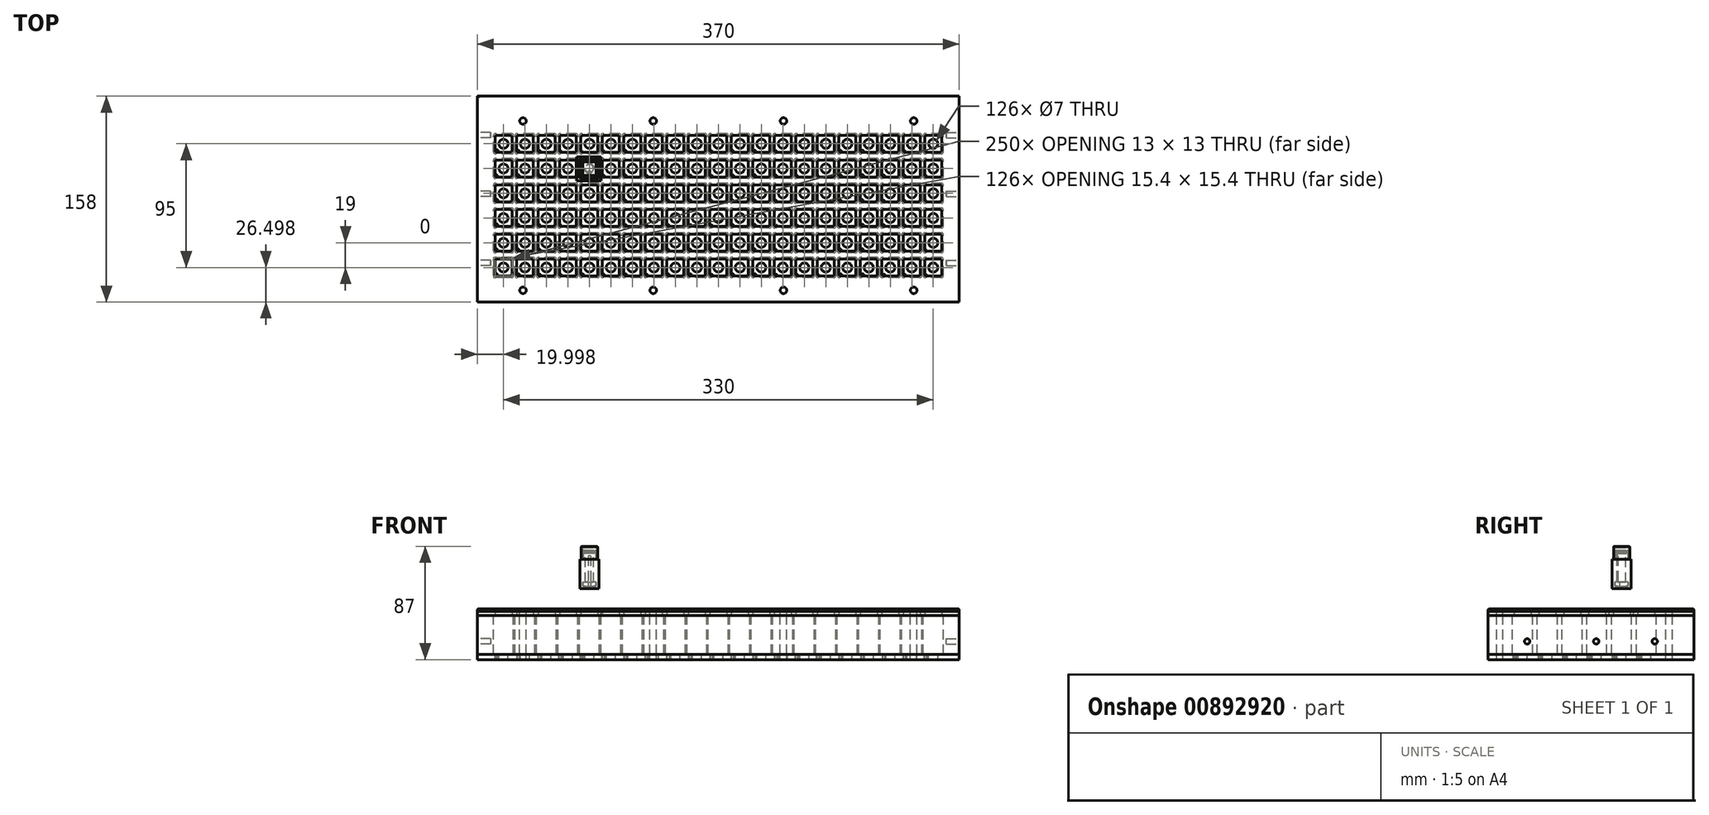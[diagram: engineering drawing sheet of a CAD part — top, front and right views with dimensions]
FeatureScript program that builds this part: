
annotation { "Feature Type Name" : "Feature", "Feature Type Description" : "" }
export const myFeature = defineFeature(function(context is Context, id is Id, definition is map)
    precondition{}
    {
        {
            var Q0;
            Q0=qCreatedBy(makeId("Top.planeOp"),FACE);
            var sketch = newSketch(context, id + "F0", { "sketchPlane" : qUnion([Q0])});
            skLineSegment(sketch, "E0.bottom", {"start": v(-181.07, -94.06) * mm, "end": v(188.93, -94.06) * mm});
            skLineSegment(sketch, "E0.top", {"start": v(-181.07, -252.06) * mm, "end": v(188.93, -252.06) * mm});
            skLineSegment(sketch, "E0.left", {"start": v(-181.07, -94.06) * mm, "end": v(-181.07, -252.06) * mm});
            skLineSegment(sketch, "E0.right", {"start": v(188.93, -94.06) * mm, "end": v(188.93, -252.06) * mm});
            skLineSegment(sketch, "E1.bottom", {"start": v(-167.57, -124.06) * mm, "end": v(175.43, -124.06) * mm, "construction": true});
            skLineSegment(sketch, "E1.top", {"start": v(-167.57, -232.06) * mm, "end": v(175.43, -232.06) * mm, "construction": true});
            skLineSegment(sketch, "E1.left", {"start": v(-167.57, -124.06) * mm, "end": v(-167.57, -232.06) * mm, "construction": true});
            skLineSegment(sketch, "E1.right", {"start": v(175.43, -124.06) * mm, "end": v(175.43, -232.06) * mm, "construction": true});
            skSolve(sketch);
        }
        {
            var Q0;
            Q0=makeQuery(id+"F0.imprint","IMPRINT",FACE,{"disambiguationData":[TD([[makeQuery(id+"F0.imprint","IMPRINT",EDGE,{"derivedFrom":sQuery(id+"F0.wireOp",EDGE,"E0.bottom")}),-1.0]])]});
            var sketch = newSketch(context, id + "F1", { "sketchPlane" : qUnion([Q0])});
            skLineSegment(sketch, "E2.bottom", {"start": v(-166.07, -124.06) * mm, "end": v(-156.07, -124.06) * mm});
            skLineSegment(sketch, "E2.top", {"start": v(-166.07, -137.06) * mm, "end": v(-156.07, -137.06) * mm});
            skLineSegment(sketch, "E2.left", {"start": v(-167.57, -125.56) * mm, "end": v(-167.57, -135.56) * mm});
            skLineSegment(sketch, "E2.right", {"start": v(-154.57, -125.56) * mm, "end": v(-154.57, -135.56) * mm});
            skLineSegment(sketch, "E3.bottom", {"start": v(-166.07, -219.06) * mm, "end": v(-156.07, -219.06) * mm});
            skLineSegment(sketch, "E3.top", {"start": v(-166.07, -232.06) * mm, "end": v(-156.07, -232.06) * mm});
            skLineSegment(sketch, "E3.left", {"start": v(-167.57, -220.56) * mm, "end": v(-167.57, -230.56) * mm});
            skLineSegment(sketch, "E3.right", {"start": v(-154.57, -220.56) * mm, "end": v(-154.57, -230.56) * mm});
            skLineSegment(sketch, "E4.bottom", {"start": v(-166.07, -200.06) * mm, "end": v(-156.07, -200.06) * mm});
            skLineSegment(sketch, "E4.top", {"start": v(-166.07, -213.06) * mm, "end": v(-156.07, -213.06) * mm});
            skLineSegment(sketch, "E4.left", {"start": v(-167.57, -201.56) * mm, "end": v(-167.57, -211.56) * mm});
            skLineSegment(sketch, "E4.right", {"start": v(-154.57, -201.56) * mm, "end": v(-154.57, -211.56) * mm});
            skLineSegment(sketch, "E5.bottom", {"start": v(-166.07, -181.06) * mm, "end": v(-156.07, -181.06) * mm});
            skLineSegment(sketch, "E5.top", {"start": v(-166.07, -194.06) * mm, "end": v(-156.07, -194.06) * mm});
            skLineSegment(sketch, "E5.left", {"start": v(-167.57, -182.56) * mm, "end": v(-167.57, -192.56) * mm});
            skLineSegment(sketch, "E5.right", {"start": v(-154.57, -182.56) * mm, "end": v(-154.57, -192.56) * mm});
            skLineSegment(sketch, "E6.bottom", {"start": v(-166.07, -162.06) * mm, "end": v(-156.07, -162.06) * mm});
            skLineSegment(sketch, "E6.top", {"start": v(-166.07, -175.06) * mm, "end": v(-156.07, -175.06) * mm});
            skLineSegment(sketch, "E6.left", {"start": v(-167.57, -163.56) * mm, "end": v(-167.57, -173.56) * mm});
            skLineSegment(sketch, "E6.right", {"start": v(-154.57, -163.56) * mm, "end": v(-154.57, -173.56) * mm});
            skLineSegment(sketch, "E7.bottom", {"start": v(-166.07, -143.06) * mm, "end": v(-156.07, -143.06) * mm});
            skLineSegment(sketch, "E7.top", {"start": v(-166.07, -156.06) * mm, "end": v(-156.07, -156.06) * mm});
            skLineSegment(sketch, "E7.left", {"start": v(-167.57, -144.56) * mm, "end": v(-167.57, -154.56) * mm});
            skLineSegment(sketch, "E7.right", {"start": v(-154.57, -144.56) * mm, "end": v(-154.57, -154.56) * mm});
            skLineSegment(sketch, "E8.bottom", {"start": v(-149.57, -124.06) * mm, "end": v(-139.57, -124.06) * mm});
            skLineSegment(sketch, "E8.top", {"start": v(-149.57, -137.06) * mm, "end": v(-139.57, -137.06) * mm});
            skLineSegment(sketch, "E8.left", {"start": v(-151.07, -125.56) * mm, "end": v(-151.07, -135.56) * mm});
            skLineSegment(sketch, "E8.right", {"start": v(-138.07, -125.56) * mm, "end": v(-138.07, -135.56) * mm});
            skLineSegment(sketch, "E9.bottom", {"start": v(-149.57, -219.06) * mm, "end": v(-139.57, -219.06) * mm});
            skLineSegment(sketch, "E9.top", {"start": v(-149.57, -232.06) * mm, "end": v(-139.57, -232.06) * mm});
            skLineSegment(sketch, "E9.left", {"start": v(-151.07, -220.56) * mm, "end": v(-151.07, -230.56) * mm});
            skLineSegment(sketch, "E9.right", {"start": v(-138.07, -220.56) * mm, "end": v(-138.07, -230.56) * mm});
            skLineSegment(sketch, "E10.bottom", {"start": v(-149.57, -200.06) * mm, "end": v(-139.57, -200.06) * mm});
            skLineSegment(sketch, "E10.top", {"start": v(-149.57, -213.06) * mm, "end": v(-139.57, -213.06) * mm});
            skLineSegment(sketch, "E10.left", {"start": v(-151.07, -201.56) * mm, "end": v(-151.07, -211.56) * mm});
            skLineSegment(sketch, "E10.right", {"start": v(-138.07, -201.56) * mm, "end": v(-138.07, -211.56) * mm});
            skLineSegment(sketch, "E11.bottom", {"start": v(-149.57, -181.06) * mm, "end": v(-139.57, -181.06) * mm});
            skLineSegment(sketch, "E11.top", {"start": v(-149.57, -194.06) * mm, "end": v(-139.57, -194.06) * mm});
            skLineSegment(sketch, "E11.left", {"start": v(-151.07, -182.56) * mm, "end": v(-151.07, -192.56) * mm});
            skLineSegment(sketch, "E11.right", {"start": v(-138.07, -182.56) * mm, "end": v(-138.07, -192.56) * mm});
            skLineSegment(sketch, "E12.bottom", {"start": v(-149.57, -162.06) * mm, "end": v(-139.57, -162.06) * mm});
            skLineSegment(sketch, "E12.top", {"start": v(-149.57, -175.06) * mm, "end": v(-139.57, -175.06) * mm});
            skLineSegment(sketch, "E12.left", {"start": v(-151.07, -163.56) * mm, "end": v(-151.07, -173.56) * mm});
            skLineSegment(sketch, "E12.right", {"start": v(-138.07, -163.56) * mm, "end": v(-138.07, -173.56) * mm});
            skLineSegment(sketch, "E13.bottom", {"start": v(-149.57, -143.06) * mm, "end": v(-139.57, -143.06) * mm});
            skLineSegment(sketch, "E13.top", {"start": v(-149.57, -156.06) * mm, "end": v(-139.57, -156.06) * mm});
            skLineSegment(sketch, "E13.left", {"start": v(-151.07, -144.56) * mm, "end": v(-151.07, -154.56) * mm});
            skLineSegment(sketch, "E13.right", {"start": v(-138.07, -144.56) * mm, "end": v(-138.07, -154.56) * mm});
            skLineSegment(sketch, "E14.bottom", {"start": v(-133.07, -124.06) * mm, "end": v(-123.07, -124.06) * mm});
            skLineSegment(sketch, "E14.top", {"start": v(-133.07, -137.06) * mm, "end": v(-123.07, -137.06) * mm});
            skLineSegment(sketch, "E14.left", {"start": v(-134.57, -125.56) * mm, "end": v(-134.57, -135.56) * mm});
            skLineSegment(sketch, "E14.right", {"start": v(-121.57, -125.56) * mm, "end": v(-121.57, -135.56) * mm});
            skLineSegment(sketch, "E15.bottom", {"start": v(-133.07, -219.06) * mm, "end": v(-123.07, -219.06) * mm});
            skLineSegment(sketch, "E15.top", {"start": v(-133.07, -232.06) * mm, "end": v(-123.07, -232.06) * mm});
            skLineSegment(sketch, "E15.left", {"start": v(-134.57, -220.56) * mm, "end": v(-134.57, -230.56) * mm});
            skLineSegment(sketch, "E15.right", {"start": v(-121.57, -220.56) * mm, "end": v(-121.57, -230.56) * mm});
            skLineSegment(sketch, "E16.bottom", {"start": v(-133.07, -200.06) * mm, "end": v(-123.07, -200.06) * mm});
            skLineSegment(sketch, "E16.top", {"start": v(-133.07, -213.06) * mm, "end": v(-123.07, -213.06) * mm});
            skLineSegment(sketch, "E16.left", {"start": v(-134.57, -201.56) * mm, "end": v(-134.57, -211.56) * mm});
            skLineSegment(sketch, "E16.right", {"start": v(-121.57, -201.56) * mm, "end": v(-121.57, -211.56) * mm});
            skLineSegment(sketch, "E17.bottom", {"start": v(-133.07, -181.06) * mm, "end": v(-123.07, -181.06) * mm});
            skLineSegment(sketch, "E17.top", {"start": v(-133.07, -194.06) * mm, "end": v(-123.07, -194.06) * mm});
            skLineSegment(sketch, "E17.left", {"start": v(-134.57, -182.56) * mm, "end": v(-134.57, -192.56) * mm});
            skLineSegment(sketch, "E17.right", {"start": v(-121.57, -182.56) * mm, "end": v(-121.57, -192.56) * mm});
            skLineSegment(sketch, "E18.bottom", {"start": v(-133.07, -162.06) * mm, "end": v(-123.07, -162.06) * mm});
            skLineSegment(sketch, "E18.top", {"start": v(-133.07, -175.06) * mm, "end": v(-123.07, -175.06) * mm});
            skLineSegment(sketch, "E18.left", {"start": v(-134.57, -163.56) * mm, "end": v(-134.57, -173.56) * mm});
            skLineSegment(sketch, "E18.right", {"start": v(-121.57, -163.56) * mm, "end": v(-121.57, -173.56) * mm});
            skLineSegment(sketch, "E19.bottom", {"start": v(-133.07, -143.06) * mm, "end": v(-123.07, -143.06) * mm});
            skLineSegment(sketch, "E19.top", {"start": v(-133.07, -156.06) * mm, "end": v(-123.07, -156.06) * mm});
            skLineSegment(sketch, "E19.left", {"start": v(-134.57, -144.56) * mm, "end": v(-134.57, -154.56) * mm});
            skLineSegment(sketch, "E19.right", {"start": v(-121.57, -144.56) * mm, "end": v(-121.57, -154.56) * mm});
            skLineSegment(sketch, "E20.bottom", {"start": v(-116.57, -124.06) * mm, "end": v(-106.57, -124.06) * mm});
            skLineSegment(sketch, "E20.top", {"start": v(-116.57, -137.06) * mm, "end": v(-106.57, -137.06) * mm});
            skLineSegment(sketch, "E20.left", {"start": v(-118.07, -125.56) * mm, "end": v(-118.07, -135.56) * mm});
            skLineSegment(sketch, "E20.right", {"start": v(-105.07, -125.56) * mm, "end": v(-105.07, -135.56) * mm});
            skLineSegment(sketch, "E21.bottom", {"start": v(-116.57, -219.06) * mm, "end": v(-106.57, -219.06) * mm});
            skLineSegment(sketch, "E21.top", {"start": v(-116.57, -232.06) * mm, "end": v(-106.57, -232.06) * mm});
            skLineSegment(sketch, "E21.left", {"start": v(-118.07, -220.56) * mm, "end": v(-118.07, -230.56) * mm});
            skLineSegment(sketch, "E21.right", {"start": v(-105.07, -220.56) * mm, "end": v(-105.07, -230.56) * mm});
            skLineSegment(sketch, "E22.bottom", {"start": v(-116.57, -200.06) * mm, "end": v(-106.57, -200.06) * mm});
            skLineSegment(sketch, "E22.top", {"start": v(-116.57, -213.06) * mm, "end": v(-106.57, -213.06) * mm});
            skLineSegment(sketch, "E22.left", {"start": v(-118.07, -201.56) * mm, "end": v(-118.07, -211.56) * mm});
            skLineSegment(sketch, "E22.right", {"start": v(-105.07, -201.56) * mm, "end": v(-105.07, -211.56) * mm});
            skLineSegment(sketch, "E23.bottom", {"start": v(-116.57, -181.06) * mm, "end": v(-106.57, -181.06) * mm});
            skLineSegment(sketch, "E23.top", {"start": v(-116.57, -194.06) * mm, "end": v(-106.57, -194.06) * mm});
            skLineSegment(sketch, "E23.left", {"start": v(-118.07, -182.56) * mm, "end": v(-118.07, -192.56) * mm});
            skLineSegment(sketch, "E23.right", {"start": v(-105.07, -182.56) * mm, "end": v(-105.07, -192.56) * mm});
            skLineSegment(sketch, "E24.bottom", {"start": v(-116.57, -162.06) * mm, "end": v(-106.57, -162.06) * mm});
            skLineSegment(sketch, "E24.top", {"start": v(-116.57, -175.06) * mm, "end": v(-106.57, -175.06) * mm});
            skLineSegment(sketch, "E24.left", {"start": v(-118.07, -163.56) * mm, "end": v(-118.07, -173.56) * mm});
            skLineSegment(sketch, "E24.right", {"start": v(-105.07, -163.56) * mm, "end": v(-105.07, -173.56) * mm});
            skLineSegment(sketch, "E25.bottom", {"start": v(-116.57, -143.06) * mm, "end": v(-106.57, -143.06) * mm});
            skLineSegment(sketch, "E25.top", {"start": v(-116.57, -156.06) * mm, "end": v(-106.57, -156.06) * mm});
            skLineSegment(sketch, "E25.left", {"start": v(-118.07, -144.56) * mm, "end": v(-118.07, -154.56) * mm});
            skLineSegment(sketch, "E25.right", {"start": v(-105.07, -144.56) * mm, "end": v(-105.07, -154.56) * mm});
            skLineSegment(sketch, "E26.bottom", {"start": v(-100.07, -124.06) * mm, "end": v(-90.07, -124.06) * mm});
            skLineSegment(sketch, "E26.top", {"start": v(-100.07, -137.06) * mm, "end": v(-90.07, -137.06) * mm});
            skLineSegment(sketch, "E26.left", {"start": v(-101.57, -125.56) * mm, "end": v(-101.57, -135.56) * mm});
            skLineSegment(sketch, "E26.right", {"start": v(-88.57, -125.56) * mm, "end": v(-88.57, -135.56) * mm});
            skLineSegment(sketch, "E27.bottom", {"start": v(-100.07, -219.06) * mm, "end": v(-90.07, -219.06) * mm});
            skLineSegment(sketch, "E27.top", {"start": v(-100.07, -232.06) * mm, "end": v(-90.07, -232.06) * mm});
            skLineSegment(sketch, "E27.left", {"start": v(-101.57, -220.56) * mm, "end": v(-101.57, -230.56) * mm});
            skLineSegment(sketch, "E27.right", {"start": v(-88.57, -220.56) * mm, "end": v(-88.57, -230.56) * mm});
            skLineSegment(sketch, "E28.bottom", {"start": v(-100.07, -200.06) * mm, "end": v(-90.07, -200.06) * mm});
            skLineSegment(sketch, "E28.top", {"start": v(-100.07, -213.06) * mm, "end": v(-90.07, -213.06) * mm});
            skLineSegment(sketch, "E28.left", {"start": v(-101.57, -201.56) * mm, "end": v(-101.57, -211.56) * mm});
            skLineSegment(sketch, "E28.right", {"start": v(-88.57, -201.56) * mm, "end": v(-88.57, -211.56) * mm});
            skLineSegment(sketch, "E29.bottom", {"start": v(-100.07, -181.06) * mm, "end": v(-90.07, -181.06) * mm});
            skLineSegment(sketch, "E29.top", {"start": v(-100.07, -194.06) * mm, "end": v(-90.07, -194.06) * mm});
            skLineSegment(sketch, "E29.left", {"start": v(-101.57, -182.56) * mm, "end": v(-101.57, -192.56) * mm});
            skLineSegment(sketch, "E29.right", {"start": v(-88.57, -182.56) * mm, "end": v(-88.57, -192.56) * mm});
            skLineSegment(sketch, "E30.bottom", {"start": v(-100.07, -162.06) * mm, "end": v(-90.07, -162.06) * mm});
            skLineSegment(sketch, "E30.top", {"start": v(-100.07, -175.06) * mm, "end": v(-90.07, -175.06) * mm});
            skLineSegment(sketch, "E30.left", {"start": v(-101.57, -163.56) * mm, "end": v(-101.57, -173.56) * mm});
            skLineSegment(sketch, "E30.right", {"start": v(-88.57, -163.56) * mm, "end": v(-88.57, -173.56) * mm});
            skLineSegment(sketch, "E31.bottom", {"start": v(-100.07, -143.06) * mm, "end": v(-90.07, -143.06) * mm});
            skLineSegment(sketch, "E31.top", {"start": v(-100.07, -156.06) * mm, "end": v(-90.07, -156.06) * mm});
            skLineSegment(sketch, "E31.left", {"start": v(-101.57, -144.56) * mm, "end": v(-101.57, -154.56) * mm});
            skLineSegment(sketch, "E31.right", {"start": v(-88.57, -144.56) * mm, "end": v(-88.57, -154.56) * mm});
            skLineSegment(sketch, "E32.bottom", {"start": v(-83.57, -124.06) * mm, "end": v(-73.57, -124.06) * mm});
            skLineSegment(sketch, "E32.top", {"start": v(-83.57, -137.06) * mm, "end": v(-73.57, -137.06) * mm});
            skLineSegment(sketch, "E32.left", {"start": v(-85.07, -125.56) * mm, "end": v(-85.07, -135.56) * mm});
            skLineSegment(sketch, "E32.right", {"start": v(-72.07, -125.56) * mm, "end": v(-72.07, -135.56) * mm});
            skLineSegment(sketch, "E33.bottom", {"start": v(-83.57, -219.06) * mm, "end": v(-73.57, -219.06) * mm});
            skLineSegment(sketch, "E33.top", {"start": v(-83.57, -232.06) * mm, "end": v(-73.57, -232.06) * mm});
            skLineSegment(sketch, "E33.left", {"start": v(-85.07, -220.56) * mm, "end": v(-85.07, -230.56) * mm});
            skLineSegment(sketch, "E33.right", {"start": v(-72.07, -220.56) * mm, "end": v(-72.07, -230.56) * mm});
            skLineSegment(sketch, "E34.bottom", {"start": v(-83.57, -200.06) * mm, "end": v(-73.57, -200.06) * mm});
            skLineSegment(sketch, "E34.top", {"start": v(-83.57, -213.06) * mm, "end": v(-73.57, -213.06) * mm});
            skLineSegment(sketch, "E34.left", {"start": v(-85.07, -201.56) * mm, "end": v(-85.07, -211.56) * mm});
            skLineSegment(sketch, "E34.right", {"start": v(-72.07, -201.56) * mm, "end": v(-72.07, -211.56) * mm});
            skLineSegment(sketch, "E35.bottom", {"start": v(-83.57, -181.06) * mm, "end": v(-73.57, -181.06) * mm});
            skLineSegment(sketch, "E35.top", {"start": v(-83.57, -194.06) * mm, "end": v(-73.57, -194.06) * mm});
            skLineSegment(sketch, "E35.left", {"start": v(-85.07, -182.56) * mm, "end": v(-85.07, -192.56) * mm});
            skLineSegment(sketch, "E35.right", {"start": v(-72.07, -182.56) * mm, "end": v(-72.07, -192.56) * mm});
            skLineSegment(sketch, "E36.bottom", {"start": v(-83.57, -162.06) * mm, "end": v(-73.57, -162.06) * mm});
            skLineSegment(sketch, "E36.top", {"start": v(-83.57, -175.06) * mm, "end": v(-73.57, -175.06) * mm});
            skLineSegment(sketch, "E36.left", {"start": v(-85.07, -163.56) * mm, "end": v(-85.07, -173.56) * mm});
            skLineSegment(sketch, "E36.right", {"start": v(-72.07, -163.56) * mm, "end": v(-72.07, -173.56) * mm});
            skLineSegment(sketch, "E37.bottom", {"start": v(-83.57, -143.06) * mm, "end": v(-73.57, -143.06) * mm});
            skLineSegment(sketch, "E37.top", {"start": v(-83.57, -156.06) * mm, "end": v(-73.57, -156.06) * mm});
            skLineSegment(sketch, "E37.left", {"start": v(-85.07, -144.56) * mm, "end": v(-85.07, -154.56) * mm});
            skLineSegment(sketch, "E37.right", {"start": v(-72.07, -144.56) * mm, "end": v(-72.07, -154.56) * mm});
            skLineSegment(sketch, "E38.bottom", {"start": v(-67.07, -124.06) * mm, "end": v(-57.07, -124.06) * mm});
            skLineSegment(sketch, "E38.top", {"start": v(-67.07, -137.06) * mm, "end": v(-57.07, -137.06) * mm});
            skLineSegment(sketch, "E38.left", {"start": v(-68.57, -125.56) * mm, "end": v(-68.57, -135.56) * mm});
            skLineSegment(sketch, "E38.right", {"start": v(-55.57, -125.56) * mm, "end": v(-55.57, -135.56) * mm});
            skLineSegment(sketch, "E39.bottom", {"start": v(-67.07, -219.06) * mm, "end": v(-57.07, -219.06) * mm});
            skLineSegment(sketch, "E39.top", {"start": v(-67.07, -232.06) * mm, "end": v(-57.07, -232.06) * mm});
            skLineSegment(sketch, "E39.left", {"start": v(-68.57, -220.56) * mm, "end": v(-68.57, -230.56) * mm});
            skLineSegment(sketch, "E39.right", {"start": v(-55.57, -220.56) * mm, "end": v(-55.57, -230.56) * mm});
            skLineSegment(sketch, "E40.bottom", {"start": v(-67.07, -200.06) * mm, "end": v(-57.07, -200.06) * mm});
            skLineSegment(sketch, "E40.top", {"start": v(-67.07, -213.06) * mm, "end": v(-57.07, -213.06) * mm});
            skLineSegment(sketch, "E40.left", {"start": v(-68.57, -201.56) * mm, "end": v(-68.57, -211.56) * mm});
            skLineSegment(sketch, "E40.right", {"start": v(-55.57, -201.56) * mm, "end": v(-55.57, -211.56) * mm});
            skLineSegment(sketch, "E41.bottom", {"start": v(-67.07, -181.06) * mm, "end": v(-57.07, -181.06) * mm});
            skLineSegment(sketch, "E41.top", {"start": v(-67.07, -194.06) * mm, "end": v(-57.07, -194.06) * mm});
            skLineSegment(sketch, "E41.left", {"start": v(-68.57, -182.56) * mm, "end": v(-68.57, -192.56) * mm});
            skLineSegment(sketch, "E41.right", {"start": v(-55.57, -182.56) * mm, "end": v(-55.57, -192.56) * mm});
            skLineSegment(sketch, "E42.bottom", {"start": v(-67.07, -162.06) * mm, "end": v(-57.07, -162.06) * mm});
            skLineSegment(sketch, "E42.top", {"start": v(-67.07, -175.06) * mm, "end": v(-57.07, -175.06) * mm});
            skLineSegment(sketch, "E42.left", {"start": v(-68.57, -163.56) * mm, "end": v(-68.57, -173.56) * mm});
            skLineSegment(sketch, "E42.right", {"start": v(-55.57, -163.56) * mm, "end": v(-55.57, -173.56) * mm});
            skLineSegment(sketch, "E43.bottom", {"start": v(-67.07, -143.06) * mm, "end": v(-57.07, -143.06) * mm});
            skLineSegment(sketch, "E43.top", {"start": v(-67.07, -156.06) * mm, "end": v(-57.07, -156.06) * mm});
            skLineSegment(sketch, "E43.left", {"start": v(-68.57, -144.56) * mm, "end": v(-68.57, -154.56) * mm});
            skLineSegment(sketch, "E43.right", {"start": v(-55.57, -144.56) * mm, "end": v(-55.57, -154.56) * mm});
            skLineSegment(sketch, "E44.bottom", {"start": v(-50.57, -124.06) * mm, "end": v(-40.57, -124.06) * mm});
            skLineSegment(sketch, "E44.top", {"start": v(-50.57, -137.06) * mm, "end": v(-40.57, -137.06) * mm});
            skLineSegment(sketch, "E44.left", {"start": v(-52.07, -125.56) * mm, "end": v(-52.07, -135.56) * mm});
            skLineSegment(sketch, "E44.right", {"start": v(-39.07, -125.56) * mm, "end": v(-39.07, -135.56) * mm});
            skLineSegment(sketch, "E45.bottom", {"start": v(-50.57, -219.06) * mm, "end": v(-40.57, -219.06) * mm});
            skLineSegment(sketch, "E45.top", {"start": v(-50.57, -232.06) * mm, "end": v(-40.57, -232.06) * mm});
            skLineSegment(sketch, "E45.left", {"start": v(-52.07, -220.56) * mm, "end": v(-52.07, -230.56) * mm});
            skLineSegment(sketch, "E45.right", {"start": v(-39.07, -220.56) * mm, "end": v(-39.07, -230.56) * mm});
            skLineSegment(sketch, "E46.bottom", {"start": v(-50.57, -200.06) * mm, "end": v(-40.57, -200.06) * mm});
            skLineSegment(sketch, "E46.top", {"start": v(-50.57, -213.06) * mm, "end": v(-40.57, -213.06) * mm});
            skLineSegment(sketch, "E46.left", {"start": v(-52.07, -201.56) * mm, "end": v(-52.07, -211.56) * mm});
            skLineSegment(sketch, "E46.right", {"start": v(-39.07, -201.56) * mm, "end": v(-39.07, -211.56) * mm});
            skLineSegment(sketch, "E47.bottom", {"start": v(-50.57, -181.06) * mm, "end": v(-40.57, -181.06) * mm});
            skLineSegment(sketch, "E47.top", {"start": v(-50.57, -194.06) * mm, "end": v(-40.57, -194.06) * mm});
            skLineSegment(sketch, "E47.left", {"start": v(-52.07, -182.56) * mm, "end": v(-52.07, -192.56) * mm});
            skLineSegment(sketch, "E47.right", {"start": v(-39.07, -182.56) * mm, "end": v(-39.07, -192.56) * mm});
            skLineSegment(sketch, "E48.bottom", {"start": v(-50.57, -162.06) * mm, "end": v(-40.57, -162.06) * mm});
            skLineSegment(sketch, "E48.top", {"start": v(-50.57, -175.06) * mm, "end": v(-40.57, -175.06) * mm});
            skLineSegment(sketch, "E48.left", {"start": v(-52.07, -163.56) * mm, "end": v(-52.07, -173.56) * mm});
            skLineSegment(sketch, "E48.right", {"start": v(-39.07, -163.56) * mm, "end": v(-39.07, -173.56) * mm});
            skLineSegment(sketch, "E49.bottom", {"start": v(-50.57, -143.06) * mm, "end": v(-40.57, -143.06) * mm});
            skLineSegment(sketch, "E49.top", {"start": v(-50.57, -156.06) * mm, "end": v(-40.57, -156.06) * mm});
            skLineSegment(sketch, "E49.left", {"start": v(-52.07, -144.56) * mm, "end": v(-52.07, -154.56) * mm});
            skLineSegment(sketch, "E49.right", {"start": v(-39.07, -144.56) * mm, "end": v(-39.07, -154.56) * mm});
            skLineSegment(sketch, "E50.bottom", {"start": v(-34.07, -124.06) * mm, "end": v(-24.07, -124.06) * mm});
            skLineSegment(sketch, "E50.top", {"start": v(-34.07, -137.06) * mm, "end": v(-24.07, -137.06) * mm});
            skLineSegment(sketch, "E50.left", {"start": v(-35.57, -125.56) * mm, "end": v(-35.57, -135.56) * mm});
            skLineSegment(sketch, "E50.right", {"start": v(-22.57, -125.56) * mm, "end": v(-22.57, -135.56) * mm});
            skLineSegment(sketch, "E51.bottom", {"start": v(-34.07, -219.06) * mm, "end": v(-24.07, -219.06) * mm});
            skLineSegment(sketch, "E51.top", {"start": v(-34.07, -232.06) * mm, "end": v(-24.07, -232.06) * mm});
            skLineSegment(sketch, "E51.left", {"start": v(-35.57, -220.56) * mm, "end": v(-35.57, -230.56) * mm});
            skLineSegment(sketch, "E51.right", {"start": v(-22.57, -220.56) * mm, "end": v(-22.57, -230.56) * mm});
            skLineSegment(sketch, "E52.bottom", {"start": v(-34.07, -200.06) * mm, "end": v(-24.07, -200.06) * mm});
            skLineSegment(sketch, "E52.top", {"start": v(-34.07, -213.06) * mm, "end": v(-24.07, -213.06) * mm});
            skLineSegment(sketch, "E52.left", {"start": v(-35.57, -201.56) * mm, "end": v(-35.57, -211.56) * mm});
            skLineSegment(sketch, "E52.right", {"start": v(-22.57, -201.56) * mm, "end": v(-22.57, -211.56) * mm});
            skLineSegment(sketch, "E53.bottom", {"start": v(-34.07, -181.06) * mm, "end": v(-24.07, -181.06) * mm});
            skLineSegment(sketch, "E53.top", {"start": v(-34.07, -194.06) * mm, "end": v(-24.07, -194.06) * mm});
            skLineSegment(sketch, "E53.left", {"start": v(-35.57, -182.56) * mm, "end": v(-35.57, -192.56) * mm});
            skLineSegment(sketch, "E53.right", {"start": v(-22.57, -182.56) * mm, "end": v(-22.57, -192.56) * mm});
            skLineSegment(sketch, "E54.bottom", {"start": v(-34.07, -162.06) * mm, "end": v(-24.07, -162.06) * mm});
            skLineSegment(sketch, "E54.top", {"start": v(-34.07, -175.06) * mm, "end": v(-24.07, -175.06) * mm});
            skLineSegment(sketch, "E54.left", {"start": v(-35.57, -163.56) * mm, "end": v(-35.57, -173.56) * mm});
            skLineSegment(sketch, "E54.right", {"start": v(-22.57, -163.56) * mm, "end": v(-22.57, -173.56) * mm});
            skLineSegment(sketch, "E55.bottom", {"start": v(-34.07, -143.06) * mm, "end": v(-24.07, -143.06) * mm});
            skLineSegment(sketch, "E55.top", {"start": v(-34.07, -156.06) * mm, "end": v(-24.07, -156.06) * mm});
            skLineSegment(sketch, "E55.left", {"start": v(-35.57, -144.56) * mm, "end": v(-35.57, -154.56) * mm});
            skLineSegment(sketch, "E55.right", {"start": v(-22.57, -144.56) * mm, "end": v(-22.57, -154.56) * mm});
            skLineSegment(sketch, "E56.bottom", {"start": v(-17.57, -124.06) * mm, "end": v(-7.57, -124.06) * mm});
            skLineSegment(sketch, "E56.top", {"start": v(-17.57, -137.06) * mm, "end": v(-7.57, -137.06) * mm});
            skLineSegment(sketch, "E56.left", {"start": v(-19.07, -125.56) * mm, "end": v(-19.07, -135.56) * mm});
            skLineSegment(sketch, "E56.right", {"start": v(-6.07, -125.56) * mm, "end": v(-6.07, -135.56) * mm});
            skLineSegment(sketch, "E57.bottom", {"start": v(-17.57, -219.06) * mm, "end": v(-7.57, -219.06) * mm});
            skLineSegment(sketch, "E57.top", {"start": v(-17.57, -232.06) * mm, "end": v(-7.57, -232.06) * mm});
            skLineSegment(sketch, "E57.left", {"start": v(-19.07, -220.56) * mm, "end": v(-19.07, -230.56) * mm});
            skLineSegment(sketch, "E57.right", {"start": v(-6.07, -220.56) * mm, "end": v(-6.07, -230.56) * mm});
            skLineSegment(sketch, "E58.bottom", {"start": v(-17.57, -200.06) * mm, "end": v(-7.57, -200.06) * mm});
            skLineSegment(sketch, "E58.top", {"start": v(-17.57, -213.06) * mm, "end": v(-7.57, -213.06) * mm});
            skLineSegment(sketch, "E58.left", {"start": v(-19.07, -201.56) * mm, "end": v(-19.07, -211.56) * mm});
            skLineSegment(sketch, "E58.right", {"start": v(-6.07, -201.56) * mm, "end": v(-6.07, -211.56) * mm});
            skLineSegment(sketch, "E59.bottom", {"start": v(-17.57, -181.06) * mm, "end": v(-7.57, -181.06) * mm});
            skLineSegment(sketch, "E59.top", {"start": v(-17.57, -194.06) * mm, "end": v(-7.57, -194.06) * mm});
            skLineSegment(sketch, "E59.left", {"start": v(-19.07, -182.56) * mm, "end": v(-19.07, -192.56) * mm});
            skLineSegment(sketch, "E59.right", {"start": v(-6.07, -182.56) * mm, "end": v(-6.07, -192.56) * mm});
            skLineSegment(sketch, "E60.bottom", {"start": v(-17.57, -162.06) * mm, "end": v(-7.57, -162.06) * mm});
            skLineSegment(sketch, "E60.top", {"start": v(-17.57, -175.06) * mm, "end": v(-7.57, -175.06) * mm});
            skLineSegment(sketch, "E60.left", {"start": v(-19.07, -163.56) * mm, "end": v(-19.07, -173.56) * mm});
            skLineSegment(sketch, "E60.right", {"start": v(-6.07, -163.56) * mm, "end": v(-6.07, -173.56) * mm});
            skLineSegment(sketch, "E61.bottom", {"start": v(-17.57, -143.06) * mm, "end": v(-7.57, -143.06) * mm});
            skLineSegment(sketch, "E61.top", {"start": v(-17.57, -156.06) * mm, "end": v(-7.57, -156.06) * mm});
            skLineSegment(sketch, "E61.left", {"start": v(-19.07, -144.56) * mm, "end": v(-19.07, -154.56) * mm});
            skLineSegment(sketch, "E61.right", {"start": v(-6.07, -144.56) * mm, "end": v(-6.07, -154.56) * mm});
            skLineSegment(sketch, "E62.bottom", {"start": v(-1.07, -124.06) * mm, "end": v(8.93, -124.06) * mm});
            skLineSegment(sketch, "E62.top", {"start": v(-1.07, -137.06) * mm, "end": v(8.93, -137.06) * mm});
            skLineSegment(sketch, "E62.left", {"start": v(-2.57, -125.56) * mm, "end": v(-2.57, -135.56) * mm});
            skLineSegment(sketch, "E62.right", {"start": v(10.43, -125.56) * mm, "end": v(10.43, -135.56) * mm});
            skLineSegment(sketch, "E63.bottom", {"start": v(-1.07, -219.06) * mm, "end": v(8.93, -219.06) * mm});
            skLineSegment(sketch, "E63.top", {"start": v(-1.07, -232.06) * mm, "end": v(8.93, -232.06) * mm});
            skLineSegment(sketch, "E63.left", {"start": v(-2.57, -220.56) * mm, "end": v(-2.57, -230.56) * mm});
            skLineSegment(sketch, "E63.right", {"start": v(10.43, -220.56) * mm, "end": v(10.43, -230.56) * mm});
            skLineSegment(sketch, "E64.bottom", {"start": v(-1.07, -200.06) * mm, "end": v(8.93, -200.06) * mm});
            skLineSegment(sketch, "E64.top", {"start": v(-1.07, -213.06) * mm, "end": v(8.93, -213.06) * mm});
            skLineSegment(sketch, "E64.left", {"start": v(-2.57, -201.56) * mm, "end": v(-2.57, -211.56) * mm});
            skLineSegment(sketch, "E64.right", {"start": v(10.43, -201.56) * mm, "end": v(10.43, -211.56) * mm});
            skLineSegment(sketch, "E65.bottom", {"start": v(-1.07, -181.06) * mm, "end": v(8.93, -181.06) * mm});
            skLineSegment(sketch, "E65.top", {"start": v(-1.07, -194.06) * mm, "end": v(8.93, -194.06) * mm});
            skLineSegment(sketch, "E65.left", {"start": v(-2.57, -182.56) * mm, "end": v(-2.57, -192.56) * mm});
            skLineSegment(sketch, "E65.right", {"start": v(10.43, -182.56) * mm, "end": v(10.43, -192.56) * mm});
            skLineSegment(sketch, "E66.bottom", {"start": v(-1.07, -162.06) * mm, "end": v(8.93, -162.06) * mm});
            skLineSegment(sketch, "E66.top", {"start": v(-1.07, -175.06) * mm, "end": v(8.93, -175.06) * mm});
            skLineSegment(sketch, "E66.left", {"start": v(-2.57, -163.56) * mm, "end": v(-2.57, -173.56) * mm});
            skLineSegment(sketch, "E66.right", {"start": v(10.43, -163.56) * mm, "end": v(10.43, -173.56) * mm});
            skLineSegment(sketch, "E67.bottom", {"start": v(-1.07, -143.06) * mm, "end": v(8.93, -143.06) * mm});
            skLineSegment(sketch, "E67.top", {"start": v(-1.07, -156.06) * mm, "end": v(8.93, -156.06) * mm});
            skLineSegment(sketch, "E67.left", {"start": v(-2.57, -144.56) * mm, "end": v(-2.57, -154.56) * mm});
            skLineSegment(sketch, "E67.right", {"start": v(10.43, -144.56) * mm, "end": v(10.43, -154.56) * mm});
            skLineSegment(sketch, "E68.bottom", {"start": v(15.43, -124.06) * mm, "end": v(25.43, -124.06) * mm});
            skLineSegment(sketch, "E68.top", {"start": v(15.43, -137.06) * mm, "end": v(25.43, -137.06) * mm});
            skLineSegment(sketch, "E68.left", {"start": v(13.93, -125.56) * mm, "end": v(13.93, -135.56) * mm});
            skLineSegment(sketch, "E68.right", {"start": v(26.93, -125.56) * mm, "end": v(26.93, -135.56) * mm});
            skLineSegment(sketch, "E69.bottom", {"start": v(15.43, -219.06) * mm, "end": v(25.43, -219.06) * mm});
            skLineSegment(sketch, "E69.top", {"start": v(15.43, -232.06) * mm, "end": v(25.43, -232.06) * mm});
            skLineSegment(sketch, "E69.left", {"start": v(13.93, -220.56) * mm, "end": v(13.93, -230.56) * mm});
            skLineSegment(sketch, "E69.right", {"start": v(26.93, -220.56) * mm, "end": v(26.93, -230.56) * mm});
            skLineSegment(sketch, "E70.bottom", {"start": v(15.43, -200.06) * mm, "end": v(25.43, -200.06) * mm});
            skLineSegment(sketch, "E70.top", {"start": v(15.43, -213.06) * mm, "end": v(25.43, -213.06) * mm});
            skLineSegment(sketch, "E70.left", {"start": v(13.93, -201.56) * mm, "end": v(13.93, -211.56) * mm});
            skLineSegment(sketch, "E70.right", {"start": v(26.93, -201.56) * mm, "end": v(26.93, -211.56) * mm});
            skLineSegment(sketch, "E71.bottom", {"start": v(15.43, -181.06) * mm, "end": v(25.43, -181.06) * mm});
            skLineSegment(sketch, "E71.top", {"start": v(15.43, -194.06) * mm, "end": v(25.43, -194.06) * mm});
            skLineSegment(sketch, "E71.left", {"start": v(13.93, -182.56) * mm, "end": v(13.93, -192.56) * mm});
            skLineSegment(sketch, "E71.right", {"start": v(26.93, -182.56) * mm, "end": v(26.93, -192.56) * mm});
            skLineSegment(sketch, "E72.bottom", {"start": v(15.43, -162.06) * mm, "end": v(25.43, -162.06) * mm});
            skLineSegment(sketch, "E72.top", {"start": v(15.43, -175.06) * mm, "end": v(25.43, -175.06) * mm});
            skLineSegment(sketch, "E72.left", {"start": v(13.93, -163.56) * mm, "end": v(13.93, -173.56) * mm});
            skLineSegment(sketch, "E72.right", {"start": v(26.93, -163.56) * mm, "end": v(26.93, -173.56) * mm});
            skLineSegment(sketch, "E73.bottom", {"start": v(15.43, -143.06) * mm, "end": v(25.43, -143.06) * mm});
            skLineSegment(sketch, "E73.top", {"start": v(15.43, -156.06) * mm, "end": v(25.43, -156.06) * mm});
            skLineSegment(sketch, "E73.left", {"start": v(13.93, -144.56) * mm, "end": v(13.93, -154.56) * mm});
            skLineSegment(sketch, "E73.right", {"start": v(26.93, -144.56) * mm, "end": v(26.93, -154.56) * mm});
            skLineSegment(sketch, "E74.bottom", {"start": v(31.93, -124.06) * mm, "end": v(41.93, -124.06) * mm});
            skLineSegment(sketch, "E74.top", {"start": v(31.93, -137.06) * mm, "end": v(41.93, -137.06) * mm});
            skLineSegment(sketch, "E74.left", {"start": v(30.43, -125.56) * mm, "end": v(30.43, -135.56) * mm});
            skLineSegment(sketch, "E74.right", {"start": v(43.43, -125.56) * mm, "end": v(43.43, -135.56) * mm});
            skLineSegment(sketch, "E75.bottom", {"start": v(31.93, -219.06) * mm, "end": v(41.93, -219.06) * mm});
            skLineSegment(sketch, "E75.top", {"start": v(31.93, -232.06) * mm, "end": v(41.93, -232.06) * mm});
            skLineSegment(sketch, "E75.left", {"start": v(30.43, -220.56) * mm, "end": v(30.43, -230.56) * mm});
            skLineSegment(sketch, "E75.right", {"start": v(43.43, -220.56) * mm, "end": v(43.43, -230.56) * mm});
            skLineSegment(sketch, "E76.bottom", {"start": v(31.93, -200.06) * mm, "end": v(41.93, -200.06) * mm});
            skLineSegment(sketch, "E76.top", {"start": v(31.93, -213.06) * mm, "end": v(41.93, -213.06) * mm});
            skLineSegment(sketch, "E76.left", {"start": v(30.43, -201.56) * mm, "end": v(30.43, -211.56) * mm});
            skLineSegment(sketch, "E76.right", {"start": v(43.43, -201.56) * mm, "end": v(43.43, -211.56) * mm});
            skLineSegment(sketch, "E77.bottom", {"start": v(31.93, -181.06) * mm, "end": v(41.93, -181.06) * mm});
            skLineSegment(sketch, "E77.top", {"start": v(31.93, -194.06) * mm, "end": v(41.93, -194.06) * mm});
            skLineSegment(sketch, "E77.left", {"start": v(30.43, -182.56) * mm, "end": v(30.43, -192.56) * mm});
            skLineSegment(sketch, "E77.right", {"start": v(43.43, -182.56) * mm, "end": v(43.43, -192.56) * mm});
            skLineSegment(sketch, "E78.bottom", {"start": v(31.93, -162.06) * mm, "end": v(41.93, -162.06) * mm});
            skLineSegment(sketch, "E78.top", {"start": v(31.93, -175.06) * mm, "end": v(41.93, -175.06) * mm});
            skLineSegment(sketch, "E78.left", {"start": v(30.43, -163.56) * mm, "end": v(30.43, -173.56) * mm});
            skLineSegment(sketch, "E78.right", {"start": v(43.43, -163.56) * mm, "end": v(43.43, -173.56) * mm});
            skLineSegment(sketch, "E79.bottom", {"start": v(31.93, -143.06) * mm, "end": v(41.93, -143.06) * mm});
            skLineSegment(sketch, "E79.top", {"start": v(31.93, -156.06) * mm, "end": v(41.93, -156.06) * mm});
            skLineSegment(sketch, "E79.left", {"start": v(30.43, -144.56) * mm, "end": v(30.43, -154.56) * mm});
            skLineSegment(sketch, "E79.right", {"start": v(43.43, -144.56) * mm, "end": v(43.43, -154.56) * mm});
            skLineSegment(sketch, "E80.bottom", {"start": v(48.43, -124.06) * mm, "end": v(58.43, -124.06) * mm});
            skLineSegment(sketch, "E80.top", {"start": v(48.43, -137.06) * mm, "end": v(58.43, -137.06) * mm});
            skLineSegment(sketch, "E80.left", {"start": v(46.93, -125.56) * mm, "end": v(46.93, -135.56) * mm});
            skLineSegment(sketch, "E80.right", {"start": v(59.93, -125.56) * mm, "end": v(59.93, -135.56) * mm});
            skLineSegment(sketch, "E81.bottom", {"start": v(48.43, -219.06) * mm, "end": v(58.43, -219.06) * mm});
            skLineSegment(sketch, "E81.top", {"start": v(48.43, -232.06) * mm, "end": v(58.43, -232.06) * mm});
            skLineSegment(sketch, "E81.left", {"start": v(46.93, -220.56) * mm, "end": v(46.93, -230.56) * mm});
            skLineSegment(sketch, "E81.right", {"start": v(59.93, -220.56) * mm, "end": v(59.93, -230.56) * mm});
            skLineSegment(sketch, "E82.bottom", {"start": v(48.43, -200.06) * mm, "end": v(58.43, -200.06) * mm});
            skLineSegment(sketch, "E82.top", {"start": v(48.43, -213.06) * mm, "end": v(58.43, -213.06) * mm});
            skLineSegment(sketch, "E82.left", {"start": v(46.93, -201.56) * mm, "end": v(46.93, -211.56) * mm});
            skLineSegment(sketch, "E82.right", {"start": v(59.93, -201.56) * mm, "end": v(59.93, -211.56) * mm});
            skLineSegment(sketch, "E83.bottom", {"start": v(48.43, -181.06) * mm, "end": v(58.43, -181.06) * mm});
            skLineSegment(sketch, "E83.top", {"start": v(48.43, -194.06) * mm, "end": v(58.43, -194.06) * mm});
            skLineSegment(sketch, "E83.left", {"start": v(46.93, -182.56) * mm, "end": v(46.93, -192.56) * mm});
            skLineSegment(sketch, "E83.right", {"start": v(59.93, -182.56) * mm, "end": v(59.93, -192.56) * mm});
            skLineSegment(sketch, "E84.bottom", {"start": v(48.43, -162.06) * mm, "end": v(58.43, -162.06) * mm});
            skLineSegment(sketch, "E84.top", {"start": v(48.43, -175.06) * mm, "end": v(58.43, -175.06) * mm});
            skLineSegment(sketch, "E84.left", {"start": v(46.93, -163.56) * mm, "end": v(46.93, -173.56) * mm});
            skLineSegment(sketch, "E84.right", {"start": v(59.93, -163.56) * mm, "end": v(59.93, -173.56) * mm});
            skLineSegment(sketch, "E85.bottom", {"start": v(48.43, -143.06) * mm, "end": v(58.43, -143.06) * mm});
            skLineSegment(sketch, "E85.top", {"start": v(48.43, -156.06) * mm, "end": v(58.43, -156.06) * mm});
            skLineSegment(sketch, "E85.left", {"start": v(46.93, -144.56) * mm, "end": v(46.93, -154.56) * mm});
            skLineSegment(sketch, "E85.right", {"start": v(59.93, -144.56) * mm, "end": v(59.93, -154.56) * mm});
            skLineSegment(sketch, "E86.bottom", {"start": v(64.93, -124.06) * mm, "end": v(74.93, -124.06) * mm});
            skLineSegment(sketch, "E86.top", {"start": v(64.93, -137.06) * mm, "end": v(74.93, -137.06) * mm});
            skLineSegment(sketch, "E86.left", {"start": v(63.43, -125.56) * mm, "end": v(63.43, -135.56) * mm});
            skLineSegment(sketch, "E86.right", {"start": v(76.43, -125.56) * mm, "end": v(76.43, -135.56) * mm});
            skLineSegment(sketch, "E87.bottom", {"start": v(64.93, -219.06) * mm, "end": v(74.93, -219.06) * mm});
            skLineSegment(sketch, "E87.top", {"start": v(64.93, -232.06) * mm, "end": v(74.93, -232.06) * mm});
            skLineSegment(sketch, "E87.left", {"start": v(63.43, -220.56) * mm, "end": v(63.43, -230.56) * mm});
            skLineSegment(sketch, "E87.right", {"start": v(76.43, -220.56) * mm, "end": v(76.43, -230.56) * mm});
            skLineSegment(sketch, "E88.bottom", {"start": v(64.93, -200.06) * mm, "end": v(74.93, -200.06) * mm});
            skLineSegment(sketch, "E88.top", {"start": v(64.93, -213.06) * mm, "end": v(74.93, -213.06) * mm});
            skLineSegment(sketch, "E88.left", {"start": v(63.43, -201.56) * mm, "end": v(63.43, -211.56) * mm});
            skLineSegment(sketch, "E88.right", {"start": v(76.43, -201.56) * mm, "end": v(76.43, -211.56) * mm});
            skLineSegment(sketch, "E89.bottom", {"start": v(64.93, -181.06) * mm, "end": v(74.93, -181.06) * mm});
            skLineSegment(sketch, "E89.top", {"start": v(64.93, -194.06) * mm, "end": v(74.93, -194.06) * mm});
            skLineSegment(sketch, "E89.left", {"start": v(63.43, -182.56) * mm, "end": v(63.43, -192.56) * mm});
            skLineSegment(sketch, "E89.right", {"start": v(76.43, -182.56) * mm, "end": v(76.43, -192.56) * mm});
            skLineSegment(sketch, "E90.bottom", {"start": v(64.93, -162.06) * mm, "end": v(74.93, -162.06) * mm});
            skLineSegment(sketch, "E90.top", {"start": v(64.93, -175.06) * mm, "end": v(74.93, -175.06) * mm});
            skLineSegment(sketch, "E90.left", {"start": v(63.43, -163.56) * mm, "end": v(63.43, -173.56) * mm});
            skLineSegment(sketch, "E90.right", {"start": v(76.43, -163.56) * mm, "end": v(76.43, -173.56) * mm});
            skLineSegment(sketch, "E91.bottom", {"start": v(64.93, -143.06) * mm, "end": v(74.93, -143.06) * mm});
            skLineSegment(sketch, "E91.top", {"start": v(64.93, -156.06) * mm, "end": v(74.93, -156.06) * mm});
            skLineSegment(sketch, "E91.left", {"start": v(63.43, -144.56) * mm, "end": v(63.43, -154.56) * mm});
            skLineSegment(sketch, "E91.right", {"start": v(76.43, -144.56) * mm, "end": v(76.43, -154.56) * mm});
            skLineSegment(sketch, "E92.bottom", {"start": v(81.43, -124.06) * mm, "end": v(91.43, -124.06) * mm});
            skLineSegment(sketch, "E92.top", {"start": v(81.43, -137.06) * mm, "end": v(91.43, -137.06) * mm});
            skLineSegment(sketch, "E92.left", {"start": v(79.93, -125.56) * mm, "end": v(79.93, -135.56) * mm});
            skLineSegment(sketch, "E92.right", {"start": v(92.93, -125.56) * mm, "end": v(92.93, -135.56) * mm});
            skLineSegment(sketch, "E93.bottom", {"start": v(81.43, -219.06) * mm, "end": v(91.43, -219.06) * mm});
            skLineSegment(sketch, "E93.top", {"start": v(81.43, -232.06) * mm, "end": v(91.43, -232.06) * mm});
            skLineSegment(sketch, "E93.left", {"start": v(79.93, -220.56) * mm, "end": v(79.93, -230.56) * mm});
            skLineSegment(sketch, "E93.right", {"start": v(92.93, -220.56) * mm, "end": v(92.93, -230.56) * mm});
            skLineSegment(sketch, "E94.bottom", {"start": v(81.43, -200.06) * mm, "end": v(91.43, -200.06) * mm});
            skLineSegment(sketch, "E94.top", {"start": v(81.43, -213.06) * mm, "end": v(91.43, -213.06) * mm});
            skLineSegment(sketch, "E94.left", {"start": v(79.93, -201.56) * mm, "end": v(79.93, -211.56) * mm});
            skLineSegment(sketch, "E94.right", {"start": v(92.93, -201.56) * mm, "end": v(92.93, -211.56) * mm});
            skLineSegment(sketch, "E95.bottom", {"start": v(81.43, -181.06) * mm, "end": v(91.43, -181.06) * mm});
            skLineSegment(sketch, "E95.top", {"start": v(81.43, -194.06) * mm, "end": v(91.43, -194.06) * mm});
            skLineSegment(sketch, "E95.left", {"start": v(79.93, -182.56) * mm, "end": v(79.93, -192.56) * mm});
            skLineSegment(sketch, "E95.right", {"start": v(92.93, -182.56) * mm, "end": v(92.93, -192.56) * mm});
            skLineSegment(sketch, "E96.bottom", {"start": v(81.43, -162.06) * mm, "end": v(91.43, -162.06) * mm});
            skLineSegment(sketch, "E96.top", {"start": v(81.43, -175.06) * mm, "end": v(91.43, -175.06) * mm});
            skLineSegment(sketch, "E96.left", {"start": v(79.93, -163.56) * mm, "end": v(79.93, -173.56) * mm});
            skLineSegment(sketch, "E96.right", {"start": v(92.93, -163.56) * mm, "end": v(92.93, -173.56) * mm});
            skLineSegment(sketch, "E97.bottom", {"start": v(81.43, -143.06) * mm, "end": v(91.43, -143.06) * mm});
            skLineSegment(sketch, "E97.top", {"start": v(81.43, -156.06) * mm, "end": v(91.43, -156.06) * mm});
            skLineSegment(sketch, "E97.left", {"start": v(79.93, -144.56) * mm, "end": v(79.93, -154.56) * mm});
            skLineSegment(sketch, "E97.right", {"start": v(92.93, -144.56) * mm, "end": v(92.93, -154.56) * mm});
            skLineSegment(sketch, "E98.bottom", {"start": v(97.93, -124.06) * mm, "end": v(107.93, -124.06) * mm});
            skLineSegment(sketch, "E98.top", {"start": v(97.93, -137.06) * mm, "end": v(107.93, -137.06) * mm});
            skLineSegment(sketch, "E98.left", {"start": v(96.43, -125.56) * mm, "end": v(96.43, -135.56) * mm});
            skLineSegment(sketch, "E98.right", {"start": v(109.43, -125.56) * mm, "end": v(109.43, -135.56) * mm});
            skLineSegment(sketch, "E99.bottom", {"start": v(97.93, -219.06) * mm, "end": v(107.93, -219.06) * mm});
            skLineSegment(sketch, "E99.top", {"start": v(97.93, -232.06) * mm, "end": v(107.93, -232.06) * mm});
            skLineSegment(sketch, "E99.left", {"start": v(96.43, -220.56) * mm, "end": v(96.43, -230.56) * mm});
            skLineSegment(sketch, "E99.right", {"start": v(109.43, -220.56) * mm, "end": v(109.43, -230.56) * mm});
            skLineSegment(sketch, "E100.bottom", {"start": v(97.93, -200.06) * mm, "end": v(107.93, -200.06) * mm});
            skLineSegment(sketch, "E100.top", {"start": v(97.93, -213.06) * mm, "end": v(107.93, -213.06) * mm});
            skLineSegment(sketch, "E100.left", {"start": v(96.43, -201.56) * mm, "end": v(96.43, -211.56) * mm});
            skLineSegment(sketch, "E100.right", {"start": v(109.43, -201.56) * mm, "end": v(109.43, -211.56) * mm});
            skLineSegment(sketch, "E101.bottom", {"start": v(97.93, -181.06) * mm, "end": v(107.93, -181.06) * mm});
            skLineSegment(sketch, "E101.top", {"start": v(97.93, -194.06) * mm, "end": v(107.93, -194.06) * mm});
            skLineSegment(sketch, "E101.left", {"start": v(96.43, -182.56) * mm, "end": v(96.43, -192.56) * mm});
            skLineSegment(sketch, "E101.right", {"start": v(109.43, -182.56) * mm, "end": v(109.43, -192.56) * mm});
            skLineSegment(sketch, "E102.bottom", {"start": v(97.93, -162.06) * mm, "end": v(107.93, -162.06) * mm});
            skLineSegment(sketch, "E102.top", {"start": v(97.93, -175.06) * mm, "end": v(107.93, -175.06) * mm});
            skLineSegment(sketch, "E102.left", {"start": v(96.43, -163.56) * mm, "end": v(96.43, -173.56) * mm});
            skLineSegment(sketch, "E102.right", {"start": v(109.43, -163.56) * mm, "end": v(109.43, -173.56) * mm});
            skLineSegment(sketch, "E103.bottom", {"start": v(97.93, -143.06) * mm, "end": v(107.93, -143.06) * mm});
            skLineSegment(sketch, "E103.top", {"start": v(97.93, -156.06) * mm, "end": v(107.93, -156.06) * mm});
            skLineSegment(sketch, "E103.left", {"start": v(96.43, -144.56) * mm, "end": v(96.43, -154.56) * mm});
            skLineSegment(sketch, "E103.right", {"start": v(109.43, -144.56) * mm, "end": v(109.43, -154.56) * mm});
            skLineSegment(sketch, "E104.bottom", {"start": v(114.43, -124.06) * mm, "end": v(124.43, -124.06) * mm});
            skLineSegment(sketch, "E104.top", {"start": v(114.43, -137.06) * mm, "end": v(124.43, -137.06) * mm});
            skLineSegment(sketch, "E104.left", {"start": v(112.93, -125.56) * mm, "end": v(112.93, -135.56) * mm});
            skLineSegment(sketch, "E104.right", {"start": v(125.93, -125.56) * mm, "end": v(125.93, -135.56) * mm});
            skLineSegment(sketch, "E105.bottom", {"start": v(114.43, -219.06) * mm, "end": v(124.43, -219.06) * mm});
            skLineSegment(sketch, "E105.top", {"start": v(114.43, -232.06) * mm, "end": v(124.43, -232.06) * mm});
            skLineSegment(sketch, "E105.left", {"start": v(112.93, -220.56) * mm, "end": v(112.93, -230.56) * mm});
            skLineSegment(sketch, "E105.right", {"start": v(125.93, -220.56) * mm, "end": v(125.93, -230.56) * mm});
            skLineSegment(sketch, "E106.bottom", {"start": v(114.43, -200.06) * mm, "end": v(124.43, -200.06) * mm});
            skLineSegment(sketch, "E106.top", {"start": v(114.43, -213.06) * mm, "end": v(124.43, -213.06) * mm});
            skLineSegment(sketch, "E106.left", {"start": v(112.93, -201.56) * mm, "end": v(112.93, -211.56) * mm});
            skLineSegment(sketch, "E106.right", {"start": v(125.93, -201.56) * mm, "end": v(125.93, -211.56) * mm});
            skLineSegment(sketch, "E107.bottom", {"start": v(114.43, -181.06) * mm, "end": v(124.43, -181.06) * mm});
            skLineSegment(sketch, "E107.top", {"start": v(114.43, -194.06) * mm, "end": v(124.43, -194.06) * mm});
            skLineSegment(sketch, "E107.left", {"start": v(112.93, -182.56) * mm, "end": v(112.93, -192.56) * mm});
            skLineSegment(sketch, "E107.right", {"start": v(125.93, -182.56) * mm, "end": v(125.93, -192.56) * mm});
            skLineSegment(sketch, "E108.bottom", {"start": v(114.43, -162.06) * mm, "end": v(124.43, -162.06) * mm});
            skLineSegment(sketch, "E108.top", {"start": v(114.43, -175.06) * mm, "end": v(124.43, -175.06) * mm});
            skLineSegment(sketch, "E108.left", {"start": v(112.93, -163.56) * mm, "end": v(112.93, -173.56) * mm});
            skLineSegment(sketch, "E108.right", {"start": v(125.93, -163.56) * mm, "end": v(125.93, -173.56) * mm});
            skLineSegment(sketch, "E109.bottom", {"start": v(114.43, -143.06) * mm, "end": v(124.43, -143.06) * mm});
            skLineSegment(sketch, "E109.top", {"start": v(114.43, -156.06) * mm, "end": v(124.43, -156.06) * mm});
            skLineSegment(sketch, "E109.left", {"start": v(112.93, -144.56) * mm, "end": v(112.93, -154.56) * mm});
            skLineSegment(sketch, "E109.right", {"start": v(125.93, -144.56) * mm, "end": v(125.93, -154.56) * mm});
            skLineSegment(sketch, "E110.bottom", {"start": v(130.93, -124.06) * mm, "end": v(140.93, -124.06) * mm});
            skLineSegment(sketch, "E110.top", {"start": v(130.93, -137.06) * mm, "end": v(140.93, -137.06) * mm});
            skLineSegment(sketch, "E110.left", {"start": v(129.43, -125.56) * mm, "end": v(129.43, -135.56) * mm});
            skLineSegment(sketch, "E110.right", {"start": v(142.43, -125.56) * mm, "end": v(142.43, -135.56) * mm});
            skLineSegment(sketch, "E111.bottom", {"start": v(130.93, -219.06) * mm, "end": v(140.93, -219.06) * mm});
            skLineSegment(sketch, "E111.top", {"start": v(130.93, -232.06) * mm, "end": v(140.93, -232.06) * mm});
            skLineSegment(sketch, "E111.left", {"start": v(129.43, -220.56) * mm, "end": v(129.43, -230.56) * mm});
            skLineSegment(sketch, "E111.right", {"start": v(142.43, -220.56) * mm, "end": v(142.43, -230.56) * mm});
            skLineSegment(sketch, "E112.bottom", {"start": v(130.93, -200.06) * mm, "end": v(140.93, -200.06) * mm});
            skLineSegment(sketch, "E112.top", {"start": v(130.93, -213.06) * mm, "end": v(140.93, -213.06) * mm});
            skLineSegment(sketch, "E112.left", {"start": v(129.43, -201.56) * mm, "end": v(129.43, -211.56) * mm});
            skLineSegment(sketch, "E112.right", {"start": v(142.43, -201.56) * mm, "end": v(142.43, -211.56) * mm});
            skLineSegment(sketch, "E113.bottom", {"start": v(130.93, -181.06) * mm, "end": v(140.93, -181.06) * mm});
            skLineSegment(sketch, "E113.top", {"start": v(130.93, -194.06) * mm, "end": v(140.93, -194.06) * mm});
            skLineSegment(sketch, "E113.left", {"start": v(129.43, -182.56) * mm, "end": v(129.43, -192.56) * mm});
            skLineSegment(sketch, "E113.right", {"start": v(142.43, -182.56) * mm, "end": v(142.43, -192.56) * mm});
            skLineSegment(sketch, "E114.bottom", {"start": v(130.93, -162.06) * mm, "end": v(140.93, -162.06) * mm});
            skLineSegment(sketch, "E114.top", {"start": v(130.93, -175.06) * mm, "end": v(140.93, -175.06) * mm});
            skLineSegment(sketch, "E114.left", {"start": v(129.43, -163.56) * mm, "end": v(129.43, -173.56) * mm});
            skLineSegment(sketch, "E114.right", {"start": v(142.43, -163.56) * mm, "end": v(142.43, -173.56) * mm});
            skLineSegment(sketch, "E115.bottom", {"start": v(130.93, -143.06) * mm, "end": v(140.93, -143.06) * mm});
            skLineSegment(sketch, "E115.top", {"start": v(130.93, -156.06) * mm, "end": v(140.93, -156.06) * mm});
            skLineSegment(sketch, "E115.left", {"start": v(129.43, -144.56) * mm, "end": v(129.43, -154.56) * mm});
            skLineSegment(sketch, "E115.right", {"start": v(142.43, -144.56) * mm, "end": v(142.43, -154.56) * mm});
            skLineSegment(sketch, "E116.bottom", {"start": v(147.43, -124.06) * mm, "end": v(157.43, -124.06) * mm});
            skLineSegment(sketch, "E116.top", {"start": v(147.43, -137.06) * mm, "end": v(157.43, -137.06) * mm});
            skLineSegment(sketch, "E116.left", {"start": v(145.93, -125.56) * mm, "end": v(145.93, -135.56) * mm});
            skLineSegment(sketch, "E116.right", {"start": v(158.93, -125.56) * mm, "end": v(158.93, -135.56) * mm});
            skLineSegment(sketch, "E117.bottom", {"start": v(147.43, -219.06) * mm, "end": v(157.43, -219.06) * mm});
            skLineSegment(sketch, "E117.top", {"start": v(147.43, -232.06) * mm, "end": v(157.43, -232.06) * mm});
            skLineSegment(sketch, "E117.left", {"start": v(145.93, -220.56) * mm, "end": v(145.93, -230.56) * mm});
            skLineSegment(sketch, "E117.right", {"start": v(158.93, -220.56) * mm, "end": v(158.93, -230.56) * mm});
            skLineSegment(sketch, "E118.bottom", {"start": v(147.43, -200.06) * mm, "end": v(157.43, -200.06) * mm});
            skLineSegment(sketch, "E118.top", {"start": v(147.43, -213.06) * mm, "end": v(157.43, -213.06) * mm});
            skLineSegment(sketch, "E118.left", {"start": v(145.93, -201.56) * mm, "end": v(145.93, -211.56) * mm});
            skLineSegment(sketch, "E118.right", {"start": v(158.93, -201.56) * mm, "end": v(158.93, -211.56) * mm});
            skLineSegment(sketch, "E119.bottom", {"start": v(147.43, -181.06) * mm, "end": v(157.43, -181.06) * mm});
            skLineSegment(sketch, "E119.top", {"start": v(147.43, -194.06) * mm, "end": v(157.43, -194.06) * mm});
            skLineSegment(sketch, "E119.left", {"start": v(145.93, -182.56) * mm, "end": v(145.93, -192.56) * mm});
            skLineSegment(sketch, "E119.right", {"start": v(158.93, -182.56) * mm, "end": v(158.93, -192.56) * mm});
            skLineSegment(sketch, "E120.bottom", {"start": v(147.43, -162.06) * mm, "end": v(157.43, -162.06) * mm});
            skLineSegment(sketch, "E120.top", {"start": v(147.43, -175.06) * mm, "end": v(157.43, -175.06) * mm});
            skLineSegment(sketch, "E120.left", {"start": v(145.93, -163.56) * mm, "end": v(145.93, -173.56) * mm});
            skLineSegment(sketch, "E120.right", {"start": v(158.93, -163.56) * mm, "end": v(158.93, -173.56) * mm});
            skLineSegment(sketch, "E121.bottom", {"start": v(147.43, -143.06) * mm, "end": v(157.43, -143.06) * mm});
            skLineSegment(sketch, "E121.top", {"start": v(147.43, -156.06) * mm, "end": v(157.43, -156.06) * mm});
            skLineSegment(sketch, "E121.left", {"start": v(145.93, -144.56) * mm, "end": v(145.93, -154.56) * mm});
            skLineSegment(sketch, "E121.right", {"start": v(158.93, -144.56) * mm, "end": v(158.93, -154.56) * mm});
            skLineSegment(sketch, "E122.bottom", {"start": v(163.93, -124.06) * mm, "end": v(173.93, -124.06) * mm});
            skLineSegment(sketch, "E122.top", {"start": v(163.93, -137.06) * mm, "end": v(173.93, -137.06) * mm});
            skLineSegment(sketch, "E122.left", {"start": v(162.43, -125.56) * mm, "end": v(162.43, -135.56) * mm});
            skLineSegment(sketch, "E122.right", {"start": v(175.43, -125.56) * mm, "end": v(175.43, -135.56) * mm});
            skLineSegment(sketch, "E123.bottom", {"start": v(163.93, -219.06) * mm, "end": v(173.93, -219.06) * mm});
            skLineSegment(sketch, "E123.top", {"start": v(163.93, -232.06) * mm, "end": v(173.93, -232.06) * mm});
            skLineSegment(sketch, "E123.left", {"start": v(162.43, -220.56) * mm, "end": v(162.43, -230.56) * mm});
            skLineSegment(sketch, "E123.right", {"start": v(175.43, -220.56) * mm, "end": v(175.43, -230.56) * mm});
            skLineSegment(sketch, "E124.bottom", {"start": v(163.93, -200.06) * mm, "end": v(173.93, -200.06) * mm});
            skLineSegment(sketch, "E124.top", {"start": v(163.93, -213.06) * mm, "end": v(173.93, -213.06) * mm});
            skLineSegment(sketch, "E124.left", {"start": v(162.43, -201.56) * mm, "end": v(162.43, -211.56) * mm});
            skLineSegment(sketch, "E124.right", {"start": v(175.43, -201.56) * mm, "end": v(175.43, -211.56) * mm});
            skLineSegment(sketch, "E125.bottom", {"start": v(163.93, -181.06) * mm, "end": v(173.93, -181.06) * mm});
            skLineSegment(sketch, "E125.top", {"start": v(163.93, -194.06) * mm, "end": v(173.93, -194.06) * mm});
            skLineSegment(sketch, "E125.left", {"start": v(162.43, -182.56) * mm, "end": v(162.43, -192.56) * mm});
            skLineSegment(sketch, "E125.right", {"start": v(175.43, -182.56) * mm, "end": v(175.43, -192.56) * mm});
            skLineSegment(sketch, "E126.bottom", {"start": v(163.93, -162.06) * mm, "end": v(173.93, -162.06) * mm});
            skLineSegment(sketch, "E126.top", {"start": v(163.93, -175.06) * mm, "end": v(173.93, -175.06) * mm});
            skLineSegment(sketch, "E126.left", {"start": v(162.43, -163.56) * mm, "end": v(162.43, -173.56) * mm});
            skLineSegment(sketch, "E126.right", {"start": v(175.43, -163.56) * mm, "end": v(175.43, -173.56) * mm});
            skLineSegment(sketch, "E127.bottom", {"start": v(163.93, -143.06) * mm, "end": v(173.93, -143.06) * mm});
            skLineSegment(sketch, "E127.top", {"start": v(163.93, -156.06) * mm, "end": v(173.93, -156.06) * mm});
            skLineSegment(sketch, "E127.left", {"start": v(162.43, -144.56) * mm, "end": v(162.43, -154.56) * mm});
            skLineSegment(sketch, "E127.right", {"start": v(175.43, -144.56) * mm, "end": v(175.43, -154.56) * mm});
            skPoint(sketch, "E128.visualSharp", {"position": v(-167.57, -124.06) * mm});
            skArc(sketch, "E128.filletArc", {"start": v(-166.07, -124.06) * mm, "mid": v(-167.13, -124.5) * mm, "end": v(-167.57, -125.56) * mm});
            skPoint(sketch, "E129.visualSharp", {"position": v(-154.57, -124.06) * mm});
            skArc(sketch, "E129.filletArc", {"start": v(-154.57, -125.56) * mm, "mid": v(-155.01, -124.5) * mm, "end": v(-156.07, -124.06) * mm});
            skPoint(sketch, "E130.visualSharp", {"position": v(-154.57, -137.06) * mm});
            skArc(sketch, "E130.filletArc", {"start": v(-156.07, -137.06) * mm, "mid": v(-155.01, -136.62) * mm, "end": v(-154.57, -135.56) * mm});
            skPoint(sketch, "E131.visualSharp", {"position": v(-167.57, -137.06) * mm});
            skArc(sketch, "E131.filletArc", {"start": v(-167.57, -135.56) * mm, "mid": v(-167.13, -136.62) * mm, "end": v(-166.07, -137.06) * mm});
            skPoint(sketch, "E132.visualSharp", {"position": v(-167.57, -143.06) * mm});
            skArc(sketch, "E132.filletArc", {"start": v(-166.07, -143.06) * mm, "mid": v(-167.13, -143.5) * mm, "end": v(-167.57, -144.56) * mm});
            skPoint(sketch, "E133.visualSharp", {"position": v(-154.57, -143.06) * mm});
            skArc(sketch, "E133.filletArc", {"start": v(-154.57, -144.56) * mm, "mid": v(-155.01, -143.5) * mm, "end": v(-156.07, -143.06) * mm});
            skPoint(sketch, "E134.visualSharp", {"position": v(-167.57, -156.06) * mm});
            skArc(sketch, "E134.filletArc", {"start": v(-167.57, -154.56) * mm, "mid": v(-167.13, -155.62) * mm, "end": v(-166.07, -156.06) * mm});
            skPoint(sketch, "E135.visualSharp", {"position": v(-154.57, -156.06) * mm});
            skArc(sketch, "E135.filletArc", {"start": v(-156.07, -156.06) * mm, "mid": v(-155.01, -155.62) * mm, "end": v(-154.57, -154.56) * mm});
            skPoint(sketch, "E136.visualSharp", {"position": v(-167.57, -162.06) * mm});
            skArc(sketch, "E136.filletArc", {"start": v(-166.07, -162.06) * mm, "mid": v(-167.13, -162.5) * mm, "end": v(-167.57, -163.56) * mm});
            skPoint(sketch, "E137.visualSharp", {"position": v(-154.57, -162.06) * mm});
            skArc(sketch, "E137.filletArc", {"start": v(-154.57, -163.56) * mm, "mid": v(-155.01, -162.5) * mm, "end": v(-156.07, -162.06) * mm});
            skPoint(sketch, "E138.visualSharp", {"position": v(-154.57, -175.06) * mm});
            skArc(sketch, "E138.filletArc", {"start": v(-156.07, -175.06) * mm, "mid": v(-155.01, -174.62) * mm, "end": v(-154.57, -173.56) * mm});
            skPoint(sketch, "E139.visualSharp", {"position": v(-167.57, -175.06) * mm});
            skArc(sketch, "E139.filletArc", {"start": v(-167.57, -173.56) * mm, "mid": v(-167.13, -174.62) * mm, "end": v(-166.07, -175.06) * mm});
            skPoint(sketch, "E140.visualSharp", {"position": v(-167.57, -181.06) * mm});
            skArc(sketch, "E140.filletArc", {"start": v(-166.07, -181.06) * mm, "mid": v(-167.13, -181.5) * mm, "end": v(-167.57, -182.56) * mm});
            skPoint(sketch, "E141.visualSharp", {"position": v(-154.57, -181.06) * mm});
            skArc(sketch, "E141.filletArc", {"start": v(-154.57, -182.56) * mm, "mid": v(-155.01, -181.5) * mm, "end": v(-156.07, -181.06) * mm});
            skPoint(sketch, "E142.visualSharp", {"position": v(-167.57, -194.06) * mm});
            skArc(sketch, "E142.filletArc", {"start": v(-167.57, -192.56) * mm, "mid": v(-167.13, -193.62) * mm, "end": v(-166.07, -194.06) * mm});
            skPoint(sketch, "E143.visualSharp", {"position": v(-154.57, -194.06) * mm});
            skArc(sketch, "E143.filletArc", {"start": v(-156.07, -194.06) * mm, "mid": v(-155.01, -193.62) * mm, "end": v(-154.57, -192.56) * mm});
            skPoint(sketch, "E144.visualSharp", {"position": v(-167.57, -200.06) * mm});
            skArc(sketch, "E144.filletArc", {"start": v(-166.07, -200.06) * mm, "mid": v(-167.13, -200.5) * mm, "end": v(-167.57, -201.56) * mm});
            skPoint(sketch, "E145.visualSharp", {"position": v(-167.57, -213.06) * mm});
            skArc(sketch, "E145.filletArc", {"start": v(-167.57, -211.56) * mm, "mid": v(-167.13, -212.62) * mm, "end": v(-166.07, -213.06) * mm});
            skPoint(sketch, "E146.visualSharp", {"position": v(-154.57, -200.06) * mm});
            skArc(sketch, "E146.filletArc", {"start": v(-154.57, -201.56) * mm, "mid": v(-155.01, -200.5) * mm, "end": v(-156.07, -200.06) * mm});
            skPoint(sketch, "E147.visualSharp", {"position": v(-154.57, -213.06) * mm});
            skArc(sketch, "E147.filletArc", {"start": v(-156.07, -213.06) * mm, "mid": v(-155.01, -212.62) * mm, "end": v(-154.57, -211.56) * mm});
            skPoint(sketch, "E148.visualSharp", {"position": v(-167.57, -219.06) * mm});
            skArc(sketch, "E148.filletArc", {"start": v(-166.07, -219.06) * mm, "mid": v(-167.13, -219.5) * mm, "end": v(-167.57, -220.56) * mm});
            skPoint(sketch, "E149.visualSharp", {"position": v(-154.57, -219.06) * mm});
            skArc(sketch, "E149.filletArc", {"start": v(-154.57, -220.56) * mm, "mid": v(-155.01, -219.5) * mm, "end": v(-156.07, -219.06) * mm});
            skPoint(sketch, "E150.visualSharp", {"position": v(-167.57, -232.06) * mm});
            skArc(sketch, "E150.filletArc", {"start": v(-167.57, -230.56) * mm, "mid": v(-167.13, -231.62) * mm, "end": v(-166.07, -232.06) * mm});
            skPoint(sketch, "E151.visualSharp", {"position": v(-154.57, -232.06) * mm});
            skArc(sketch, "E151.filletArc", {"start": v(-156.07, -232.06) * mm, "mid": v(-155.01, -231.62) * mm, "end": v(-154.57, -230.56) * mm});
            skPoint(sketch, "E152.visualSharp", {"position": v(-151.07, -124.06) * mm});
            skArc(sketch, "E152.filletArc", {"start": v(-149.57, -124.06) * mm, "mid": v(-150.63, -124.5) * mm, "end": v(-151.07, -125.56) * mm});
            skPoint(sketch, "E153.visualSharp", {"position": v(-151.07, -137.06) * mm});
            skArc(sketch, "E153.filletArc", {"start": v(-151.07, -135.56) * mm, "mid": v(-150.63, -136.62) * mm, "end": v(-149.57, -137.06) * mm});
            skPoint(sketch, "E154.visualSharp", {"position": v(-138.07, -124.06) * mm});
            skArc(sketch, "E154.filletArc", {"start": v(-138.07, -125.56) * mm, "mid": v(-138.51, -124.5) * mm, "end": v(-139.57, -124.06) * mm});
            skPoint(sketch, "E155.visualSharp", {"position": v(-138.07, -137.06) * mm});
            skArc(sketch, "E155.filletArc", {"start": v(-139.57, -137.06) * mm, "mid": v(-138.51, -136.62) * mm, "end": v(-138.07, -135.56) * mm});
            skPoint(sketch, "E156.visualSharp", {"position": v(-151.07, -143.06) * mm});
            skArc(sketch, "E156.filletArc", {"start": v(-149.57, -143.06) * mm, "mid": v(-150.63, -143.5) * mm, "end": v(-151.07, -144.56) * mm});
            skPoint(sketch, "E157.visualSharp", {"position": v(-138.07, -143.06) * mm});
            skArc(sketch, "E157.filletArc", {"start": v(-138.07, -144.56) * mm, "mid": v(-138.51, -143.5) * mm, "end": v(-139.57, -143.06) * mm});
            skPoint(sketch, "E158.visualSharp", {"position": v(-151.07, -156.06) * mm});
            skArc(sketch, "E158.filletArc", {"start": v(-151.07, -154.56) * mm, "mid": v(-150.63, -155.62) * mm, "end": v(-149.57, -156.06) * mm});
            skPoint(sketch, "E159.visualSharp", {"position": v(-138.07, -156.06) * mm});
            skArc(sketch, "E159.filletArc", {"start": v(-139.57, -156.06) * mm, "mid": v(-138.51, -155.62) * mm, "end": v(-138.07, -154.56) * mm});
            skPoint(sketch, "E160.visualSharp", {"position": v(-138.07, -162.06) * mm});
            skArc(sketch, "E160.filletArc", {"start": v(-138.07, -163.56) * mm, "mid": v(-138.51, -162.5) * mm, "end": v(-139.57, -162.06) * mm});
            skPoint(sketch, "E161.visualSharp", {"position": v(-138.07, -175.06) * mm});
            skArc(sketch, "E161.filletArc", {"start": v(-139.57, -175.06) * mm, "mid": v(-138.51, -174.62) * mm, "end": v(-138.07, -173.56) * mm});
            skPoint(sketch, "E162.visualSharp", {"position": v(-151.07, -175.06) * mm});
            skArc(sketch, "E162.filletArc", {"start": v(-151.07, -173.56) * mm, "mid": v(-150.63, -174.62) * mm, "end": v(-149.57, -175.06) * mm});
            skPoint(sketch, "E163.visualSharp", {"position": v(-151.07, -162.06) * mm});
            skArc(sketch, "E163.filletArc", {"start": v(-149.57, -162.06) * mm, "mid": v(-150.63, -162.5) * mm, "end": v(-151.07, -163.56) * mm});
            skPoint(sketch, "E164.visualSharp", {"position": v(-151.07, -181.06) * mm});
            skArc(sketch, "E164.filletArc", {"start": v(-149.57, -181.06) * mm, "mid": v(-150.63, -181.5) * mm, "end": v(-151.07, -182.56) * mm});
            skPoint(sketch, "E165.visualSharp", {"position": v(-138.07, -181.06) * mm});
            skArc(sketch, "E165.filletArc", {"start": v(-138.07, -182.56) * mm, "mid": v(-138.51, -181.5) * mm, "end": v(-139.57, -181.06) * mm});
            skPoint(sketch, "E166.visualSharp", {"position": v(-151.07, -194.06) * mm});
            skArc(sketch, "E166.filletArc", {"start": v(-151.07, -192.56) * mm, "mid": v(-150.63, -193.62) * mm, "end": v(-149.57, -194.06) * mm});
            skPoint(sketch, "E167.visualSharp", {"position": v(-138.07, -194.06) * mm});
            skArc(sketch, "E167.filletArc", {"start": v(-139.57, -194.06) * mm, "mid": v(-138.51, -193.62) * mm, "end": v(-138.07, -192.56) * mm});
            skPoint(sketch, "E168.visualSharp", {"position": v(-151.07, -200.06) * mm});
            skArc(sketch, "E168.filletArc", {"start": v(-149.57, -200.06) * mm, "mid": v(-150.63, -200.5) * mm, "end": v(-151.07, -201.56) * mm});
            skPoint(sketch, "E169.visualSharp", {"position": v(-138.07, -200.06) * mm});
            skArc(sketch, "E169.filletArc", {"start": v(-138.07, -201.56) * mm, "mid": v(-138.51, -200.5) * mm, "end": v(-139.57, -200.06) * mm});
            skPoint(sketch, "E170.visualSharp", {"position": v(-138.07, -213.06) * mm});
            skArc(sketch, "E170.filletArc", {"start": v(-139.57, -213.06) * mm, "mid": v(-138.51, -212.62) * mm, "end": v(-138.07, -211.56) * mm});
            skPoint(sketch, "E171.visualSharp", {"position": v(-151.07, -213.06) * mm});
            skArc(sketch, "E171.filletArc", {"start": v(-151.07, -211.56) * mm, "mid": v(-150.63, -212.62) * mm, "end": v(-149.57, -213.06) * mm});
            skPoint(sketch, "E172.visualSharp", {"position": v(-151.07, -219.06) * mm});
            skArc(sketch, "E172.filletArc", {"start": v(-149.57, -219.06) * mm, "mid": v(-150.63, -219.5) * mm, "end": v(-151.07, -220.56) * mm});
            skPoint(sketch, "E173.visualSharp", {"position": v(-138.07, -219.06) * mm});
            skArc(sketch, "E173.filletArc", {"start": v(-138.07, -220.56) * mm, "mid": v(-138.51, -219.5) * mm, "end": v(-139.57, -219.06) * mm});
            skPoint(sketch, "E174.visualSharp", {"position": v(-151.07, -232.06) * mm});
            skArc(sketch, "E174.filletArc", {"start": v(-151.07, -230.56) * mm, "mid": v(-150.63, -231.62) * mm, "end": v(-149.57, -232.06) * mm});
            skPoint(sketch, "E175.visualSharp", {"position": v(-138.07, -232.06) * mm});
            skArc(sketch, "E175.filletArc", {"start": v(-139.57, -232.06) * mm, "mid": v(-138.51, -231.62) * mm, "end": v(-138.07, -230.56) * mm});
            skPoint(sketch, "E176.visualSharp", {"position": v(-134.57, -124.06) * mm});
            skArc(sketch, "E176.filletArc", {"start": v(-133.07, -124.06) * mm, "mid": v(-134.13, -124.5) * mm, "end": v(-134.57, -125.56) * mm});
            skPoint(sketch, "E177.visualSharp", {"position": v(-121.57, -124.06) * mm});
            skArc(sketch, "E177.filletArc", {"start": v(-121.57, -125.56) * mm, "mid": v(-122.01, -124.5) * mm, "end": v(-123.07, -124.06) * mm});
            skPoint(sketch, "E178.visualSharp", {"position": v(-134.57, -137.06) * mm});
            skArc(sketch, "E178.filletArc", {"start": v(-134.57, -135.56) * mm, "mid": v(-134.13, -136.62) * mm, "end": v(-133.07, -137.06) * mm});
            skPoint(sketch, "E179.visualSharp", {"position": v(-121.57, -137.06) * mm});
            skArc(sketch, "E179.filletArc", {"start": v(-123.07, -137.06) * mm, "mid": v(-122.01, -136.62) * mm, "end": v(-121.57, -135.56) * mm});
            skPoint(sketch, "E180.visualSharp", {"position": v(-134.57, -143.06) * mm});
            skArc(sketch, "E180.filletArc", {"start": v(-133.07, -143.06) * mm, "mid": v(-134.13, -143.5) * mm, "end": v(-134.57, -144.56) * mm});
            skPoint(sketch, "E181.visualSharp", {"position": v(-121.57, -143.06) * mm});
            skArc(sketch, "E181.filletArc", {"start": v(-121.57, -144.56) * mm, "mid": v(-122.01, -143.5) * mm, "end": v(-123.07, -143.06) * mm});
            skPoint(sketch, "E182.visualSharp", {"position": v(-134.57, -156.06) * mm});
            skArc(sketch, "E182.filletArc", {"start": v(-134.57, -154.56) * mm, "mid": v(-134.13, -155.62) * mm, "end": v(-133.07, -156.06) * mm});
            skPoint(sketch, "E183.visualSharp", {"position": v(-121.57, -156.06) * mm});
            skArc(sketch, "E183.filletArc", {"start": v(-123.07, -156.06) * mm, "mid": v(-122.01, -155.62) * mm, "end": v(-121.57, -154.56) * mm});
            skPoint(sketch, "E184.visualSharp", {"position": v(-134.57, -162.06) * mm});
            skArc(sketch, "E184.filletArc", {"start": v(-133.07, -162.06) * mm, "mid": v(-134.13, -162.5) * mm, "end": v(-134.57, -163.56) * mm});
            skPoint(sketch, "E185.visualSharp", {"position": v(-121.57, -162.06) * mm});
            skArc(sketch, "E185.filletArc", {"start": v(-121.57, -163.56) * mm, "mid": v(-122.01, -162.5) * mm, "end": v(-123.07, -162.06) * mm});
            skPoint(sketch, "E186.visualSharp", {"position": v(-134.57, -175.06) * mm});
            skArc(sketch, "E186.filletArc", {"start": v(-134.57, -173.56) * mm, "mid": v(-134.13, -174.62) * mm, "end": v(-133.07, -175.06) * mm});
            skPoint(sketch, "E187.visualSharp", {"position": v(-121.57, -175.06) * mm});
            skArc(sketch, "E187.filletArc", {"start": v(-123.07, -175.06) * mm, "mid": v(-122.01, -174.62) * mm, "end": v(-121.57, -173.56) * mm});
            skPoint(sketch, "E188.visualSharp", {"position": v(-134.57, -181.06) * mm});
            skArc(sketch, "E188.filletArc", {"start": v(-133.07, -181.06) * mm, "mid": v(-134.13, -181.5) * mm, "end": v(-134.57, -182.56) * mm});
            skPoint(sketch, "E189.visualSharp", {"position": v(-121.57, -181.06) * mm});
            skArc(sketch, "E189.filletArc", {"start": v(-121.57, -182.56) * mm, "mid": v(-122.01, -181.5) * mm, "end": v(-123.07, -181.06) * mm});
            skPoint(sketch, "E190.visualSharp", {"position": v(-134.57, -194.06) * mm});
            skArc(sketch, "E190.filletArc", {"start": v(-134.57, -192.56) * mm, "mid": v(-134.13, -193.62) * mm, "end": v(-133.07, -194.06) * mm});
            skPoint(sketch, "E191.visualSharp", {"position": v(-121.57, -194.06) * mm});
            skArc(sketch, "E191.filletArc", {"start": v(-123.07, -194.06) * mm, "mid": v(-122.01, -193.62) * mm, "end": v(-121.57, -192.56) * mm});
            skPoint(sketch, "E192.visualSharp", {"position": v(-134.57, -200.06) * mm});
            skArc(sketch, "E192.filletArc", {"start": v(-133.07, -200.06) * mm, "mid": v(-134.13, -200.5) * mm, "end": v(-134.57, -201.56) * mm});
            skPoint(sketch, "E193.visualSharp", {"position": v(-121.57, -200.06) * mm});
            skArc(sketch, "E193.filletArc", {"start": v(-121.57, -201.56) * mm, "mid": v(-122.01, -200.5) * mm, "end": v(-123.07, -200.06) * mm});
            skPoint(sketch, "E194.visualSharp", {"position": v(-134.57, -213.06) * mm});
            skArc(sketch, "E194.filletArc", {"start": v(-134.57, -211.56) * mm, "mid": v(-134.13, -212.62) * mm, "end": v(-133.07, -213.06) * mm});
            skPoint(sketch, "E195.visualSharp", {"position": v(-121.57, -213.06) * mm});
            skArc(sketch, "E195.filletArc", {"start": v(-123.07, -213.06) * mm, "mid": v(-122.01, -212.62) * mm, "end": v(-121.57, -211.56) * mm});
            skPoint(sketch, "E196.visualSharp", {"position": v(-134.57, -219.06) * mm});
            skArc(sketch, "E196.filletArc", {"start": v(-133.07, -219.06) * mm, "mid": v(-134.13, -219.5) * mm, "end": v(-134.57, -220.56) * mm});
            skPoint(sketch, "E197.visualSharp", {"position": v(-121.57, -219.06) * mm});
            skArc(sketch, "E197.filletArc", {"start": v(-121.57, -220.56) * mm, "mid": v(-122.01, -219.5) * mm, "end": v(-123.07, -219.06) * mm});
            skPoint(sketch, "E198.visualSharp", {"position": v(-134.57, -232.06) * mm});
            skArc(sketch, "E198.filletArc", {"start": v(-134.57, -230.56) * mm, "mid": v(-134.13, -231.62) * mm, "end": v(-133.07, -232.06) * mm});
            skPoint(sketch, "E199.visualSharp", {"position": v(-121.57, -232.06) * mm});
            skArc(sketch, "E199.filletArc", {"start": v(-123.07, -232.06) * mm, "mid": v(-122.01, -231.62) * mm, "end": v(-121.57, -230.56) * mm});
            skPoint(sketch, "E200.visualSharp", {"position": v(-118.07, -124.06) * mm});
            skArc(sketch, "E200.filletArc", {"start": v(-116.57, -124.06) * mm, "mid": v(-117.63, -124.5) * mm, "end": v(-118.07, -125.56) * mm});
            skPoint(sketch, "E201.visualSharp", {"position": v(-105.07, -124.06) * mm});
            skArc(sketch, "E201.filletArc", {"start": v(-105.07, -125.56) * mm, "mid": v(-105.51, -124.5) * mm, "end": v(-106.57, -124.06) * mm});
            skPoint(sketch, "E202.visualSharp", {"position": v(-118.07, -137.06) * mm});
            skArc(sketch, "E202.filletArc", {"start": v(-118.07, -135.56) * mm, "mid": v(-117.63, -136.62) * mm, "end": v(-116.57, -137.06) * mm});
            skPoint(sketch, "E203.visualSharp", {"position": v(-105.07, -137.06) * mm});
            skArc(sketch, "E203.filletArc", {"start": v(-106.57, -137.06) * mm, "mid": v(-105.51, -136.62) * mm, "end": v(-105.07, -135.56) * mm});
            skPoint(sketch, "E204.visualSharp", {"position": v(-118.07, -143.06) * mm});
            skArc(sketch, "E204.filletArc", {"start": v(-116.57, -143.06) * mm, "mid": v(-117.63, -143.5) * mm, "end": v(-118.07, -144.56) * mm});
            skPoint(sketch, "E205.visualSharp", {"position": v(-105.07, -143.06) * mm});
            skArc(sketch, "E205.filletArc", {"start": v(-105.07, -144.56) * mm, "mid": v(-105.51, -143.5) * mm, "end": v(-106.57, -143.06) * mm});
            skPoint(sketch, "E206.visualSharp", {"position": v(-118.07, -156.06) * mm});
            skArc(sketch, "E206.filletArc", {"start": v(-118.07, -154.56) * mm, "mid": v(-117.63, -155.62) * mm, "end": v(-116.57, -156.06) * mm});
            skPoint(sketch, "E207.visualSharp", {"position": v(-105.07, -156.06) * mm});
            skArc(sketch, "E207.filletArc", {"start": v(-106.57, -156.06) * mm, "mid": v(-105.51, -155.62) * mm, "end": v(-105.07, -154.56) * mm});
            skPoint(sketch, "E208.visualSharp", {"position": v(-118.07, -162.06) * mm});
            skArc(sketch, "E208.filletArc", {"start": v(-116.57, -162.06) * mm, "mid": v(-117.63, -162.5) * mm, "end": v(-118.07, -163.56) * mm});
            skPoint(sketch, "E209.visualSharp", {"position": v(-105.07, -162.06) * mm});
            skArc(sketch, "E209.filletArc", {"start": v(-105.07, -163.56) * mm, "mid": v(-105.51, -162.5) * mm, "end": v(-106.57, -162.06) * mm});
            skPoint(sketch, "E210.visualSharp", {"position": v(-118.07, -175.06) * mm});
            skArc(sketch, "E210.filletArc", {"start": v(-118.07, -173.56) * mm, "mid": v(-117.63, -174.62) * mm, "end": v(-116.57, -175.06) * mm});
            skPoint(sketch, "E211.visualSharp", {"position": v(-105.07, -175.06) * mm});
            skArc(sketch, "E211.filletArc", {"start": v(-106.57, -175.06) * mm, "mid": v(-105.51, -174.62) * mm, "end": v(-105.07, -173.56) * mm});
            skPoint(sketch, "E212.visualSharp", {"position": v(-118.07, -181.06) * mm});
            skArc(sketch, "E212.filletArc", {"start": v(-116.57, -181.06) * mm, "mid": v(-117.63, -181.5) * mm, "end": v(-118.07, -182.56) * mm});
            skPoint(sketch, "E213.visualSharp", {"position": v(-105.07, -181.06) * mm});
            skArc(sketch, "E213.filletArc", {"start": v(-105.07, -182.56) * mm, "mid": v(-105.51, -181.5) * mm, "end": v(-106.57, -181.06) * mm});
            skPoint(sketch, "E214.visualSharp", {"position": v(-118.07, -194.06) * mm});
            skArc(sketch, "E214.filletArc", {"start": v(-118.07, -192.56) * mm, "mid": v(-117.63, -193.62) * mm, "end": v(-116.57, -194.06) * mm});
            skPoint(sketch, "E215.visualSharp", {"position": v(-105.07, -194.06) * mm});
            skArc(sketch, "E215.filletArc", {"start": v(-106.57, -194.06) * mm, "mid": v(-105.51, -193.62) * mm, "end": v(-105.07, -192.56) * mm});
            skPoint(sketch, "E216.visualSharp", {"position": v(-118.07, -200.06) * mm});
            skArc(sketch, "E216.filletArc", {"start": v(-116.57, -200.06) * mm, "mid": v(-117.63, -200.5) * mm, "end": v(-118.07, -201.56) * mm});
            skPoint(sketch, "E217.visualSharp", {"position": v(-105.07, -200.06) * mm});
            skArc(sketch, "E217.filletArc", {"start": v(-105.07, -201.56) * mm, "mid": v(-105.51, -200.5) * mm, "end": v(-106.57, -200.06) * mm});
            skPoint(sketch, "E218.visualSharp", {"position": v(-118.07, -213.06) * mm});
            skArc(sketch, "E218.filletArc", {"start": v(-118.07, -211.56) * mm, "mid": v(-117.63, -212.62) * mm, "end": v(-116.57, -213.06) * mm});
            skPoint(sketch, "E219.visualSharp", {"position": v(-105.07, -213.06) * mm});
            skArc(sketch, "E219.filletArc", {"start": v(-106.57, -213.06) * mm, "mid": v(-105.51, -212.62) * mm, "end": v(-105.07, -211.56) * mm});
            skPoint(sketch, "E220.visualSharp", {"position": v(-118.07, -219.06) * mm});
            skArc(sketch, "E220.filletArc", {"start": v(-116.57, -219.06) * mm, "mid": v(-117.63, -219.5) * mm, "end": v(-118.07, -220.56) * mm});
            skPoint(sketch, "E221.visualSharp", {"position": v(-105.07, -219.06) * mm});
            skArc(sketch, "E221.filletArc", {"start": v(-105.07, -220.56) * mm, "mid": v(-105.51, -219.5) * mm, "end": v(-106.57, -219.06) * mm});
            skPoint(sketch, "E222.visualSharp", {"position": v(-118.07, -232.06) * mm});
            skArc(sketch, "E222.filletArc", {"start": v(-118.07, -230.56) * mm, "mid": v(-117.63, -231.62) * mm, "end": v(-116.57, -232.06) * mm});
            skPoint(sketch, "E223.visualSharp", {"position": v(-105.07, -232.06) * mm});
            skArc(sketch, "E223.filletArc", {"start": v(-106.57, -232.06) * mm, "mid": v(-105.51, -231.62) * mm, "end": v(-105.07, -230.56) * mm});
            skPoint(sketch, "E224.visualSharp", {"position": v(-101.57, -124.06) * mm});
            skArc(sketch, "E224.filletArc", {"start": v(-100.07, -124.06) * mm, "mid": v(-101.13, -124.5) * mm, "end": v(-101.57, -125.56) * mm});
            skPoint(sketch, "E225.visualSharp", {"position": v(-88.57, -124.06) * mm});
            skArc(sketch, "E225.filletArc", {"start": v(-88.57, -125.56) * mm, "mid": v(-89.01, -124.5) * mm, "end": v(-90.07, -124.06) * mm});
            skPoint(sketch, "E226.visualSharp", {"position": v(-101.57, -137.06) * mm});
            skArc(sketch, "E226.filletArc", {"start": v(-101.57, -135.56) * mm, "mid": v(-101.13, -136.62) * mm, "end": v(-100.07, -137.06) * mm});
            skPoint(sketch, "E227.visualSharp", {"position": v(-88.57, -137.06) * mm});
            skArc(sketch, "E227.filletArc", {"start": v(-90.07, -137.06) * mm, "mid": v(-89.01, -136.62) * mm, "end": v(-88.57, -135.56) * mm});
            skPoint(sketch, "E228.visualSharp", {"position": v(-101.57, -143.06) * mm});
            skArc(sketch, "E228.filletArc", {"start": v(-100.07, -143.06) * mm, "mid": v(-101.13, -143.5) * mm, "end": v(-101.57, -144.56) * mm});
            skPoint(sketch, "E229.visualSharp", {"position": v(-88.57, -143.06) * mm});
            skArc(sketch, "E229.filletArc", {"start": v(-88.57, -144.56) * mm, "mid": v(-89.01, -143.5) * mm, "end": v(-90.07, -143.06) * mm});
            skPoint(sketch, "E230.visualSharp", {"position": v(-101.57, -156.06) * mm});
            skArc(sketch, "E230.filletArc", {"start": v(-101.57, -154.56) * mm, "mid": v(-101.13, -155.62) * mm, "end": v(-100.07, -156.06) * mm});
            skPoint(sketch, "E231.visualSharp", {"position": v(-88.57, -156.06) * mm});
            skArc(sketch, "E231.filletArc", {"start": v(-90.07, -156.06) * mm, "mid": v(-89.01, -155.62) * mm, "end": v(-88.57, -154.56) * mm});
            skPoint(sketch, "E232.visualSharp", {"position": v(-88.57, -162.06) * mm});
            skArc(sketch, "E232.filletArc", {"start": v(-88.57, -163.56) * mm, "mid": v(-89.01, -162.5) * mm, "end": v(-90.07, -162.06) * mm});
            skPoint(sketch, "E233.visualSharp", {"position": v(-88.57, -175.06) * mm});
            skArc(sketch, "E233.filletArc", {"start": v(-90.07, -175.06) * mm, "mid": v(-89.01, -174.62) * mm, "end": v(-88.57, -173.56) * mm});
            skPoint(sketch, "E234.visualSharp", {"position": v(-101.57, -175.06) * mm});
            skArc(sketch, "E234.filletArc", {"start": v(-101.57, -173.56) * mm, "mid": v(-101.13, -174.62) * mm, "end": v(-100.07, -175.06) * mm});
            skPoint(sketch, "E235.visualSharp", {"position": v(-101.57, -162.06) * mm});
            skArc(sketch, "E235.filletArc", {"start": v(-100.07, -162.06) * mm, "mid": v(-101.13, -162.5) * mm, "end": v(-101.57, -163.56) * mm});
            skPoint(sketch, "E236.visualSharp", {"position": v(-101.57, -181.06) * mm});
            skArc(sketch, "E236.filletArc", {"start": v(-100.07, -181.06) * mm, "mid": v(-101.13, -181.5) * mm, "end": v(-101.57, -182.56) * mm});
            skPoint(sketch, "E237.visualSharp", {"position": v(-88.57, -181.06) * mm});
            skArc(sketch, "E237.filletArc", {"start": v(-88.57, -182.56) * mm, "mid": v(-89.01, -181.5) * mm, "end": v(-90.07, -181.06) * mm});
            skPoint(sketch, "E238.visualSharp", {"position": v(-101.57, -194.06) * mm});
            skArc(sketch, "E238.filletArc", {"start": v(-101.57, -192.56) * mm, "mid": v(-101.13, -193.62) * mm, "end": v(-100.07, -194.06) * mm});
            skPoint(sketch, "E239.visualSharp", {"position": v(-88.57, -194.06) * mm});
            skArc(sketch, "E239.filletArc", {"start": v(-90.07, -194.06) * mm, "mid": v(-89.01, -193.62) * mm, "end": v(-88.57, -192.56) * mm});
            skPoint(sketch, "E240.visualSharp", {"position": v(-101.57, -200.06) * mm});
            skArc(sketch, "E240.filletArc", {"start": v(-100.07, -200.06) * mm, "mid": v(-101.13, -200.5) * mm, "end": v(-101.57, -201.56) * mm});
            skPoint(sketch, "E241.visualSharp", {"position": v(-88.57, -200.06) * mm});
            skArc(sketch, "E241.filletArc", {"start": v(-88.57, -201.56) * mm, "mid": v(-89.01, -200.5) * mm, "end": v(-90.07, -200.06) * mm});
            skPoint(sketch, "E242.visualSharp", {"position": v(-101.57, -213.06) * mm});
            skArc(sketch, "E242.filletArc", {"start": v(-101.57, -211.56) * mm, "mid": v(-101.13, -212.62) * mm, "end": v(-100.07, -213.06) * mm});
            skPoint(sketch, "E243.visualSharp", {"position": v(-88.57, -213.06) * mm});
            skArc(sketch, "E243.filletArc", {"start": v(-90.07, -213.06) * mm, "mid": v(-89.01, -212.62) * mm, "end": v(-88.57, -211.56) * mm});
            skPoint(sketch, "E244.visualSharp", {"position": v(-101.57, -219.06) * mm});
            skArc(sketch, "E244.filletArc", {"start": v(-100.07, -219.06) * mm, "mid": v(-101.13, -219.5) * mm, "end": v(-101.57, -220.56) * mm});
            skPoint(sketch, "E245.visualSharp", {"position": v(-88.57, -219.06) * mm});
            skArc(sketch, "E245.filletArc", {"start": v(-88.57, -220.56) * mm, "mid": v(-89.01, -219.5) * mm, "end": v(-90.07, -219.06) * mm});
            skPoint(sketch, "E246.visualSharp", {"position": v(-101.57, -232.06) * mm});
            skArc(sketch, "E246.filletArc", {"start": v(-101.57, -230.56) * mm, "mid": v(-101.13, -231.62) * mm, "end": v(-100.07, -232.06) * mm});
            skPoint(sketch, "E247.visualSharp", {"position": v(-88.57, -232.06) * mm});
            skArc(sketch, "E247.filletArc", {"start": v(-90.07, -232.06) * mm, "mid": v(-89.01, -231.62) * mm, "end": v(-88.57, -230.56) * mm});
            skPoint(sketch, "E248.visualSharp", {"position": v(-85.07, -124.06) * mm});
            skArc(sketch, "E248.filletArc", {"start": v(-83.57, -124.06) * mm, "mid": v(-84.63, -124.5) * mm, "end": v(-85.07, -125.56) * mm});
            skPoint(sketch, "E249.visualSharp", {"position": v(-72.07, -124.06) * mm});
            skArc(sketch, "E249.filletArc", {"start": v(-72.07, -125.56) * mm, "mid": v(-72.51, -124.5) * mm, "end": v(-73.57, -124.06) * mm});
            skPoint(sketch, "E250.visualSharp", {"position": v(-85.07, -137.06) * mm});
            skArc(sketch, "E250.filletArc", {"start": v(-85.07, -135.56) * mm, "mid": v(-84.63, -136.62) * mm, "end": v(-83.57, -137.06) * mm});
            skPoint(sketch, "E251.visualSharp", {"position": v(-72.07, -137.06) * mm});
            skArc(sketch, "E251.filletArc", {"start": v(-73.57, -137.06) * mm, "mid": v(-72.51, -136.62) * mm, "end": v(-72.07, -135.56) * mm});
            skPoint(sketch, "E252.visualSharp", {"position": v(-85.07, -143.06) * mm});
            skArc(sketch, "E252.filletArc", {"start": v(-83.57, -143.06) * mm, "mid": v(-84.63, -143.5) * mm, "end": v(-85.07, -144.56) * mm});
            skPoint(sketch, "E253.visualSharp", {"position": v(-72.07, -143.06) * mm});
            skArc(sketch, "E253.filletArc", {"start": v(-72.07, -144.56) * mm, "mid": v(-72.51, -143.5) * mm, "end": v(-73.57, -143.06) * mm});
            skPoint(sketch, "E254.visualSharp", {"position": v(-85.07, -156.06) * mm});
            skArc(sketch, "E254.filletArc", {"start": v(-85.07, -154.56) * mm, "mid": v(-84.63, -155.62) * mm, "end": v(-83.57, -156.06) * mm});
            skPoint(sketch, "E255.visualSharp", {"position": v(-72.07, -156.06) * mm});
            skArc(sketch, "E255.filletArc", {"start": v(-73.57, -156.06) * mm, "mid": v(-72.51, -155.62) * mm, "end": v(-72.07, -154.56) * mm});
            skPoint(sketch, "E256.visualSharp", {"position": v(-85.07, -162.06) * mm});
            skArc(sketch, "E256.filletArc", {"start": v(-83.57, -162.06) * mm, "mid": v(-84.63, -162.5) * mm, "end": v(-85.07, -163.56) * mm});
            skPoint(sketch, "E257.visualSharp", {"position": v(-72.07, -162.06) * mm});
            skArc(sketch, "E257.filletArc", {"start": v(-72.07, -163.56) * mm, "mid": v(-72.51, -162.5) * mm, "end": v(-73.57, -162.06) * mm});
            skPoint(sketch, "E258.visualSharp", {"position": v(-85.07, -175.06) * mm});
            skArc(sketch, "E258.filletArc", {"start": v(-85.07, -173.56) * mm, "mid": v(-84.63, -174.62) * mm, "end": v(-83.57, -175.06) * mm});
            skPoint(sketch, "E259.visualSharp", {"position": v(-72.07, -175.06) * mm});
            skArc(sketch, "E259.filletArc", {"start": v(-73.57, -175.06) * mm, "mid": v(-72.51, -174.62) * mm, "end": v(-72.07, -173.56) * mm});
            skPoint(sketch, "E260.visualSharp", {"position": v(-85.07, -181.06) * mm});
            skArc(sketch, "E260.filletArc", {"start": v(-83.57, -181.06) * mm, "mid": v(-84.63, -181.5) * mm, "end": v(-85.07, -182.56) * mm});
            skPoint(sketch, "E261.visualSharp", {"position": v(-85.07, -194.06) * mm});
            skArc(sketch, "E261.filletArc", {"start": v(-85.07, -192.56) * mm, "mid": v(-84.63, -193.62) * mm, "end": v(-83.57, -194.06) * mm});
            skPoint(sketch, "E262.visualSharp", {"position": v(-72.07, -181.06) * mm});
            skArc(sketch, "E262.filletArc", {"start": v(-72.07, -182.56) * mm, "mid": v(-72.51, -181.5) * mm, "end": v(-73.57, -181.06) * mm});
            skPoint(sketch, "E263.visualSharp", {"position": v(-72.07, -194.06) * mm});
            skArc(sketch, "E263.filletArc", {"start": v(-73.57, -194.06) * mm, "mid": v(-72.51, -193.62) * mm, "end": v(-72.07, -192.56) * mm});
            skPoint(sketch, "E264.visualSharp", {"position": v(-85.07, -200.06) * mm});
            skArc(sketch, "E264.filletArc", {"start": v(-83.57, -200.06) * mm, "mid": v(-84.63, -200.5) * mm, "end": v(-85.07, -201.56) * mm});
            skPoint(sketch, "E265.visualSharp", {"position": v(-72.07, -200.06) * mm});
            skArc(sketch, "E265.filletArc", {"start": v(-72.07, -201.56) * mm, "mid": v(-72.51, -200.5) * mm, "end": v(-73.57, -200.06) * mm});
            skPoint(sketch, "E266.visualSharp", {"position": v(-85.07, -213.06) * mm});
            skArc(sketch, "E266.filletArc", {"start": v(-85.07, -211.56) * mm, "mid": v(-84.63, -212.62) * mm, "end": v(-83.57, -213.06) * mm});
            skPoint(sketch, "E267.visualSharp", {"position": v(-72.07, -213.06) * mm});
            skArc(sketch, "E267.filletArc", {"start": v(-73.57, -213.06) * mm, "mid": v(-72.51, -212.62) * mm, "end": v(-72.07, -211.56) * mm});
            skPoint(sketch, "E268.visualSharp", {"position": v(-85.07, -219.06) * mm});
            skArc(sketch, "E268.filletArc", {"start": v(-83.57, -219.06) * mm, "mid": v(-84.63, -219.5) * mm, "end": v(-85.07, -220.56) * mm});
            skPoint(sketch, "E269.visualSharp", {"position": v(-72.07, -219.06) * mm});
            skArc(sketch, "E269.filletArc", {"start": v(-72.07, -220.56) * mm, "mid": v(-72.51, -219.5) * mm, "end": v(-73.57, -219.06) * mm});
            skPoint(sketch, "E270.visualSharp", {"position": v(-85.07, -232.06) * mm});
            skArc(sketch, "E270.filletArc", {"start": v(-85.07, -230.56) * mm, "mid": v(-84.63, -231.62) * mm, "end": v(-83.57, -232.06) * mm});
            skPoint(sketch, "E271.visualSharp", {"position": v(-72.07, -232.06) * mm});
            skArc(sketch, "E271.filletArc", {"start": v(-73.57, -232.06) * mm, "mid": v(-72.51, -231.62) * mm, "end": v(-72.07, -230.56) * mm});
            skPoint(sketch, "E272.visualSharp", {"position": v(-68.57, -124.06) * mm});
            skArc(sketch, "E272.filletArc", {"start": v(-67.07, -124.06) * mm, "mid": v(-68.13, -124.5) * mm, "end": v(-68.57, -125.56) * mm});
            skPoint(sketch, "E273.visualSharp", {"position": v(-68.57, -137.06) * mm});
            skArc(sketch, "E273.filletArc", {"start": v(-68.57, -135.56) * mm, "mid": v(-68.13, -136.62) * mm, "end": v(-67.07, -137.06) * mm});
            skPoint(sketch, "E274.visualSharp", {"position": v(-55.57, -137.06) * mm});
            skArc(sketch, "E274.filletArc", {"start": v(-57.07, -137.06) * mm, "mid": v(-56.01, -136.62) * mm, "end": v(-55.57, -135.56) * mm});
            skPoint(sketch, "E275.visualSharp", {"position": v(-55.57, -124.06) * mm});
            skArc(sketch, "E275.filletArc", {"start": v(-55.57, -125.56) * mm, "mid": v(-56.01, -124.5) * mm, "end": v(-57.07, -124.06) * mm});
            skPoint(sketch, "E276.visualSharp", {"position": v(-68.57, -143.06) * mm});
            skArc(sketch, "E276.filletArc", {"start": v(-67.07, -143.06) * mm, "mid": v(-68.13, -143.5) * mm, "end": v(-68.57, -144.56) * mm});
            skPoint(sketch, "E277.visualSharp", {"position": v(-55.57, -143.06) * mm});
            skArc(sketch, "E277.filletArc", {"start": v(-55.57, -144.56) * mm, "mid": v(-56.01, -143.5) * mm, "end": v(-57.07, -143.06) * mm});
            skPoint(sketch, "E278.visualSharp", {"position": v(-68.57, -156.06) * mm});
            skArc(sketch, "E278.filletArc", {"start": v(-68.57, -154.56) * mm, "mid": v(-68.13, -155.62) * mm, "end": v(-67.07, -156.06) * mm});
            skPoint(sketch, "E279.visualSharp", {"position": v(-55.57, -156.06) * mm});
            skArc(sketch, "E279.filletArc", {"start": v(-57.07, -156.06) * mm, "mid": v(-56.01, -155.62) * mm, "end": v(-55.57, -154.56) * mm});
            skPoint(sketch, "E280.visualSharp", {"position": v(-55.57, -162.06) * mm});
            skArc(sketch, "E280.filletArc", {"start": v(-55.57, -163.56) * mm, "mid": v(-56.01, -162.5) * mm, "end": v(-57.07, -162.06) * mm});
            skPoint(sketch, "E281.visualSharp", {"position": v(-68.57, -175.06) * mm});
            skArc(sketch, "E281.filletArc", {"start": v(-68.57, -173.56) * mm, "mid": v(-68.13, -174.62) * mm, "end": v(-67.07, -175.06) * mm});
            skPoint(sketch, "E282.visualSharp", {"position": v(-55.57, -175.06) * mm});
            skArc(sketch, "E282.filletArc", {"start": v(-57.07, -175.06) * mm, "mid": v(-56.01, -174.62) * mm, "end": v(-55.57, -173.56) * mm});
            skPoint(sketch, "E283.visualSharp", {"position": v(-68.57, -162.06) * mm});
            skArc(sketch, "E283.filletArc", {"start": v(-67.07, -162.06) * mm, "mid": v(-68.13, -162.5) * mm, "end": v(-68.57, -163.56) * mm});
            skPoint(sketch, "E284.visualSharp", {"position": v(-68.57, -181.06) * mm});
            skArc(sketch, "E284.filletArc", {"start": v(-67.07, -181.06) * mm, "mid": v(-68.13, -181.5) * mm, "end": v(-68.57, -182.56) * mm});
            skPoint(sketch, "E285.visualSharp", {"position": v(-55.57, -181.06) * mm});
            skArc(sketch, "E285.filletArc", {"start": v(-55.57, -182.56) * mm, "mid": v(-56.01, -181.5) * mm, "end": v(-57.07, -181.06) * mm});
            skPoint(sketch, "E286.visualSharp", {"position": v(-68.57, -194.06) * mm});
            skArc(sketch, "E286.filletArc", {"start": v(-68.57, -192.56) * mm, "mid": v(-68.13, -193.62) * mm, "end": v(-67.07, -194.06) * mm});
            skPoint(sketch, "E287.visualSharp", {"position": v(-55.57, -194.06) * mm});
            skArc(sketch, "E287.filletArc", {"start": v(-57.07, -194.06) * mm, "mid": v(-56.01, -193.62) * mm, "end": v(-55.57, -192.56) * mm});
            skPoint(sketch, "E288.visualSharp", {"position": v(-68.57, -200.06) * mm});
            skArc(sketch, "E288.filletArc", {"start": v(-67.07, -200.06) * mm, "mid": v(-68.13, -200.5) * mm, "end": v(-68.57, -201.56) * mm});
            skPoint(sketch, "E289.visualSharp", {"position": v(-55.57, -200.06) * mm});
            skArc(sketch, "E289.filletArc", {"start": v(-55.57, -201.56) * mm, "mid": v(-56.01, -200.5) * mm, "end": v(-57.07, -200.06) * mm});
            skPoint(sketch, "E290.visualSharp", {"position": v(-68.57, -213.06) * mm});
            skArc(sketch, "E290.filletArc", {"start": v(-68.57, -211.56) * mm, "mid": v(-68.13, -212.62) * mm, "end": v(-67.07, -213.06) * mm});
            skPoint(sketch, "E291.visualSharp", {"position": v(-55.57, -213.06) * mm});
            skArc(sketch, "E291.filletArc", {"start": v(-57.07, -213.06) * mm, "mid": v(-56.01, -212.62) * mm, "end": v(-55.57, -211.56) * mm});
            skPoint(sketch, "E292.visualSharp", {"position": v(-68.57, -219.06) * mm});
            skArc(sketch, "E292.filletArc", {"start": v(-67.07, -219.06) * mm, "mid": v(-68.13, -219.5) * mm, "end": v(-68.57, -220.56) * mm});
            skPoint(sketch, "E293.visualSharp", {"position": v(-55.57, -219.06) * mm});
            skArc(sketch, "E293.filletArc", {"start": v(-55.57, -220.56) * mm, "mid": v(-56.01, -219.5) * mm, "end": v(-57.07, -219.06) * mm});
            skPoint(sketch, "E294.visualSharp", {"position": v(-68.57, -232.06) * mm});
            skArc(sketch, "E294.filletArc", {"start": v(-68.57, -230.56) * mm, "mid": v(-68.13, -231.62) * mm, "end": v(-67.07, -232.06) * mm});
            skPoint(sketch, "E295.visualSharp", {"position": v(-55.57, -232.06) * mm});
            skArc(sketch, "E295.filletArc", {"start": v(-57.07, -232.06) * mm, "mid": v(-56.01, -231.62) * mm, "end": v(-55.57, -230.56) * mm});
            skPoint(sketch, "E296.visualSharp", {"position": v(-52.07, -124.06) * mm});
            skArc(sketch, "E296.filletArc", {"start": v(-50.57, -124.06) * mm, "mid": v(-51.63, -124.5) * mm, "end": v(-52.07, -125.56) * mm});
            skPoint(sketch, "E297.visualSharp", {"position": v(-39.07, -124.06) * mm});
            skArc(sketch, "E297.filletArc", {"start": v(-39.07, -125.56) * mm, "mid": v(-39.51, -124.5) * mm, "end": v(-40.57, -124.06) * mm});
            skPoint(sketch, "E298.visualSharp", {"position": v(-52.07, -137.06) * mm});
            skArc(sketch, "E298.filletArc", {"start": v(-52.07, -135.56) * mm, "mid": v(-51.63, -136.62) * mm, "end": v(-50.57, -137.06) * mm});
            skPoint(sketch, "E299.visualSharp", {"position": v(-39.07, -137.06) * mm});
            skArc(sketch, "E299.filletArc", {"start": v(-40.57, -137.06) * mm, "mid": v(-39.51, -136.62) * mm, "end": v(-39.07, -135.56) * mm});
            skPoint(sketch, "E300.visualSharp", {"position": v(-52.07, -143.06) * mm});
            skArc(sketch, "E300.filletArc", {"start": v(-50.57, -143.06) * mm, "mid": v(-51.63, -143.5) * mm, "end": v(-52.07, -144.56) * mm});
            skPoint(sketch, "E301.visualSharp", {"position": v(-39.07, -143.06) * mm});
            skArc(sketch, "E301.filletArc", {"start": v(-39.07, -144.56) * mm, "mid": v(-39.51, -143.5) * mm, "end": v(-40.57, -143.06) * mm});
            skPoint(sketch, "E302.visualSharp", {"position": v(-52.07, -156.06) * mm});
            skArc(sketch, "E302.filletArc", {"start": v(-52.07, -154.56) * mm, "mid": v(-51.63, -155.62) * mm, "end": v(-50.57, -156.06) * mm});
            skPoint(sketch, "E303.visualSharp", {"position": v(-39.07, -156.06) * mm});
            skArc(sketch, "E303.filletArc", {"start": v(-40.57, -156.06) * mm, "mid": v(-39.51, -155.62) * mm, "end": v(-39.07, -154.56) * mm});
            skPoint(sketch, "E304.visualSharp", {"position": v(-52.07, -162.06) * mm});
            skArc(sketch, "E304.filletArc", {"start": v(-50.57, -162.06) * mm, "mid": v(-51.63, -162.5) * mm, "end": v(-52.07, -163.56) * mm});
            skPoint(sketch, "E305.visualSharp", {"position": v(-39.07, -162.06) * mm});
            skArc(sketch, "E305.filletArc", {"start": v(-39.07, -163.56) * mm, "mid": v(-39.51, -162.5) * mm, "end": v(-40.57, -162.06) * mm});
            skPoint(sketch, "E306.visualSharp", {"position": v(-52.07, -175.06) * mm});
            skArc(sketch, "E306.filletArc", {"start": v(-52.07, -173.56) * mm, "mid": v(-51.63, -174.62) * mm, "end": v(-50.57, -175.06) * mm});
            skPoint(sketch, "E307.visualSharp", {"position": v(-39.07, -175.06) * mm});
            skArc(sketch, "E307.filletArc", {"start": v(-40.57, -175.06) * mm, "mid": v(-39.51, -174.62) * mm, "end": v(-39.07, -173.56) * mm});
            skPoint(sketch, "E308.visualSharp", {"position": v(-52.07, -181.06) * mm});
            skArc(sketch, "E308.filletArc", {"start": v(-50.57, -181.06) * mm, "mid": v(-51.63, -181.5) * mm, "end": v(-52.07, -182.56) * mm});
            skPoint(sketch, "E309.visualSharp", {"position": v(-39.07, -181.06) * mm});
            skArc(sketch, "E309.filletArc", {"start": v(-39.07, -182.56) * mm, "mid": v(-39.51, -181.5) * mm, "end": v(-40.57, -181.06) * mm});
            skPoint(sketch, "E310.visualSharp", {"position": v(-52.07, -194.06) * mm});
            skArc(sketch, "E310.filletArc", {"start": v(-52.07, -192.56) * mm, "mid": v(-51.63, -193.62) * mm, "end": v(-50.57, -194.06) * mm});
            skPoint(sketch, "E311.visualSharp", {"position": v(-39.07, -194.06) * mm});
            skArc(sketch, "E311.filletArc", {"start": v(-40.57, -194.06) * mm, "mid": v(-39.51, -193.62) * mm, "end": v(-39.07, -192.56) * mm});
            skPoint(sketch, "E312.visualSharp", {"position": v(-52.07, -200.06) * mm});
            skArc(sketch, "E312.filletArc", {"start": v(-50.57, -200.06) * mm, "mid": v(-51.63, -200.5) * mm, "end": v(-52.07, -201.56) * mm});
            skPoint(sketch, "E313.visualSharp", {"position": v(-39.07, -200.06) * mm});
            skArc(sketch, "E313.filletArc", {"start": v(-39.07, -201.56) * mm, "mid": v(-39.51, -200.5) * mm, "end": v(-40.57, -200.06) * mm});
            skPoint(sketch, "E314.visualSharp", {"position": v(-52.07, -213.06) * mm});
            skArc(sketch, "E314.filletArc", {"start": v(-52.07, -211.56) * mm, "mid": v(-51.63, -212.62) * mm, "end": v(-50.57, -213.06) * mm});
            skPoint(sketch, "E315.visualSharp", {"position": v(-39.07, -213.06) * mm});
            skArc(sketch, "E315.filletArc", {"start": v(-40.57, -213.06) * mm, "mid": v(-39.51, -212.62) * mm, "end": v(-39.07, -211.56) * mm});
            skPoint(sketch, "E316.visualSharp", {"position": v(-52.07, -219.06) * mm});
            skArc(sketch, "E316.filletArc", {"start": v(-50.57, -219.06) * mm, "mid": v(-51.63, -219.5) * mm, "end": v(-52.07, -220.56) * mm});
            skPoint(sketch, "E317.visualSharp", {"position": v(-39.07, -219.06) * mm});
            skArc(sketch, "E317.filletArc", {"start": v(-39.07, -220.56) * mm, "mid": v(-39.51, -219.5) * mm, "end": v(-40.57, -219.06) * mm});
            skPoint(sketch, "E318.visualSharp", {"position": v(-52.07, -232.06) * mm});
            skArc(sketch, "E318.filletArc", {"start": v(-52.07, -230.56) * mm, "mid": v(-51.63, -231.62) * mm, "end": v(-50.57, -232.06) * mm});
            skPoint(sketch, "E319.visualSharp", {"position": v(-39.07, -232.06) * mm});
            skArc(sketch, "E319.filletArc", {"start": v(-40.57, -232.06) * mm, "mid": v(-39.51, -231.62) * mm, "end": v(-39.07, -230.56) * mm});
            skPoint(sketch, "E320.visualSharp", {"position": v(-35.57, -124.06) * mm});
            skArc(sketch, "E320.filletArc", {"start": v(-34.07, -124.06) * mm, "mid": v(-35.13, -124.5) * mm, "end": v(-35.57, -125.56) * mm});
            skPoint(sketch, "E321.visualSharp", {"position": v(-22.57, -124.06) * mm});
            skArc(sketch, "E321.filletArc", {"start": v(-22.57, -125.56) * mm, "mid": v(-23.01, -124.5) * mm, "end": v(-24.07, -124.06) * mm});
            skPoint(sketch, "E322.visualSharp", {"position": v(-35.57, -137.06) * mm});
            skArc(sketch, "E322.filletArc", {"start": v(-35.57, -135.56) * mm, "mid": v(-35.13, -136.62) * mm, "end": v(-34.07, -137.06) * mm});
            skPoint(sketch, "E323.visualSharp", {"position": v(-22.57, -137.06) * mm});
            skArc(sketch, "E323.filletArc", {"start": v(-24.07, -137.06) * mm, "mid": v(-23.01, -136.62) * mm, "end": v(-22.57, -135.56) * mm});
            skPoint(sketch, "E324.visualSharp", {"position": v(-35.57, -143.06) * mm});
            skArc(sketch, "E324.filletArc", {"start": v(-34.07, -143.06) * mm, "mid": v(-35.13, -143.5) * mm, "end": v(-35.57, -144.56) * mm});
            skPoint(sketch, "E325.visualSharp", {"position": v(-22.57, -143.06) * mm});
            skArc(sketch, "E325.filletArc", {"start": v(-22.57, -144.56) * mm, "mid": v(-23.01, -143.5) * mm, "end": v(-24.07, -143.06) * mm});
            skPoint(sketch, "E326.visualSharp", {"position": v(-35.57, -156.06) * mm});
            skArc(sketch, "E326.filletArc", {"start": v(-35.57, -154.56) * mm, "mid": v(-35.13, -155.62) * mm, "end": v(-34.07, -156.06) * mm});
            skPoint(sketch, "E327.visualSharp", {"position": v(-22.57, -156.06) * mm});
            skArc(sketch, "E327.filletArc", {"start": v(-24.07, -156.06) * mm, "mid": v(-23.01, -155.62) * mm, "end": v(-22.57, -154.56) * mm});
            skPoint(sketch, "E328.visualSharp", {"position": v(-35.57, -162.06) * mm});
            skArc(sketch, "E328.filletArc", {"start": v(-34.07, -162.06) * mm, "mid": v(-35.13, -162.5) * mm, "end": v(-35.57, -163.56) * mm});
            skPoint(sketch, "E329.visualSharp", {"position": v(-22.57, -162.06) * mm});
            skArc(sketch, "E329.filletArc", {"start": v(-22.57, -163.56) * mm, "mid": v(-23.01, -162.5) * mm, "end": v(-24.07, -162.06) * mm});
            skPoint(sketch, "E330.visualSharp", {"position": v(-35.57, -175.06) * mm});
            skArc(sketch, "E330.filletArc", {"start": v(-35.57, -173.56) * mm, "mid": v(-35.13, -174.62) * mm, "end": v(-34.07, -175.06) * mm});
            skPoint(sketch, "E331.visualSharp", {"position": v(-22.57, -175.06) * mm});
            skArc(sketch, "E331.filletArc", {"start": v(-24.07, -175.06) * mm, "mid": v(-23.01, -174.62) * mm, "end": v(-22.57, -173.56) * mm});
            skPoint(sketch, "E332.visualSharp", {"position": v(-35.57, -181.06) * mm});
            skArc(sketch, "E332.filletArc", {"start": v(-34.07, -181.06) * mm, "mid": v(-35.13, -181.5) * mm, "end": v(-35.57, -182.56) * mm});
            skPoint(sketch, "E333.visualSharp", {"position": v(-22.57, -181.06) * mm});
            skArc(sketch, "E333.filletArc", {"start": v(-22.57, -182.56) * mm, "mid": v(-23.01, -181.5) * mm, "end": v(-24.07, -181.06) * mm});
            skPoint(sketch, "E334.visualSharp", {"position": v(-35.57, -194.06) * mm});
            skArc(sketch, "E334.filletArc", {"start": v(-35.57, -192.56) * mm, "mid": v(-35.13, -193.62) * mm, "end": v(-34.07, -194.06) * mm});
            skPoint(sketch, "E335.visualSharp", {"position": v(-22.57, -194.06) * mm});
            skArc(sketch, "E335.filletArc", {"start": v(-24.07, -194.06) * mm, "mid": v(-23.01, -193.62) * mm, "end": v(-22.57, -192.56) * mm});
            skPoint(sketch, "E336.visualSharp", {"position": v(-35.57, -200.06) * mm});
            skArc(sketch, "E336.filletArc", {"start": v(-34.07, -200.06) * mm, "mid": v(-35.13, -200.5) * mm, "end": v(-35.57, -201.56) * mm});
            skPoint(sketch, "E337.visualSharp", {"position": v(-22.57, -200.06) * mm});
            skArc(sketch, "E337.filletArc", {"start": v(-22.57, -201.56) * mm, "mid": v(-23.01, -200.5) * mm, "end": v(-24.07, -200.06) * mm});
            skPoint(sketch, "E338.visualSharp", {"position": v(-35.57, -213.06) * mm});
            skArc(sketch, "E338.filletArc", {"start": v(-35.57, -211.56) * mm, "mid": v(-35.13, -212.62) * mm, "end": v(-34.07, -213.06) * mm});
            skPoint(sketch, "E339.visualSharp", {"position": v(-22.57, -213.06) * mm});
            skArc(sketch, "E339.filletArc", {"start": v(-24.07, -213.06) * mm, "mid": v(-23.01, -212.62) * mm, "end": v(-22.57, -211.56) * mm});
            skPoint(sketch, "E340.visualSharp", {"position": v(-35.57, -219.06) * mm});
            skArc(sketch, "E340.filletArc", {"start": v(-34.07, -219.06) * mm, "mid": v(-35.13, -219.5) * mm, "end": v(-35.57, -220.56) * mm});
            skPoint(sketch, "E341.visualSharp", {"position": v(-22.57, -219.06) * mm});
            skArc(sketch, "E341.filletArc", {"start": v(-22.57, -220.56) * mm, "mid": v(-23.01, -219.5) * mm, "end": v(-24.07, -219.06) * mm});
            skPoint(sketch, "E342.visualSharp", {"position": v(-35.57, -232.06) * mm});
            skArc(sketch, "E342.filletArc", {"start": v(-35.57, -230.56) * mm, "mid": v(-35.13, -231.62) * mm, "end": v(-34.07, -232.06) * mm});
            skPoint(sketch, "E343.visualSharp", {"position": v(-22.57, -232.06) * mm});
            skArc(sketch, "E343.filletArc", {"start": v(-24.07, -232.06) * mm, "mid": v(-23.01, -231.62) * mm, "end": v(-22.57, -230.56) * mm});
            skPoint(sketch, "E344.visualSharp", {"position": v(-19.07, -124.06) * mm});
            skArc(sketch, "E344.filletArc", {"start": v(-17.57, -124.06) * mm, "mid": v(-18.63, -124.5) * mm, "end": v(-19.07, -125.56) * mm});
            skPoint(sketch, "E345.visualSharp", {"position": v(-6.07, -124.06) * mm});
            skArc(sketch, "E345.filletArc", {"start": v(-6.07, -125.56) * mm, "mid": v(-6.51, -124.5) * mm, "end": v(-7.57, -124.06) * mm});
            skPoint(sketch, "E346.visualSharp", {"position": v(-19.07, -137.06) * mm});
            skArc(sketch, "E346.filletArc", {"start": v(-19.07, -135.56) * mm, "mid": v(-18.63, -136.62) * mm, "end": v(-17.57, -137.06) * mm});
            skPoint(sketch, "E347.visualSharp", {"position": v(-6.07, -137.06) * mm});
            skArc(sketch, "E347.filletArc", {"start": v(-7.57, -137.06) * mm, "mid": v(-6.51, -136.62) * mm, "end": v(-6.07, -135.56) * mm});
            skPoint(sketch, "E348.visualSharp", {"position": v(-19.07, -143.06) * mm});
            skArc(sketch, "E348.filletArc", {"start": v(-17.57, -143.06) * mm, "mid": v(-18.63, -143.5) * mm, "end": v(-19.07, -144.56) * mm});
            skPoint(sketch, "E349.visualSharp", {"position": v(-6.07, -143.06) * mm});
            skArc(sketch, "E349.filletArc", {"start": v(-6.07, -144.56) * mm, "mid": v(-6.51, -143.5) * mm, "end": v(-7.57, -143.06) * mm});
            skPoint(sketch, "E350.visualSharp", {"position": v(-19.07, -156.06) * mm});
            skArc(sketch, "E350.filletArc", {"start": v(-19.07, -154.56) * mm, "mid": v(-18.63, -155.62) * mm, "end": v(-17.57, -156.06) * mm});
            skPoint(sketch, "E351.visualSharp", {"position": v(-6.07, -156.06) * mm});
            skArc(sketch, "E351.filletArc", {"start": v(-7.57, -156.06) * mm, "mid": v(-6.51, -155.62) * mm, "end": v(-6.07, -154.56) * mm});
            skPoint(sketch, "E352.visualSharp", {"position": v(-19.07, -162.06) * mm});
            skArc(sketch, "E352.filletArc", {"start": v(-17.57, -162.06) * mm, "mid": v(-18.63, -162.5) * mm, "end": v(-19.07, -163.56) * mm});
            skPoint(sketch, "E353.visualSharp", {"position": v(-6.07, -162.06) * mm});
            skArc(sketch, "E353.filletArc", {"start": v(-6.07, -163.56) * mm, "mid": v(-6.51, -162.5) * mm, "end": v(-7.57, -162.06) * mm});
            skPoint(sketch, "E354.visualSharp", {"position": v(-19.07, -175.06) * mm});
            skArc(sketch, "E354.filletArc", {"start": v(-19.07, -173.56) * mm, "mid": v(-18.63, -174.62) * mm, "end": v(-17.57, -175.06) * mm});
            skPoint(sketch, "E355.visualSharp", {"position": v(-6.07, -175.06) * mm});
            skArc(sketch, "E355.filletArc", {"start": v(-7.57, -175.06) * mm, "mid": v(-6.51, -174.62) * mm, "end": v(-6.07, -173.56) * mm});
            skPoint(sketch, "E356.visualSharp", {"position": v(-19.07, -181.06) * mm});
            skArc(sketch, "E356.filletArc", {"start": v(-17.57, -181.06) * mm, "mid": v(-18.63, -181.5) * mm, "end": v(-19.07, -182.56) * mm});
            skPoint(sketch, "E357.visualSharp", {"position": v(-6.07, -181.06) * mm});
            skArc(sketch, "E357.filletArc", {"start": v(-6.07, -182.56) * mm, "mid": v(-6.51, -181.5) * mm, "end": v(-7.57, -181.06) * mm});
            skPoint(sketch, "E358.visualSharp", {"position": v(-19.07, -194.06) * mm});
            skArc(sketch, "E358.filletArc", {"start": v(-19.07, -192.56) * mm, "mid": v(-18.63, -193.62) * mm, "end": v(-17.57, -194.06) * mm});
            skPoint(sketch, "E359.visualSharp", {"position": v(-6.07, -194.06) * mm});
            skArc(sketch, "E359.filletArc", {"start": v(-7.57, -194.06) * mm, "mid": v(-6.51, -193.62) * mm, "end": v(-6.07, -192.56) * mm});
            skPoint(sketch, "E360.visualSharp", {"position": v(-19.07, -200.06) * mm});
            skArc(sketch, "E360.filletArc", {"start": v(-17.57, -200.06) * mm, "mid": v(-18.63, -200.5) * mm, "end": v(-19.07, -201.56) * mm});
            skPoint(sketch, "E361.visualSharp", {"position": v(-6.07, -200.06) * mm});
            skArc(sketch, "E361.filletArc", {"start": v(-6.07, -201.56) * mm, "mid": v(-6.51, -200.5) * mm, "end": v(-7.57, -200.06) * mm});
            skPoint(sketch, "E362.visualSharp", {"position": v(-19.07, -213.06) * mm});
            skArc(sketch, "E362.filletArc", {"start": v(-19.07, -211.56) * mm, "mid": v(-18.63, -212.62) * mm, "end": v(-17.57, -213.06) * mm});
            skPoint(sketch, "E363.visualSharp", {"position": v(-6.07, -213.06) * mm});
            skArc(sketch, "E363.filletArc", {"start": v(-7.57, -213.06) * mm, "mid": v(-6.51, -212.62) * mm, "end": v(-6.07, -211.56) * mm});
            skPoint(sketch, "E364.visualSharp", {"position": v(-19.07, -219.06) * mm});
            skArc(sketch, "E364.filletArc", {"start": v(-17.57, -219.06) * mm, "mid": v(-18.63, -219.5) * mm, "end": v(-19.07, -220.56) * mm});
            skPoint(sketch, "E365.visualSharp", {"position": v(-6.07, -219.06) * mm});
            skArc(sketch, "E365.filletArc", {"start": v(-6.07, -220.56) * mm, "mid": v(-6.51, -219.5) * mm, "end": v(-7.57, -219.06) * mm});
            skPoint(sketch, "E366.visualSharp", {"position": v(-19.07, -232.06) * mm});
            skArc(sketch, "E366.filletArc", {"start": v(-19.07, -230.56) * mm, "mid": v(-18.63, -231.62) * mm, "end": v(-17.57, -232.06) * mm});
            skPoint(sketch, "E367.visualSharp", {"position": v(-6.07, -232.06) * mm});
            skArc(sketch, "E367.filletArc", {"start": v(-7.57, -232.06) * mm, "mid": v(-6.51, -231.62) * mm, "end": v(-6.07, -230.56) * mm});
            skPoint(sketch, "E368.visualSharp", {"position": v(-2.57, -124.06) * mm});
            skArc(sketch, "E368.filletArc", {"start": v(-1.07, -124.06) * mm, "mid": v(-2.13, -124.5) * mm, "end": v(-2.57, -125.56) * mm});
            skPoint(sketch, "E369.visualSharp", {"position": v(10.43, -124.06) * mm});
            skArc(sketch, "E369.filletArc", {"start": v(10.43, -125.56) * mm, "mid": v(9.99, -124.5) * mm, "end": v(8.93, -124.06) * mm});
            skPoint(sketch, "E370.visualSharp", {"position": v(-2.57, -137.06) * mm});
            skArc(sketch, "E370.filletArc", {"start": v(-2.57, -135.56) * mm, "mid": v(-2.13, -136.62) * mm, "end": v(-1.07, -137.06) * mm});
            skPoint(sketch, "E371.visualSharp", {"position": v(-2.57, -143.06) * mm});
            skArc(sketch, "E371.filletArc", {"start": v(-1.07, -143.06) * mm, "mid": v(-2.13, -143.5) * mm, "end": v(-2.57, -144.56) * mm});
            skPoint(sketch, "E372.visualSharp", {"position": v(10.43, -137.06) * mm});
            skArc(sketch, "E372.filletArc", {"start": v(8.93, -137.06) * mm, "mid": v(9.99, -136.62) * mm, "end": v(10.43, -135.56) * mm});
            skPoint(sketch, "E373.visualSharp", {"position": v(10.43, -143.06) * mm});
            skArc(sketch, "E373.filletArc", {"start": v(10.43, -144.56) * mm, "mid": v(9.99, -143.5) * mm, "end": v(8.93, -143.06) * mm});
            skPoint(sketch, "E374.visualSharp", {"position": v(-2.57, -156.06) * mm});
            skArc(sketch, "E374.filletArc", {"start": v(-2.57, -154.56) * mm, "mid": v(-2.13, -155.62) * mm, "end": v(-1.07, -156.06) * mm});
            skPoint(sketch, "E375.visualSharp", {"position": v(10.43, -156.06) * mm});
            skArc(sketch, "E375.filletArc", {"start": v(8.93, -156.06) * mm, "mid": v(9.99, -155.62) * mm, "end": v(10.43, -154.56) * mm});
            skPoint(sketch, "E376.visualSharp", {"position": v(-2.57, -162.06) * mm});
            skArc(sketch, "E376.filletArc", {"start": v(-1.07, -162.06) * mm, "mid": v(-2.13, -162.5) * mm, "end": v(-2.57, -163.56) * mm});
            skPoint(sketch, "E377.visualSharp", {"position": v(13.93, -162.06) * mm});
            skArc(sketch, "E377.filletArc", {"start": v(15.43, -162.06) * mm, "mid": v(14.37, -162.5) * mm, "end": v(13.93, -163.56) * mm});
            skPoint(sketch, "E378.visualSharp", {"position": v(30.43, -162.06) * mm});
            skArc(sketch, "E378.filletArc", {"start": v(31.93, -162.06) * mm, "mid": v(30.87, -162.5) * mm, "end": v(30.43, -163.56) * mm});
            skPoint(sketch, "E379.visualSharp", {"position": v(46.93, -162.06) * mm});
            skArc(sketch, "E379.filletArc", {"start": v(48.43, -162.06) * mm, "mid": v(47.37, -162.5) * mm, "end": v(46.93, -163.56) * mm});
            skPoint(sketch, "E380.visualSharp", {"position": v(63.43, -162.06) * mm});
            skArc(sketch, "E380.filletArc", {"start": v(64.93, -162.06) * mm, "mid": v(63.87, -162.5) * mm, "end": v(63.43, -163.56) * mm});
            skPoint(sketch, "E381.visualSharp", {"position": v(79.93, -162.06) * mm});
            skArc(sketch, "E381.filletArc", {"start": v(81.43, -162.06) * mm, "mid": v(80.37, -162.5) * mm, "end": v(79.93, -163.56) * mm});
            skPoint(sketch, "E382.visualSharp", {"position": v(96.43, -162.06) * mm});
            skArc(sketch, "E382.filletArc", {"start": v(97.93, -162.06) * mm, "mid": v(96.87, -162.5) * mm, "end": v(96.43, -163.56) * mm});
            skPoint(sketch, "E383.visualSharp", {"position": v(112.93, -162.06) * mm});
            skArc(sketch, "E383.filletArc", {"start": v(114.43, -162.06) * mm, "mid": v(113.37, -162.5) * mm, "end": v(112.93, -163.56) * mm});
            skPoint(sketch, "E384.visualSharp", {"position": v(129.43, -162.06) * mm});
            skArc(sketch, "E384.filletArc", {"start": v(130.93, -162.06) * mm, "mid": v(129.87, -162.5) * mm, "end": v(129.43, -163.56) * mm});
            skPoint(sketch, "E385.visualSharp", {"position": v(145.93, -162.06) * mm});
            skArc(sketch, "E385.filletArc", {"start": v(147.43, -162.06) * mm, "mid": v(146.37, -162.5) * mm, "end": v(145.93, -163.56) * mm});
            skPoint(sketch, "E386.visualSharp", {"position": v(162.43, -162.06) * mm});
            skArc(sketch, "E386.filletArc", {"start": v(163.93, -162.06) * mm, "mid": v(162.87, -162.5) * mm, "end": v(162.43, -163.56) * mm});
            skPoint(sketch, "E387.visualSharp", {"position": v(10.43, -162.06) * mm});
            skArc(sketch, "E387.filletArc", {"start": v(10.43, -163.56) * mm, "mid": v(9.99, -162.5) * mm, "end": v(8.93, -162.06) * mm});
            skPoint(sketch, "E388.visualSharp", {"position": v(-2.57, -175.06) * mm});
            skArc(sketch, "E388.filletArc", {"start": v(-2.57, -173.56) * mm, "mid": v(-2.13, -174.62) * mm, "end": v(-1.07, -175.06) * mm});
            skPoint(sketch, "E389.visualSharp", {"position": v(10.43, -175.06) * mm});
            skArc(sketch, "E389.filletArc", {"start": v(8.93, -175.06) * mm, "mid": v(9.99, -174.62) * mm, "end": v(10.43, -173.56) * mm});
            skPoint(sketch, "E390.visualSharp", {"position": v(-2.57, -181.06) * mm});
            skArc(sketch, "E390.filletArc", {"start": v(-1.07, -181.06) * mm, "mid": v(-2.13, -181.5) * mm, "end": v(-2.57, -182.56) * mm});
            skPoint(sketch, "E391.visualSharp", {"position": v(10.43, -181.06) * mm});
            skArc(sketch, "E391.filletArc", {"start": v(10.43, -182.56) * mm, "mid": v(9.99, -181.5) * mm, "end": v(8.93, -181.06) * mm});
            skPoint(sketch, "E392.visualSharp", {"position": v(-2.57, -194.06) * mm});
            skArc(sketch, "E392.filletArc", {"start": v(-2.57, -192.56) * mm, "mid": v(-2.13, -193.62) * mm, "end": v(-1.07, -194.06) * mm});
            skPoint(sketch, "E393.visualSharp", {"position": v(10.43, -194.06) * mm});
            skArc(sketch, "E393.filletArc", {"start": v(8.93, -194.06) * mm, "mid": v(9.99, -193.62) * mm, "end": v(10.43, -192.56) * mm});
            skPoint(sketch, "E394.visualSharp", {"position": v(-2.57, -200.06) * mm});
            skArc(sketch, "E394.filletArc", {"start": v(-1.07, -200.06) * mm, "mid": v(-2.13, -200.5) * mm, "end": v(-2.57, -201.56) * mm});
            skPoint(sketch, "E395.visualSharp", {"position": v(10.43, -200.06) * mm});
            skArc(sketch, "E395.filletArc", {"start": v(10.43, -201.56) * mm, "mid": v(9.99, -200.5) * mm, "end": v(8.93, -200.06) * mm});
            skPoint(sketch, "E396.visualSharp", {"position": v(-2.57, -213.06) * mm});
            skArc(sketch, "E396.filletArc", {"start": v(-2.57, -211.56) * mm, "mid": v(-2.13, -212.62) * mm, "end": v(-1.07, -213.06) * mm});
            skPoint(sketch, "E397.visualSharp", {"position": v(10.43, -213.06) * mm});
            skArc(sketch, "E397.filletArc", {"start": v(8.93, -213.06) * mm, "mid": v(9.99, -212.62) * mm, "end": v(10.43, -211.56) * mm});
            skPoint(sketch, "E398.visualSharp", {"position": v(-2.57, -219.06) * mm});
            skArc(sketch, "E398.filletArc", {"start": v(-1.07, -219.06) * mm, "mid": v(-2.13, -219.5) * mm, "end": v(-2.57, -220.56) * mm});
            skPoint(sketch, "E399.visualSharp", {"position": v(10.43, -219.06) * mm});
            skArc(sketch, "E399.filletArc", {"start": v(10.43, -220.56) * mm, "mid": v(9.99, -219.5) * mm, "end": v(8.93, -219.06) * mm});
            skPoint(sketch, "E400.visualSharp", {"position": v(-2.57, -232.06) * mm});
            skArc(sketch, "E400.filletArc", {"start": v(-2.57, -230.56) * mm, "mid": v(-2.13, -231.62) * mm, "end": v(-1.07, -232.06) * mm});
            skPoint(sketch, "E401.visualSharp", {"position": v(10.43, -232.06) * mm});
            skArc(sketch, "E401.filletArc", {"start": v(8.93, -232.06) * mm, "mid": v(9.99, -231.62) * mm, "end": v(10.43, -230.56) * mm});
            skPoint(sketch, "E402.visualSharp", {"position": v(13.93, -124.06) * mm});
            skArc(sketch, "E402.filletArc", {"start": v(15.43, -124.06) * mm, "mid": v(14.37, -124.5) * mm, "end": v(13.93, -125.56) * mm});
            skPoint(sketch, "E403.visualSharp", {"position": v(26.93, -124.06) * mm});
            skArc(sketch, "E403.filletArc", {"start": v(26.93, -125.56) * mm, "mid": v(26.49, -124.5) * mm, "end": v(25.43, -124.06) * mm});
            skPoint(sketch, "E404.visualSharp", {"position": v(13.93, -137.06) * mm});
            skArc(sketch, "E404.filletArc", {"start": v(13.93, -135.56) * mm, "mid": v(14.37, -136.62) * mm, "end": v(15.43, -137.06) * mm});
            skPoint(sketch, "E405.visualSharp", {"position": v(26.93, -137.06) * mm});
            skArc(sketch, "E405.filletArc", {"start": v(25.43, -137.06) * mm, "mid": v(26.49, -136.62) * mm, "end": v(26.93, -135.56) * mm});
            skPoint(sketch, "E406.visualSharp", {"position": v(13.93, -143.06) * mm});
            skArc(sketch, "E406.filletArc", {"start": v(15.43, -143.06) * mm, "mid": v(14.37, -143.5) * mm, "end": v(13.93, -144.56) * mm});
            skPoint(sketch, "E407.visualSharp", {"position": v(26.93, -143.06) * mm});
            skArc(sketch, "E407.filletArc", {"start": v(26.93, -144.56) * mm, "mid": v(26.49, -143.5) * mm, "end": v(25.43, -143.06) * mm});
            skPoint(sketch, "E408.visualSharp", {"position": v(13.93, -156.06) * mm});
            skArc(sketch, "E408.filletArc", {"start": v(13.93, -154.56) * mm, "mid": v(14.37, -155.62) * mm, "end": v(15.43, -156.06) * mm});
            skPoint(sketch, "E409.visualSharp", {"position": v(26.93, -156.06) * mm});
            skArc(sketch, "E409.filletArc", {"start": v(25.43, -156.06) * mm, "mid": v(26.49, -155.62) * mm, "end": v(26.93, -154.56) * mm});
            skPoint(sketch, "E410.visualSharp", {"position": v(26.93, -162.06) * mm});
            skArc(sketch, "E410.filletArc", {"start": v(26.93, -163.56) * mm, "mid": v(26.49, -162.5) * mm, "end": v(25.43, -162.06) * mm});
            skPoint(sketch, "E411.visualSharp", {"position": v(13.93, -175.06) * mm});
            skArc(sketch, "E411.filletArc", {"start": v(13.93, -173.56) * mm, "mid": v(14.37, -174.62) * mm, "end": v(15.43, -175.06) * mm});
            skPoint(sketch, "E412.visualSharp", {"position": v(26.93, -175.06) * mm});
            skArc(sketch, "E412.filletArc", {"start": v(25.43, -175.06) * mm, "mid": v(26.49, -174.62) * mm, "end": v(26.93, -173.56) * mm});
            skPoint(sketch, "E413.visualSharp", {"position": v(13.93, -181.06) * mm});
            skArc(sketch, "E413.filletArc", {"start": v(15.43, -181.06) * mm, "mid": v(14.37, -181.5) * mm, "end": v(13.93, -182.56) * mm});
            skPoint(sketch, "E414.visualSharp", {"position": v(26.93, -181.06) * mm});
            skArc(sketch, "E414.filletArc", {"start": v(26.93, -182.56) * mm, "mid": v(26.49, -181.5) * mm, "end": v(25.43, -181.06) * mm});
            skPoint(sketch, "E415.visualSharp", {"position": v(13.93, -194.06) * mm});
            skArc(sketch, "E415.filletArc", {"start": v(13.93, -192.56) * mm, "mid": v(14.37, -193.62) * mm, "end": v(15.43, -194.06) * mm});
            skPoint(sketch, "E416.visualSharp", {"position": v(26.93, -194.06) * mm});
            skArc(sketch, "E416.filletArc", {"start": v(25.43, -194.06) * mm, "mid": v(26.49, -193.62) * mm, "end": v(26.93, -192.56) * mm});
            skPoint(sketch, "E417.visualSharp", {"position": v(13.93, -200.06) * mm});
            skArc(sketch, "E417.filletArc", {"start": v(15.43, -200.06) * mm, "mid": v(14.37, -200.5) * mm, "end": v(13.93, -201.56) * mm});
            skPoint(sketch, "E418.visualSharp", {"position": v(26.93, -200.06) * mm});
            skArc(sketch, "E418.filletArc", {"start": v(26.93, -201.56) * mm, "mid": v(26.49, -200.5) * mm, "end": v(25.43, -200.06) * mm});
            skPoint(sketch, "E419.visualSharp", {"position": v(13.93, -213.06) * mm});
            skArc(sketch, "E419.filletArc", {"start": v(13.93, -211.56) * mm, "mid": v(14.37, -212.62) * mm, "end": v(15.43, -213.06) * mm});
            skPoint(sketch, "E420.visualSharp", {"position": v(26.93, -213.06) * mm});
            skArc(sketch, "E420.filletArc", {"start": v(25.43, -213.06) * mm, "mid": v(26.49, -212.62) * mm, "end": v(26.93, -211.56) * mm});
            skPoint(sketch, "E421.visualSharp", {"position": v(13.93, -219.06) * mm});
            skArc(sketch, "E421.filletArc", {"start": v(15.43, -219.06) * mm, "mid": v(14.37, -219.5) * mm, "end": v(13.93, -220.56) * mm});
            skPoint(sketch, "E422.visualSharp", {"position": v(26.93, -219.06) * mm});
            skArc(sketch, "E422.filletArc", {"start": v(26.93, -220.56) * mm, "mid": v(26.49, -219.5) * mm, "end": v(25.43, -219.06) * mm});
            skPoint(sketch, "E423.visualSharp", {"position": v(13.93, -232.06) * mm});
            skArc(sketch, "E423.filletArc", {"start": v(13.93, -230.56) * mm, "mid": v(14.37, -231.62) * mm, "end": v(15.43, -232.06) * mm});
            skPoint(sketch, "E424.visualSharp", {"position": v(26.93, -232.06) * mm});
            skArc(sketch, "E424.filletArc", {"start": v(25.43, -232.06) * mm, "mid": v(26.49, -231.62) * mm, "end": v(26.93, -230.56) * mm});
            skPoint(sketch, "E425.visualSharp", {"position": v(30.43, -124.06) * mm});
            skArc(sketch, "E425.filletArc", {"start": v(31.93, -124.06) * mm, "mid": v(30.87, -124.5) * mm, "end": v(30.43, -125.56) * mm});
            skPoint(sketch, "E426.visualSharp", {"position": v(43.43, -124.06) * mm});
            skArc(sketch, "E426.filletArc", {"start": v(43.43, -125.56) * mm, "mid": v(42.99, -124.5) * mm, "end": v(41.93, -124.06) * mm});
            skPoint(sketch, "E427.visualSharp", {"position": v(30.43, -137.06) * mm});
            skArc(sketch, "E427.filletArc", {"start": v(30.43, -135.56) * mm, "mid": v(30.87, -136.62) * mm, "end": v(31.93, -137.06) * mm});
            skPoint(sketch, "E428.visualSharp", {"position": v(43.43, -137.06) * mm});
            skArc(sketch, "E428.filletArc", {"start": v(41.93, -137.06) * mm, "mid": v(42.99, -136.62) * mm, "end": v(43.43, -135.56) * mm});
            skPoint(sketch, "E429.visualSharp", {"position": v(30.43, -143.06) * mm});
            skArc(sketch, "E429.filletArc", {"start": v(31.93, -143.06) * mm, "mid": v(30.87, -143.5) * mm, "end": v(30.43, -144.56) * mm});
            skPoint(sketch, "E430.visualSharp", {"position": v(43.43, -143.06) * mm});
            skArc(sketch, "E430.filletArc", {"start": v(43.43, -144.56) * mm, "mid": v(42.99, -143.5) * mm, "end": v(41.93, -143.06) * mm});
            skPoint(sketch, "E431.visualSharp", {"position": v(30.43, -156.06) * mm});
            skArc(sketch, "E431.filletArc", {"start": v(30.43, -154.56) * mm, "mid": v(30.87, -155.62) * mm, "end": v(31.93, -156.06) * mm});
            skPoint(sketch, "E432.visualSharp", {"position": v(43.43, -156.06) * mm});
            skArc(sketch, "E432.filletArc", {"start": v(41.93, -156.06) * mm, "mid": v(42.99, -155.62) * mm, "end": v(43.43, -154.56) * mm});
            skPoint(sketch, "E433.visualSharp", {"position": v(43.43, -162.06) * mm});
            skArc(sketch, "E433.filletArc", {"start": v(43.43, -163.56) * mm, "mid": v(42.99, -162.5) * mm, "end": v(41.93, -162.06) * mm});
            skPoint(sketch, "E434.visualSharp", {"position": v(30.43, -175.06) * mm});
            skArc(sketch, "E434.filletArc", {"start": v(30.43, -173.56) * mm, "mid": v(30.87, -174.62) * mm, "end": v(31.93, -175.06) * mm});
            skPoint(sketch, "E435.visualSharp", {"position": v(43.43, -175.06) * mm});
            skArc(sketch, "E435.filletArc", {"start": v(41.93, -175.06) * mm, "mid": v(42.99, -174.62) * mm, "end": v(43.43, -173.56) * mm});
            skPoint(sketch, "E436.visualSharp", {"position": v(30.43, -181.06) * mm});
            skArc(sketch, "E436.filletArc", {"start": v(31.93, -181.06) * mm, "mid": v(30.87, -181.5) * mm, "end": v(30.43, -182.56) * mm});
            skPoint(sketch, "E437.visualSharp", {"position": v(43.43, -181.06) * mm});
            skArc(sketch, "E437.filletArc", {"start": v(43.43, -182.56) * mm, "mid": v(42.99, -181.5) * mm, "end": v(41.93, -181.06) * mm});
            skPoint(sketch, "E438.visualSharp", {"position": v(30.43, -194.06) * mm});
            skArc(sketch, "E438.filletArc", {"start": v(30.43, -192.56) * mm, "mid": v(30.87, -193.62) * mm, "end": v(31.93, -194.06) * mm});
            skPoint(sketch, "E439.visualSharp", {"position": v(43.43, -194.06) * mm});
            skArc(sketch, "E439.filletArc", {"start": v(41.93, -194.06) * mm, "mid": v(42.99, -193.62) * mm, "end": v(43.43, -192.56) * mm});
            skPoint(sketch, "E440.visualSharp", {"position": v(30.43, -200.06) * mm});
            skArc(sketch, "E440.filletArc", {"start": v(31.93, -200.06) * mm, "mid": v(30.87, -200.5) * mm, "end": v(30.43, -201.56) * mm});
            skPoint(sketch, "E441.visualSharp", {"position": v(43.43, -200.06) * mm});
            skArc(sketch, "E441.filletArc", {"start": v(43.43, -201.56) * mm, "mid": v(42.99, -200.5) * mm, "end": v(41.93, -200.06) * mm});
            skPoint(sketch, "E442.visualSharp", {"position": v(43.43, -213.06) * mm});
            skArc(sketch, "E442.filletArc", {"start": v(41.93, -213.06) * mm, "mid": v(42.99, -212.62) * mm, "end": v(43.43, -211.56) * mm});
            skPoint(sketch, "E443.visualSharp", {"position": v(30.43, -213.06) * mm});
            skArc(sketch, "E443.filletArc", {"start": v(30.43, -211.56) * mm, "mid": v(30.87, -212.62) * mm, "end": v(31.93, -213.06) * mm});
            skPoint(sketch, "E444.visualSharp", {"position": v(30.43, -219.06) * mm});
            skArc(sketch, "E444.filletArc", {"start": v(31.93, -219.06) * mm, "mid": v(30.87, -219.5) * mm, "end": v(30.43, -220.56) * mm});
            skPoint(sketch, "E445.visualSharp", {"position": v(43.43, -219.06) * mm});
            skArc(sketch, "E445.filletArc", {"start": v(43.43, -220.56) * mm, "mid": v(42.99, -219.5) * mm, "end": v(41.93, -219.06) * mm});
            skPoint(sketch, "E446.visualSharp", {"position": v(30.43, -232.06) * mm});
            skArc(sketch, "E446.filletArc", {"start": v(30.43, -230.56) * mm, "mid": v(30.87, -231.62) * mm, "end": v(31.93, -232.06) * mm});
            skPoint(sketch, "E447.visualSharp", {"position": v(43.43, -232.06) * mm});
            skArc(sketch, "E447.filletArc", {"start": v(41.93, -232.06) * mm, "mid": v(42.99, -231.62) * mm, "end": v(43.43, -230.56) * mm});
            skPoint(sketch, "E448.visualSharp", {"position": v(46.93, -124.06) * mm});
            skArc(sketch, "E448.filletArc", {"start": v(48.43, -124.06) * mm, "mid": v(47.37, -124.5) * mm, "end": v(46.93, -125.56) * mm});
            skPoint(sketch, "E449.visualSharp", {"position": v(59.93, -124.06) * mm});
            skArc(sketch, "E449.filletArc", {"start": v(59.93, -125.56) * mm, "mid": v(59.49, -124.5) * mm, "end": v(58.43, -124.06) * mm});
            skPoint(sketch, "E450.visualSharp", {"position": v(46.93, -137.06) * mm});
            skArc(sketch, "E450.filletArc", {"start": v(46.93, -135.56) * mm, "mid": v(47.37, -136.62) * mm, "end": v(48.43, -137.06) * mm});
            skPoint(sketch, "E451.visualSharp", {"position": v(59.93, -137.06) * mm});
            skArc(sketch, "E451.filletArc", {"start": v(58.43, -137.06) * mm, "mid": v(59.49, -136.62) * mm, "end": v(59.93, -135.56) * mm});
            skPoint(sketch, "E452.visualSharp", {"position": v(46.93, -143.06) * mm});
            skArc(sketch, "E452.filletArc", {"start": v(48.43, -143.06) * mm, "mid": v(47.37, -143.5) * mm, "end": v(46.93, -144.56) * mm});
            skPoint(sketch, "E453.visualSharp", {"position": v(46.93, -156.06) * mm});
            skArc(sketch, "E453.filletArc", {"start": v(46.93, -154.56) * mm, "mid": v(47.37, -155.62) * mm, "end": v(48.43, -156.06) * mm});
            skPoint(sketch, "E454.visualSharp", {"position": v(59.93, -143.06) * mm});
            skArc(sketch, "E454.filletArc", {"start": v(59.93, -144.56) * mm, "mid": v(59.49, -143.5) * mm, "end": v(58.43, -143.06) * mm});
            skPoint(sketch, "E455.visualSharp", {"position": v(59.93, -156.06) * mm});
            skArc(sketch, "E455.filletArc", {"start": v(58.43, -156.06) * mm, "mid": v(59.49, -155.62) * mm, "end": v(59.93, -154.56) * mm});
            skPoint(sketch, "E456.visualSharp", {"position": v(59.93, -162.06) * mm});
            skArc(sketch, "E456.filletArc", {"start": v(59.93, -163.56) * mm, "mid": v(59.49, -162.5) * mm, "end": v(58.43, -162.06) * mm});
            skPoint(sketch, "E457.visualSharp", {"position": v(46.93, -175.06) * mm});
            skArc(sketch, "E457.filletArc", {"start": v(46.93, -173.56) * mm, "mid": v(47.37, -174.62) * mm, "end": v(48.43, -175.06) * mm});
            skPoint(sketch, "E458.visualSharp", {"position": v(59.93, -175.06) * mm});
            skArc(sketch, "E458.filletArc", {"start": v(58.43, -175.06) * mm, "mid": v(59.49, -174.62) * mm, "end": v(59.93, -173.56) * mm});
            skPoint(sketch, "E459.visualSharp", {"position": v(46.93, -181.06) * mm});
            skArc(sketch, "E459.filletArc", {"start": v(48.43, -181.06) * mm, "mid": v(47.37, -181.5) * mm, "end": v(46.93, -182.56) * mm});
            skPoint(sketch, "E460.visualSharp", {"position": v(59.93, -181.06) * mm});
            skArc(sketch, "E460.filletArc", {"start": v(59.93, -182.56) * mm, "mid": v(59.49, -181.5) * mm, "end": v(58.43, -181.06) * mm});
            skPoint(sketch, "E461.visualSharp", {"position": v(46.93, -194.06) * mm});
            skArc(sketch, "E461.filletArc", {"start": v(46.93, -192.56) * mm, "mid": v(47.37, -193.62) * mm, "end": v(48.43, -194.06) * mm});
            skPoint(sketch, "E462.visualSharp", {"position": v(59.93, -194.06) * mm});
            skArc(sketch, "E462.filletArc", {"start": v(58.43, -194.06) * mm, "mid": v(59.49, -193.62) * mm, "end": v(59.93, -192.56) * mm});
            skPoint(sketch, "E463.visualSharp", {"position": v(46.93, -200.06) * mm});
            skArc(sketch, "E463.filletArc", {"start": v(48.43, -200.06) * mm, "mid": v(47.37, -200.5) * mm, "end": v(46.93, -201.56) * mm});
            skPoint(sketch, "E464.visualSharp", {"position": v(59.93, -200.06) * mm});
            skArc(sketch, "E464.filletArc", {"start": v(59.93, -201.56) * mm, "mid": v(59.49, -200.5) * mm, "end": v(58.43, -200.06) * mm});
            skPoint(sketch, "E465.visualSharp", {"position": v(46.93, -213.06) * mm});
            skArc(sketch, "E465.filletArc", {"start": v(46.93, -211.56) * mm, "mid": v(47.37, -212.62) * mm, "end": v(48.43, -213.06) * mm});
            skPoint(sketch, "E466.visualSharp", {"position": v(59.93, -213.06) * mm});
            skArc(sketch, "E466.filletArc", {"start": v(58.43, -213.06) * mm, "mid": v(59.49, -212.62) * mm, "end": v(59.93, -211.56) * mm});
            skPoint(sketch, "E467.visualSharp", {"position": v(46.93, -219.06) * mm});
            skArc(sketch, "E467.filletArc", {"start": v(48.43, -219.06) * mm, "mid": v(47.37, -219.5) * mm, "end": v(46.93, -220.56) * mm});
            skPoint(sketch, "E468.visualSharp", {"position": v(59.93, -219.06) * mm});
            skArc(sketch, "E468.filletArc", {"start": v(59.93, -220.56) * mm, "mid": v(59.49, -219.5) * mm, "end": v(58.43, -219.06) * mm});
            skPoint(sketch, "E469.visualSharp", {"position": v(46.93, -232.06) * mm});
            skArc(sketch, "E469.filletArc", {"start": v(46.93, -230.56) * mm, "mid": v(47.37, -231.62) * mm, "end": v(48.43, -232.06) * mm});
            skPoint(sketch, "E470.visualSharp", {"position": v(59.93, -232.06) * mm});
            skArc(sketch, "E470.filletArc", {"start": v(58.43, -232.06) * mm, "mid": v(59.49, -231.62) * mm, "end": v(59.93, -230.56) * mm});
            skPoint(sketch, "E471.visualSharp", {"position": v(63.43, -124.06) * mm});
            skArc(sketch, "E471.filletArc", {"start": v(64.93, -124.06) * mm, "mid": v(63.87, -124.5) * mm, "end": v(63.43, -125.56) * mm});
            skPoint(sketch, "E472.visualSharp", {"position": v(76.43, -124.06) * mm});
            skArc(sketch, "E472.filletArc", {"start": v(76.43, -125.56) * mm, "mid": v(75.99, -124.5) * mm, "end": v(74.93, -124.06) * mm});
            skPoint(sketch, "E473.visualSharp", {"position": v(63.43, -137.06) * mm});
            skArc(sketch, "E473.filletArc", {"start": v(63.43, -135.56) * mm, "mid": v(63.87, -136.62) * mm, "end": v(64.93, -137.06) * mm});
            skPoint(sketch, "E474.visualSharp", {"position": v(76.43, -137.06) * mm});
            skArc(sketch, "E474.filletArc", {"start": v(74.93, -137.06) * mm, "mid": v(75.99, -136.62) * mm, "end": v(76.43, -135.56) * mm});
            skPoint(sketch, "E475.visualSharp", {"position": v(63.43, -143.06) * mm});
            skArc(sketch, "E475.filletArc", {"start": v(64.93, -143.06) * mm, "mid": v(63.87, -143.5) * mm, "end": v(63.43, -144.56) * mm});
            skPoint(sketch, "E476.visualSharp", {"position": v(76.43, -143.06) * mm});
            skArc(sketch, "E476.filletArc", {"start": v(76.43, -144.56) * mm, "mid": v(75.99, -143.5) * mm, "end": v(74.93, -143.06) * mm});
            skPoint(sketch, "E477.visualSharp", {"position": v(63.43, -156.06) * mm});
            skArc(sketch, "E477.filletArc", {"start": v(63.43, -154.56) * mm, "mid": v(63.87, -155.62) * mm, "end": v(64.93, -156.06) * mm});
            skPoint(sketch, "E478.visualSharp", {"position": v(76.43, -156.06) * mm});
            skArc(sketch, "E478.filletArc", {"start": v(74.93, -156.06) * mm, "mid": v(75.99, -155.62) * mm, "end": v(76.43, -154.56) * mm});
            skPoint(sketch, "E479.visualSharp", {"position": v(76.43, -162.06) * mm});
            skArc(sketch, "E479.filletArc", {"start": v(76.43, -163.56) * mm, "mid": v(75.99, -162.5) * mm, "end": v(74.93, -162.06) * mm});
            skPoint(sketch, "E480.visualSharp", {"position": v(63.43, -175.06) * mm});
            skArc(sketch, "E480.filletArc", {"start": v(63.43, -173.56) * mm, "mid": v(63.87, -174.62) * mm, "end": v(64.93, -175.06) * mm});
            skPoint(sketch, "E481.visualSharp", {"position": v(76.43, -175.06) * mm});
            skArc(sketch, "E481.filletArc", {"start": v(74.93, -175.06) * mm, "mid": v(75.99, -174.62) * mm, "end": v(76.43, -173.56) * mm});
            skPoint(sketch, "E482.visualSharp", {"position": v(63.43, -181.06) * mm});
            skArc(sketch, "E482.filletArc", {"start": v(64.93, -181.06) * mm, "mid": v(63.87, -181.5) * mm, "end": v(63.43, -182.56) * mm});
            skPoint(sketch, "E483.visualSharp", {"position": v(76.43, -181.06) * mm});
            skArc(sketch, "E483.filletArc", {"start": v(76.43, -182.56) * mm, "mid": v(75.99, -181.5) * mm, "end": v(74.93, -181.06) * mm});
            skPoint(sketch, "E484.visualSharp", {"position": v(63.43, -194.06) * mm});
            skArc(sketch, "E484.filletArc", {"start": v(63.43, -192.56) * mm, "mid": v(63.87, -193.62) * mm, "end": v(64.93, -194.06) * mm});
            skPoint(sketch, "E485.visualSharp", {"position": v(76.43, -194.06) * mm});
            skArc(sketch, "E485.filletArc", {"start": v(74.93, -194.06) * mm, "mid": v(75.99, -193.62) * mm, "end": v(76.43, -192.56) * mm});
            skPoint(sketch, "E486.visualSharp", {"position": v(63.43, -200.06) * mm});
            skArc(sketch, "E486.filletArc", {"start": v(64.93, -200.06) * mm, "mid": v(63.87, -200.5) * mm, "end": v(63.43, -201.56) * mm});
            skPoint(sketch, "E487.visualSharp", {"position": v(76.43, -200.06) * mm});
            skArc(sketch, "E487.filletArc", {"start": v(76.43, -201.56) * mm, "mid": v(75.99, -200.5) * mm, "end": v(74.93, -200.06) * mm});
            skPoint(sketch, "E488.visualSharp", {"position": v(63.43, -213.06) * mm});
            skArc(sketch, "E488.filletArc", {"start": v(63.43, -211.56) * mm, "mid": v(63.87, -212.62) * mm, "end": v(64.93, -213.06) * mm});
            skPoint(sketch, "E489.visualSharp", {"position": v(76.43, -213.06) * mm});
            skArc(sketch, "E489.filletArc", {"start": v(74.93, -213.06) * mm, "mid": v(75.99, -212.62) * mm, "end": v(76.43, -211.56) * mm});
            skPoint(sketch, "E490.visualSharp", {"position": v(63.43, -219.06) * mm});
            skArc(sketch, "E490.filletArc", {"start": v(64.93, -219.06) * mm, "mid": v(63.87, -219.5) * mm, "end": v(63.43, -220.56) * mm});
            skPoint(sketch, "E491.visualSharp", {"position": v(76.43, -219.06) * mm});
            skArc(sketch, "E491.filletArc", {"start": v(76.43, -220.56) * mm, "mid": v(75.99, -219.5) * mm, "end": v(74.93, -219.06) * mm});
            skPoint(sketch, "E492.visualSharp", {"position": v(63.43, -232.06) * mm});
            skArc(sketch, "E492.filletArc", {"start": v(63.43, -230.56) * mm, "mid": v(63.87, -231.62) * mm, "end": v(64.93, -232.06) * mm});
            skPoint(sketch, "E493.visualSharp", {"position": v(76.43, -232.06) * mm});
            skArc(sketch, "E493.filletArc", {"start": v(74.93, -232.06) * mm, "mid": v(75.99, -231.62) * mm, "end": v(76.43, -230.56) * mm});
            skPoint(sketch, "E494.visualSharp", {"position": v(79.93, -124.06) * mm});
            skArc(sketch, "E494.filletArc", {"start": v(81.43, -124.06) * mm, "mid": v(80.37, -124.5) * mm, "end": v(79.93, -125.56) * mm});
            skPoint(sketch, "E495.visualSharp", {"position": v(92.93, -124.06) * mm});
            skArc(sketch, "E495.filletArc", {"start": v(92.93, -125.56) * mm, "mid": v(92.49, -124.5) * mm, "end": v(91.43, -124.06) * mm});
            skPoint(sketch, "E496.visualSharp", {"position": v(79.93, -137.06) * mm});
            skArc(sketch, "E496.filletArc", {"start": v(79.93, -135.56) * mm, "mid": v(80.37, -136.62) * mm, "end": v(81.43, -137.06) * mm});
            skPoint(sketch, "E497.visualSharp", {"position": v(92.93, -137.06) * mm});
            skArc(sketch, "E497.filletArc", {"start": v(91.43, -137.06) * mm, "mid": v(92.49, -136.62) * mm, "end": v(92.93, -135.56) * mm});
            skPoint(sketch, "E498.visualSharp", {"position": v(96.43, -124.06) * mm});
            skArc(sketch, "E498.filletArc", {"start": v(97.93, -124.06) * mm, "mid": v(96.87, -124.5) * mm, "end": v(96.43, -125.56) * mm});
            skPoint(sketch, "E499.visualSharp", {"position": v(109.43, -124.06) * mm});
            skArc(sketch, "E499.filletArc", {"start": v(109.43, -125.56) * mm, "mid": v(108.99, -124.5) * mm, "end": v(107.93, -124.06) * mm});
            skPoint(sketch, "E500.visualSharp", {"position": v(96.43, -137.06) * mm});
            skArc(sketch, "E500.filletArc", {"start": v(96.43, -135.56) * mm, "mid": v(96.87, -136.62) * mm, "end": v(97.93, -137.06) * mm});
            skPoint(sketch, "E501.visualSharp", {"position": v(109.43, -137.06) * mm});
            skArc(sketch, "E501.filletArc", {"start": v(107.93, -137.06) * mm, "mid": v(108.99, -136.62) * mm, "end": v(109.43, -135.56) * mm});
            skPoint(sketch, "E502.visualSharp", {"position": v(112.93, -124.06) * mm});
            skArc(sketch, "E502.filletArc", {"start": v(114.43, -124.06) * mm, "mid": v(113.37, -124.5) * mm, "end": v(112.93, -125.56) * mm});
            skPoint(sketch, "E503.visualSharp", {"position": v(125.93, -124.06) * mm});
            skArc(sketch, "E503.filletArc", {"start": v(125.93, -125.56) * mm, "mid": v(125.49, -124.5) * mm, "end": v(124.43, -124.06) * mm});
            skPoint(sketch, "E504.visualSharp", {"position": v(112.93, -137.06) * mm});
            skArc(sketch, "E504.filletArc", {"start": v(112.93, -135.56) * mm, "mid": v(113.37, -136.62) * mm, "end": v(114.43, -137.06) * mm});
            skPoint(sketch, "E505.visualSharp", {"position": v(125.93, -137.06) * mm});
            skArc(sketch, "E505.filletArc", {"start": v(124.43, -137.06) * mm, "mid": v(125.49, -136.62) * mm, "end": v(125.93, -135.56) * mm});
            skPoint(sketch, "E506.visualSharp", {"position": v(129.43, -124.06) * mm});
            skArc(sketch, "E506.filletArc", {"start": v(130.93, -124.06) * mm, "mid": v(129.87, -124.5) * mm, "end": v(129.43, -125.56) * mm});
            skPoint(sketch, "E507.visualSharp", {"position": v(142.43, -124.06) * mm});
            skArc(sketch, "E507.filletArc", {"start": v(142.43, -125.56) * mm, "mid": v(141.99, -124.5) * mm, "end": v(140.93, -124.06) * mm});
            skPoint(sketch, "E508.visualSharp", {"position": v(129.43, -137.06) * mm});
            skArc(sketch, "E508.filletArc", {"start": v(129.43, -135.56) * mm, "mid": v(129.87, -136.62) * mm, "end": v(130.93, -137.06) * mm});
            skPoint(sketch, "E509.visualSharp", {"position": v(142.43, -137.06) * mm});
            skArc(sketch, "E509.filletArc", {"start": v(140.93, -137.06) * mm, "mid": v(141.99, -136.62) * mm, "end": v(142.43, -135.56) * mm});
            skPoint(sketch, "E510.visualSharp", {"position": v(145.93, -124.06) * mm});
            skArc(sketch, "E510.filletArc", {"start": v(147.43, -124.06) * mm, "mid": v(146.37, -124.5) * mm, "end": v(145.93, -125.56) * mm});
            skPoint(sketch, "E511.visualSharp", {"position": v(158.93, -124.06) * mm});
            skArc(sketch, "E511.filletArc", {"start": v(158.93, -125.56) * mm, "mid": v(158.49, -124.5) * mm, "end": v(157.43, -124.06) * mm});
            skPoint(sketch, "E512.visualSharp", {"position": v(145.93, -137.06) * mm});
            skArc(sketch, "E512.filletArc", {"start": v(145.93, -135.56) * mm, "mid": v(146.37, -136.62) * mm, "end": v(147.43, -137.06) * mm});
            skPoint(sketch, "E513.visualSharp", {"position": v(158.93, -137.06) * mm});
            skArc(sketch, "E513.filletArc", {"start": v(157.43, -137.06) * mm, "mid": v(158.49, -136.62) * mm, "end": v(158.93, -135.56) * mm});
            skPoint(sketch, "E514.visualSharp", {"position": v(162.43, -124.06) * mm});
            skArc(sketch, "E514.filletArc", {"start": v(163.93, -124.06) * mm, "mid": v(162.87, -124.5) * mm, "end": v(162.43, -125.56) * mm});
            skPoint(sketch, "E515.visualSharp", {"position": v(175.43, -124.06) * mm});
            skArc(sketch, "E515.filletArc", {"start": v(175.43, -125.56) * mm, "mid": v(174.99, -124.5) * mm, "end": v(173.93, -124.06) * mm});
            skPoint(sketch, "E516.visualSharp", {"position": v(162.43, -137.06) * mm});
            skArc(sketch, "E516.filletArc", {"start": v(162.43, -135.56) * mm, "mid": v(162.87, -136.62) * mm, "end": v(163.93, -137.06) * mm});
            skPoint(sketch, "E517.visualSharp", {"position": v(175.43, -137.06) * mm});
            skArc(sketch, "E517.filletArc", {"start": v(173.93, -137.06) * mm, "mid": v(174.99, -136.62) * mm, "end": v(175.43, -135.56) * mm});
            skPoint(sketch, "E518.visualSharp", {"position": v(79.93, -143.06) * mm});
            skArc(sketch, "E518.filletArc", {"start": v(81.43, -143.06) * mm, "mid": v(80.37, -143.5) * mm, "end": v(79.93, -144.56) * mm});
            skPoint(sketch, "E519.visualSharp", {"position": v(92.93, -143.06) * mm});
            skArc(sketch, "E519.filletArc", {"start": v(92.93, -144.56) * mm, "mid": v(92.49, -143.5) * mm, "end": v(91.43, -143.06) * mm});
            skPoint(sketch, "E520.visualSharp", {"position": v(79.93, -156.06) * mm});
            skArc(sketch, "E520.filletArc", {"start": v(79.93, -154.56) * mm, "mid": v(80.37, -155.62) * mm, "end": v(81.43, -156.06) * mm});
            skPoint(sketch, "E521.visualSharp", {"position": v(92.93, -156.06) * mm});
            skArc(sketch, "E521.filletArc", {"start": v(91.43, -156.06) * mm, "mid": v(92.49, -155.62) * mm, "end": v(92.93, -154.56) * mm});
            skPoint(sketch, "E522.visualSharp", {"position": v(96.43, -143.06) * mm});
            skArc(sketch, "E522.filletArc", {"start": v(97.93, -143.06) * mm, "mid": v(96.87, -143.5) * mm, "end": v(96.43, -144.56) * mm});
            skPoint(sketch, "E523.visualSharp", {"position": v(109.43, -143.06) * mm});
            skArc(sketch, "E523.filletArc", {"start": v(109.43, -144.56) * mm, "mid": v(108.99, -143.5) * mm, "end": v(107.93, -143.06) * mm});
            skPoint(sketch, "E524.visualSharp", {"position": v(96.43, -156.06) * mm});
            skArc(sketch, "E524.filletArc", {"start": v(96.43, -154.56) * mm, "mid": v(96.87, -155.62) * mm, "end": v(97.93, -156.06) * mm});
            skPoint(sketch, "E525.visualSharp", {"position": v(109.43, -156.06) * mm});
            skArc(sketch, "E525.filletArc", {"start": v(107.93, -156.06) * mm, "mid": v(108.99, -155.62) * mm, "end": v(109.43, -154.56) * mm});
            skPoint(sketch, "E526.visualSharp", {"position": v(112.93, -143.06) * mm});
            skArc(sketch, "E526.filletArc", {"start": v(114.43, -143.06) * mm, "mid": v(113.37, -143.5) * mm, "end": v(112.93, -144.56) * mm});
            skPoint(sketch, "E527.visualSharp", {"position": v(125.93, -143.06) * mm});
            skArc(sketch, "E527.filletArc", {"start": v(125.93, -144.56) * mm, "mid": v(125.49, -143.5) * mm, "end": v(124.43, -143.06) * mm});
            skPoint(sketch, "E528.visualSharp", {"position": v(112.93, -156.06) * mm});
            skArc(sketch, "E528.filletArc", {"start": v(112.93, -154.56) * mm, "mid": v(113.37, -155.62) * mm, "end": v(114.43, -156.06) * mm});
            skPoint(sketch, "E529.visualSharp", {"position": v(125.93, -156.06) * mm});
            skArc(sketch, "E529.filletArc", {"start": v(124.43, -156.06) * mm, "mid": v(125.49, -155.62) * mm, "end": v(125.93, -154.56) * mm});
            skPoint(sketch, "E530.visualSharp", {"position": v(129.43, -143.06) * mm});
            skArc(sketch, "E530.filletArc", {"start": v(130.93, -143.06) * mm, "mid": v(129.87, -143.5) * mm, "end": v(129.43, -144.56) * mm});
            skPoint(sketch, "E531.visualSharp", {"position": v(142.43, -143.06) * mm});
            skArc(sketch, "E531.filletArc", {"start": v(142.43, -144.56) * mm, "mid": v(141.99, -143.5) * mm, "end": v(140.93, -143.06) * mm});
            skPoint(sketch, "E532.visualSharp", {"position": v(129.43, -156.06) * mm});
            skArc(sketch, "E532.filletArc", {"start": v(129.43, -154.56) * mm, "mid": v(129.87, -155.62) * mm, "end": v(130.93, -156.06) * mm});
            skPoint(sketch, "E533.visualSharp", {"position": v(142.43, -156.06) * mm});
            skArc(sketch, "E533.filletArc", {"start": v(140.93, -156.06) * mm, "mid": v(141.99, -155.62) * mm, "end": v(142.43, -154.56) * mm});
            skPoint(sketch, "E534.visualSharp", {"position": v(145.93, -143.06) * mm});
            skArc(sketch, "E534.filletArc", {"start": v(147.43, -143.06) * mm, "mid": v(146.37, -143.5) * mm, "end": v(145.93, -144.56) * mm});
            skPoint(sketch, "E535.visualSharp", {"position": v(145.93, -156.06) * mm});
            skArc(sketch, "E535.filletArc", {"start": v(145.93, -154.56) * mm, "mid": v(146.37, -155.62) * mm, "end": v(147.43, -156.06) * mm});
            skPoint(sketch, "E536.visualSharp", {"position": v(158.93, -156.06) * mm});
            skArc(sketch, "E536.filletArc", {"start": v(157.43, -156.06) * mm, "mid": v(158.49, -155.62) * mm, "end": v(158.93, -154.56) * mm});
            skPoint(sketch, "E537.visualSharp", {"position": v(158.93, -143.06) * mm});
            skArc(sketch, "E537.filletArc", {"start": v(158.93, -144.56) * mm, "mid": v(158.49, -143.5) * mm, "end": v(157.43, -143.06) * mm});
            skPoint(sketch, "E538.visualSharp", {"position": v(175.43, -143.06) * mm});
            skArc(sketch, "E538.filletArc", {"start": v(175.43, -144.56) * mm, "mid": v(174.99, -143.5) * mm, "end": v(173.93, -143.06) * mm});
            skPoint(sketch, "E539.visualSharp", {"position": v(175.43, -156.06) * mm});
            skArc(sketch, "E539.filletArc", {"start": v(173.93, -156.06) * mm, "mid": v(174.99, -155.62) * mm, "end": v(175.43, -154.56) * mm});
            skPoint(sketch, "E540.visualSharp", {"position": v(162.43, -156.06) * mm});
            skArc(sketch, "E540.filletArc", {"start": v(162.43, -154.56) * mm, "mid": v(162.87, -155.62) * mm, "end": v(163.93, -156.06) * mm});
            skPoint(sketch, "E541.visualSharp", {"position": v(162.43, -143.06) * mm});
            skArc(sketch, "E541.filletArc", {"start": v(163.93, -143.06) * mm, "mid": v(162.87, -143.5) * mm, "end": v(162.43, -144.56) * mm});
            skPoint(sketch, "E542.visualSharp", {"position": v(92.93, -162.06) * mm});
            skArc(sketch, "E542.filletArc", {"start": v(92.93, -163.56) * mm, "mid": v(92.49, -162.5) * mm, "end": v(91.43, -162.06) * mm});
            skPoint(sketch, "E543.visualSharp", {"position": v(79.93, -175.06) * mm});
            skArc(sketch, "E543.filletArc", {"start": v(79.93, -173.56) * mm, "mid": v(80.37, -174.62) * mm, "end": v(81.43, -175.06) * mm});
            skPoint(sketch, "E544.visualSharp", {"position": v(92.93, -175.06) * mm});
            skArc(sketch, "E544.filletArc", {"start": v(91.43, -175.06) * mm, "mid": v(92.49, -174.62) * mm, "end": v(92.93, -173.56) * mm});
            skPoint(sketch, "E545.visualSharp", {"position": v(109.43, -162.06) * mm});
            skArc(sketch, "E545.filletArc", {"start": v(109.43, -163.56) * mm, "mid": v(108.99, -162.5) * mm, "end": v(107.93, -162.06) * mm});
            skPoint(sketch, "E546.visualSharp", {"position": v(96.43, -175.06) * mm});
            skArc(sketch, "E546.filletArc", {"start": v(96.43, -173.56) * mm, "mid": v(96.87, -174.62) * mm, "end": v(97.93, -175.06) * mm});
            skPoint(sketch, "E547.visualSharp", {"position": v(109.43, -175.06) * mm});
            skArc(sketch, "E547.filletArc", {"start": v(107.93, -175.06) * mm, "mid": v(108.99, -174.62) * mm, "end": v(109.43, -173.56) * mm});
            skPoint(sketch, "E548.visualSharp", {"position": v(125.93, -162.06) * mm});
            skArc(sketch, "E548.filletArc", {"start": v(125.93, -163.56) * mm, "mid": v(125.49, -162.5) * mm, "end": v(124.43, -162.06) * mm});
            skPoint(sketch, "E549.visualSharp", {"position": v(112.93, -175.06) * mm});
            skArc(sketch, "E549.filletArc", {"start": v(112.93, -173.56) * mm, "mid": v(113.37, -174.62) * mm, "end": v(114.43, -175.06) * mm});
            skPoint(sketch, "E550.visualSharp", {"position": v(125.93, -175.06) * mm});
            skArc(sketch, "E550.filletArc", {"start": v(124.43, -175.06) * mm, "mid": v(125.49, -174.62) * mm, "end": v(125.93, -173.56) * mm});
            skPoint(sketch, "E551.visualSharp", {"position": v(142.43, -162.06) * mm});
            skArc(sketch, "E551.filletArc", {"start": v(142.43, -163.56) * mm, "mid": v(141.99, -162.5) * mm, "end": v(140.93, -162.06) * mm});
            skPoint(sketch, "E552.visualSharp", {"position": v(158.93, -162.06) * mm});
            skArc(sketch, "E552.filletArc", {"start": v(158.93, -163.56) * mm, "mid": v(158.49, -162.5) * mm, "end": v(157.43, -162.06) * mm});
            skPoint(sketch, "E553.visualSharp", {"position": v(175.43, -162.06) * mm});
            skArc(sketch, "E553.filletArc", {"start": v(175.43, -163.56) * mm, "mid": v(174.99, -162.5) * mm, "end": v(173.93, -162.06) * mm});
            skPoint(sketch, "E554.visualSharp", {"position": v(129.43, -175.06) * mm});
            skArc(sketch, "E554.filletArc", {"start": v(129.43, -173.56) * mm, "mid": v(129.87, -174.62) * mm, "end": v(130.93, -175.06) * mm});
            skPoint(sketch, "E555.visualSharp", {"position": v(142.43, -175.06) * mm});
            skArc(sketch, "E555.filletArc", {"start": v(140.93, -175.06) * mm, "mid": v(141.99, -174.62) * mm, "end": v(142.43, -173.56) * mm});
            skPoint(sketch, "E556.visualSharp", {"position": v(145.93, -175.06) * mm});
            skArc(sketch, "E556.filletArc", {"start": v(145.93, -173.56) * mm, "mid": v(146.37, -174.62) * mm, "end": v(147.43, -175.06) * mm});
            skPoint(sketch, "E557.visualSharp", {"position": v(158.93, -175.06) * mm});
            skArc(sketch, "E557.filletArc", {"start": v(157.43, -175.06) * mm, "mid": v(158.49, -174.62) * mm, "end": v(158.93, -173.56) * mm});
            skPoint(sketch, "E558.visualSharp", {"position": v(162.43, -175.06) * mm});
            skArc(sketch, "E558.filletArc", {"start": v(162.43, -173.56) * mm, "mid": v(162.87, -174.62) * mm, "end": v(163.93, -175.06) * mm});
            skPoint(sketch, "E559.visualSharp", {"position": v(175.43, -175.06) * mm});
            skArc(sketch, "E559.filletArc", {"start": v(173.93, -175.06) * mm, "mid": v(174.99, -174.62) * mm, "end": v(175.43, -173.56) * mm});
            skPoint(sketch, "E560.visualSharp", {"position": v(79.93, -181.06) * mm});
            skArc(sketch, "E560.filletArc", {"start": v(81.43, -181.06) * mm, "mid": v(80.37, -181.5) * mm, "end": v(79.93, -182.56) * mm});
            skPoint(sketch, "E561.visualSharp", {"position": v(92.93, -181.06) * mm});
            skArc(sketch, "E561.filletArc", {"start": v(92.93, -182.56) * mm, "mid": v(92.49, -181.5) * mm, "end": v(91.43, -181.06) * mm});
            skPoint(sketch, "E562.visualSharp", {"position": v(96.43, -181.06) * mm});
            skArc(sketch, "E562.filletArc", {"start": v(97.93, -181.06) * mm, "mid": v(96.87, -181.5) * mm, "end": v(96.43, -182.56) * mm});
            skPoint(sketch, "E563.visualSharp", {"position": v(109.43, -181.06) * mm});
            skArc(sketch, "E563.filletArc", {"start": v(109.43, -182.56) * mm, "mid": v(108.99, -181.5) * mm, "end": v(107.93, -181.06) * mm});
            skPoint(sketch, "E564.visualSharp", {"position": v(79.93, -194.06) * mm});
            skArc(sketch, "E564.filletArc", {"start": v(79.93, -192.56) * mm, "mid": v(80.37, -193.62) * mm, "end": v(81.43, -194.06) * mm});
            skPoint(sketch, "E565.visualSharp", {"position": v(92.93, -194.06) * mm});
            skArc(sketch, "E565.filletArc", {"start": v(91.43, -194.06) * mm, "mid": v(92.49, -193.62) * mm, "end": v(92.93, -192.56) * mm});
            skPoint(sketch, "E566.visualSharp", {"position": v(96.43, -194.06) * mm});
            skArc(sketch, "E566.filletArc", {"start": v(96.43, -192.56) * mm, "mid": v(96.87, -193.62) * mm, "end": v(97.93, -194.06) * mm});
            skPoint(sketch, "E567.visualSharp", {"position": v(109.43, -194.06) * mm});
            skArc(sketch, "E567.filletArc", {"start": v(107.93, -194.06) * mm, "mid": v(108.99, -193.62) * mm, "end": v(109.43, -192.56) * mm});
            skPoint(sketch, "E568.visualSharp", {"position": v(79.93, -200.06) * mm});
            skArc(sketch, "E568.filletArc", {"start": v(81.43, -200.06) * mm, "mid": v(80.37, -200.5) * mm, "end": v(79.93, -201.56) * mm});
            skPoint(sketch, "E569.visualSharp", {"position": v(92.93, -200.06) * mm});
            skArc(sketch, "E569.filletArc", {"start": v(92.93, -201.56) * mm, "mid": v(92.49, -200.5) * mm, "end": v(91.43, -200.06) * mm});
            skPoint(sketch, "E570.visualSharp", {"position": v(96.43, -200.06) * mm});
            skArc(sketch, "E570.filletArc", {"start": v(97.93, -200.06) * mm, "mid": v(96.87, -200.5) * mm, "end": v(96.43, -201.56) * mm});
            skPoint(sketch, "E571.visualSharp", {"position": v(109.43, -200.06) * mm});
            skArc(sketch, "E571.filletArc", {"start": v(109.43, -201.56) * mm, "mid": v(108.99, -200.5) * mm, "end": v(107.93, -200.06) * mm});
            skPoint(sketch, "E572.visualSharp", {"position": v(79.93, -213.06) * mm});
            skArc(sketch, "E572.filletArc", {"start": v(79.93, -211.56) * mm, "mid": v(80.37, -212.62) * mm, "end": v(81.43, -213.06) * mm});
            skPoint(sketch, "E573.visualSharp", {"position": v(92.93, -213.06) * mm});
            skArc(sketch, "E573.filletArc", {"start": v(91.43, -213.06) * mm, "mid": v(92.49, -212.62) * mm, "end": v(92.93, -211.56) * mm});
            skPoint(sketch, "E574.visualSharp", {"position": v(96.43, -213.06) * mm});
            skArc(sketch, "E574.filletArc", {"start": v(96.43, -211.56) * mm, "mid": v(96.87, -212.62) * mm, "end": v(97.93, -213.06) * mm});
            skPoint(sketch, "E575.visualSharp", {"position": v(109.43, -213.06) * mm});
            skArc(sketch, "E575.filletArc", {"start": v(107.93, -213.06) * mm, "mid": v(108.99, -212.62) * mm, "end": v(109.43, -211.56) * mm});
            skPoint(sketch, "E576.visualSharp", {"position": v(79.93, -219.06) * mm});
            skArc(sketch, "E576.filletArc", {"start": v(81.43, -219.06) * mm, "mid": v(80.37, -219.5) * mm, "end": v(79.93, -220.56) * mm});
            skPoint(sketch, "E577.visualSharp", {"position": v(92.93, -219.06) * mm});
            skArc(sketch, "E577.filletArc", {"start": v(92.93, -220.56) * mm, "mid": v(92.49, -219.5) * mm, "end": v(91.43, -219.06) * mm});
            skPoint(sketch, "E578.visualSharp", {"position": v(79.93, -232.06) * mm});
            skArc(sketch, "E578.filletArc", {"start": v(79.93, -230.56) * mm, "mid": v(80.37, -231.62) * mm, "end": v(81.43, -232.06) * mm});
            skPoint(sketch, "E579.visualSharp", {"position": v(92.93, -232.06) * mm});
            skArc(sketch, "E579.filletArc", {"start": v(91.43, -232.06) * mm, "mid": v(92.49, -231.62) * mm, "end": v(92.93, -230.56) * mm});
            skPoint(sketch, "E580.visualSharp", {"position": v(96.43, -219.06) * mm});
            skArc(sketch, "E580.filletArc", {"start": v(97.93, -219.06) * mm, "mid": v(96.87, -219.5) * mm, "end": v(96.43, -220.56) * mm});
            skPoint(sketch, "E581.visualSharp", {"position": v(109.43, -219.06) * mm});
            skArc(sketch, "E581.filletArc", {"start": v(109.43, -220.56) * mm, "mid": v(108.99, -219.5) * mm, "end": v(107.93, -219.06) * mm});
            skPoint(sketch, "E582.visualSharp", {"position": v(96.43, -232.06) * mm});
            skArc(sketch, "E582.filletArc", {"start": v(96.43, -230.56) * mm, "mid": v(96.87, -231.62) * mm, "end": v(97.93, -232.06) * mm});
            skPoint(sketch, "E583.visualSharp", {"position": v(109.43, -232.06) * mm});
            skArc(sketch, "E583.filletArc", {"start": v(107.93, -232.06) * mm, "mid": v(108.99, -231.62) * mm, "end": v(109.43, -230.56) * mm});
            skPoint(sketch, "E584.visualSharp", {"position": v(112.93, -181.06) * mm});
            skArc(sketch, "E584.filletArc", {"start": v(114.43, -181.06) * mm, "mid": v(113.37, -181.5) * mm, "end": v(112.93, -182.56) * mm});
            skPoint(sketch, "E585.visualSharp", {"position": v(125.93, -181.06) * mm});
            skArc(sketch, "E585.filletArc", {"start": v(125.93, -182.56) * mm, "mid": v(125.49, -181.5) * mm, "end": v(124.43, -181.06) * mm});
            skPoint(sketch, "E586.visualSharp", {"position": v(112.93, -194.06) * mm});
            skArc(sketch, "E586.filletArc", {"start": v(112.93, -192.56) * mm, "mid": v(113.37, -193.62) * mm, "end": v(114.43, -194.06) * mm});
            skPoint(sketch, "E587.visualSharp", {"position": v(125.93, -194.06) * mm});
            skArc(sketch, "E587.filletArc", {"start": v(124.43, -194.06) * mm, "mid": v(125.49, -193.62) * mm, "end": v(125.93, -192.56) * mm});
            skPoint(sketch, "E588.visualSharp", {"position": v(129.43, -181.06) * mm});
            skArc(sketch, "E588.filletArc", {"start": v(130.93, -181.06) * mm, "mid": v(129.87, -181.5) * mm, "end": v(129.43, -182.56) * mm});
            skPoint(sketch, "E589.visualSharp", {"position": v(142.43, -181.06) * mm});
            skArc(sketch, "E589.filletArc", {"start": v(142.43, -182.56) * mm, "mid": v(141.99, -181.5) * mm, "end": v(140.93, -181.06) * mm});
            skPoint(sketch, "E590.visualSharp", {"position": v(129.43, -194.06) * mm});
            skArc(sketch, "E590.filletArc", {"start": v(129.43, -192.56) * mm, "mid": v(129.87, -193.62) * mm, "end": v(130.93, -194.06) * mm});
            skPoint(sketch, "E591.visualSharp", {"position": v(142.43, -194.06) * mm});
            skArc(sketch, "E591.filletArc", {"start": v(140.93, -194.06) * mm, "mid": v(141.99, -193.62) * mm, "end": v(142.43, -192.56) * mm});
            skPoint(sketch, "E592.visualSharp", {"position": v(145.93, -181.06) * mm});
            skArc(sketch, "E592.filletArc", {"start": v(147.43, -181.06) * mm, "mid": v(146.37, -181.5) * mm, "end": v(145.93, -182.56) * mm});
            skPoint(sketch, "E593.visualSharp", {"position": v(158.93, -181.06) * mm});
            skArc(sketch, "E593.filletArc", {"start": v(158.93, -182.56) * mm, "mid": v(158.49, -181.5) * mm, "end": v(157.43, -181.06) * mm});
            skPoint(sketch, "E594.visualSharp", {"position": v(145.93, -194.06) * mm});
            skArc(sketch, "E594.filletArc", {"start": v(145.93, -192.56) * mm, "mid": v(146.37, -193.62) * mm, "end": v(147.43, -194.06) * mm});
            skPoint(sketch, "E595.visualSharp", {"position": v(158.93, -194.06) * mm});
            skArc(sketch, "E595.filletArc", {"start": v(157.43, -194.06) * mm, "mid": v(158.49, -193.62) * mm, "end": v(158.93, -192.56) * mm});
            skPoint(sketch, "E596.visualSharp", {"position": v(162.43, -181.06) * mm});
            skArc(sketch, "E596.filletArc", {"start": v(163.93, -181.06) * mm, "mid": v(162.87, -181.5) * mm, "end": v(162.43, -182.56) * mm});
            skPoint(sketch, "E597.visualSharp", {"position": v(175.43, -181.06) * mm});
            skArc(sketch, "E597.filletArc", {"start": v(175.43, -182.56) * mm, "mid": v(174.99, -181.5) * mm, "end": v(173.93, -181.06) * mm});
            skPoint(sketch, "E598.visualSharp", {"position": v(162.43, -194.06) * mm});
            skArc(sketch, "E598.filletArc", {"start": v(162.43, -192.56) * mm, "mid": v(162.87, -193.62) * mm, "end": v(163.93, -194.06) * mm});
            skPoint(sketch, "E599.visualSharp", {"position": v(175.43, -194.06) * mm});
            skArc(sketch, "E599.filletArc", {"start": v(173.93, -194.06) * mm, "mid": v(174.99, -193.62) * mm, "end": v(175.43, -192.56) * mm});
            skPoint(sketch, "E600.visualSharp", {"position": v(112.93, -200.06) * mm});
            skArc(sketch, "E600.filletArc", {"start": v(114.43, -200.06) * mm, "mid": v(113.37, -200.5) * mm, "end": v(112.93, -201.56) * mm});
            skPoint(sketch, "E601.visualSharp", {"position": v(125.93, -200.06) * mm});
            skArc(sketch, "E601.filletArc", {"start": v(125.93, -201.56) * mm, "mid": v(125.49, -200.5) * mm, "end": v(124.43, -200.06) * mm});
            skPoint(sketch, "E602.visualSharp", {"position": v(112.93, -213.06) * mm});
            skArc(sketch, "E602.filletArc", {"start": v(112.93, -211.56) * mm, "mid": v(113.37, -212.62) * mm, "end": v(114.43, -213.06) * mm});
            skPoint(sketch, "E603.visualSharp", {"position": v(125.93, -213.06) * mm});
            skArc(sketch, "E603.filletArc", {"start": v(124.43, -213.06) * mm, "mid": v(125.49, -212.62) * mm, "end": v(125.93, -211.56) * mm});
            skPoint(sketch, "E604.visualSharp", {"position": v(112.93, -219.06) * mm});
            skArc(sketch, "E604.filletArc", {"start": v(114.43, -219.06) * mm, "mid": v(113.37, -219.5) * mm, "end": v(112.93, -220.56) * mm});
            skPoint(sketch, "E605.visualSharp", {"position": v(125.93, -219.06) * mm});
            skArc(sketch, "E605.filletArc", {"start": v(125.93, -220.56) * mm, "mid": v(125.49, -219.5) * mm, "end": v(124.43, -219.06) * mm});
            skPoint(sketch, "E606.visualSharp", {"position": v(112.93, -232.06) * mm});
            skArc(sketch, "E606.filletArc", {"start": v(112.93, -230.56) * mm, "mid": v(113.37, -231.62) * mm, "end": v(114.43, -232.06) * mm});
            skPoint(sketch, "E607.visualSharp", {"position": v(125.93, -232.06) * mm});
            skArc(sketch, "E607.filletArc", {"start": v(124.43, -232.06) * mm, "mid": v(125.49, -231.62) * mm, "end": v(125.93, -230.56) * mm});
            skPoint(sketch, "E608.visualSharp", {"position": v(129.43, -200.06) * mm});
            skArc(sketch, "E608.filletArc", {"start": v(130.93, -200.06) * mm, "mid": v(129.87, -200.5) * mm, "end": v(129.43, -201.56) * mm});
            skPoint(sketch, "E609.visualSharp", {"position": v(142.43, -200.06) * mm});
            skArc(sketch, "E609.filletArc", {"start": v(142.43, -201.56) * mm, "mid": v(141.99, -200.5) * mm, "end": v(140.93, -200.06) * mm});
            skPoint(sketch, "E610.visualSharp", {"position": v(129.43, -213.06) * mm});
            skArc(sketch, "E610.filletArc", {"start": v(129.43, -211.56) * mm, "mid": v(129.87, -212.62) * mm, "end": v(130.93, -213.06) * mm});
            skPoint(sketch, "E611.visualSharp", {"position": v(142.43, -213.06) * mm});
            skArc(sketch, "E611.filletArc", {"start": v(140.93, -213.06) * mm, "mid": v(141.99, -212.62) * mm, "end": v(142.43, -211.56) * mm});
            skPoint(sketch, "E612.visualSharp", {"position": v(145.93, -200.06) * mm});
            skArc(sketch, "E612.filletArc", {"start": v(147.43, -200.06) * mm, "mid": v(146.37, -200.5) * mm, "end": v(145.93, -201.56) * mm});
            skPoint(sketch, "E613.visualSharp", {"position": v(158.93, -200.06) * mm});
            skArc(sketch, "E613.filletArc", {"start": v(158.93, -201.56) * mm, "mid": v(158.49, -200.5) * mm, "end": v(157.43, -200.06) * mm});
            skPoint(sketch, "E614.visualSharp", {"position": v(145.93, -213.06) * mm});
            skArc(sketch, "E614.filletArc", {"start": v(145.93, -211.56) * mm, "mid": v(146.37, -212.62) * mm, "end": v(147.43, -213.06) * mm});
            skPoint(sketch, "E615.visualSharp", {"position": v(158.93, -213.06) * mm});
            skArc(sketch, "E615.filletArc", {"start": v(157.43, -213.06) * mm, "mid": v(158.49, -212.62) * mm, "end": v(158.93, -211.56) * mm});
            skPoint(sketch, "E616.visualSharp", {"position": v(162.43, -200.06) * mm});
            skArc(sketch, "E616.filletArc", {"start": v(163.93, -200.06) * mm, "mid": v(162.87, -200.5) * mm, "end": v(162.43, -201.56) * mm});
            skPoint(sketch, "E617.visualSharp", {"position": v(175.43, -200.06) * mm});
            skArc(sketch, "E617.filletArc", {"start": v(175.43, -201.56) * mm, "mid": v(174.99, -200.5) * mm, "end": v(173.93, -200.06) * mm});
            skPoint(sketch, "E618.visualSharp", {"position": v(162.43, -213.06) * mm});
            skArc(sketch, "E618.filletArc", {"start": v(162.43, -211.56) * mm, "mid": v(162.87, -212.62) * mm, "end": v(163.93, -213.06) * mm});
            skPoint(sketch, "E619.visualSharp", {"position": v(175.43, -213.06) * mm});
            skArc(sketch, "E619.filletArc", {"start": v(173.93, -213.06) * mm, "mid": v(174.99, -212.62) * mm, "end": v(175.43, -211.56) * mm});
            skPoint(sketch, "E620.visualSharp", {"position": v(129.43, -219.06) * mm});
            skArc(sketch, "E620.filletArc", {"start": v(130.93, -219.06) * mm, "mid": v(129.87, -219.5) * mm, "end": v(129.43, -220.56) * mm});
            skPoint(sketch, "E621.visualSharp", {"position": v(142.43, -219.06) * mm});
            skArc(sketch, "E621.filletArc", {"start": v(142.43, -220.56) * mm, "mid": v(141.99, -219.5) * mm, "end": v(140.93, -219.06) * mm});
            skPoint(sketch, "E622.visualSharp", {"position": v(129.43, -232.06) * mm});
            skArc(sketch, "E622.filletArc", {"start": v(129.43, -230.56) * mm, "mid": v(129.87, -231.62) * mm, "end": v(130.93, -232.06) * mm});
            skPoint(sketch, "E623.visualSharp", {"position": v(142.43, -232.06) * mm});
            skArc(sketch, "E623.filletArc", {"start": v(140.93, -232.06) * mm, "mid": v(141.99, -231.62) * mm, "end": v(142.43, -230.56) * mm});
            skPoint(sketch, "E624.visualSharp", {"position": v(145.93, -219.06) * mm});
            skArc(sketch, "E624.filletArc", {"start": v(147.43, -219.06) * mm, "mid": v(146.37, -219.5) * mm, "end": v(145.93, -220.56) * mm});
            skPoint(sketch, "E625.visualSharp", {"position": v(158.93, -219.06) * mm});
            skArc(sketch, "E625.filletArc", {"start": v(158.93, -220.56) * mm, "mid": v(158.49, -219.5) * mm, "end": v(157.43, -219.06) * mm});
            skPoint(sketch, "E626.visualSharp", {"position": v(145.93, -232.06) * mm});
            skArc(sketch, "E626.filletArc", {"start": v(145.93, -230.56) * mm, "mid": v(146.37, -231.62) * mm, "end": v(147.43, -232.06) * mm});
            skPoint(sketch, "E627.visualSharp", {"position": v(158.93, -232.06) * mm});
            skArc(sketch, "E627.filletArc", {"start": v(157.43, -232.06) * mm, "mid": v(158.49, -231.62) * mm, "end": v(158.93, -230.56) * mm});
            skPoint(sketch, "E628.visualSharp", {"position": v(162.43, -219.06) * mm});
            skArc(sketch, "E628.filletArc", {"start": v(163.93, -219.06) * mm, "mid": v(162.87, -219.5) * mm, "end": v(162.43, -220.56) * mm});
            skPoint(sketch, "E629.visualSharp", {"position": v(175.43, -219.06) * mm});
            skArc(sketch, "E629.filletArc", {"start": v(175.43, -220.56) * mm, "mid": v(174.99, -219.5) * mm, "end": v(173.93, -219.06) * mm});
            skPoint(sketch, "E630.visualSharp", {"position": v(162.43, -232.06) * mm});
            skArc(sketch, "E630.filletArc", {"start": v(162.43, -230.56) * mm, "mid": v(162.87, -231.62) * mm, "end": v(163.93, -232.06) * mm});
            skPoint(sketch, "E631.visualSharp", {"position": v(175.43, -232.06) * mm});
            skArc(sketch, "E631.filletArc", {"start": v(173.93, -232.06) * mm, "mid": v(174.99, -231.62) * mm, "end": v(175.43, -230.56) * mm});
            skSolve(sketch);
        }
        {
            var Q0;
            Q0=qCreatedBy(makeId("Top.planeOp"),FACE);
            var sketch = newSketch(context, id + "F2", { "sketchPlane" : qUnion([Q0])});
            skLineSegment(sketch, "E632.bottom", {"start": v(-181.07, -94.06) * mm, "end": v(188.93, -94.06) * mm});
            skLineSegment(sketch, "E632.top", {"start": v(-181.07, -252.06) * mm, "end": v(188.93, -252.06) * mm});
            skLineSegment(sketch, "E632.left", {"start": v(-181.07, -94.06) * mm, "end": v(-181.07, -252.06) * mm});
            skLineSegment(sketch, "E632.right", {"start": v(188.93, -94.06) * mm, "end": v(188.93, -252.06) * mm});
            skSolve(sketch);
        }
        {
            var Q0;
            Q0 = qSketchRegion(id + "F0", true);
            extrude(context, id + "F3", {"entities" : qUnion([Q0]), "oppositeDirection" : true, "depth" : 3 * mm, "offsetDistance" : 25 * mm});
        }
        {
            var Q0;
            Q0 = qSketchRegion(id + "F2", true);
            extrude(context, id + "F4", {"entities" : qUnion([Q0]), "depth" : 2 * mm, "offsetDistance" : 25 * mm});
        }
        {
            var Q0;
            Q0 = qSketchRegion(id + "F1", true);
            extrude(context, id + "F5", {"entities" : qUnion([Q0]), "operationType" : NewBodyOperationType.REMOVE, "depth" : 25 * mm, "offsetDistance" : 25 * mm, "hasSecondDirection" : true, "secondDirectionOppositeDirection" : true, "secondDirectionDepth" : 25 * mm});
        }
        {
            var Q0;
            Q0=makeQuery(id+"F3.opExtrude","CAP_FACE",FACE,{"disambiguationData":[OSD([sQuery(id+"F0.wireOp",EDGE,"E0.bottom"),sQuery(id+"F0.wireOp",EDGE,"E0.top"),sQuery(id+"F0.wireOp",EDGE,"E0.left"),sQuery(id+"F0.wireOp",EDGE,"E0.right")])],"isStart":true});
            cPlane(context, id + "F6", {"entities" : qUnion([Q0]), "cplaneType" : CPlaneType.OFFSET, "offset" : 50 * mm, "width" : 150 * mm, "height" : 150 * mm});
        }
        {
            var Q0;
            Q0=qCreatedBy(id+"F6.planeOp",FACE);
            var sketch = newSketch(context, id + "F7", { "sketchPlane" : qUnion([Q0])});
            skLineSegment(sketch, "E633.bottom", {"start": v(-100.07, -143.36) * mm, "end": v(-90.07, -143.36) * mm});
            skLineSegment(sketch, "E633.top", {"start": v(-100.07, -155.76) * mm, "end": v(-90.07, -155.76) * mm});
            skLineSegment(sketch, "E633.left", {"start": v(-101.27, -144.56) * mm, "end": v(-101.27, -154.56) * mm});
            skLineSegment(sketch, "E633.right", {"start": v(-88.87, -144.56) * mm, "end": v(-88.87, -154.56) * mm});
            skPoint(sketch, "E634.visualSharp", {"position": v(-101.27, -143.36) * mm});
            skArc(sketch, "E634.filletArc", {"start": v(-100.07, -143.36) * mm, "mid": v(-100.92, -143.71) * mm, "end": v(-101.27, -144.56) * mm});
            skPoint(sketch, "E635.visualSharp", {"position": v(-88.87, -143.36) * mm});
            skArc(sketch, "E635.filletArc", {"start": v(-88.87, -144.56) * mm, "mid": v(-89.22, -143.71) * mm, "end": v(-90.07, -143.36) * mm});
            skPoint(sketch, "E636.visualSharp", {"position": v(-101.27, -155.76) * mm});
            skArc(sketch, "E636.filletArc", {"start": v(-101.27, -154.56) * mm, "mid": v(-100.92, -155.41) * mm, "end": v(-100.07, -155.76) * mm});
            skPoint(sketch, "E637.visualSharp", {"position": v(-88.87, -155.76) * mm});
            skArc(sketch, "E637.filletArc", {"start": v(-90.07, -155.76) * mm, "mid": v(-89.22, -155.41) * mm, "end": v(-88.87, -154.56) * mm});
            skSolve(sketch);
        }
        {
            var Q0;
            Q0 = qSketchRegion(id + "F7", true);
            extrude(context, id + "F8", {"entities" : qUnion([Q0]), "oppositeDirection" : true, "depth" : 10 * mm, "offsetDistance" : 25 * mm});
        }
        {
            var Q0;
            Q0=makeQuery(id+"F8.opExtrude","CAP_FACE",FACE,{"disambiguationData":[OSD([sQuery(id+"F7.wireOp",EDGE,"E633.bottom"),sQuery(id+"F7.wireOp",EDGE,"E633.top"),sQuery(id+"F7.wireOp",EDGE,"E633.left"),sQuery(id+"F7.wireOp",EDGE,"E633.right"),sQuery(id+"F7.wireOp",EDGE,"E634.filletArc"),sQuery(id+"F7.wireOp",EDGE,"E635.filletArc"),sQuery(id+"F7.wireOp",EDGE,"E636.filletArc"),sQuery(id+"F7.wireOp",EDGE,"E637.filletArc")])],"isStart":true});
            var sketch = newSketch(context, id + "F9", { "sketchPlane" : qUnion([Q0])});
            skLineSegment(sketch, "E638.bottom", {"start": v(-99.27, -144.36) * mm, "end": v(-90.87, -144.36) * mm});
            skLineSegment(sketch, "E638.top", {"start": v(-99.27, -154.76) * mm, "end": v(-90.87, -154.76) * mm});
            skLineSegment(sketch, "E638.left", {"start": v(-100.27, -145.36) * mm, "end": v(-100.27, -153.76) * mm});
            skLineSegment(sketch, "E638.right", {"start": v(-89.87, -145.36) * mm, "end": v(-89.87, -153.76) * mm});
            skPoint(sketch, "E639.visualSharp", {"position": v(-100.27, -144.36) * mm});
            skArc(sketch, "E639.filletArc", {"start": v(-99.27, -144.36) * mm, "mid": v(-99.98, -144.66) * mm, "end": v(-100.27, -145.36) * mm});
            skPoint(sketch, "E640.visualSharp", {"position": v(-89.87, -144.36) * mm});
            skArc(sketch, "E640.filletArc", {"start": v(-89.87, -145.36) * mm, "mid": v(-90.16, -144.66) * mm, "end": v(-90.87, -144.36) * mm});
            skPoint(sketch, "E641.visualSharp", {"position": v(-100.27, -154.76) * mm});
            skArc(sketch, "E641.filletArc", {"start": v(-100.27, -153.76) * mm, "mid": v(-99.98, -154.47) * mm, "end": v(-99.27, -154.76) * mm});
            skPoint(sketch, "E642.visualSharp", {"position": v(-89.87, -154.76) * mm});
            skArc(sketch, "E642.filletArc", {"start": v(-90.87, -154.76) * mm, "mid": v(-90.16, -154.47) * mm, "end": v(-89.87, -153.76) * mm});
            skSolve(sketch);
        }
        {
            var Q0;
            Q0 = qSketchRegion(id + "F9", true);
            extrude(context, id + "F10", {"entities" : qUnion([Q0]), "operationType" : NewBodyOperationType.REMOVE, "oppositeDirection" : true, "depth" : 25 * mm, "offsetDistance" : 25 * mm});
        }
        {
            var Q0;
            Q0=makeQuery(id+"F8.opExtrude","CAP_FACE",FACE,{"disambiguationData":[OSD([sQuery(id+"F7.wireOp",EDGE,"E633.bottom"),sQuery(id+"F7.wireOp",EDGE,"E633.top"),sQuery(id+"F7.wireOp",EDGE,"E633.left"),sQuery(id+"F7.wireOp",EDGE,"E633.right"),sQuery(id+"F7.wireOp",EDGE,"E634.filletArc"),sQuery(id+"F7.wireOp",EDGE,"E635.filletArc"),sQuery(id+"F7.wireOp",EDGE,"E636.filletArc"),sQuery(id+"F7.wireOp",EDGE,"E637.filletArc")])],"isStart":true});
            cPlane(context, id + "F11", {"entities" : qUnion([Q0]), "cplaneType" : CPlaneType.OFFSET, "offset" : 1 * mm, "oppositeDirection" : true, "width" : 150 * mm, "height" : 150 * mm});
        }
        {
            var Q0;
            Q0=qCreatedBy(id+"F11.planeOp",FACE);
            var sketch = newSketch(context, id + "F12", { "sketchPlane" : qUnion([Q0])});
            skLineSegment(sketch, "E643.bottom", {"start": v(-99.77, -143.86) * mm, "end": v(-90.37, -143.86) * mm});
            skLineSegment(sketch, "E643.top", {"start": v(-99.77, -155.26) * mm, "end": v(-90.37, -155.26) * mm});
            skLineSegment(sketch, "E643.left", {"start": v(-100.77, -144.86) * mm, "end": v(-100.77, -154.26) * mm});
            skLineSegment(sketch, "E643.right", {"start": v(-89.37, -144.86) * mm, "end": v(-89.37, -154.26) * mm});
            skPoint(sketch, "E644.visualSharp", {"position": v(-100.77, -143.86) * mm});
            skArc(sketch, "E644.filletArc", {"start": v(-99.77, -143.86) * mm, "mid": v(-100.48, -144.16) * mm, "end": v(-100.77, -144.86) * mm});
            skPoint(sketch, "E645.visualSharp", {"position": v(-89.37, -143.86) * mm});
            skArc(sketch, "E645.filletArc", {"start": v(-89.37, -144.86) * mm, "mid": v(-89.66, -144.16) * mm, "end": v(-90.37, -143.86) * mm});
            skPoint(sketch, "E646.visualSharp", {"position": v(-100.77, -155.26) * mm});
            skArc(sketch, "E646.filletArc", {"start": v(-100.77, -154.26) * mm, "mid": v(-100.48, -154.97) * mm, "end": v(-99.77, -155.26) * mm});
            skPoint(sketch, "E647.visualSharp", {"position": v(-89.37, -155.26) * mm});
            skArc(sketch, "E647.filletArc", {"start": v(-90.37, -155.26) * mm, "mid": v(-89.66, -154.97) * mm, "end": v(-89.37, -154.26) * mm});
            skSolve(sketch);
        }
        {
            var Q0;
            Q0 = qSketchRegion(id + "F12", true);
            extrude(context, id + "F13", {"entities" : qUnion([Q0]), "operationType" : NewBodyOperationType.REMOVE, "oppositeDirection" : true, "depth" : 25 * mm, "offsetDistance" : 25 * mm});
        }
        {
            var Q0;
            Q0=makeQuery(id+"F10.boolean.opBoolean","COPY",EDGE,{"derivedFrom":makeQuery(id+"F10.opExtrude","CAP_EDGE",EDGE,{"disambiguationData":[OSD([sQuery(id+"F9.wireOp",EDGE,"E638.bottom")])],"isStart":true})});
            var Q1;
            Q1=makeQuery(id+"F8.opExtrude","CAP_EDGE",EDGE,{"disambiguationData":[OSD([sQuery(id+"F7.wireOp",EDGE,"E634.filletArc")])],"isStart":true});
            fillet(context, id + "F14", {"entities" : qUnion([Q0, Q1]), "radius" : 0.5 * mm, "tangentPropagation" : true, "allowEdgeOverflow" : false});
        }
        {
            var Q0;
            Q0=makeQuery(id+"F13.boolean.opBoolean","COPY",FACE,{"derivedFrom":makeQuery(id+"F13.opExtrude","CAP_FACE",FACE,{"disambiguationData":[OSD([sQuery(id+"F12.wireOp",EDGE,"E643.bottom"),sQuery(id+"F12.wireOp",EDGE,"E643.top"),sQuery(id+"F12.wireOp",EDGE,"E643.left"),sQuery(id+"F12.wireOp",EDGE,"E643.right"),sQuery(id+"F12.wireOp",EDGE,"E644.filletArc"),sQuery(id+"F12.wireOp",EDGE,"E645.filletArc"),sQuery(id+"F12.wireOp",EDGE,"E646.filletArc"),sQuery(id+"F12.wireOp",EDGE,"E647.filletArc")])],"isStart":true})});
            var sketch = newSketch(context, id + "F15", { "sketchPlane" : qUnion([Q0])});
            skLineSegment(sketch, "E648.bottom", {"start": v(-99.62, 155.11) * mm, "end": v(-90.52, 155.11) * mm});
            skLineSegment(sketch, "E648.top", {"start": v(-99.62, 144.01) * mm, "end": v(-90.52, 144.01) * mm});
            skLineSegment(sketch, "E648.left", {"start": v(-100.62, 154.11) * mm, "end": v(-100.62, 145.01) * mm});
            skLineSegment(sketch, "E648.right", {"start": v(-89.52, 154.11) * mm, "end": v(-89.52, 145.01) * mm});
            skPoint(sketch, "E649.visualSharp", {"position": v(-100.62, 155.11) * mm});
            skArc(sketch, "E649.filletArc", {"start": v(-99.62, 155.11) * mm, "mid": v(-100.33, 154.82) * mm, "end": v(-100.62, 154.11) * mm});
            skPoint(sketch, "E650.visualSharp", {"position": v(-89.52, 155.11) * mm});
            skArc(sketch, "E650.filletArc", {"start": v(-89.52, 154.11) * mm, "mid": v(-89.81, 154.82) * mm, "end": v(-90.52, 155.11) * mm});
            skPoint(sketch, "E651.visualSharp", {"position": v(-100.62, 144.01) * mm});
            skArc(sketch, "E651.filletArc", {"start": v(-100.62, 145.01) * mm, "mid": v(-100.33, 144.3) * mm, "end": v(-99.62, 144.01) * mm});
            skPoint(sketch, "E652.visualSharp", {"position": v(-89.52, 144.01) * mm});
            skArc(sketch, "E652.filletArc", {"start": v(-90.52, 144.01) * mm, "mid": v(-89.81, 144.3) * mm, "end": v(-89.52, 145.01) * mm});
            skSolve(sketch);
        }
        {
            var Q0;
            Q0 = qSketchRegion(id + "F15", true);
            extrude(context, id + "F16", {"entities" : qUnion([Q0]), "depth" : 9 * mm, "offsetDistance" : 25 * mm});
        }
        {
            var Q0;
            Q0=makeQuery(id+"F16.opExtrude","CAP_FACE",FACE,{"disambiguationData":[OSD([sQuery(id+"F15.wireOp",EDGE,"E648.bottom"),sQuery(id+"F15.wireOp",EDGE,"E648.top"),sQuery(id+"F15.wireOp",EDGE,"E648.left"),sQuery(id+"F15.wireOp",EDGE,"E648.right"),sQuery(id+"F15.wireOp",EDGE,"E649.filletArc"),sQuery(id+"F15.wireOp",EDGE,"E650.filletArc"),sQuery(id+"F15.wireOp",EDGE,"E651.filletArc"),sQuery(id+"F15.wireOp",EDGE,"E652.filletArc")])],"isStart":false});
            var sketch = newSketch(context, id + "F17", { "sketchPlane" : qUnion([Q0])});
            skLineSegment(sketch, "E653.bottom", {"start": v(-99.12, 154.61) * mm, "end": v(-91.02, 154.61) * mm});
            skLineSegment(sketch, "E653.top", {"start": v(-99.12, 144.51) * mm, "end": v(-91.02, 144.51) * mm});
            skLineSegment(sketch, "E653.left", {"start": v(-100.12, 153.61) * mm, "end": v(-100.12, 145.51) * mm});
            skLineSegment(sketch, "E653.right", {"start": v(-90.02, 153.61) * mm, "end": v(-90.02, 145.51) * mm});
            skPoint(sketch, "E654.visualSharp", {"position": v(-100.12, 154.61) * mm});
            skArc(sketch, "E654.filletArc", {"start": v(-99.12, 154.61) * mm, "mid": v(-99.83, 154.32) * mm, "end": v(-100.12, 153.61) * mm});
            skPoint(sketch, "E655.visualSharp", {"position": v(-90.02, 154.61) * mm});
            skArc(sketch, "E655.filletArc", {"start": v(-90.02, 153.61) * mm, "mid": v(-90.31, 154.32) * mm, "end": v(-91.02, 154.61) * mm});
            skPoint(sketch, "E656.visualSharp", {"position": v(-100.12, 144.51) * mm});
            skArc(sketch, "E656.filletArc", {"start": v(-100.12, 145.51) * mm, "mid": v(-99.83, 144.8) * mm, "end": v(-99.12, 144.51) * mm});
            skPoint(sketch, "E657.visualSharp", {"position": v(-90.02, 144.51) * mm});
            skArc(sketch, "E657.filletArc", {"start": v(-91.02, 144.51) * mm, "mid": v(-90.31, 144.8) * mm, "end": v(-90.02, 145.51) * mm});
            skSolve(sketch);
        }
        {
            var Q0;
            Q0 = qSketchRegion(id + "F17", true);
            extrude(context, id + "F18", {"entities" : qUnion([Q0]), "operationType" : NewBodyOperationType.REMOVE, "oppositeDirection" : true, "depth" : 7 * mm, "offsetDistance" : 25 * mm});
        }
        {
            var Q0;
            Q0=makeQuery(id+"F16.opExtrude","CAP_FACE",FACE,{"disambiguationData":[OSD([sQuery(id+"F15.wireOp",EDGE,"E648.bottom"),sQuery(id+"F15.wireOp",EDGE,"E648.top"),sQuery(id+"F15.wireOp",EDGE,"E648.left"),sQuery(id+"F15.wireOp",EDGE,"E648.right"),sQuery(id+"F15.wireOp",EDGE,"E649.filletArc"),sQuery(id+"F15.wireOp",EDGE,"E650.filletArc"),sQuery(id+"F15.wireOp",EDGE,"E651.filletArc"),sQuery(id+"F15.wireOp",EDGE,"E652.filletArc")])],"isStart":false});
            var sketch = newSketch(context, id + "F19", { "sketchPlane" : qUnion([Q0])});
            skLineSegment(sketch, "E658.bottom", {"start": v(-99.12, 154.41) * mm, "end": v(-91.02, 154.41) * mm});
            skLineSegment(sketch, "E658.top", {"start": v(-99.12, 144.71) * mm, "end": v(-91.02, 144.71) * mm});
            skLineSegment(sketch, "E658.left", {"start": v(-99.92, 153.61) * mm, "end": v(-99.92, 145.51) * mm});
            skLineSegment(sketch, "E658.right", {"start": v(-90.22, 153.61) * mm, "end": v(-90.22, 145.51) * mm});
            skPoint(sketch, "E659.visualSharp", {"position": v(-99.92, 154.41) * mm});
            skArc(sketch, "E659.filletArc", {"start": v(-99.12, 154.41) * mm, "mid": v(-99.69, 154.18) * mm, "end": v(-99.92, 153.61) * mm});
            skPoint(sketch, "E660.visualSharp", {"position": v(-90.22, 154.41) * mm});
            skArc(sketch, "E660.filletArc", {"start": v(-90.22, 153.61) * mm, "mid": v(-90.46, 154.18) * mm, "end": v(-91.02, 154.41) * mm});
            skPoint(sketch, "E661.visualSharp", {"position": v(-99.92, 144.71) * mm});
            skArc(sketch, "E661.filletArc", {"start": v(-99.92, 145.51) * mm, "mid": v(-99.69, 144.95) * mm, "end": v(-99.12, 144.71) * mm});
            skPoint(sketch, "E662.visualSharp", {"position": v(-90.22, 144.71) * mm});
            skArc(sketch, "E662.filletArc", {"start": v(-91.02, 144.71) * mm, "mid": v(-90.46, 144.95) * mm, "end": v(-90.22, 145.51) * mm});
            skSolve(sketch);
        }
        {
            var Q0;
            Q0 = qSketchRegion(id + "F19", true);
            extrude(context, id + "F20", {"entities" : qUnion([Q0]), "oppositeDirection" : true, "depth" : 6 * mm, "offsetDistance" : 25 * mm});
        }
        {
            var Q0;
            Q0=makeQuery(id+"F20.opExtrude","CAP_FACE",FACE,{"disambiguationData":[OSD([sQuery(id+"F19.wireOp",EDGE,"E658.bottom"),sQuery(id+"F19.wireOp",EDGE,"E658.top"),sQuery(id+"F19.wireOp",EDGE,"E658.left"),sQuery(id+"F19.wireOp",EDGE,"E658.right"),sQuery(id+"F19.wireOp",EDGE,"E659.filletArc"),sQuery(id+"F19.wireOp",EDGE,"E660.filletArc"),sQuery(id+"F19.wireOp",EDGE,"E661.filletArc"),sQuery(id+"F19.wireOp",EDGE,"E662.filletArc")])],"isStart":true});
            var sketch = newSketch(context, id + "F21", { "sketchPlane" : qUnion([Q0])});
            skLineSegment(sketch, "E663.bottom", {"start": v(-100.77, 156.76) * mm, "end": v(-89.37, 156.76) * mm});
            skLineSegment(sketch, "E663.top", {"start": v(-100.77, 142.36) * mm, "end": v(-89.37, 142.36) * mm});
            skLineSegment(sketch, "E663.left", {"start": v(-102.27, 155.26) * mm, "end": v(-102.27, 143.86) * mm});
            skLineSegment(sketch, "E663.right", {"start": v(-87.87, 155.26) * mm, "end": v(-87.87, 143.86) * mm});
            skPoint(sketch, "E664.visualSharp", {"position": v(-102.27, 156.76) * mm});
            skArc(sketch, "E664.filletArc", {"start": v(-100.77, 156.76) * mm, "mid": v(-101.83, 156.32) * mm, "end": v(-102.27, 155.26) * mm});
            skPoint(sketch, "E665.visualSharp", {"position": v(-87.87, 156.76) * mm});
            skArc(sketch, "E665.filletArc", {"start": v(-87.87, 155.26) * mm, "mid": v(-88.31, 156.32) * mm, "end": v(-89.37, 156.76) * mm});
            skPoint(sketch, "E666.visualSharp", {"position": v(-102.27, 142.36) * mm});
            skArc(sketch, "E666.filletArc", {"start": v(-102.27, 143.86) * mm, "mid": v(-101.83, 142.8) * mm, "end": v(-100.77, 142.36) * mm});
            skPoint(sketch, "E667.visualSharp", {"position": v(-87.87, 142.36) * mm});
            skArc(sketch, "E667.filletArc", {"start": v(-89.37, 142.36) * mm, "mid": v(-88.31, 142.8) * mm, "end": v(-87.87, 143.86) * mm});
            skSolve(sketch);
        }
        {
            var Q0;
            Q0 = qSketchRegion(id + "F21", true);
            extrude(context, id + "F22", {"entities" : qUnion([Q0]), "operationType" : NewBodyOperationType.ADD, "depth" : 25 * mm, "offsetDistance" : 25 * mm});
        }
        {
            var Q0;
            Q0=makeQuery(id+"F20.opExtrude","CAP_FACE",FACE,{"disambiguationData":[OSD([sQuery(id+"F19.wireOp",EDGE,"E658.bottom"),sQuery(id+"F19.wireOp",EDGE,"E658.top"),sQuery(id+"F19.wireOp",EDGE,"E658.left"),sQuery(id+"F19.wireOp",EDGE,"E658.right"),sQuery(id+"F19.wireOp",EDGE,"E659.filletArc"),sQuery(id+"F19.wireOp",EDGE,"E660.filletArc"),sQuery(id+"F19.wireOp",EDGE,"E661.filletArc"),sQuery(id+"F19.wireOp",EDGE,"E662.filletArc")])],"isStart":false});
            var sketch = newSketch(context, id + "F23", { "sketchPlane" : qUnion([Q0])});
            skCircle(sketch, "E668", {"center": v(-95.07, -149.56) * mm, "radius": 3.1 * mm});
            skSolve(sketch);
        }
        {
            var Q0;
            Q0 = qSketchRegion(id + "F23", true);
            extrude(context, id + "F24", {"entities" : qUnion([Q0]), "operationType" : NewBodyOperationType.REMOVE, "oppositeDirection" : true, "depth" : 35 * mm, "offsetDistance" : 25 * mm});
        }
        {
            var Q0;
            Q0=makeQuery(id+"F20.opExtrude","CAP_FACE",FACE,{"disambiguationData":[OSD([sQuery(id+"F19.wireOp",EDGE,"E658.bottom"),sQuery(id+"F19.wireOp",EDGE,"E658.top"),sQuery(id+"F19.wireOp",EDGE,"E658.left"),sQuery(id+"F19.wireOp",EDGE,"E658.right"),sQuery(id+"F19.wireOp",EDGE,"E659.filletArc"),sQuery(id+"F19.wireOp",EDGE,"E660.filletArc"),sQuery(id+"F19.wireOp",EDGE,"E661.filletArc"),sQuery(id+"F19.wireOp",EDGE,"E662.filletArc")])],"isStart":false});
            var sketch = newSketch(context, id + "F25", { "sketchPlane" : qUnion([Q0])});
            skCircle(sketch, "E669", {"center": v(-95.07, -149.56) * mm, "radius": 3.75 * mm});
            skSolve(sketch);
        }
        {
            var Q0;
            Q0 = qSketchRegion(id + "F25", true);
            extrude(context, id + "F26", {"entities" : qUnion([Q0]), "operationType" : NewBodyOperationType.REMOVE, "oppositeDirection" : true, "depth" : 1.5 * mm, "offsetDistance" : 25 * mm});
        }
        {
            var Q0;
            Q0=makeQuery(id+"F26.boolean.opBoolean","COPY",FACE,{"derivedFrom":makeQuery(id+"F26.opExtrude","CAP_FACE",FACE,{"disambiguationData":[OSD([sQuery(id+"F25.wireOp",EDGE,"E669")])],"isStart":false})});
            cPlane(context, id + "F27", {"entities" : qUnion([Q0]), "cplaneType" : CPlaneType.OFFSET, "offset" : 25 * mm, "oppositeDirection" : true, "width" : 150 * mm, "height" : 150 * mm});
        }
        {
            var Q0;
            Q0=qCreatedBy(id+"F27.planeOp",FACE);
            var sketch = newSketch(context, id + "F28", { "sketchPlane" : qUnion([Q0])});
            skLineSegment(sketch, "E670.bottom", {"start": v(-104.83, -140.45) * mm, "end": v(-86.05, -140.45) * mm});
            skLineSegment(sketch, "E670.top", {"start": v(-104.83, -159.17) * mm, "end": v(-86.05, -159.17) * mm});
            skLineSegment(sketch, "E670.left", {"start": v(-104.83, -140.45) * mm, "end": v(-104.83, -159.17) * mm});
            skLineSegment(sketch, "E670.right", {"start": v(-86.05, -140.45) * mm, "end": v(-86.05, -159.17) * mm});
            skSolve(sketch);
        }
        {
            var Q0;
            Q0 = qSketchRegion(id + "F28", true);
            extrude(context, id + "F29", {"entities" : qUnion([Q0]), "operationType" : NewBodyOperationType.REMOVE, "oppositeDirection" : true, "depth" : 25 * mm, "offsetDistance" : 25 * mm});
        }
        {
            var Q0;
            Q0=makeQuery(id+"F29.boolean.opBoolean","COPY",FACE,{"derivedFrom":makeQuery(id+"F29.opExtrude","CAP_FACE",FACE,{"disambiguationData":[OSD([sQuery(id+"F28.wireOp",EDGE,"E670.bottom"),sQuery(id+"F28.wireOp",EDGE,"E670.top"),sQuery(id+"F28.wireOp",EDGE,"E670.left"),sQuery(id+"F28.wireOp",EDGE,"E670.right")])],"isStart":true})});
            var sketch = newSketch(context, id + "F30", { "sketchPlane" : qUnion([Q0])});
            skLineSegment(sketch, "E671.bottom", {"start": v(-98.27, 154.76) * mm, "end": v(-91.87, 154.76) * mm});
            skLineSegment(sketch, "E671.top", {"start": v(-98.27, 144.36) * mm, "end": v(-91.87, 144.36) * mm});
            skLineSegment(sketch, "E671.left", {"start": v(-100.27, 152.76) * mm, "end": v(-100.27, 146.36) * mm});
            skLineSegment(sketch, "E671.right", {"start": v(-89.87, 152.76) * mm, "end": v(-89.87, 146.36) * mm});
            skPoint(sketch, "E672.visualSharp", {"position": v(-100.27, 154.76) * mm});
            skArc(sketch, "E672.filletArc", {"start": v(-98.27, 154.76) * mm, "mid": v(-99.69, 154.18) * mm, "end": v(-100.27, 152.76) * mm});
            skPoint(sketch, "E673.visualSharp", {"position": v(-89.87, 154.76) * mm});
            skArc(sketch, "E673.filletArc", {"start": v(-89.87, 152.76) * mm, "mid": v(-90.46, 154.18) * mm, "end": v(-91.87, 154.76) * mm});
            skPoint(sketch, "E674.visualSharp", {"position": v(-100.27, 144.36) * mm});
            skArc(sketch, "E674.filletArc", {"start": v(-100.27, 146.36) * mm, "mid": v(-99.69, 144.95) * mm, "end": v(-98.27, 144.36) * mm});
            skPoint(sketch, "E675.visualSharp", {"position": v(-89.87, 144.36) * mm});
            skArc(sketch, "E675.filletArc", {"start": v(-91.87, 144.36) * mm, "mid": v(-90.46, 144.95) * mm, "end": v(-89.87, 146.36) * mm});
            skSolve(sketch);
        }
        {
            var Q0;
            Q0 = qSketchRegion(id + "F30", true);
            extrude(context, id + "F31", {"entities" : qUnion([Q0]), "operationType" : NewBodyOperationType.REMOVE, "oppositeDirection" : true, "depth" : 3 * mm, "offsetDistance" : 25 * mm});
        }
        {
            var Q0;
            Q0=makeQuery(id+"F31.boolean.opBoolean","COPY",FACE,{"derivedFrom":makeQuery(id+"F31.opExtrude","CAP_FACE",FACE,{"disambiguationData":[OSD([sQuery(id+"F30.wireOp",EDGE,"E671.bottom"),sQuery(id+"F30.wireOp",EDGE,"E671.top"),sQuery(id+"F30.wireOp",EDGE,"E671.left"),sQuery(id+"F30.wireOp",EDGE,"E671.right"),sQuery(id+"F30.wireOp",EDGE,"E672.filletArc"),sQuery(id+"F30.wireOp",EDGE,"E673.filletArc"),sQuery(id+"F30.wireOp",EDGE,"E674.filletArc"),sQuery(id+"F30.wireOp",EDGE,"E675.filletArc")])],"isStart":false})});
            var sketch = newSketch(context, id + "F32", { "sketchPlane" : qUnion([Q0])});
            skLineSegment(sketch, "E676.bottom", {"start": v(-98.37, 154.56) * mm, "end": v(-91.77, 154.56) * mm});
            skLineSegment(sketch, "E676.top", {"start": v(-98.37, 144.56) * mm, "end": v(-91.77, 144.56) * mm});
            skLineSegment(sketch, "E676.left", {"start": v(-100.07, 152.86) * mm, "end": v(-100.07, 146.26) * mm});
            skLineSegment(sketch, "E676.right", {"start": v(-90.07, 152.86) * mm, "end": v(-90.07, 146.26) * mm});
            skPoint(sketch, "E677.visualSharp", {"position": v(-100.07, 154.56) * mm});
            skArc(sketch, "E677.filletArc", {"start": v(-98.37, 154.56) * mm, "mid": v(-99.57, 154.06) * mm, "end": v(-100.07, 152.86) * mm});
            skPoint(sketch, "E678.visualSharp", {"position": v(-90.07, 154.56) * mm});
            skArc(sketch, "E678.filletArc", {"start": v(-90.07, 152.86) * mm, "mid": v(-90.57, 154.06) * mm, "end": v(-91.77, 154.56) * mm});
            skPoint(sketch, "E679.visualSharp", {"position": v(-100.07, 144.56) * mm});
            skArc(sketch, "E679.filletArc", {"start": v(-100.07, 146.26) * mm, "mid": v(-99.57, 145.06) * mm, "end": v(-98.37, 144.56) * mm});
            skPoint(sketch, "E680.visualSharp", {"position": v(-90.07, 144.56) * mm});
            skArc(sketch, "E680.filletArc", {"start": v(-91.77, 144.56) * mm, "mid": v(-90.57, 145.06) * mm, "end": v(-90.07, 146.26) * mm});
            skSolve(sketch);
        }
        {
            var Q0;
            Q0 = qSketchRegion(id + "F32", true);
            extrude(context, id + "F33", {"entities" : qUnion([Q0]), "depth" : 3 * mm, "offsetDistance" : 25 * mm});
        }
        {
            var Q0;
            Q0=makeQuery(id+"F33.opExtrude","CAP_FACE",FACE,{"disambiguationData":[OSD([sQuery(id+"F32.wireOp",EDGE,"E676.bottom"),sQuery(id+"F32.wireOp",EDGE,"E676.top"),sQuery(id+"F32.wireOp",EDGE,"E676.left"),sQuery(id+"F32.wireOp",EDGE,"E676.right"),sQuery(id+"F32.wireOp",EDGE,"E677.filletArc"),sQuery(id+"F32.wireOp",EDGE,"E678.filletArc"),sQuery(id+"F32.wireOp",EDGE,"E679.filletArc"),sQuery(id+"F32.wireOp",EDGE,"E680.filletArc")])],"isStart":false});
            var sketch = newSketch(context, id + "F34", { "sketchPlane" : qUnion([Q0])});
            skLineSegment(sketch, "E681.bottom", {"start": v(-100.77, 156.76) * mm, "end": v(-89.37, 156.76) * mm});
            skLineSegment(sketch, "E681.top", {"start": v(-100.77, 142.36) * mm, "end": v(-89.37, 142.36) * mm});
            skLineSegment(sketch, "E681.left", {"start": v(-102.27, 155.26) * mm, "end": v(-102.27, 143.86) * mm});
            skLineSegment(sketch, "E681.right", {"start": v(-87.87, 155.26) * mm, "end": v(-87.87, 143.86) * mm});
            skPoint(sketch, "E682.visualSharp", {"position": v(-102.27, 156.76) * mm});
            skArc(sketch, "E682.filletArc", {"start": v(-100.77, 156.76) * mm, "mid": v(-101.83, 156.32) * mm, "end": v(-102.27, 155.26) * mm});
            skPoint(sketch, "E683.visualSharp", {"position": v(-87.87, 156.76) * mm});
            skArc(sketch, "E683.filletArc", {"start": v(-87.87, 155.26) * mm, "mid": v(-88.31, 156.32) * mm, "end": v(-89.37, 156.76) * mm});
            skPoint(sketch, "E684.visualSharp", {"position": v(-102.27, 142.36) * mm});
            skArc(sketch, "E684.filletArc", {"start": v(-102.27, 143.86) * mm, "mid": v(-101.83, 142.8) * mm, "end": v(-100.77, 142.36) * mm});
            skPoint(sketch, "E685.visualSharp", {"position": v(-87.87, 142.36) * mm});
            skArc(sketch, "E685.filletArc", {"start": v(-89.37, 142.36) * mm, "mid": v(-88.31, 142.8) * mm, "end": v(-87.87, 143.86) * mm});
            skSolve(sketch);
        }
        {
            var Q0;
            Q0=makeQuery(id+"F3.opExtrude","CAP_FACE",FACE,{"disambiguationData":[OSD([sQuery(id+"F0.wireOp",EDGE,"E0.bottom"),sQuery(id+"F0.wireOp",EDGE,"E0.top"),sQuery(id+"F0.wireOp",EDGE,"E0.left"),sQuery(id+"F0.wireOp",EDGE,"E0.right")])],"isStart":false});
            var sketch = newSketch(context, id + "F35", { "sketchPlane" : qUnion([Q0])});
            skLineSegment(sketch, "E686.bottom", {"start": v(-181.07, 94.06) * mm, "end": v(188.93, 94.06) * mm});
            skLineSegment(sketch, "E686.top", {"start": v(-181.07, 252.06) * mm, "end": v(188.93, 252.06) * mm});
            skLineSegment(sketch, "E686.left", {"start": v(-181.07, 94.06) * mm, "end": v(-181.07, 252.06) * mm});
            skLineSegment(sketch, "E686.right", {"start": v(188.93, 94.06) * mm, "end": v(188.93, 252.06) * mm});
            skSolve(sketch);
        }
        {
            var Q0;
            Q0 = qSketchRegion(id + "F35", true);
            extrude(context, id + "F36", {"entities" : qUnion([Q0]), "depth" : 40 * mm, "offsetDistance" : 25 * mm});
        }
        {
            var Q0;
            Q0=makeQuery(id+"F36.opExtrude","CAP_FACE",FACE,{"disambiguationData":[OSD([sQuery(id+"F35.wireOp",EDGE,"E686.bottom"),sQuery(id+"F35.wireOp",EDGE,"E686.top"),sQuery(id+"F35.wireOp",EDGE,"E686.left"),sQuery(id+"F35.wireOp",EDGE,"E686.right")])],"isStart":true});
            var sketch = newSketch(context, id + "F37", { "sketchPlane" : qUnion([Q0])});
            skLineSegment(sketch, "E687.bottom", {"start": v(-101.27, -141.86) * mm, "end": v(-88.87, -141.86) * mm});
            skLineSegment(sketch, "E687.top", {"start": v(-101.27, -157.26) * mm, "end": v(-88.87, -157.26) * mm});
            skLineSegment(sketch, "E687.left", {"start": v(-102.77, -143.36) * mm, "end": v(-102.77, -155.76) * mm});
            skLineSegment(sketch, "E687.right", {"start": v(-87.37, -143.36) * mm, "end": v(-87.37, -155.76) * mm});
            skPoint(sketch, "E688.visualSharp", {"position": v(-102.77, -141.86) * mm});
            skArc(sketch, "E688.filletArc", {"start": v(-101.27, -141.86) * mm, "mid": v(-102.33, -142.3) * mm, "end": v(-102.77, -143.36) * mm});
            skPoint(sketch, "E689.visualSharp", {"position": v(-87.37, -141.86) * mm});
            skArc(sketch, "E689.filletArc", {"start": v(-87.37, -143.36) * mm, "mid": v(-87.81, -142.3) * mm, "end": v(-88.87, -141.86) * mm});
            skPoint(sketch, "E690.visualSharp", {"position": v(-102.77, -157.26) * mm});
            skArc(sketch, "E690.filletArc", {"start": v(-102.77, -155.76) * mm, "mid": v(-102.33, -156.82) * mm, "end": v(-101.27, -157.26) * mm});
            skPoint(sketch, "E691.visualSharp", {"position": v(-87.37, -157.26) * mm});
            skArc(sketch, "E691.filletArc", {"start": v(-88.87, -157.26) * mm, "mid": v(-87.81, -156.82) * mm, "end": v(-87.37, -155.76) * mm});
            skLineSegment(sketch, "E692.bottom", {"start": v(-101.27, -122.86) * mm, "end": v(-88.87, -122.86) * mm});
            skLineSegment(sketch, "E692.top", {"start": v(-101.27, -138.26) * mm, "end": v(-88.87, -138.26) * mm});
            skLineSegment(sketch, "E692.left", {"start": v(-102.77, -124.36) * mm, "end": v(-102.77, -136.76) * mm});
            skLineSegment(sketch, "E692.right", {"start": v(-87.37, -124.36) * mm, "end": v(-87.37, -136.76) * mm});
            skPoint(sketch, "E693.visualSharp", {"position": v(-102.77, -122.86) * mm});
            skArc(sketch, "E693.filletArc", {"start": v(-101.27, -122.86) * mm, "mid": v(-102.33, -123.3) * mm, "end": v(-102.77, -124.36) * mm});
            skPoint(sketch, "E694.visualSharp", {"position": v(-87.37, -122.86) * mm});
            skArc(sketch, "E694.filletArc", {"start": v(-87.37, -124.36) * mm, "mid": v(-87.81, -123.3) * mm, "end": v(-88.87, -122.86) * mm});
            skPoint(sketch, "E695.visualSharp", {"position": v(-102.77, -138.26) * mm});
            skArc(sketch, "E695.filletArc", {"start": v(-102.77, -136.76) * mm, "mid": v(-102.33, -137.82) * mm, "end": v(-101.27, -138.26) * mm});
            skPoint(sketch, "E696.visualSharp", {"position": v(-87.37, -138.26) * mm});
            skArc(sketch, "E696.filletArc", {"start": v(-88.87, -138.26) * mm, "mid": v(-87.81, -137.82) * mm, "end": v(-87.37, -136.76) * mm});
            skLineSegment(sketch, "E697.bottom", {"start": v(-101.27, -179.86) * mm, "end": v(-88.87, -179.86) * mm});
            skLineSegment(sketch, "E697.top", {"start": v(-101.27, -195.26) * mm, "end": v(-88.87, -195.26) * mm});
            skLineSegment(sketch, "E697.left", {"start": v(-102.77, -181.36) * mm, "end": v(-102.77, -193.76) * mm});
            skLineSegment(sketch, "E697.right", {"start": v(-87.37, -181.36) * mm, "end": v(-87.37, -193.76) * mm});
            skPoint(sketch, "E698.visualSharp", {"position": v(-102.77, -179.86) * mm});
            skArc(sketch, "E698.filletArc", {"start": v(-101.27, -179.86) * mm, "mid": v(-102.33, -180.3) * mm, "end": v(-102.77, -181.36) * mm});
            skPoint(sketch, "E699.visualSharp", {"position": v(-87.37, -179.86) * mm});
            skArc(sketch, "E699.filletArc", {"start": v(-87.37, -181.36) * mm, "mid": v(-87.81, -180.3) * mm, "end": v(-88.87, -179.86) * mm});
            skPoint(sketch, "E700.visualSharp", {"position": v(-102.77, -195.26) * mm});
            skArc(sketch, "E700.filletArc", {"start": v(-102.77, -193.76) * mm, "mid": v(-102.33, -194.82) * mm, "end": v(-101.27, -195.26) * mm});
            skPoint(sketch, "E701.visualSharp", {"position": v(-87.37, -195.26) * mm});
            skArc(sketch, "E701.filletArc", {"start": v(-88.87, -195.26) * mm, "mid": v(-87.81, -194.82) * mm, "end": v(-87.37, -193.76) * mm});
            skLineSegment(sketch, "E702.bottom", {"start": v(-101.27, -160.86) * mm, "end": v(-88.87, -160.86) * mm});
            skLineSegment(sketch, "E702.top", {"start": v(-101.27, -176.26) * mm, "end": v(-88.87, -176.26) * mm});
            skLineSegment(sketch, "E702.left", {"start": v(-102.77, -162.36) * mm, "end": v(-102.77, -174.76) * mm});
            skLineSegment(sketch, "E702.right", {"start": v(-87.37, -162.36) * mm, "end": v(-87.37, -174.76) * mm});
            skPoint(sketch, "E703.visualSharp", {"position": v(-102.77, -160.86) * mm});
            skArc(sketch, "E703.filletArc", {"start": v(-101.27, -160.86) * mm, "mid": v(-102.33, -161.3) * mm, "end": v(-102.77, -162.36) * mm});
            skPoint(sketch, "E704.visualSharp", {"position": v(-87.37, -160.86) * mm});
            skArc(sketch, "E704.filletArc", {"start": v(-87.37, -162.36) * mm, "mid": v(-87.81, -161.3) * mm, "end": v(-88.87, -160.86) * mm});
            skPoint(sketch, "E705.visualSharp", {"position": v(-102.77, -176.26) * mm});
            skArc(sketch, "E705.filletArc", {"start": v(-102.77, -174.76) * mm, "mid": v(-102.33, -175.82) * mm, "end": v(-101.27, -176.26) * mm});
            skPoint(sketch, "E706.visualSharp", {"position": v(-87.37, -176.26) * mm});
            skArc(sketch, "E706.filletArc", {"start": v(-88.87, -176.26) * mm, "mid": v(-87.81, -175.82) * mm, "end": v(-87.37, -174.76) * mm});
            skLineSegment(sketch, "E707.bottom", {"start": v(-101.27, -217.86) * mm, "end": v(-88.87, -217.86) * mm});
            skLineSegment(sketch, "E707.top", {"start": v(-101.27, -233.26) * mm, "end": v(-88.87, -233.26) * mm});
            skLineSegment(sketch, "E707.left", {"start": v(-102.77, -219.36) * mm, "end": v(-102.77, -231.76) * mm});
            skLineSegment(sketch, "E707.right", {"start": v(-87.37, -219.36) * mm, "end": v(-87.37, -231.76) * mm});
            skPoint(sketch, "E708.visualSharp", {"position": v(-102.77, -217.86) * mm});
            skArc(sketch, "E708.filletArc", {"start": v(-101.27, -217.86) * mm, "mid": v(-102.33, -218.3) * mm, "end": v(-102.77, -219.36) * mm});
            skPoint(sketch, "E709.visualSharp", {"position": v(-87.37, -217.86) * mm});
            skArc(sketch, "E709.filletArc", {"start": v(-87.37, -219.36) * mm, "mid": v(-87.81, -218.3) * mm, "end": v(-88.87, -217.86) * mm});
            skPoint(sketch, "E710.visualSharp", {"position": v(-102.77, -233.26) * mm});
            skArc(sketch, "E710.filletArc", {"start": v(-102.77, -231.76) * mm, "mid": v(-102.33, -232.82) * mm, "end": v(-101.27, -233.26) * mm});
            skPoint(sketch, "E711.visualSharp", {"position": v(-87.37, -233.26) * mm});
            skArc(sketch, "E711.filletArc", {"start": v(-88.87, -233.26) * mm, "mid": v(-87.81, -232.82) * mm, "end": v(-87.37, -231.76) * mm});
            skLineSegment(sketch, "E712.bottom", {"start": v(-101.27, -198.86) * mm, "end": v(-88.87, -198.86) * mm});
            skLineSegment(sketch, "E712.top", {"start": v(-101.27, -214.26) * mm, "end": v(-88.87, -214.26) * mm});
            skLineSegment(sketch, "E712.left", {"start": v(-102.77, -200.36) * mm, "end": v(-102.77, -212.76) * mm});
            skLineSegment(sketch, "E712.right", {"start": v(-87.37, -200.36) * mm, "end": v(-87.37, -212.76) * mm});
            skPoint(sketch, "E713.visualSharp", {"position": v(-102.77, -198.86) * mm});
            skArc(sketch, "E713.filletArc", {"start": v(-101.27, -198.86) * mm, "mid": v(-102.33, -199.3) * mm, "end": v(-102.77, -200.36) * mm});
            skPoint(sketch, "E714.visualSharp", {"position": v(-87.37, -198.86) * mm});
            skArc(sketch, "E714.filletArc", {"start": v(-87.37, -200.36) * mm, "mid": v(-87.81, -199.3) * mm, "end": v(-88.87, -198.86) * mm});
            skPoint(sketch, "E715.visualSharp", {"position": v(-102.77, -214.26) * mm});
            skArc(sketch, "E715.filletArc", {"start": v(-102.77, -212.76) * mm, "mid": v(-102.33, -213.82) * mm, "end": v(-101.27, -214.26) * mm});
            skPoint(sketch, "E716.visualSharp", {"position": v(-87.37, -214.26) * mm});
            skArc(sketch, "E716.filletArc", {"start": v(-88.87, -214.26) * mm, "mid": v(-87.81, -213.82) * mm, "end": v(-87.37, -212.76) * mm});
            skLineSegment(sketch, "E717.bottom", {"start": v(-117.77, -141.86) * mm, "end": v(-105.37, -141.86) * mm});
            skLineSegment(sketch, "E717.top", {"start": v(-117.77, -157.26) * mm, "end": v(-105.37, -157.26) * mm});
            skLineSegment(sketch, "E717.left", {"start": v(-119.27, -143.36) * mm, "end": v(-119.27, -155.76) * mm});
            skLineSegment(sketch, "E717.right", {"start": v(-103.87, -143.36) * mm, "end": v(-103.87, -155.76) * mm});
            skPoint(sketch, "E718.visualSharp", {"position": v(-119.27, -141.86) * mm});
            skArc(sketch, "E718.filletArc", {"start": v(-117.77, -141.86) * mm, "mid": v(-118.83, -142.3) * mm, "end": v(-119.27, -143.36) * mm});
            skPoint(sketch, "E719.visualSharp", {"position": v(-103.87, -141.86) * mm});
            skArc(sketch, "E719.filletArc", {"start": v(-103.87, -143.36) * mm, "mid": v(-104.31, -142.3) * mm, "end": v(-105.37, -141.86) * mm});
            skPoint(sketch, "E720.visualSharp", {"position": v(-119.27, -157.26) * mm});
            skArc(sketch, "E720.filletArc", {"start": v(-119.27, -155.76) * mm, "mid": v(-118.83, -156.82) * mm, "end": v(-117.77, -157.26) * mm});
            skPoint(sketch, "E721.visualSharp", {"position": v(-103.87, -157.26) * mm});
            skArc(sketch, "E721.filletArc", {"start": v(-105.37, -157.26) * mm, "mid": v(-104.31, -156.82) * mm, "end": v(-103.87, -155.76) * mm});
            skLineSegment(sketch, "E722.bottom", {"start": v(-117.77, -122.86) * mm, "end": v(-105.37, -122.86) * mm});
            skLineSegment(sketch, "E722.top", {"start": v(-117.77, -138.26) * mm, "end": v(-105.37, -138.26) * mm});
            skLineSegment(sketch, "E722.left", {"start": v(-119.27, -124.36) * mm, "end": v(-119.27, -136.76) * mm});
            skLineSegment(sketch, "E722.right", {"start": v(-103.87, -124.36) * mm, "end": v(-103.87, -136.76) * mm});
            skPoint(sketch, "E723.visualSharp", {"position": v(-119.27, -122.86) * mm});
            skArc(sketch, "E723.filletArc", {"start": v(-117.77, -122.86) * mm, "mid": v(-118.83, -123.3) * mm, "end": v(-119.27, -124.36) * mm});
            skPoint(sketch, "E724.visualSharp", {"position": v(-103.87, -122.86) * mm});
            skArc(sketch, "E724.filletArc", {"start": v(-103.87, -124.36) * mm, "mid": v(-104.31, -123.3) * mm, "end": v(-105.37, -122.86) * mm});
            skPoint(sketch, "E725.visualSharp", {"position": v(-119.27, -138.26) * mm});
            skArc(sketch, "E725.filletArc", {"start": v(-119.27, -136.76) * mm, "mid": v(-118.83, -137.82) * mm, "end": v(-117.77, -138.26) * mm});
            skPoint(sketch, "E726.visualSharp", {"position": v(-103.87, -138.26) * mm});
            skArc(sketch, "E726.filletArc", {"start": v(-105.37, -138.26) * mm, "mid": v(-104.31, -137.82) * mm, "end": v(-103.87, -136.76) * mm});
            skLineSegment(sketch, "E727.bottom", {"start": v(-117.77, -179.86) * mm, "end": v(-105.37, -179.86) * mm});
            skLineSegment(sketch, "E727.top", {"start": v(-117.77, -195.26) * mm, "end": v(-105.37, -195.26) * mm});
            skLineSegment(sketch, "E727.left", {"start": v(-119.27, -181.36) * mm, "end": v(-119.27, -193.76) * mm});
            skLineSegment(sketch, "E727.right", {"start": v(-103.87, -181.36) * mm, "end": v(-103.87, -193.76) * mm});
            skPoint(sketch, "E728.visualSharp", {"position": v(-119.27, -179.86) * mm});
            skArc(sketch, "E728.filletArc", {"start": v(-117.77, -179.86) * mm, "mid": v(-118.83, -180.3) * mm, "end": v(-119.27, -181.36) * mm});
            skPoint(sketch, "E729.visualSharp", {"position": v(-103.87, -179.86) * mm});
            skArc(sketch, "E729.filletArc", {"start": v(-103.87, -181.36) * mm, "mid": v(-104.31, -180.3) * mm, "end": v(-105.37, -179.86) * mm});
            skPoint(sketch, "E730.visualSharp", {"position": v(-119.27, -195.26) * mm});
            skArc(sketch, "E730.filletArc", {"start": v(-119.27, -193.76) * mm, "mid": v(-118.83, -194.82) * mm, "end": v(-117.77, -195.26) * mm});
            skPoint(sketch, "E731.visualSharp", {"position": v(-103.87, -195.26) * mm});
            skArc(sketch, "E731.filletArc", {"start": v(-105.37, -195.26) * mm, "mid": v(-104.31, -194.82) * mm, "end": v(-103.87, -193.76) * mm});
            skLineSegment(sketch, "E732.bottom", {"start": v(-117.77, -160.86) * mm, "end": v(-105.37, -160.86) * mm});
            skLineSegment(sketch, "E732.top", {"start": v(-117.77, -176.26) * mm, "end": v(-105.37, -176.26) * mm});
            skLineSegment(sketch, "E732.left", {"start": v(-119.27, -162.36) * mm, "end": v(-119.27, -174.76) * mm});
            skLineSegment(sketch, "E732.right", {"start": v(-103.87, -162.36) * mm, "end": v(-103.87, -174.76) * mm});
            skPoint(sketch, "E733.visualSharp", {"position": v(-119.27, -160.86) * mm});
            skArc(sketch, "E733.filletArc", {"start": v(-117.77, -160.86) * mm, "mid": v(-118.83, -161.3) * mm, "end": v(-119.27, -162.36) * mm});
            skPoint(sketch, "E734.visualSharp", {"position": v(-103.87, -160.86) * mm});
            skArc(sketch, "E734.filletArc", {"start": v(-103.87, -162.36) * mm, "mid": v(-104.31, -161.3) * mm, "end": v(-105.37, -160.86) * mm});
            skPoint(sketch, "E735.visualSharp", {"position": v(-119.27, -176.26) * mm});
            skArc(sketch, "E735.filletArc", {"start": v(-119.27, -174.76) * mm, "mid": v(-118.83, -175.82) * mm, "end": v(-117.77, -176.26) * mm});
            skPoint(sketch, "E736.visualSharp", {"position": v(-103.87, -176.26) * mm});
            skArc(sketch, "E736.filletArc", {"start": v(-105.37, -176.26) * mm, "mid": v(-104.31, -175.82) * mm, "end": v(-103.87, -174.76) * mm});
            skLineSegment(sketch, "E737.bottom", {"start": v(-117.77, -217.86) * mm, "end": v(-105.37, -217.86) * mm});
            skLineSegment(sketch, "E737.top", {"start": v(-117.77, -233.26) * mm, "end": v(-105.37, -233.26) * mm});
            skLineSegment(sketch, "E737.left", {"start": v(-119.27, -219.36) * mm, "end": v(-119.27, -231.76) * mm});
            skLineSegment(sketch, "E737.right", {"start": v(-103.87, -219.36) * mm, "end": v(-103.87, -231.76) * mm});
            skPoint(sketch, "E738.visualSharp", {"position": v(-119.27, -217.86) * mm});
            skArc(sketch, "E738.filletArc", {"start": v(-117.77, -217.86) * mm, "mid": v(-118.83, -218.3) * mm, "end": v(-119.27, -219.36) * mm});
            skPoint(sketch, "E739.visualSharp", {"position": v(-103.87, -217.86) * mm});
            skArc(sketch, "E739.filletArc", {"start": v(-103.87, -219.36) * mm, "mid": v(-104.31, -218.3) * mm, "end": v(-105.37, -217.86) * mm});
            skPoint(sketch, "E740.visualSharp", {"position": v(-119.27, -233.26) * mm});
            skArc(sketch, "E740.filletArc", {"start": v(-119.27, -231.76) * mm, "mid": v(-118.83, -232.82) * mm, "end": v(-117.77, -233.26) * mm});
            skPoint(sketch, "E741.visualSharp", {"position": v(-103.87, -233.26) * mm});
            skArc(sketch, "E741.filletArc", {"start": v(-105.37, -233.26) * mm, "mid": v(-104.31, -232.82) * mm, "end": v(-103.87, -231.76) * mm});
            skLineSegment(sketch, "E742.bottom", {"start": v(-117.77, -198.86) * mm, "end": v(-105.37, -198.86) * mm});
            skLineSegment(sketch, "E742.top", {"start": v(-117.77, -214.26) * mm, "end": v(-105.37, -214.26) * mm});
            skLineSegment(sketch, "E742.left", {"start": v(-119.27, -200.36) * mm, "end": v(-119.27, -212.76) * mm});
            skLineSegment(sketch, "E742.right", {"start": v(-103.87, -200.36) * mm, "end": v(-103.87, -212.76) * mm});
            skPoint(sketch, "E743.visualSharp", {"position": v(-119.27, -198.86) * mm});
            skArc(sketch, "E743.filletArc", {"start": v(-117.77, -198.86) * mm, "mid": v(-118.83, -199.3) * mm, "end": v(-119.27, -200.36) * mm});
            skPoint(sketch, "E744.visualSharp", {"position": v(-103.87, -198.86) * mm});
            skArc(sketch, "E744.filletArc", {"start": v(-103.87, -200.36) * mm, "mid": v(-104.31, -199.3) * mm, "end": v(-105.37, -198.86) * mm});
            skPoint(sketch, "E745.visualSharp", {"position": v(-119.27, -214.26) * mm});
            skArc(sketch, "E745.filletArc", {"start": v(-119.27, -212.76) * mm, "mid": v(-118.83, -213.82) * mm, "end": v(-117.77, -214.26) * mm});
            skPoint(sketch, "E746.visualSharp", {"position": v(-103.87, -214.26) * mm});
            skArc(sketch, "E746.filletArc", {"start": v(-105.37, -214.26) * mm, "mid": v(-104.31, -213.82) * mm, "end": v(-103.87, -212.76) * mm});
            skLineSegment(sketch, "E747.bottom", {"start": v(-167.27, -141.86) * mm, "end": v(-154.87, -141.86) * mm});
            skLineSegment(sketch, "E747.top", {"start": v(-167.27, -157.26) * mm, "end": v(-154.87, -157.26) * mm});
            skLineSegment(sketch, "E747.left", {"start": v(-168.77, -143.36) * mm, "end": v(-168.77, -155.76) * mm});
            skLineSegment(sketch, "E747.right", {"start": v(-153.37, -143.36) * mm, "end": v(-153.37, -155.76) * mm});
            skPoint(sketch, "E748.visualSharp", {"position": v(-168.77, -141.86) * mm});
            skArc(sketch, "E748.filletArc", {"start": v(-167.27, -141.86) * mm, "mid": v(-168.33, -142.3) * mm, "end": v(-168.77, -143.36) * mm});
            skPoint(sketch, "E749.visualSharp", {"position": v(-153.37, -141.86) * mm});
            skArc(sketch, "E749.filletArc", {"start": v(-153.37, -143.36) * mm, "mid": v(-153.81, -142.3) * mm, "end": v(-154.87, -141.86) * mm});
            skPoint(sketch, "E750.visualSharp", {"position": v(-168.77, -157.26) * mm});
            skArc(sketch, "E750.filletArc", {"start": v(-168.77, -155.76) * mm, "mid": v(-168.33, -156.82) * mm, "end": v(-167.27, -157.26) * mm});
            skPoint(sketch, "E751.visualSharp", {"position": v(-153.37, -157.26) * mm});
            skArc(sketch, "E751.filletArc", {"start": v(-154.87, -157.26) * mm, "mid": v(-153.81, -156.82) * mm, "end": v(-153.37, -155.76) * mm});
            skLineSegment(sketch, "E752.bottom", {"start": v(-167.27, -122.86) * mm, "end": v(-154.87, -122.86) * mm});
            skLineSegment(sketch, "E752.top", {"start": v(-167.27, -138.26) * mm, "end": v(-154.87, -138.26) * mm});
            skLineSegment(sketch, "E752.left", {"start": v(-168.77, -124.36) * mm, "end": v(-168.77, -136.76) * mm});
            skLineSegment(sketch, "E752.right", {"start": v(-153.37, -124.36) * mm, "end": v(-153.37, -136.76) * mm});
            skPoint(sketch, "E753.visualSharp", {"position": v(-168.77, -122.86) * mm});
            skArc(sketch, "E753.filletArc", {"start": v(-167.27, -122.86) * mm, "mid": v(-168.33, -123.3) * mm, "end": v(-168.77, -124.36) * mm});
            skPoint(sketch, "E754.visualSharp", {"position": v(-153.37, -122.86) * mm});
            skArc(sketch, "E754.filletArc", {"start": v(-153.37, -124.36) * mm, "mid": v(-153.81, -123.3) * mm, "end": v(-154.87, -122.86) * mm});
            skPoint(sketch, "E755.visualSharp", {"position": v(-168.77, -138.26) * mm});
            skArc(sketch, "E755.filletArc", {"start": v(-168.77, -136.76) * mm, "mid": v(-168.33, -137.82) * mm, "end": v(-167.27, -138.26) * mm});
            skPoint(sketch, "E756.visualSharp", {"position": v(-153.37, -138.26) * mm});
            skArc(sketch, "E756.filletArc", {"start": v(-154.87, -138.26) * mm, "mid": v(-153.81, -137.82) * mm, "end": v(-153.37, -136.76) * mm});
            skLineSegment(sketch, "E757.bottom", {"start": v(-167.27, -179.86) * mm, "end": v(-154.87, -179.86) * mm});
            skLineSegment(sketch, "E757.top", {"start": v(-167.27, -195.26) * mm, "end": v(-154.87, -195.26) * mm});
            skLineSegment(sketch, "E757.left", {"start": v(-168.77, -181.36) * mm, "end": v(-168.77, -193.76) * mm});
            skLineSegment(sketch, "E757.right", {"start": v(-153.37, -181.36) * mm, "end": v(-153.37, -193.76) * mm});
            skPoint(sketch, "E758.visualSharp", {"position": v(-168.77, -179.86) * mm});
            skArc(sketch, "E758.filletArc", {"start": v(-167.27, -179.86) * mm, "mid": v(-168.33, -180.3) * mm, "end": v(-168.77, -181.36) * mm});
            skPoint(sketch, "E759.visualSharp", {"position": v(-153.37, -179.86) * mm});
            skArc(sketch, "E759.filletArc", {"start": v(-153.37, -181.36) * mm, "mid": v(-153.81, -180.3) * mm, "end": v(-154.87, -179.86) * mm});
            skPoint(sketch, "E760.visualSharp", {"position": v(-168.77, -195.26) * mm});
            skArc(sketch, "E760.filletArc", {"start": v(-168.77, -193.76) * mm, "mid": v(-168.33, -194.82) * mm, "end": v(-167.27, -195.26) * mm});
            skPoint(sketch, "E761.visualSharp", {"position": v(-153.37, -195.26) * mm});
            skArc(sketch, "E761.filletArc", {"start": v(-154.87, -195.26) * mm, "mid": v(-153.81, -194.82) * mm, "end": v(-153.37, -193.76) * mm});
            skLineSegment(sketch, "E762.bottom", {"start": v(-167.27, -160.86) * mm, "end": v(-154.87, -160.86) * mm});
            skLineSegment(sketch, "E762.top", {"start": v(-167.27, -176.26) * mm, "end": v(-154.87, -176.26) * mm});
            skLineSegment(sketch, "E762.left", {"start": v(-168.77, -162.36) * mm, "end": v(-168.77, -174.76) * mm});
            skLineSegment(sketch, "E762.right", {"start": v(-153.37, -162.36) * mm, "end": v(-153.37, -174.76) * mm});
            skPoint(sketch, "E763.visualSharp", {"position": v(-168.77, -160.86) * mm});
            skArc(sketch, "E763.filletArc", {"start": v(-167.27, -160.86) * mm, "mid": v(-168.33, -161.3) * mm, "end": v(-168.77, -162.36) * mm});
            skPoint(sketch, "E764.visualSharp", {"position": v(-153.37, -160.86) * mm});
            skArc(sketch, "E764.filletArc", {"start": v(-153.37, -162.36) * mm, "mid": v(-153.81, -161.3) * mm, "end": v(-154.87, -160.86) * mm});
            skPoint(sketch, "E765.visualSharp", {"position": v(-168.77, -176.26) * mm});
            skArc(sketch, "E765.filletArc", {"start": v(-168.77, -174.76) * mm, "mid": v(-168.33, -175.82) * mm, "end": v(-167.27, -176.26) * mm});
            skPoint(sketch, "E766.visualSharp", {"position": v(-153.37, -176.26) * mm});
            skArc(sketch, "E766.filletArc", {"start": v(-154.87, -176.26) * mm, "mid": v(-153.81, -175.82) * mm, "end": v(-153.37, -174.76) * mm});
            skLineSegment(sketch, "E767.bottom", {"start": v(-167.27, -217.86) * mm, "end": v(-154.87, -217.86) * mm});
            skLineSegment(sketch, "E767.top", {"start": v(-167.27, -233.26) * mm, "end": v(-154.87, -233.26) * mm});
            skLineSegment(sketch, "E767.left", {"start": v(-168.77, -219.36) * mm, "end": v(-168.77, -231.76) * mm});
            skLineSegment(sketch, "E767.right", {"start": v(-153.37, -219.36) * mm, "end": v(-153.37, -231.76) * mm});
            skPoint(sketch, "E768.visualSharp", {"position": v(-168.77, -217.86) * mm});
            skArc(sketch, "E768.filletArc", {"start": v(-167.27, -217.86) * mm, "mid": v(-168.33, -218.3) * mm, "end": v(-168.77, -219.36) * mm});
            skPoint(sketch, "E769.visualSharp", {"position": v(-153.37, -217.86) * mm});
            skArc(sketch, "E769.filletArc", {"start": v(-153.37, -219.36) * mm, "mid": v(-153.81, -218.3) * mm, "end": v(-154.87, -217.86) * mm});
            skPoint(sketch, "E770.visualSharp", {"position": v(-168.77, -233.26) * mm});
            skArc(sketch, "E770.filletArc", {"start": v(-168.77, -231.76) * mm, "mid": v(-168.33, -232.82) * mm, "end": v(-167.27, -233.26) * mm});
            skPoint(sketch, "E771.visualSharp", {"position": v(-153.37, -233.26) * mm});
            skArc(sketch, "E771.filletArc", {"start": v(-154.87, -233.26) * mm, "mid": v(-153.81, -232.82) * mm, "end": v(-153.37, -231.76) * mm});
            skLineSegment(sketch, "E772.bottom", {"start": v(-167.27, -198.86) * mm, "end": v(-154.87, -198.86) * mm});
            skLineSegment(sketch, "E772.top", {"start": v(-167.27, -214.26) * mm, "end": v(-154.87, -214.26) * mm});
            skLineSegment(sketch, "E772.left", {"start": v(-168.77, -200.36) * mm, "end": v(-168.77, -212.76) * mm});
            skLineSegment(sketch, "E772.right", {"start": v(-153.37, -200.36) * mm, "end": v(-153.37, -212.76) * mm});
            skPoint(sketch, "E773.visualSharp", {"position": v(-168.77, -198.86) * mm});
            skArc(sketch, "E773.filletArc", {"start": v(-167.27, -198.86) * mm, "mid": v(-168.33, -199.3) * mm, "end": v(-168.77, -200.36) * mm});
            skPoint(sketch, "E774.visualSharp", {"position": v(-153.37, -198.86) * mm});
            skArc(sketch, "E774.filletArc", {"start": v(-153.37, -200.36) * mm, "mid": v(-153.81, -199.3) * mm, "end": v(-154.87, -198.86) * mm});
            skPoint(sketch, "E775.visualSharp", {"position": v(-168.77, -214.26) * mm});
            skArc(sketch, "E775.filletArc", {"start": v(-168.77, -212.76) * mm, "mid": v(-168.33, -213.82) * mm, "end": v(-167.27, -214.26) * mm});
            skPoint(sketch, "E776.visualSharp", {"position": v(-153.37, -214.26) * mm});
            skArc(sketch, "E776.filletArc", {"start": v(-154.87, -214.26) * mm, "mid": v(-153.81, -213.82) * mm, "end": v(-153.37, -212.76) * mm});
            skLineSegment(sketch, "E777.bottom", {"start": v(-134.27, -141.86) * mm, "end": v(-121.87, -141.86) * mm});
            skLineSegment(sketch, "E777.top", {"start": v(-134.27, -157.26) * mm, "end": v(-121.87, -157.26) * mm});
            skLineSegment(sketch, "E777.left", {"start": v(-135.77, -143.36) * mm, "end": v(-135.77, -155.76) * mm});
            skLineSegment(sketch, "E777.right", {"start": v(-120.37, -143.36) * mm, "end": v(-120.37, -155.76) * mm});
            skPoint(sketch, "E778.visualSharp", {"position": v(-135.77, -141.86) * mm});
            skArc(sketch, "E778.filletArc", {"start": v(-134.27, -141.86) * mm, "mid": v(-135.33, -142.3) * mm, "end": v(-135.77, -143.36) * mm});
            skPoint(sketch, "E779.visualSharp", {"position": v(-120.37, -141.86) * mm});
            skArc(sketch, "E779.filletArc", {"start": v(-120.37, -143.36) * mm, "mid": v(-120.81, -142.3) * mm, "end": v(-121.87, -141.86) * mm});
            skPoint(sketch, "E780.visualSharp", {"position": v(-135.77, -157.26) * mm});
            skArc(sketch, "E780.filletArc", {"start": v(-135.77, -155.76) * mm, "mid": v(-135.33, -156.82) * mm, "end": v(-134.27, -157.26) * mm});
            skPoint(sketch, "E781.visualSharp", {"position": v(-120.37, -157.26) * mm});
            skArc(sketch, "E781.filletArc", {"start": v(-121.87, -157.26) * mm, "mid": v(-120.81, -156.82) * mm, "end": v(-120.37, -155.76) * mm});
            skLineSegment(sketch, "E782.bottom", {"start": v(-134.27, -122.86) * mm, "end": v(-121.87, -122.86) * mm});
            skLineSegment(sketch, "E782.top", {"start": v(-134.27, -138.26) * mm, "end": v(-121.87, -138.26) * mm});
            skLineSegment(sketch, "E782.left", {"start": v(-135.77, -124.36) * mm, "end": v(-135.77, -136.76) * mm});
            skLineSegment(sketch, "E782.right", {"start": v(-120.37, -124.36) * mm, "end": v(-120.37, -136.76) * mm});
            skPoint(sketch, "E783.visualSharp", {"position": v(-135.77, -122.86) * mm});
            skArc(sketch, "E783.filletArc", {"start": v(-134.27, -122.86) * mm, "mid": v(-135.33, -123.3) * mm, "end": v(-135.77, -124.36) * mm});
            skPoint(sketch, "E784.visualSharp", {"position": v(-120.37, -122.86) * mm});
            skArc(sketch, "E784.filletArc", {"start": v(-120.37, -124.36) * mm, "mid": v(-120.81, -123.3) * mm, "end": v(-121.87, -122.86) * mm});
            skPoint(sketch, "E785.visualSharp", {"position": v(-135.77, -138.26) * mm});
            skArc(sketch, "E785.filletArc", {"start": v(-135.77, -136.76) * mm, "mid": v(-135.33, -137.82) * mm, "end": v(-134.27, -138.26) * mm});
            skPoint(sketch, "E786.visualSharp", {"position": v(-120.37, -138.26) * mm});
            skArc(sketch, "E786.filletArc", {"start": v(-121.87, -138.26) * mm, "mid": v(-120.81, -137.82) * mm, "end": v(-120.37, -136.76) * mm});
            skLineSegment(sketch, "E787.bottom", {"start": v(-134.27, -179.86) * mm, "end": v(-121.87, -179.86) * mm});
            skLineSegment(sketch, "E787.top", {"start": v(-134.27, -195.26) * mm, "end": v(-121.87, -195.26) * mm});
            skLineSegment(sketch, "E787.left", {"start": v(-135.77, -181.36) * mm, "end": v(-135.77, -193.76) * mm});
            skLineSegment(sketch, "E787.right", {"start": v(-120.37, -181.36) * mm, "end": v(-120.37, -193.76) * mm});
            skPoint(sketch, "E788.visualSharp", {"position": v(-135.77, -179.86) * mm});
            skArc(sketch, "E788.filletArc", {"start": v(-134.27, -179.86) * mm, "mid": v(-135.33, -180.3) * mm, "end": v(-135.77, -181.36) * mm});
            skPoint(sketch, "E789.visualSharp", {"position": v(-120.37, -179.86) * mm});
            skArc(sketch, "E789.filletArc", {"start": v(-120.37, -181.36) * mm, "mid": v(-120.81, -180.3) * mm, "end": v(-121.87, -179.86) * mm});
            skPoint(sketch, "E790.visualSharp", {"position": v(-135.77, -195.26) * mm});
            skArc(sketch, "E790.filletArc", {"start": v(-135.77, -193.76) * mm, "mid": v(-135.33, -194.82) * mm, "end": v(-134.27, -195.26) * mm});
            skPoint(sketch, "E791.visualSharp", {"position": v(-120.37, -195.26) * mm});
            skArc(sketch, "E791.filletArc", {"start": v(-121.87, -195.26) * mm, "mid": v(-120.81, -194.82) * mm, "end": v(-120.37, -193.76) * mm});
            skLineSegment(sketch, "E792.bottom", {"start": v(-134.27, -160.86) * mm, "end": v(-121.87, -160.86) * mm});
            skLineSegment(sketch, "E792.top", {"start": v(-134.27, -176.26) * mm, "end": v(-121.87, -176.26) * mm});
            skLineSegment(sketch, "E792.left", {"start": v(-135.77, -162.36) * mm, "end": v(-135.77, -174.76) * mm});
            skLineSegment(sketch, "E792.right", {"start": v(-120.37, -162.36) * mm, "end": v(-120.37, -174.76) * mm});
            skPoint(sketch, "E793.visualSharp", {"position": v(-135.77, -160.86) * mm});
            skArc(sketch, "E793.filletArc", {"start": v(-134.27, -160.86) * mm, "mid": v(-135.33, -161.3) * mm, "end": v(-135.77, -162.36) * mm});
            skPoint(sketch, "E794.visualSharp", {"position": v(-120.37, -160.86) * mm});
            skArc(sketch, "E794.filletArc", {"start": v(-120.37, -162.36) * mm, "mid": v(-120.81, -161.3) * mm, "end": v(-121.87, -160.86) * mm});
            skPoint(sketch, "E795.visualSharp", {"position": v(-135.77, -176.26) * mm});
            skArc(sketch, "E795.filletArc", {"start": v(-135.77, -174.76) * mm, "mid": v(-135.33, -175.82) * mm, "end": v(-134.27, -176.26) * mm});
            skPoint(sketch, "E796.visualSharp", {"position": v(-120.37, -176.26) * mm});
            skArc(sketch, "E796.filletArc", {"start": v(-121.87, -176.26) * mm, "mid": v(-120.81, -175.82) * mm, "end": v(-120.37, -174.76) * mm});
            skLineSegment(sketch, "E797.bottom", {"start": v(-134.27, -217.86) * mm, "end": v(-121.87, -217.86) * mm});
            skLineSegment(sketch, "E797.top", {"start": v(-134.27, -233.26) * mm, "end": v(-121.87, -233.26) * mm});
            skLineSegment(sketch, "E797.left", {"start": v(-135.77, -219.36) * mm, "end": v(-135.77, -231.76) * mm});
            skLineSegment(sketch, "E797.right", {"start": v(-120.37, -219.36) * mm, "end": v(-120.37, -231.76) * mm});
            skPoint(sketch, "E798.visualSharp", {"position": v(-135.77, -217.86) * mm});
            skArc(sketch, "E798.filletArc", {"start": v(-134.27, -217.86) * mm, "mid": v(-135.33, -218.3) * mm, "end": v(-135.77, -219.36) * mm});
            skPoint(sketch, "E799.visualSharp", {"position": v(-120.37, -217.86) * mm});
            skArc(sketch, "E799.filletArc", {"start": v(-120.37, -219.36) * mm, "mid": v(-120.81, -218.3) * mm, "end": v(-121.87, -217.86) * mm});
            skPoint(sketch, "E800.visualSharp", {"position": v(-135.77, -233.26) * mm});
            skArc(sketch, "E800.filletArc", {"start": v(-135.77, -231.76) * mm, "mid": v(-135.33, -232.82) * mm, "end": v(-134.27, -233.26) * mm});
            skPoint(sketch, "E801.visualSharp", {"position": v(-120.37, -233.26) * mm});
            skArc(sketch, "E801.filletArc", {"start": v(-121.87, -233.26) * mm, "mid": v(-120.81, -232.82) * mm, "end": v(-120.37, -231.76) * mm});
            skLineSegment(sketch, "E802.bottom", {"start": v(-134.27, -198.86) * mm, "end": v(-121.87, -198.86) * mm});
            skLineSegment(sketch, "E802.top", {"start": v(-134.27, -214.26) * mm, "end": v(-121.87, -214.26) * mm});
            skLineSegment(sketch, "E802.left", {"start": v(-135.77, -200.36) * mm, "end": v(-135.77, -212.76) * mm});
            skLineSegment(sketch, "E802.right", {"start": v(-120.37, -200.36) * mm, "end": v(-120.37, -212.76) * mm});
            skPoint(sketch, "E803.visualSharp", {"position": v(-135.77, -198.86) * mm});
            skArc(sketch, "E803.filletArc", {"start": v(-134.27, -198.86) * mm, "mid": v(-135.33, -199.3) * mm, "end": v(-135.77, -200.36) * mm});
            skPoint(sketch, "E804.visualSharp", {"position": v(-120.37, -198.86) * mm});
            skArc(sketch, "E804.filletArc", {"start": v(-120.37, -200.36) * mm, "mid": v(-120.81, -199.3) * mm, "end": v(-121.87, -198.86) * mm});
            skPoint(sketch, "E805.visualSharp", {"position": v(-135.77, -214.26) * mm});
            skArc(sketch, "E805.filletArc", {"start": v(-135.77, -212.76) * mm, "mid": v(-135.33, -213.82) * mm, "end": v(-134.27, -214.26) * mm});
            skPoint(sketch, "E806.visualSharp", {"position": v(-120.37, -214.26) * mm});
            skArc(sketch, "E806.filletArc", {"start": v(-121.87, -214.26) * mm, "mid": v(-120.81, -213.82) * mm, "end": v(-120.37, -212.76) * mm});
            skLineSegment(sketch, "E807.bottom", {"start": v(-150.77, -141.86) * mm, "end": v(-138.37, -141.86) * mm});
            skLineSegment(sketch, "E807.top", {"start": v(-150.77, -157.26) * mm, "end": v(-138.37, -157.26) * mm});
            skLineSegment(sketch, "E807.left", {"start": v(-152.27, -143.36) * mm, "end": v(-152.27, -155.76) * mm});
            skLineSegment(sketch, "E807.right", {"start": v(-136.87, -143.36) * mm, "end": v(-136.87, -155.76) * mm});
            skPoint(sketch, "E808.visualSharp", {"position": v(-152.27, -141.86) * mm});
            skArc(sketch, "E808.filletArc", {"start": v(-150.77, -141.86) * mm, "mid": v(-151.83, -142.3) * mm, "end": v(-152.27, -143.36) * mm});
            skPoint(sketch, "E809.visualSharp", {"position": v(-136.87, -141.86) * mm});
            skArc(sketch, "E809.filletArc", {"start": v(-136.87, -143.36) * mm, "mid": v(-137.31, -142.3) * mm, "end": v(-138.37, -141.86) * mm});
            skPoint(sketch, "E810.visualSharp", {"position": v(-152.27, -157.26) * mm});
            skArc(sketch, "E810.filletArc", {"start": v(-152.27, -155.76) * mm, "mid": v(-151.83, -156.82) * mm, "end": v(-150.77, -157.26) * mm});
            skPoint(sketch, "E811.visualSharp", {"position": v(-136.87, -157.26) * mm});
            skArc(sketch, "E811.filletArc", {"start": v(-138.37, -157.26) * mm, "mid": v(-137.31, -156.82) * mm, "end": v(-136.87, -155.76) * mm});
            skLineSegment(sketch, "E812.bottom", {"start": v(-150.77, -122.86) * mm, "end": v(-138.37, -122.86) * mm});
            skLineSegment(sketch, "E812.top", {"start": v(-150.77, -138.26) * mm, "end": v(-138.37, -138.26) * mm});
            skLineSegment(sketch, "E812.left", {"start": v(-152.27, -124.36) * mm, "end": v(-152.27, -136.76) * mm});
            skLineSegment(sketch, "E812.right", {"start": v(-136.87, -124.36) * mm, "end": v(-136.87, -136.76) * mm});
            skPoint(sketch, "E813.visualSharp", {"position": v(-152.27, -122.86) * mm});
            skArc(sketch, "E813.filletArc", {"start": v(-150.77, -122.86) * mm, "mid": v(-151.83, -123.3) * mm, "end": v(-152.27, -124.36) * mm});
            skPoint(sketch, "E814.visualSharp", {"position": v(-136.87, -122.86) * mm});
            skArc(sketch, "E814.filletArc", {"start": v(-136.87, -124.36) * mm, "mid": v(-137.31, -123.3) * mm, "end": v(-138.37, -122.86) * mm});
            skPoint(sketch, "E815.visualSharp", {"position": v(-152.27, -138.26) * mm});
            skArc(sketch, "E815.filletArc", {"start": v(-152.27, -136.76) * mm, "mid": v(-151.83, -137.82) * mm, "end": v(-150.77, -138.26) * mm});
            skPoint(sketch, "E816.visualSharp", {"position": v(-136.87, -138.26) * mm});
            skArc(sketch, "E816.filletArc", {"start": v(-138.37, -138.26) * mm, "mid": v(-137.31, -137.82) * mm, "end": v(-136.87, -136.76) * mm});
            skLineSegment(sketch, "E817.bottom", {"start": v(-150.77, -179.86) * mm, "end": v(-138.37, -179.86) * mm});
            skLineSegment(sketch, "E817.top", {"start": v(-150.77, -195.26) * mm, "end": v(-138.37, -195.26) * mm});
            skLineSegment(sketch, "E817.left", {"start": v(-152.27, -181.36) * mm, "end": v(-152.27, -193.76) * mm});
            skLineSegment(sketch, "E817.right", {"start": v(-136.87, -181.36) * mm, "end": v(-136.87, -193.76) * mm});
            skPoint(sketch, "E818.visualSharp", {"position": v(-152.27, -179.86) * mm});
            skArc(sketch, "E818.filletArc", {"start": v(-150.77, -179.86) * mm, "mid": v(-151.83, -180.3) * mm, "end": v(-152.27, -181.36) * mm});
            skPoint(sketch, "E819.visualSharp", {"position": v(-136.87, -179.86) * mm});
            skArc(sketch, "E819.filletArc", {"start": v(-136.87, -181.36) * mm, "mid": v(-137.31, -180.3) * mm, "end": v(-138.37, -179.86) * mm});
            skPoint(sketch, "E820.visualSharp", {"position": v(-152.27, -195.26) * mm});
            skArc(sketch, "E820.filletArc", {"start": v(-152.27, -193.76) * mm, "mid": v(-151.83, -194.82) * mm, "end": v(-150.77, -195.26) * mm});
            skPoint(sketch, "E821.visualSharp", {"position": v(-136.87, -195.26) * mm});
            skArc(sketch, "E821.filletArc", {"start": v(-138.37, -195.26) * mm, "mid": v(-137.31, -194.82) * mm, "end": v(-136.87, -193.76) * mm});
            skLineSegment(sketch, "E822.bottom", {"start": v(-150.77, -160.86) * mm, "end": v(-138.37, -160.86) * mm});
            skLineSegment(sketch, "E822.top", {"start": v(-150.77, -176.26) * mm, "end": v(-138.37, -176.26) * mm});
            skLineSegment(sketch, "E822.left", {"start": v(-152.27, -162.36) * mm, "end": v(-152.27, -174.76) * mm});
            skLineSegment(sketch, "E822.right", {"start": v(-136.87, -162.36) * mm, "end": v(-136.87, -174.76) * mm});
            skPoint(sketch, "E823.visualSharp", {"position": v(-152.27, -160.86) * mm});
            skArc(sketch, "E823.filletArc", {"start": v(-150.77, -160.86) * mm, "mid": v(-151.83, -161.3) * mm, "end": v(-152.27, -162.36) * mm});
            skPoint(sketch, "E824.visualSharp", {"position": v(-136.87, -160.86) * mm});
            skArc(sketch, "E824.filletArc", {"start": v(-136.87, -162.36) * mm, "mid": v(-137.31, -161.3) * mm, "end": v(-138.37, -160.86) * mm});
            skPoint(sketch, "E825.visualSharp", {"position": v(-152.27, -176.26) * mm});
            skArc(sketch, "E825.filletArc", {"start": v(-152.27, -174.76) * mm, "mid": v(-151.83, -175.82) * mm, "end": v(-150.77, -176.26) * mm});
            skPoint(sketch, "E826.visualSharp", {"position": v(-136.87, -176.26) * mm});
            skArc(sketch, "E826.filletArc", {"start": v(-138.37, -176.26) * mm, "mid": v(-137.31, -175.82) * mm, "end": v(-136.87, -174.76) * mm});
            skLineSegment(sketch, "E827.bottom", {"start": v(-150.77, -217.86) * mm, "end": v(-138.37, -217.86) * mm});
            skLineSegment(sketch, "E827.top", {"start": v(-150.77, -233.26) * mm, "end": v(-138.37, -233.26) * mm});
            skLineSegment(sketch, "E827.left", {"start": v(-152.27, -219.36) * mm, "end": v(-152.27, -231.76) * mm});
            skLineSegment(sketch, "E827.right", {"start": v(-136.87, -219.36) * mm, "end": v(-136.87, -231.76) * mm});
            skPoint(sketch, "E828.visualSharp", {"position": v(-152.27, -217.86) * mm});
            skArc(sketch, "E828.filletArc", {"start": v(-150.77, -217.86) * mm, "mid": v(-151.83, -218.3) * mm, "end": v(-152.27, -219.36) * mm});
            skPoint(sketch, "E829.visualSharp", {"position": v(-136.87, -217.86) * mm});
            skArc(sketch, "E829.filletArc", {"start": v(-136.87, -219.36) * mm, "mid": v(-137.31, -218.3) * mm, "end": v(-138.37, -217.86) * mm});
            skPoint(sketch, "E830.visualSharp", {"position": v(-152.27, -233.26) * mm});
            skArc(sketch, "E830.filletArc", {"start": v(-152.27, -231.76) * mm, "mid": v(-151.83, -232.82) * mm, "end": v(-150.77, -233.26) * mm});
            skPoint(sketch, "E831.visualSharp", {"position": v(-136.87, -233.26) * mm});
            skArc(sketch, "E831.filletArc", {"start": v(-138.37, -233.26) * mm, "mid": v(-137.31, -232.82) * mm, "end": v(-136.87, -231.76) * mm});
            skLineSegment(sketch, "E832.bottom", {"start": v(-150.77, -198.86) * mm, "end": v(-138.37, -198.86) * mm});
            skLineSegment(sketch, "E832.top", {"start": v(-150.77, -214.26) * mm, "end": v(-138.37, -214.26) * mm});
            skLineSegment(sketch, "E832.left", {"start": v(-152.27, -200.36) * mm, "end": v(-152.27, -212.76) * mm});
            skLineSegment(sketch, "E832.right", {"start": v(-136.87, -200.36) * mm, "end": v(-136.87, -212.76) * mm});
            skPoint(sketch, "E833.visualSharp", {"position": v(-152.27, -198.86) * mm});
            skArc(sketch, "E833.filletArc", {"start": v(-150.77, -198.86) * mm, "mid": v(-151.83, -199.3) * mm, "end": v(-152.27, -200.36) * mm});
            skPoint(sketch, "E834.visualSharp", {"position": v(-136.87, -198.86) * mm});
            skArc(sketch, "E834.filletArc", {"start": v(-136.87, -200.36) * mm, "mid": v(-137.31, -199.3) * mm, "end": v(-138.37, -198.86) * mm});
            skPoint(sketch, "E835.visualSharp", {"position": v(-152.27, -214.26) * mm});
            skArc(sketch, "E835.filletArc", {"start": v(-152.27, -212.76) * mm, "mid": v(-151.83, -213.82) * mm, "end": v(-150.77, -214.26) * mm});
            skPoint(sketch, "E836.visualSharp", {"position": v(-136.87, -214.26) * mm});
            skArc(sketch, "E836.filletArc", {"start": v(-138.37, -214.26) * mm, "mid": v(-137.31, -213.82) * mm, "end": v(-136.87, -212.76) * mm});
            skLineSegment(sketch, "E837.bottom", {"start": v(162.73, -141.86) * mm, "end": v(175.13, -141.86) * mm});
            skLineSegment(sketch, "E837.top", {"start": v(162.73, -157.26) * mm, "end": v(175.13, -157.26) * mm});
            skLineSegment(sketch, "E837.left", {"start": v(161.23, -143.36) * mm, "end": v(161.23, -155.76) * mm});
            skLineSegment(sketch, "E837.right", {"start": v(176.63, -143.36) * mm, "end": v(176.63, -155.76) * mm});
            skPoint(sketch, "E838.visualSharp", {"position": v(161.23, -141.86) * mm});
            skArc(sketch, "E838.filletArc", {"start": v(162.73, -141.86) * mm, "mid": v(161.67, -142.3) * mm, "end": v(161.23, -143.36) * mm});
            skPoint(sketch, "E839.visualSharp", {"position": v(176.63, -141.86) * mm});
            skArc(sketch, "E839.filletArc", {"start": v(176.63, -143.36) * mm, "mid": v(176.19, -142.3) * mm, "end": v(175.13, -141.86) * mm});
            skPoint(sketch, "E840.visualSharp", {"position": v(161.23, -157.26) * mm});
            skArc(sketch, "E840.filletArc", {"start": v(161.23, -155.76) * mm, "mid": v(161.67, -156.82) * mm, "end": v(162.73, -157.26) * mm});
            skPoint(sketch, "E841.visualSharp", {"position": v(176.63, -157.26) * mm});
            skArc(sketch, "E841.filletArc", {"start": v(175.13, -157.26) * mm, "mid": v(176.19, -156.82) * mm, "end": v(176.63, -155.76) * mm});
            skLineSegment(sketch, "E842.bottom", {"start": v(162.73, -122.86) * mm, "end": v(175.13, -122.86) * mm});
            skLineSegment(sketch, "E842.top", {"start": v(162.73, -138.26) * mm, "end": v(175.13, -138.26) * mm});
            skLineSegment(sketch, "E842.left", {"start": v(161.23, -124.36) * mm, "end": v(161.23, -136.76) * mm});
            skLineSegment(sketch, "E842.right", {"start": v(176.63, -124.36) * mm, "end": v(176.63, -136.76) * mm});
            skPoint(sketch, "E843.visualSharp", {"position": v(161.23, -122.86) * mm});
            skArc(sketch, "E843.filletArc", {"start": v(162.73, -122.86) * mm, "mid": v(161.67, -123.3) * mm, "end": v(161.23, -124.36) * mm});
            skPoint(sketch, "E844.visualSharp", {"position": v(176.63, -122.86) * mm});
            skArc(sketch, "E844.filletArc", {"start": v(176.63, -124.36) * mm, "mid": v(176.19, -123.3) * mm, "end": v(175.13, -122.86) * mm});
            skPoint(sketch, "E845.visualSharp", {"position": v(161.23, -138.26) * mm});
            skArc(sketch, "E845.filletArc", {"start": v(161.23, -136.76) * mm, "mid": v(161.67, -137.82) * mm, "end": v(162.73, -138.26) * mm});
            skPoint(sketch, "E846.visualSharp", {"position": v(176.63, -138.26) * mm});
            skArc(sketch, "E846.filletArc", {"start": v(175.13, -138.26) * mm, "mid": v(176.19, -137.82) * mm, "end": v(176.63, -136.76) * mm});
            skLineSegment(sketch, "E847.bottom", {"start": v(162.73, -179.86) * mm, "end": v(175.13, -179.86) * mm});
            skLineSegment(sketch, "E847.top", {"start": v(162.73, -195.26) * mm, "end": v(175.13, -195.26) * mm});
            skLineSegment(sketch, "E847.left", {"start": v(161.23, -181.36) * mm, "end": v(161.23, -193.76) * mm});
            skLineSegment(sketch, "E847.right", {"start": v(176.63, -181.36) * mm, "end": v(176.63, -193.76) * mm});
            skPoint(sketch, "E848.visualSharp", {"position": v(161.23, -179.86) * mm});
            skArc(sketch, "E848.filletArc", {"start": v(162.73, -179.86) * mm, "mid": v(161.67, -180.3) * mm, "end": v(161.23, -181.36) * mm});
            skPoint(sketch, "E849.visualSharp", {"position": v(176.63, -179.86) * mm});
            skArc(sketch, "E849.filletArc", {"start": v(176.63, -181.36) * mm, "mid": v(176.19, -180.3) * mm, "end": v(175.13, -179.86) * mm});
            skPoint(sketch, "E850.visualSharp", {"position": v(161.23, -195.26) * mm});
            skArc(sketch, "E850.filletArc", {"start": v(161.23, -193.76) * mm, "mid": v(161.67, -194.82) * mm, "end": v(162.73, -195.26) * mm});
            skPoint(sketch, "E851.visualSharp", {"position": v(176.63, -195.26) * mm});
            skArc(sketch, "E851.filletArc", {"start": v(175.13, -195.26) * mm, "mid": v(176.19, -194.82) * mm, "end": v(176.63, -193.76) * mm});
            skLineSegment(sketch, "E852.bottom", {"start": v(162.73, -160.86) * mm, "end": v(175.13, -160.86) * mm});
            skLineSegment(sketch, "E852.top", {"start": v(162.73, -176.26) * mm, "end": v(175.13, -176.26) * mm});
            skLineSegment(sketch, "E852.left", {"start": v(161.23, -162.36) * mm, "end": v(161.23, -174.76) * mm});
            skLineSegment(sketch, "E852.right", {"start": v(176.63, -162.36) * mm, "end": v(176.63, -174.76) * mm});
            skPoint(sketch, "E853.visualSharp", {"position": v(161.23, -160.86) * mm});
            skArc(sketch, "E853.filletArc", {"start": v(162.73, -160.86) * mm, "mid": v(161.67, -161.3) * mm, "end": v(161.23, -162.36) * mm});
            skPoint(sketch, "E854.visualSharp", {"position": v(176.63, -160.86) * mm});
            skArc(sketch, "E854.filletArc", {"start": v(176.63, -162.36) * mm, "mid": v(176.19, -161.3) * mm, "end": v(175.13, -160.86) * mm});
            skPoint(sketch, "E855.visualSharp", {"position": v(161.23, -176.26) * mm});
            skArc(sketch, "E855.filletArc", {"start": v(161.23, -174.76) * mm, "mid": v(161.67, -175.82) * mm, "end": v(162.73, -176.26) * mm});
            skPoint(sketch, "E856.visualSharp", {"position": v(176.63, -176.26) * mm});
            skArc(sketch, "E856.filletArc", {"start": v(175.13, -176.26) * mm, "mid": v(176.19, -175.82) * mm, "end": v(176.63, -174.76) * mm});
            skLineSegment(sketch, "E857.bottom", {"start": v(162.73, -217.86) * mm, "end": v(175.13, -217.86) * mm});
            skLineSegment(sketch, "E857.top", {"start": v(162.73, -233.26) * mm, "end": v(175.13, -233.26) * mm});
            skLineSegment(sketch, "E857.left", {"start": v(161.23, -219.36) * mm, "end": v(161.23, -231.76) * mm});
            skLineSegment(sketch, "E857.right", {"start": v(176.63, -219.36) * mm, "end": v(176.63, -231.76) * mm});
            skPoint(sketch, "E858.visualSharp", {"position": v(161.23, -217.86) * mm});
            skArc(sketch, "E858.filletArc", {"start": v(162.73, -217.86) * mm, "mid": v(161.67, -218.3) * mm, "end": v(161.23, -219.36) * mm});
            skPoint(sketch, "E859.visualSharp", {"position": v(176.63, -217.86) * mm});
            skArc(sketch, "E859.filletArc", {"start": v(176.63, -219.36) * mm, "mid": v(176.19, -218.3) * mm, "end": v(175.13, -217.86) * mm});
            skPoint(sketch, "E860.visualSharp", {"position": v(161.23, -233.26) * mm});
            skArc(sketch, "E860.filletArc", {"start": v(161.23, -231.76) * mm, "mid": v(161.67, -232.82) * mm, "end": v(162.73, -233.26) * mm});
            skPoint(sketch, "E861.visualSharp", {"position": v(176.63, -233.26) * mm});
            skArc(sketch, "E861.filletArc", {"start": v(175.13, -233.26) * mm, "mid": v(176.19, -232.82) * mm, "end": v(176.63, -231.76) * mm});
            skLineSegment(sketch, "E862.bottom", {"start": v(162.73, -198.86) * mm, "end": v(175.13, -198.86) * mm});
            skLineSegment(sketch, "E862.top", {"start": v(162.73, -214.26) * mm, "end": v(175.13, -214.26) * mm});
            skLineSegment(sketch, "E862.left", {"start": v(161.23, -200.36) * mm, "end": v(161.23, -212.76) * mm});
            skLineSegment(sketch, "E862.right", {"start": v(176.63, -200.36) * mm, "end": v(176.63, -212.76) * mm});
            skPoint(sketch, "E863.visualSharp", {"position": v(161.23, -198.86) * mm});
            skArc(sketch, "E863.filletArc", {"start": v(162.73, -198.86) * mm, "mid": v(161.67, -199.3) * mm, "end": v(161.23, -200.36) * mm});
            skPoint(sketch, "E864.visualSharp", {"position": v(176.63, -198.86) * mm});
            skArc(sketch, "E864.filletArc", {"start": v(176.63, -200.36) * mm, "mid": v(176.19, -199.3) * mm, "end": v(175.13, -198.86) * mm});
            skPoint(sketch, "E865.visualSharp", {"position": v(161.23, -214.26) * mm});
            skArc(sketch, "E865.filletArc", {"start": v(161.23, -212.76) * mm, "mid": v(161.67, -213.82) * mm, "end": v(162.73, -214.26) * mm});
            skPoint(sketch, "E866.visualSharp", {"position": v(176.63, -214.26) * mm});
            skArc(sketch, "E866.filletArc", {"start": v(175.13, -214.26) * mm, "mid": v(176.19, -213.82) * mm, "end": v(176.63, -212.76) * mm});
            skLineSegment(sketch, "E867.bottom", {"start": v(146.23, -141.86) * mm, "end": v(158.63, -141.86) * mm});
            skLineSegment(sketch, "E867.top", {"start": v(146.23, -157.26) * mm, "end": v(158.63, -157.26) * mm});
            skLineSegment(sketch, "E867.left", {"start": v(144.73, -143.36) * mm, "end": v(144.73, -155.76) * mm});
            skLineSegment(sketch, "E867.right", {"start": v(160.13, -143.36) * mm, "end": v(160.13, -155.76) * mm});
            skPoint(sketch, "E868.visualSharp", {"position": v(144.73, -141.86) * mm});
            skArc(sketch, "E868.filletArc", {"start": v(146.23, -141.86) * mm, "mid": v(145.17, -142.3) * mm, "end": v(144.73, -143.36) * mm});
            skPoint(sketch, "E869.visualSharp", {"position": v(160.13, -141.86) * mm});
            skArc(sketch, "E869.filletArc", {"start": v(160.13, -143.36) * mm, "mid": v(159.69, -142.3) * mm, "end": v(158.63, -141.86) * mm});
            skPoint(sketch, "E870.visualSharp", {"position": v(144.73, -157.26) * mm});
            skArc(sketch, "E870.filletArc", {"start": v(144.73, -155.76) * mm, "mid": v(145.17, -156.82) * mm, "end": v(146.23, -157.26) * mm});
            skPoint(sketch, "E871.visualSharp", {"position": v(160.13, -157.26) * mm});
            skArc(sketch, "E871.filletArc", {"start": v(158.63, -157.26) * mm, "mid": v(159.69, -156.82) * mm, "end": v(160.13, -155.76) * mm});
            skLineSegment(sketch, "E872.bottom", {"start": v(146.23, -122.86) * mm, "end": v(158.63, -122.86) * mm});
            skLineSegment(sketch, "E872.top", {"start": v(146.23, -138.26) * mm, "end": v(158.63, -138.26) * mm});
            skLineSegment(sketch, "E872.left", {"start": v(144.73, -124.36) * mm, "end": v(144.73, -136.76) * mm});
            skLineSegment(sketch, "E872.right", {"start": v(160.13, -124.36) * mm, "end": v(160.13, -136.76) * mm});
            skPoint(sketch, "E873.visualSharp", {"position": v(144.73, -122.86) * mm});
            skArc(sketch, "E873.filletArc", {"start": v(146.23, -122.86) * mm, "mid": v(145.17, -123.3) * mm, "end": v(144.73, -124.36) * mm});
            skPoint(sketch, "E874.visualSharp", {"position": v(160.13, -122.86) * mm});
            skArc(sketch, "E874.filletArc", {"start": v(160.13, -124.36) * mm, "mid": v(159.69, -123.3) * mm, "end": v(158.63, -122.86) * mm});
            skPoint(sketch, "E875.visualSharp", {"position": v(144.73, -138.26) * mm});
            skArc(sketch, "E875.filletArc", {"start": v(144.73, -136.76) * mm, "mid": v(145.17, -137.82) * mm, "end": v(146.23, -138.26) * mm});
            skPoint(sketch, "E876.visualSharp", {"position": v(160.13, -138.26) * mm});
            skArc(sketch, "E876.filletArc", {"start": v(158.63, -138.26) * mm, "mid": v(159.69, -137.82) * mm, "end": v(160.13, -136.76) * mm});
            skLineSegment(sketch, "E877.bottom", {"start": v(146.23, -179.86) * mm, "end": v(158.63, -179.86) * mm});
            skLineSegment(sketch, "E877.top", {"start": v(146.23, -195.26) * mm, "end": v(158.63, -195.26) * mm});
            skLineSegment(sketch, "E877.left", {"start": v(144.73, -181.36) * mm, "end": v(144.73, -193.76) * mm});
            skLineSegment(sketch, "E877.right", {"start": v(160.13, -181.36) * mm, "end": v(160.13, -193.76) * mm});
            skPoint(sketch, "E878.visualSharp", {"position": v(144.73, -179.86) * mm});
            skArc(sketch, "E878.filletArc", {"start": v(146.23, -179.86) * mm, "mid": v(145.17, -180.3) * mm, "end": v(144.73, -181.36) * mm});
            skPoint(sketch, "E879.visualSharp", {"position": v(160.13, -179.86) * mm});
            skArc(sketch, "E879.filletArc", {"start": v(160.13, -181.36) * mm, "mid": v(159.69, -180.3) * mm, "end": v(158.63, -179.86) * mm});
            skPoint(sketch, "E880.visualSharp", {"position": v(144.73, -195.26) * mm});
            skArc(sketch, "E880.filletArc", {"start": v(144.73, -193.76) * mm, "mid": v(145.17, -194.82) * mm, "end": v(146.23, -195.26) * mm});
            skPoint(sketch, "E881.visualSharp", {"position": v(160.13, -195.26) * mm});
            skArc(sketch, "E881.filletArc", {"start": v(158.63, -195.26) * mm, "mid": v(159.69, -194.82) * mm, "end": v(160.13, -193.76) * mm});
            skLineSegment(sketch, "E882.bottom", {"start": v(146.23, -160.86) * mm, "end": v(158.63, -160.86) * mm});
            skLineSegment(sketch, "E882.top", {"start": v(146.23, -176.26) * mm, "end": v(158.63, -176.26) * mm});
            skLineSegment(sketch, "E882.left", {"start": v(144.73, -162.36) * mm, "end": v(144.73, -174.76) * mm});
            skLineSegment(sketch, "E882.right", {"start": v(160.13, -162.36) * mm, "end": v(160.13, -174.76) * mm});
            skPoint(sketch, "E883.visualSharp", {"position": v(144.73, -160.86) * mm});
            skArc(sketch, "E883.filletArc", {"start": v(146.23, -160.86) * mm, "mid": v(145.17, -161.3) * mm, "end": v(144.73, -162.36) * mm});
            skPoint(sketch, "E884.visualSharp", {"position": v(160.13, -160.86) * mm});
            skArc(sketch, "E884.filletArc", {"start": v(160.13, -162.36) * mm, "mid": v(159.69, -161.3) * mm, "end": v(158.63, -160.86) * mm});
            skPoint(sketch, "E885.visualSharp", {"position": v(144.73, -176.26) * mm});
            skArc(sketch, "E885.filletArc", {"start": v(144.73, -174.76) * mm, "mid": v(145.17, -175.82) * mm, "end": v(146.23, -176.26) * mm});
            skPoint(sketch, "E886.visualSharp", {"position": v(160.13, -176.26) * mm});
            skArc(sketch, "E886.filletArc", {"start": v(158.63, -176.26) * mm, "mid": v(159.69, -175.82) * mm, "end": v(160.13, -174.76) * mm});
            skLineSegment(sketch, "E887.bottom", {"start": v(146.23, -217.86) * mm, "end": v(158.63, -217.86) * mm});
            skLineSegment(sketch, "E887.top", {"start": v(146.23, -233.26) * mm, "end": v(158.63, -233.26) * mm});
            skLineSegment(sketch, "E887.left", {"start": v(144.73, -219.36) * mm, "end": v(144.73, -231.76) * mm});
            skLineSegment(sketch, "E887.right", {"start": v(160.13, -219.36) * mm, "end": v(160.13, -231.76) * mm});
            skPoint(sketch, "E888.visualSharp", {"position": v(144.73, -217.86) * mm});
            skArc(sketch, "E888.filletArc", {"start": v(146.23, -217.86) * mm, "mid": v(145.17, -218.3) * mm, "end": v(144.73, -219.36) * mm});
            skPoint(sketch, "E889.visualSharp", {"position": v(160.13, -217.86) * mm});
            skArc(sketch, "E889.filletArc", {"start": v(160.13, -219.36) * mm, "mid": v(159.69, -218.3) * mm, "end": v(158.63, -217.86) * mm});
            skPoint(sketch, "E890.visualSharp", {"position": v(144.73, -233.26) * mm});
            skArc(sketch, "E890.filletArc", {"start": v(144.73, -231.76) * mm, "mid": v(145.17, -232.82) * mm, "end": v(146.23, -233.26) * mm});
            skPoint(sketch, "E891.visualSharp", {"position": v(160.13, -233.26) * mm});
            skArc(sketch, "E891.filletArc", {"start": v(158.63, -233.26) * mm, "mid": v(159.69, -232.82) * mm, "end": v(160.13, -231.76) * mm});
            skLineSegment(sketch, "E892.bottom", {"start": v(146.23, -198.86) * mm, "end": v(158.63, -198.86) * mm});
            skLineSegment(sketch, "E892.top", {"start": v(146.23, -214.26) * mm, "end": v(158.63, -214.26) * mm});
            skLineSegment(sketch, "E892.left", {"start": v(144.73, -200.36) * mm, "end": v(144.73, -212.76) * mm});
            skLineSegment(sketch, "E892.right", {"start": v(160.13, -200.36) * mm, "end": v(160.13, -212.76) * mm});
            skPoint(sketch, "E893.visualSharp", {"position": v(144.73, -198.86) * mm});
            skArc(sketch, "E893.filletArc", {"start": v(146.23, -198.86) * mm, "mid": v(145.17, -199.3) * mm, "end": v(144.73, -200.36) * mm});
            skPoint(sketch, "E894.visualSharp", {"position": v(160.13, -198.86) * mm});
            skArc(sketch, "E894.filletArc", {"start": v(160.13, -200.36) * mm, "mid": v(159.69, -199.3) * mm, "end": v(158.63, -198.86) * mm});
            skPoint(sketch, "E895.visualSharp", {"position": v(144.73, -214.26) * mm});
            skArc(sketch, "E895.filletArc", {"start": v(144.73, -212.76) * mm, "mid": v(145.17, -213.82) * mm, "end": v(146.23, -214.26) * mm});
            skPoint(sketch, "E896.visualSharp", {"position": v(160.13, -214.26) * mm});
            skArc(sketch, "E896.filletArc", {"start": v(158.63, -214.26) * mm, "mid": v(159.69, -213.82) * mm, "end": v(160.13, -212.76) * mm});
            skLineSegment(sketch, "E897.bottom", {"start": v(96.73, -141.86) * mm, "end": v(109.13, -141.86) * mm});
            skLineSegment(sketch, "E897.top", {"start": v(96.73, -157.26) * mm, "end": v(109.13, -157.26) * mm});
            skLineSegment(sketch, "E897.left", {"start": v(95.23, -143.36) * mm, "end": v(95.23, -155.76) * mm});
            skLineSegment(sketch, "E897.right", {"start": v(110.63, -143.36) * mm, "end": v(110.63, -155.76) * mm});
            skPoint(sketch, "E898.visualSharp", {"position": v(95.23, -141.86) * mm});
            skArc(sketch, "E898.filletArc", {"start": v(96.73, -141.86) * mm, "mid": v(95.67, -142.3) * mm, "end": v(95.23, -143.36) * mm});
            skPoint(sketch, "E899.visualSharp", {"position": v(110.63, -141.86) * mm});
            skArc(sketch, "E899.filletArc", {"start": v(110.63, -143.36) * mm, "mid": v(110.19, -142.3) * mm, "end": v(109.13, -141.86) * mm});
            skPoint(sketch, "E900.visualSharp", {"position": v(95.23, -157.26) * mm});
            skArc(sketch, "E900.filletArc", {"start": v(95.23, -155.76) * mm, "mid": v(95.67, -156.82) * mm, "end": v(96.73, -157.26) * mm});
            skPoint(sketch, "E901.visualSharp", {"position": v(110.63, -157.26) * mm});
            skArc(sketch, "E901.filletArc", {"start": v(109.13, -157.26) * mm, "mid": v(110.19, -156.82) * mm, "end": v(110.63, -155.76) * mm});
            skLineSegment(sketch, "E902.bottom", {"start": v(96.73, -122.86) * mm, "end": v(109.13, -122.86) * mm});
            skLineSegment(sketch, "E902.top", {"start": v(96.73, -138.26) * mm, "end": v(109.13, -138.26) * mm});
            skLineSegment(sketch, "E902.left", {"start": v(95.23, -124.36) * mm, "end": v(95.23, -136.76) * mm});
            skLineSegment(sketch, "E902.right", {"start": v(110.63, -124.36) * mm, "end": v(110.63, -136.76) * mm});
            skPoint(sketch, "E903.visualSharp", {"position": v(95.23, -122.86) * mm});
            skArc(sketch, "E903.filletArc", {"start": v(96.73, -122.86) * mm, "mid": v(95.67, -123.3) * mm, "end": v(95.23, -124.36) * mm});
            skPoint(sketch, "E904.visualSharp", {"position": v(110.63, -122.86) * mm});
            skArc(sketch, "E904.filletArc", {"start": v(110.63, -124.36) * mm, "mid": v(110.19, -123.3) * mm, "end": v(109.13, -122.86) * mm});
            skPoint(sketch, "E905.visualSharp", {"position": v(95.23, -138.26) * mm});
            skArc(sketch, "E905.filletArc", {"start": v(95.23, -136.76) * mm, "mid": v(95.67, -137.82) * mm, "end": v(96.73, -138.26) * mm});
            skPoint(sketch, "E906.visualSharp", {"position": v(110.63, -138.26) * mm});
            skArc(sketch, "E906.filletArc", {"start": v(109.13, -138.26) * mm, "mid": v(110.19, -137.82) * mm, "end": v(110.63, -136.76) * mm});
            skLineSegment(sketch, "E907.bottom", {"start": v(96.73, -179.86) * mm, "end": v(109.13, -179.86) * mm});
            skLineSegment(sketch, "E907.top", {"start": v(96.73, -195.26) * mm, "end": v(109.13, -195.26) * mm});
            skLineSegment(sketch, "E907.left", {"start": v(95.23, -181.36) * mm, "end": v(95.23, -193.76) * mm});
            skLineSegment(sketch, "E907.right", {"start": v(110.63, -181.36) * mm, "end": v(110.63, -193.76) * mm});
            skPoint(sketch, "E908.visualSharp", {"position": v(95.23, -179.86) * mm});
            skArc(sketch, "E908.filletArc", {"start": v(96.73, -179.86) * mm, "mid": v(95.67, -180.3) * mm, "end": v(95.23, -181.36) * mm});
            skPoint(sketch, "E909.visualSharp", {"position": v(110.63, -179.86) * mm});
            skArc(sketch, "E909.filletArc", {"start": v(110.63, -181.36) * mm, "mid": v(110.19, -180.3) * mm, "end": v(109.13, -179.86) * mm});
            skPoint(sketch, "E910.visualSharp", {"position": v(95.23, -195.26) * mm});
            skArc(sketch, "E910.filletArc", {"start": v(95.23, -193.76) * mm, "mid": v(95.67, -194.82) * mm, "end": v(96.73, -195.26) * mm});
            skPoint(sketch, "E911.visualSharp", {"position": v(110.63, -195.26) * mm});
            skArc(sketch, "E911.filletArc", {"start": v(109.13, -195.26) * mm, "mid": v(110.19, -194.82) * mm, "end": v(110.63, -193.76) * mm});
            skLineSegment(sketch, "E912.bottom", {"start": v(96.73, -160.86) * mm, "end": v(109.13, -160.86) * mm});
            skLineSegment(sketch, "E912.top", {"start": v(96.73, -176.26) * mm, "end": v(109.13, -176.26) * mm});
            skLineSegment(sketch, "E912.left", {"start": v(95.23, -162.36) * mm, "end": v(95.23, -174.76) * mm});
            skLineSegment(sketch, "E912.right", {"start": v(110.63, -162.36) * mm, "end": v(110.63, -174.76) * mm});
            skPoint(sketch, "E913.visualSharp", {"position": v(95.23, -160.86) * mm});
            skArc(sketch, "E913.filletArc", {"start": v(96.73, -160.86) * mm, "mid": v(95.67, -161.3) * mm, "end": v(95.23, -162.36) * mm});
            skPoint(sketch, "E914.visualSharp", {"position": v(110.63, -160.86) * mm});
            skArc(sketch, "E914.filletArc", {"start": v(110.63, -162.36) * mm, "mid": v(110.19, -161.3) * mm, "end": v(109.13, -160.86) * mm});
            skPoint(sketch, "E915.visualSharp", {"position": v(95.23, -176.26) * mm});
            skArc(sketch, "E915.filletArc", {"start": v(95.23, -174.76) * mm, "mid": v(95.67, -175.82) * mm, "end": v(96.73, -176.26) * mm});
            skPoint(sketch, "E916.visualSharp", {"position": v(110.63, -176.26) * mm});
            skArc(sketch, "E916.filletArc", {"start": v(109.13, -176.26) * mm, "mid": v(110.19, -175.82) * mm, "end": v(110.63, -174.76) * mm});
            skLineSegment(sketch, "E917.bottom", {"start": v(96.73, -217.86) * mm, "end": v(109.13, -217.86) * mm});
            skLineSegment(sketch, "E917.top", {"start": v(96.73, -233.26) * mm, "end": v(109.13, -233.26) * mm});
            skLineSegment(sketch, "E917.left", {"start": v(95.23, -219.36) * mm, "end": v(95.23, -231.76) * mm});
            skLineSegment(sketch, "E917.right", {"start": v(110.63, -219.36) * mm, "end": v(110.63, -231.76) * mm});
            skPoint(sketch, "E918.visualSharp", {"position": v(95.23, -217.86) * mm});
            skArc(sketch, "E918.filletArc", {"start": v(96.73, -217.86) * mm, "mid": v(95.67, -218.3) * mm, "end": v(95.23, -219.36) * mm});
            skPoint(sketch, "E919.visualSharp", {"position": v(110.63, -217.86) * mm});
            skArc(sketch, "E919.filletArc", {"start": v(110.63, -219.36) * mm, "mid": v(110.19, -218.3) * mm, "end": v(109.13, -217.86) * mm});
            skPoint(sketch, "E920.visualSharp", {"position": v(95.23, -233.26) * mm});
            skArc(sketch, "E920.filletArc", {"start": v(95.23, -231.76) * mm, "mid": v(95.67, -232.82) * mm, "end": v(96.73, -233.26) * mm});
            skPoint(sketch, "E921.visualSharp", {"position": v(110.63, -233.26) * mm});
            skArc(sketch, "E921.filletArc", {"start": v(109.13, -233.26) * mm, "mid": v(110.19, -232.82) * mm, "end": v(110.63, -231.76) * mm});
            skLineSegment(sketch, "E922.bottom", {"start": v(96.73, -198.86) * mm, "end": v(109.13, -198.86) * mm});
            skLineSegment(sketch, "E922.top", {"start": v(96.73, -214.26) * mm, "end": v(109.13, -214.26) * mm});
            skLineSegment(sketch, "E922.left", {"start": v(95.23, -200.36) * mm, "end": v(95.23, -212.76) * mm});
            skLineSegment(sketch, "E922.right", {"start": v(110.63, -200.36) * mm, "end": v(110.63, -212.76) * mm});
            skPoint(sketch, "E923.visualSharp", {"position": v(95.23, -198.86) * mm});
            skArc(sketch, "E923.filletArc", {"start": v(96.73, -198.86) * mm, "mid": v(95.67, -199.3) * mm, "end": v(95.23, -200.36) * mm});
            skPoint(sketch, "E924.visualSharp", {"position": v(110.63, -198.86) * mm});
            skArc(sketch, "E924.filletArc", {"start": v(110.63, -200.36) * mm, "mid": v(110.19, -199.3) * mm, "end": v(109.13, -198.86) * mm});
            skPoint(sketch, "E925.visualSharp", {"position": v(95.23, -214.26) * mm});
            skArc(sketch, "E925.filletArc", {"start": v(95.23, -212.76) * mm, "mid": v(95.67, -213.82) * mm, "end": v(96.73, -214.26) * mm});
            skPoint(sketch, "E926.visualSharp", {"position": v(110.63, -214.26) * mm});
            skArc(sketch, "E926.filletArc", {"start": v(109.13, -214.26) * mm, "mid": v(110.19, -213.82) * mm, "end": v(110.63, -212.76) * mm});
            skLineSegment(sketch, "E927.bottom", {"start": v(129.73, -141.86) * mm, "end": v(142.13, -141.86) * mm});
            skLineSegment(sketch, "E927.top", {"start": v(129.73, -157.26) * mm, "end": v(142.13, -157.26) * mm});
            skLineSegment(sketch, "E927.left", {"start": v(128.23, -143.36) * mm, "end": v(128.23, -155.76) * mm});
            skLineSegment(sketch, "E927.right", {"start": v(143.63, -143.36) * mm, "end": v(143.63, -155.76) * mm});
            skPoint(sketch, "E928.visualSharp", {"position": v(128.23, -141.86) * mm});
            skArc(sketch, "E928.filletArc", {"start": v(129.73, -141.86) * mm, "mid": v(128.67, -142.3) * mm, "end": v(128.23, -143.36) * mm});
            skPoint(sketch, "E929.visualSharp", {"position": v(143.63, -141.86) * mm});
            skArc(sketch, "E929.filletArc", {"start": v(143.63, -143.36) * mm, "mid": v(143.19, -142.3) * mm, "end": v(142.13, -141.86) * mm});
            skPoint(sketch, "E930.visualSharp", {"position": v(128.23, -157.26) * mm});
            skArc(sketch, "E930.filletArc", {"start": v(128.23, -155.76) * mm, "mid": v(128.67, -156.82) * mm, "end": v(129.73, -157.26) * mm});
            skPoint(sketch, "E931.visualSharp", {"position": v(143.63, -157.26) * mm});
            skArc(sketch, "E931.filletArc", {"start": v(142.13, -157.26) * mm, "mid": v(143.19, -156.82) * mm, "end": v(143.63, -155.76) * mm});
            skLineSegment(sketch, "E932.bottom", {"start": v(129.73, -122.86) * mm, "end": v(142.13, -122.86) * mm});
            skLineSegment(sketch, "E932.top", {"start": v(129.73, -138.26) * mm, "end": v(142.13, -138.26) * mm});
            skLineSegment(sketch, "E932.left", {"start": v(128.23, -124.36) * mm, "end": v(128.23, -136.76) * mm});
            skLineSegment(sketch, "E932.right", {"start": v(143.63, -124.36) * mm, "end": v(143.63, -136.76) * mm});
            skPoint(sketch, "E933.visualSharp", {"position": v(128.23, -122.86) * mm});
            skArc(sketch, "E933.filletArc", {"start": v(129.73, -122.86) * mm, "mid": v(128.67, -123.3) * mm, "end": v(128.23, -124.36) * mm});
            skPoint(sketch, "E934.visualSharp", {"position": v(143.63, -122.86) * mm});
            skArc(sketch, "E934.filletArc", {"start": v(143.63, -124.36) * mm, "mid": v(143.19, -123.3) * mm, "end": v(142.13, -122.86) * mm});
            skPoint(sketch, "E935.visualSharp", {"position": v(128.23, -138.26) * mm});
            skArc(sketch, "E935.filletArc", {"start": v(128.23, -136.76) * mm, "mid": v(128.67, -137.82) * mm, "end": v(129.73, -138.26) * mm});
            skPoint(sketch, "E936.visualSharp", {"position": v(143.63, -138.26) * mm});
            skArc(sketch, "E936.filletArc", {"start": v(142.13, -138.26) * mm, "mid": v(143.19, -137.82) * mm, "end": v(143.63, -136.76) * mm});
            skLineSegment(sketch, "E937.bottom", {"start": v(129.73, -179.86) * mm, "end": v(142.13, -179.86) * mm});
            skLineSegment(sketch, "E937.top", {"start": v(129.73, -195.26) * mm, "end": v(142.13, -195.26) * mm});
            skLineSegment(sketch, "E937.left", {"start": v(128.23, -181.36) * mm, "end": v(128.23, -193.76) * mm});
            skLineSegment(sketch, "E937.right", {"start": v(143.63, -181.36) * mm, "end": v(143.63, -193.76) * mm});
            skPoint(sketch, "E938.visualSharp", {"position": v(128.23, -179.86) * mm});
            skArc(sketch, "E938.filletArc", {"start": v(129.73, -179.86) * mm, "mid": v(128.67, -180.3) * mm, "end": v(128.23, -181.36) * mm});
            skPoint(sketch, "E939.visualSharp", {"position": v(143.63, -179.86) * mm});
            skArc(sketch, "E939.filletArc", {"start": v(143.63, -181.36) * mm, "mid": v(143.19, -180.3) * mm, "end": v(142.13, -179.86) * mm});
            skPoint(sketch, "E940.visualSharp", {"position": v(128.23, -195.26) * mm});
            skArc(sketch, "E940.filletArc", {"start": v(128.23, -193.76) * mm, "mid": v(128.67, -194.82) * mm, "end": v(129.73, -195.26) * mm});
            skPoint(sketch, "E941.visualSharp", {"position": v(143.63, -195.26) * mm});
            skArc(sketch, "E941.filletArc", {"start": v(142.13, -195.26) * mm, "mid": v(143.19, -194.82) * mm, "end": v(143.63, -193.76) * mm});
            skLineSegment(sketch, "E942.bottom", {"start": v(129.73, -160.86) * mm, "end": v(142.13, -160.86) * mm});
            skLineSegment(sketch, "E942.top", {"start": v(129.73, -176.26) * mm, "end": v(142.13, -176.26) * mm});
            skLineSegment(sketch, "E942.left", {"start": v(128.23, -162.36) * mm, "end": v(128.23, -174.76) * mm});
            skLineSegment(sketch, "E942.right", {"start": v(143.63, -162.36) * mm, "end": v(143.63, -174.76) * mm});
            skPoint(sketch, "E943.visualSharp", {"position": v(128.23, -160.86) * mm});
            skArc(sketch, "E943.filletArc", {"start": v(129.73, -160.86) * mm, "mid": v(128.67, -161.3) * mm, "end": v(128.23, -162.36) * mm});
            skPoint(sketch, "E944.visualSharp", {"position": v(143.63, -160.86) * mm});
            skArc(sketch, "E944.filletArc", {"start": v(143.63, -162.36) * mm, "mid": v(143.19, -161.3) * mm, "end": v(142.13, -160.86) * mm});
            skPoint(sketch, "E945.visualSharp", {"position": v(128.23, -176.26) * mm});
            skArc(sketch, "E945.filletArc", {"start": v(128.23, -174.76) * mm, "mid": v(128.67, -175.82) * mm, "end": v(129.73, -176.26) * mm});
            skPoint(sketch, "E946.visualSharp", {"position": v(143.63, -176.26) * mm});
            skArc(sketch, "E946.filletArc", {"start": v(142.13, -176.26) * mm, "mid": v(143.19, -175.82) * mm, "end": v(143.63, -174.76) * mm});
            skLineSegment(sketch, "E947.bottom", {"start": v(129.73, -217.86) * mm, "end": v(142.13, -217.86) * mm});
            skLineSegment(sketch, "E947.top", {"start": v(129.73, -233.26) * mm, "end": v(142.13, -233.26) * mm});
            skLineSegment(sketch, "E947.left", {"start": v(128.23, -219.36) * mm, "end": v(128.23, -231.76) * mm});
            skLineSegment(sketch, "E947.right", {"start": v(143.63, -219.36) * mm, "end": v(143.63, -231.76) * mm});
            skPoint(sketch, "E948.visualSharp", {"position": v(128.23, -217.86) * mm});
            skArc(sketch, "E948.filletArc", {"start": v(129.73, -217.86) * mm, "mid": v(128.67, -218.3) * mm, "end": v(128.23, -219.36) * mm});
            skPoint(sketch, "E949.visualSharp", {"position": v(143.63, -217.86) * mm});
            skArc(sketch, "E949.filletArc", {"start": v(143.63, -219.36) * mm, "mid": v(143.19, -218.3) * mm, "end": v(142.13, -217.86) * mm});
            skPoint(sketch, "E950.visualSharp", {"position": v(128.23, -233.26) * mm});
            skArc(sketch, "E950.filletArc", {"start": v(128.23, -231.76) * mm, "mid": v(128.67, -232.82) * mm, "end": v(129.73, -233.26) * mm});
            skPoint(sketch, "E951.visualSharp", {"position": v(143.63, -233.26) * mm});
            skArc(sketch, "E951.filletArc", {"start": v(142.13, -233.26) * mm, "mid": v(143.19, -232.82) * mm, "end": v(143.63, -231.76) * mm});
            skLineSegment(sketch, "E952.bottom", {"start": v(129.73, -198.86) * mm, "end": v(142.13, -198.86) * mm});
            skLineSegment(sketch, "E952.top", {"start": v(129.73, -214.26) * mm, "end": v(142.13, -214.26) * mm});
            skLineSegment(sketch, "E952.left", {"start": v(128.23, -200.36) * mm, "end": v(128.23, -212.76) * mm});
            skLineSegment(sketch, "E952.right", {"start": v(143.63, -200.36) * mm, "end": v(143.63, -212.76) * mm});
            skPoint(sketch, "E953.visualSharp", {"position": v(128.23, -198.86) * mm});
            skArc(sketch, "E953.filletArc", {"start": v(129.73, -198.86) * mm, "mid": v(128.67, -199.3) * mm, "end": v(128.23, -200.36) * mm});
            skPoint(sketch, "E954.visualSharp", {"position": v(143.63, -198.86) * mm});
            skArc(sketch, "E954.filletArc", {"start": v(143.63, -200.36) * mm, "mid": v(143.19, -199.3) * mm, "end": v(142.13, -198.86) * mm});
            skPoint(sketch, "E955.visualSharp", {"position": v(128.23, -214.26) * mm});
            skArc(sketch, "E955.filletArc", {"start": v(128.23, -212.76) * mm, "mid": v(128.67, -213.82) * mm, "end": v(129.73, -214.26) * mm});
            skPoint(sketch, "E956.visualSharp", {"position": v(143.63, -214.26) * mm});
            skArc(sketch, "E956.filletArc", {"start": v(142.13, -214.26) * mm, "mid": v(143.19, -213.82) * mm, "end": v(143.63, -212.76) * mm});
            skLineSegment(sketch, "E957.bottom", {"start": v(113.23, -141.86) * mm, "end": v(125.63, -141.86) * mm});
            skLineSegment(sketch, "E957.top", {"start": v(113.23, -157.26) * mm, "end": v(125.63, -157.26) * mm});
            skLineSegment(sketch, "E957.left", {"start": v(111.73, -143.36) * mm, "end": v(111.73, -155.76) * mm});
            skLineSegment(sketch, "E957.right", {"start": v(127.13, -143.36) * mm, "end": v(127.13, -155.76) * mm});
            skPoint(sketch, "E958.visualSharp", {"position": v(111.73, -141.86) * mm});
            skArc(sketch, "E958.filletArc", {"start": v(113.23, -141.86) * mm, "mid": v(112.17, -142.3) * mm, "end": v(111.73, -143.36) * mm});
            skPoint(sketch, "E959.visualSharp", {"position": v(127.13, -141.86) * mm});
            skArc(sketch, "E959.filletArc", {"start": v(127.13, -143.36) * mm, "mid": v(126.69, -142.3) * mm, "end": v(125.63, -141.86) * mm});
            skPoint(sketch, "E960.visualSharp", {"position": v(111.73, -157.26) * mm});
            skArc(sketch, "E960.filletArc", {"start": v(111.73, -155.76) * mm, "mid": v(112.17, -156.82) * mm, "end": v(113.23, -157.26) * mm});
            skPoint(sketch, "E961.visualSharp", {"position": v(127.13, -157.26) * mm});
            skArc(sketch, "E961.filletArc", {"start": v(125.63, -157.26) * mm, "mid": v(126.69, -156.82) * mm, "end": v(127.13, -155.76) * mm});
            skLineSegment(sketch, "E962.bottom", {"start": v(113.23, -122.86) * mm, "end": v(125.63, -122.86) * mm});
            skLineSegment(sketch, "E962.top", {"start": v(113.23, -138.26) * mm, "end": v(125.63, -138.26) * mm});
            skLineSegment(sketch, "E962.left", {"start": v(111.73, -124.36) * mm, "end": v(111.73, -136.76) * mm});
            skLineSegment(sketch, "E962.right", {"start": v(127.13, -124.36) * mm, "end": v(127.13, -136.76) * mm});
            skPoint(sketch, "E963.visualSharp", {"position": v(111.73, -122.86) * mm});
            skArc(sketch, "E963.filletArc", {"start": v(113.23, -122.86) * mm, "mid": v(112.17, -123.3) * mm, "end": v(111.73, -124.36) * mm});
            skPoint(sketch, "E964.visualSharp", {"position": v(127.13, -122.86) * mm});
            skArc(sketch, "E964.filletArc", {"start": v(127.13, -124.36) * mm, "mid": v(126.69, -123.3) * mm, "end": v(125.63, -122.86) * mm});
            skPoint(sketch, "E965.visualSharp", {"position": v(111.73, -138.26) * mm});
            skArc(sketch, "E965.filletArc", {"start": v(111.73, -136.76) * mm, "mid": v(112.17, -137.82) * mm, "end": v(113.23, -138.26) * mm});
            skPoint(sketch, "E966.visualSharp", {"position": v(127.13, -138.26) * mm});
            skArc(sketch, "E966.filletArc", {"start": v(125.63, -138.26) * mm, "mid": v(126.69, -137.82) * mm, "end": v(127.13, -136.76) * mm});
            skLineSegment(sketch, "E967.bottom", {"start": v(113.23, -179.86) * mm, "end": v(125.63, -179.86) * mm});
            skLineSegment(sketch, "E967.top", {"start": v(113.23, -195.26) * mm, "end": v(125.63, -195.26) * mm});
            skLineSegment(sketch, "E967.left", {"start": v(111.73, -181.36) * mm, "end": v(111.73, -193.76) * mm});
            skLineSegment(sketch, "E967.right", {"start": v(127.13, -181.36) * mm, "end": v(127.13, -193.76) * mm});
            skPoint(sketch, "E968.visualSharp", {"position": v(111.73, -179.86) * mm});
            skArc(sketch, "E968.filletArc", {"start": v(113.23, -179.86) * mm, "mid": v(112.17, -180.3) * mm, "end": v(111.73, -181.36) * mm});
            skPoint(sketch, "E969.visualSharp", {"position": v(127.13, -179.86) * mm});
            skArc(sketch, "E969.filletArc", {"start": v(127.13, -181.36) * mm, "mid": v(126.69, -180.3) * mm, "end": v(125.63, -179.86) * mm});
            skPoint(sketch, "E970.visualSharp", {"position": v(111.73, -195.26) * mm});
            skArc(sketch, "E970.filletArc", {"start": v(111.73, -193.76) * mm, "mid": v(112.17, -194.82) * mm, "end": v(113.23, -195.26) * mm});
            skPoint(sketch, "E971.visualSharp", {"position": v(127.13, -195.26) * mm});
            skArc(sketch, "E971.filletArc", {"start": v(125.63, -195.26) * mm, "mid": v(126.69, -194.82) * mm, "end": v(127.13, -193.76) * mm});
            skLineSegment(sketch, "E972.bottom", {"start": v(113.23, -160.86) * mm, "end": v(125.63, -160.86) * mm});
            skLineSegment(sketch, "E972.top", {"start": v(113.23, -176.26) * mm, "end": v(125.63, -176.26) * mm});
            skLineSegment(sketch, "E972.left", {"start": v(111.73, -162.36) * mm, "end": v(111.73, -174.76) * mm});
            skLineSegment(sketch, "E972.right", {"start": v(127.13, -162.36) * mm, "end": v(127.13, -174.76) * mm});
            skPoint(sketch, "E973.visualSharp", {"position": v(111.73, -160.86) * mm});
            skArc(sketch, "E973.filletArc", {"start": v(113.23, -160.86) * mm, "mid": v(112.17, -161.3) * mm, "end": v(111.73, -162.36) * mm});
            skPoint(sketch, "E974.visualSharp", {"position": v(127.13, -160.86) * mm});
            skArc(sketch, "E974.filletArc", {"start": v(127.13, -162.36) * mm, "mid": v(126.69, -161.3) * mm, "end": v(125.63, -160.86) * mm});
            skPoint(sketch, "E975.visualSharp", {"position": v(111.73, -176.26) * mm});
            skArc(sketch, "E975.filletArc", {"start": v(111.73, -174.76) * mm, "mid": v(112.17, -175.82) * mm, "end": v(113.23, -176.26) * mm});
            skPoint(sketch, "E976.visualSharp", {"position": v(127.13, -176.26) * mm});
            skArc(sketch, "E976.filletArc", {"start": v(125.63, -176.26) * mm, "mid": v(126.69, -175.82) * mm, "end": v(127.13, -174.76) * mm});
            skLineSegment(sketch, "E977.bottom", {"start": v(113.23, -217.86) * mm, "end": v(125.63, -217.86) * mm});
            skLineSegment(sketch, "E977.top", {"start": v(113.23, -233.26) * mm, "end": v(125.63, -233.26) * mm});
            skLineSegment(sketch, "E977.left", {"start": v(111.73, -219.36) * mm, "end": v(111.73, -231.76) * mm});
            skLineSegment(sketch, "E977.right", {"start": v(127.13, -219.36) * mm, "end": v(127.13, -231.76) * mm});
            skPoint(sketch, "E978.visualSharp", {"position": v(111.73, -217.86) * mm});
            skArc(sketch, "E978.filletArc", {"start": v(113.23, -217.86) * mm, "mid": v(112.17, -218.3) * mm, "end": v(111.73, -219.36) * mm});
            skPoint(sketch, "E979.visualSharp", {"position": v(127.13, -217.86) * mm});
            skArc(sketch, "E979.filletArc", {"start": v(127.13, -219.36) * mm, "mid": v(126.69, -218.3) * mm, "end": v(125.63, -217.86) * mm});
            skPoint(sketch, "E980.visualSharp", {"position": v(111.73, -233.26) * mm});
            skArc(sketch, "E980.filletArc", {"start": v(111.73, -231.76) * mm, "mid": v(112.17, -232.82) * mm, "end": v(113.23, -233.26) * mm});
            skPoint(sketch, "E981.visualSharp", {"position": v(127.13, -233.26) * mm});
            skArc(sketch, "E981.filletArc", {"start": v(125.63, -233.26) * mm, "mid": v(126.69, -232.82) * mm, "end": v(127.13, -231.76) * mm});
            skLineSegment(sketch, "E982.bottom", {"start": v(113.23, -198.86) * mm, "end": v(125.63, -198.86) * mm});
            skLineSegment(sketch, "E982.top", {"start": v(113.23, -214.26) * mm, "end": v(125.63, -214.26) * mm});
            skLineSegment(sketch, "E982.left", {"start": v(111.73, -200.36) * mm, "end": v(111.73, -212.76) * mm});
            skLineSegment(sketch, "E982.right", {"start": v(127.13, -200.36) * mm, "end": v(127.13, -212.76) * mm});
            skPoint(sketch, "E983.visualSharp", {"position": v(111.73, -198.86) * mm});
            skArc(sketch, "E983.filletArc", {"start": v(113.23, -198.86) * mm, "mid": v(112.17, -199.3) * mm, "end": v(111.73, -200.36) * mm});
            skPoint(sketch, "E984.visualSharp", {"position": v(127.13, -198.86) * mm});
            skArc(sketch, "E984.filletArc", {"start": v(127.13, -200.36) * mm, "mid": v(126.69, -199.3) * mm, "end": v(125.63, -198.86) * mm});
            skPoint(sketch, "E985.visualSharp", {"position": v(111.73, -214.26) * mm});
            skArc(sketch, "E985.filletArc", {"start": v(111.73, -212.76) * mm, "mid": v(112.17, -213.82) * mm, "end": v(113.23, -214.26) * mm});
            skPoint(sketch, "E986.visualSharp", {"position": v(127.13, -214.26) * mm});
            skArc(sketch, "E986.filletArc", {"start": v(125.63, -214.26) * mm, "mid": v(126.69, -213.82) * mm, "end": v(127.13, -212.76) * mm});
            skLineSegment(sketch, "E987.bottom", {"start": v(80.23, -141.86) * mm, "end": v(92.63, -141.86) * mm});
            skLineSegment(sketch, "E987.top", {"start": v(80.23, -157.26) * mm, "end": v(92.63, -157.26) * mm});
            skLineSegment(sketch, "E987.left", {"start": v(78.73, -143.36) * mm, "end": v(78.73, -155.76) * mm});
            skLineSegment(sketch, "E987.right", {"start": v(94.13, -143.36) * mm, "end": v(94.13, -155.76) * mm});
            skPoint(sketch, "E988.visualSharp", {"position": v(78.73, -141.86) * mm});
            skArc(sketch, "E988.filletArc", {"start": v(80.23, -141.86) * mm, "mid": v(79.17, -142.3) * mm, "end": v(78.73, -143.36) * mm});
            skPoint(sketch, "E989.visualSharp", {"position": v(94.13, -141.86) * mm});
            skArc(sketch, "E989.filletArc", {"start": v(94.13, -143.36) * mm, "mid": v(93.69, -142.3) * mm, "end": v(92.63, -141.86) * mm});
            skPoint(sketch, "E990.visualSharp", {"position": v(78.73, -157.26) * mm});
            skArc(sketch, "E990.filletArc", {"start": v(78.73, -155.76) * mm, "mid": v(79.17, -156.82) * mm, "end": v(80.23, -157.26) * mm});
            skPoint(sketch, "E991.visualSharp", {"position": v(94.13, -157.26) * mm});
            skArc(sketch, "E991.filletArc", {"start": v(92.63, -157.26) * mm, "mid": v(93.69, -156.82) * mm, "end": v(94.13, -155.76) * mm});
            skLineSegment(sketch, "E992.bottom", {"start": v(80.23, -122.86) * mm, "end": v(92.63, -122.86) * mm});
            skLineSegment(sketch, "E992.top", {"start": v(80.23, -138.26) * mm, "end": v(92.63, -138.26) * mm});
            skLineSegment(sketch, "E992.left", {"start": v(78.73, -124.36) * mm, "end": v(78.73, -136.76) * mm});
            skLineSegment(sketch, "E992.right", {"start": v(94.13, -124.36) * mm, "end": v(94.13, -136.76) * mm});
            skPoint(sketch, "E993.visualSharp", {"position": v(78.73, -122.86) * mm});
            skArc(sketch, "E993.filletArc", {"start": v(80.23, -122.86) * mm, "mid": v(79.17, -123.3) * mm, "end": v(78.73, -124.36) * mm});
            skPoint(sketch, "E994.visualSharp", {"position": v(94.13, -122.86) * mm});
            skArc(sketch, "E994.filletArc", {"start": v(94.13, -124.36) * mm, "mid": v(93.69, -123.3) * mm, "end": v(92.63, -122.86) * mm});
            skPoint(sketch, "E995.visualSharp", {"position": v(78.73, -138.26) * mm});
            skArc(sketch, "E995.filletArc", {"start": v(78.73, -136.76) * mm, "mid": v(79.17, -137.82) * mm, "end": v(80.23, -138.26) * mm});
            skPoint(sketch, "E996.visualSharp", {"position": v(94.13, -138.26) * mm});
            skArc(sketch, "E996.filletArc", {"start": v(92.63, -138.26) * mm, "mid": v(93.69, -137.82) * mm, "end": v(94.13, -136.76) * mm});
            skLineSegment(sketch, "E997.bottom", {"start": v(80.23, -179.86) * mm, "end": v(92.63, -179.86) * mm});
            skLineSegment(sketch, "E997.top", {"start": v(80.23, -195.26) * mm, "end": v(92.63, -195.26) * mm});
            skLineSegment(sketch, "E997.left", {"start": v(78.73, -181.36) * mm, "end": v(78.73, -193.76) * mm});
            skLineSegment(sketch, "E997.right", {"start": v(94.13, -181.36) * mm, "end": v(94.13, -193.76) * mm});
            skPoint(sketch, "E998.visualSharp", {"position": v(78.73, -179.86) * mm});
            skArc(sketch, "E998.filletArc", {"start": v(80.23, -179.86) * mm, "mid": v(79.17, -180.3) * mm, "end": v(78.73, -181.36) * mm});
            skPoint(sketch, "E999.visualSharp", {"position": v(94.13, -179.86) * mm});
            skArc(sketch, "E999.filletArc", {"start": v(94.13, -181.36) * mm, "mid": v(93.69, -180.3) * mm, "end": v(92.63, -179.86) * mm});
            skPoint(sketch, "E1000.visualSharp", {"position": v(78.73, -195.26) * mm});
            skArc(sketch, "E1000.filletArc", {"start": v(78.73, -193.76) * mm, "mid": v(79.17, -194.82) * mm, "end": v(80.23, -195.26) * mm});
            skPoint(sketch, "E1001.visualSharp", {"position": v(94.13, -195.26) * mm});
            skArc(sketch, "E1001.filletArc", {"start": v(92.63, -195.26) * mm, "mid": v(93.69, -194.82) * mm, "end": v(94.13, -193.76) * mm});
            skLineSegment(sketch, "E1002.bottom", {"start": v(80.23, -160.86) * mm, "end": v(92.63, -160.86) * mm});
            skLineSegment(sketch, "E1002.top", {"start": v(80.23, -176.26) * mm, "end": v(92.63, -176.26) * mm});
            skLineSegment(sketch, "E1002.left", {"start": v(78.73, -162.36) * mm, "end": v(78.73, -174.76) * mm});
            skLineSegment(sketch, "E1002.right", {"start": v(94.13, -162.36) * mm, "end": v(94.13, -174.76) * mm});
            skPoint(sketch, "E1003.visualSharp", {"position": v(78.73, -160.86) * mm});
            skArc(sketch, "E1003.filletArc", {"start": v(80.23, -160.86) * mm, "mid": v(79.17, -161.3) * mm, "end": v(78.73, -162.36) * mm});
            skPoint(sketch, "E1004.visualSharp", {"position": v(94.13, -160.86) * mm});
            skArc(sketch, "E1004.filletArc", {"start": v(94.13, -162.36) * mm, "mid": v(93.69, -161.3) * mm, "end": v(92.63, -160.86) * mm});
            skPoint(sketch, "E1005.visualSharp", {"position": v(78.73, -176.26) * mm});
            skArc(sketch, "E1005.filletArc", {"start": v(78.73, -174.76) * mm, "mid": v(79.17, -175.82) * mm, "end": v(80.23, -176.26) * mm});
            skPoint(sketch, "E1006.visualSharp", {"position": v(94.13, -176.26) * mm});
            skArc(sketch, "E1006.filletArc", {"start": v(92.63, -176.26) * mm, "mid": v(93.69, -175.82) * mm, "end": v(94.13, -174.76) * mm});
            skLineSegment(sketch, "E1007.bottom", {"start": v(80.23, -217.86) * mm, "end": v(92.63, -217.86) * mm});
            skLineSegment(sketch, "E1007.top", {"start": v(80.23, -233.26) * mm, "end": v(92.63, -233.26) * mm});
            skLineSegment(sketch, "E1007.left", {"start": v(78.73, -219.36) * mm, "end": v(78.73, -231.76) * mm});
            skLineSegment(sketch, "E1007.right", {"start": v(94.13, -219.36) * mm, "end": v(94.13, -231.76) * mm});
            skPoint(sketch, "E1008.visualSharp", {"position": v(78.73, -217.86) * mm});
            skArc(sketch, "E1008.filletArc", {"start": v(80.23, -217.86) * mm, "mid": v(79.17, -218.3) * mm, "end": v(78.73, -219.36) * mm});
            skPoint(sketch, "E1009.visualSharp", {"position": v(94.13, -217.86) * mm});
            skArc(sketch, "E1009.filletArc", {"start": v(94.13, -219.36) * mm, "mid": v(93.69, -218.3) * mm, "end": v(92.63, -217.86) * mm});
            skPoint(sketch, "E1010.visualSharp", {"position": v(78.73, -233.26) * mm});
            skArc(sketch, "E1010.filletArc", {"start": v(78.73, -231.76) * mm, "mid": v(79.17, -232.82) * mm, "end": v(80.23, -233.26) * mm});
            skPoint(sketch, "E1011.visualSharp", {"position": v(94.13, -233.26) * mm});
            skArc(sketch, "E1011.filletArc", {"start": v(92.63, -233.26) * mm, "mid": v(93.69, -232.82) * mm, "end": v(94.13, -231.76) * mm});
            skLineSegment(sketch, "E1012.bottom", {"start": v(80.23, -198.86) * mm, "end": v(92.63, -198.86) * mm});
            skLineSegment(sketch, "E1012.top", {"start": v(80.23, -214.26) * mm, "end": v(92.63, -214.26) * mm});
            skLineSegment(sketch, "E1012.left", {"start": v(78.73, -200.36) * mm, "end": v(78.73, -212.76) * mm});
            skLineSegment(sketch, "E1012.right", {"start": v(94.13, -200.36) * mm, "end": v(94.13, -212.76) * mm});
            skPoint(sketch, "E1013.visualSharp", {"position": v(78.73, -198.86) * mm});
            skArc(sketch, "E1013.filletArc", {"start": v(80.23, -198.86) * mm, "mid": v(79.17, -199.3) * mm, "end": v(78.73, -200.36) * mm});
            skPoint(sketch, "E1014.visualSharp", {"position": v(94.13, -198.86) * mm});
            skArc(sketch, "E1014.filletArc", {"start": v(94.13, -200.36) * mm, "mid": v(93.69, -199.3) * mm, "end": v(92.63, -198.86) * mm});
            skPoint(sketch, "E1015.visualSharp", {"position": v(78.73, -214.26) * mm});
            skArc(sketch, "E1015.filletArc", {"start": v(78.73, -212.76) * mm, "mid": v(79.17, -213.82) * mm, "end": v(80.23, -214.26) * mm});
            skPoint(sketch, "E1016.visualSharp", {"position": v(94.13, -214.26) * mm});
            skArc(sketch, "E1016.filletArc", {"start": v(92.63, -214.26) * mm, "mid": v(93.69, -213.82) * mm, "end": v(94.13, -212.76) * mm});
            skLineSegment(sketch, "E1017.bottom", {"start": v(63.73, -141.86) * mm, "end": v(76.13, -141.86) * mm});
            skLineSegment(sketch, "E1017.top", {"start": v(63.73, -157.26) * mm, "end": v(76.13, -157.26) * mm});
            skLineSegment(sketch, "E1017.left", {"start": v(62.23, -143.36) * mm, "end": v(62.23, -155.76) * mm});
            skLineSegment(sketch, "E1017.right", {"start": v(77.63, -143.36) * mm, "end": v(77.63, -155.76) * mm});
            skPoint(sketch, "E1018.visualSharp", {"position": v(62.23, -141.86) * mm});
            skArc(sketch, "E1018.filletArc", {"start": v(63.73, -141.86) * mm, "mid": v(62.67, -142.3) * mm, "end": v(62.23, -143.36) * mm});
            skPoint(sketch, "E1019.visualSharp", {"position": v(77.63, -141.86) * mm});
            skArc(sketch, "E1019.filletArc", {"start": v(77.63, -143.36) * mm, "mid": v(77.19, -142.3) * mm, "end": v(76.13, -141.86) * mm});
            skPoint(sketch, "E1020.visualSharp", {"position": v(62.23, -157.26) * mm});
            skArc(sketch, "E1020.filletArc", {"start": v(62.23, -155.76) * mm, "mid": v(62.67, -156.82) * mm, "end": v(63.73, -157.26) * mm});
            skPoint(sketch, "E1021.visualSharp", {"position": v(77.63, -157.26) * mm});
            skArc(sketch, "E1021.filletArc", {"start": v(76.13, -157.26) * mm, "mid": v(77.19, -156.82) * mm, "end": v(77.63, -155.76) * mm});
            skLineSegment(sketch, "E1022.bottom", {"start": v(63.73, -122.86) * mm, "end": v(76.13, -122.86) * mm});
            skLineSegment(sketch, "E1022.top", {"start": v(63.73, -138.26) * mm, "end": v(76.13, -138.26) * mm});
            skLineSegment(sketch, "E1022.left", {"start": v(62.23, -124.36) * mm, "end": v(62.23, -136.76) * mm});
            skLineSegment(sketch, "E1022.right", {"start": v(77.63, -124.36) * mm, "end": v(77.63, -136.76) * mm});
            skPoint(sketch, "E1023.visualSharp", {"position": v(62.23, -122.86) * mm});
            skArc(sketch, "E1023.filletArc", {"start": v(63.73, -122.86) * mm, "mid": v(62.67, -123.3) * mm, "end": v(62.23, -124.36) * mm});
            skPoint(sketch, "E1024.visualSharp", {"position": v(77.63, -122.86) * mm});
            skArc(sketch, "E1024.filletArc", {"start": v(77.63, -124.36) * mm, "mid": v(77.19, -123.3) * mm, "end": v(76.13, -122.86) * mm});
            skPoint(sketch, "E1025.visualSharp", {"position": v(62.23, -138.26) * mm});
            skArc(sketch, "E1025.filletArc", {"start": v(62.23, -136.76) * mm, "mid": v(62.67, -137.82) * mm, "end": v(63.73, -138.26) * mm});
            skPoint(sketch, "E1026.visualSharp", {"position": v(77.63, -138.26) * mm});
            skArc(sketch, "E1026.filletArc", {"start": v(76.13, -138.26) * mm, "mid": v(77.19, -137.82) * mm, "end": v(77.63, -136.76) * mm});
            skLineSegment(sketch, "E1027.bottom", {"start": v(63.73, -179.86) * mm, "end": v(76.13, -179.86) * mm});
            skLineSegment(sketch, "E1027.top", {"start": v(63.73, -195.26) * mm, "end": v(76.13, -195.26) * mm});
            skLineSegment(sketch, "E1027.left", {"start": v(62.23, -181.36) * mm, "end": v(62.23, -193.76) * mm});
            skLineSegment(sketch, "E1027.right", {"start": v(77.63, -181.36) * mm, "end": v(77.63, -193.76) * mm});
            skPoint(sketch, "E1028.visualSharp", {"position": v(62.23, -179.86) * mm});
            skArc(sketch, "E1028.filletArc", {"start": v(63.73, -179.86) * mm, "mid": v(62.67, -180.3) * mm, "end": v(62.23, -181.36) * mm});
            skPoint(sketch, "E1029.visualSharp", {"position": v(77.63, -179.86) * mm});
            skArc(sketch, "E1029.filletArc", {"start": v(77.63, -181.36) * mm, "mid": v(77.19, -180.3) * mm, "end": v(76.13, -179.86) * mm});
            skPoint(sketch, "E1030.visualSharp", {"position": v(62.23, -195.26) * mm});
            skArc(sketch, "E1030.filletArc", {"start": v(62.23, -193.76) * mm, "mid": v(62.67, -194.82) * mm, "end": v(63.73, -195.26) * mm});
            skPoint(sketch, "E1031.visualSharp", {"position": v(77.63, -195.26) * mm});
            skArc(sketch, "E1031.filletArc", {"start": v(76.13, -195.26) * mm, "mid": v(77.19, -194.82) * mm, "end": v(77.63, -193.76) * mm});
            skLineSegment(sketch, "E1032.bottom", {"start": v(63.73, -160.86) * mm, "end": v(76.13, -160.86) * mm});
            skLineSegment(sketch, "E1032.top", {"start": v(63.73, -176.26) * mm, "end": v(76.13, -176.26) * mm});
            skLineSegment(sketch, "E1032.left", {"start": v(62.23, -162.36) * mm, "end": v(62.23, -174.76) * mm});
            skLineSegment(sketch, "E1032.right", {"start": v(77.63, -162.36) * mm, "end": v(77.63, -174.76) * mm});
            skPoint(sketch, "E1033.visualSharp", {"position": v(62.23, -160.86) * mm});
            skArc(sketch, "E1033.filletArc", {"start": v(63.73, -160.86) * mm, "mid": v(62.67, -161.3) * mm, "end": v(62.23, -162.36) * mm});
            skPoint(sketch, "E1034.visualSharp", {"position": v(77.63, -160.86) * mm});
            skArc(sketch, "E1034.filletArc", {"start": v(77.63, -162.36) * mm, "mid": v(77.19, -161.3) * mm, "end": v(76.13, -160.86) * mm});
            skPoint(sketch, "E1035.visualSharp", {"position": v(62.23, -176.26) * mm});
            skArc(sketch, "E1035.filletArc", {"start": v(62.23, -174.76) * mm, "mid": v(62.67, -175.82) * mm, "end": v(63.73, -176.26) * mm});
            skPoint(sketch, "E1036.visualSharp", {"position": v(77.63, -176.26) * mm});
            skArc(sketch, "E1036.filletArc", {"start": v(76.13, -176.26) * mm, "mid": v(77.19, -175.82) * mm, "end": v(77.63, -174.76) * mm});
            skLineSegment(sketch, "E1037.bottom", {"start": v(63.73, -217.86) * mm, "end": v(76.13, -217.86) * mm});
            skLineSegment(sketch, "E1037.top", {"start": v(63.73, -233.26) * mm, "end": v(76.13, -233.26) * mm});
            skLineSegment(sketch, "E1037.left", {"start": v(62.23, -219.36) * mm, "end": v(62.23, -231.76) * mm});
            skLineSegment(sketch, "E1037.right", {"start": v(77.63, -219.36) * mm, "end": v(77.63, -231.76) * mm});
            skPoint(sketch, "E1038.visualSharp", {"position": v(62.23, -217.86) * mm});
            skArc(sketch, "E1038.filletArc", {"start": v(63.73, -217.86) * mm, "mid": v(62.67, -218.3) * mm, "end": v(62.23, -219.36) * mm});
            skPoint(sketch, "E1039.visualSharp", {"position": v(77.63, -217.86) * mm});
            skArc(sketch, "E1039.filletArc", {"start": v(77.63, -219.36) * mm, "mid": v(77.19, -218.3) * mm, "end": v(76.13, -217.86) * mm});
            skPoint(sketch, "E1040.visualSharp", {"position": v(62.23, -233.26) * mm});
            skArc(sketch, "E1040.filletArc", {"start": v(62.23, -231.76) * mm, "mid": v(62.67, -232.82) * mm, "end": v(63.73, -233.26) * mm});
            skPoint(sketch, "E1041.visualSharp", {"position": v(77.63, -233.26) * mm});
            skArc(sketch, "E1041.filletArc", {"start": v(76.13, -233.26) * mm, "mid": v(77.19, -232.82) * mm, "end": v(77.63, -231.76) * mm});
            skLineSegment(sketch, "E1042.bottom", {"start": v(63.73, -198.86) * mm, "end": v(76.13, -198.86) * mm});
            skLineSegment(sketch, "E1042.top", {"start": v(63.73, -214.26) * mm, "end": v(76.13, -214.26) * mm});
            skLineSegment(sketch, "E1042.left", {"start": v(62.23, -200.36) * mm, "end": v(62.23, -212.76) * mm});
            skLineSegment(sketch, "E1042.right", {"start": v(77.63, -200.36) * mm, "end": v(77.63, -212.76) * mm});
            skPoint(sketch, "E1043.visualSharp", {"position": v(62.23, -198.86) * mm});
            skArc(sketch, "E1043.filletArc", {"start": v(63.73, -198.86) * mm, "mid": v(62.67, -199.3) * mm, "end": v(62.23, -200.36) * mm});
            skPoint(sketch, "E1044.visualSharp", {"position": v(77.63, -198.86) * mm});
            skArc(sketch, "E1044.filletArc", {"start": v(77.63, -200.36) * mm, "mid": v(77.19, -199.3) * mm, "end": v(76.13, -198.86) * mm});
            skPoint(sketch, "E1045.visualSharp", {"position": v(62.23, -214.26) * mm});
            skArc(sketch, "E1045.filletArc", {"start": v(62.23, -212.76) * mm, "mid": v(62.67, -213.82) * mm, "end": v(63.73, -214.26) * mm});
            skPoint(sketch, "E1046.visualSharp", {"position": v(77.63, -214.26) * mm});
            skArc(sketch, "E1046.filletArc", {"start": v(76.13, -214.26) * mm, "mid": v(77.19, -213.82) * mm, "end": v(77.63, -212.76) * mm});
            skLineSegment(sketch, "E1047.bottom", {"start": v(47.23, -141.86) * mm, "end": v(59.63, -141.86) * mm});
            skLineSegment(sketch, "E1047.top", {"start": v(47.23, -157.26) * mm, "end": v(59.63, -157.26) * mm});
            skLineSegment(sketch, "E1047.left", {"start": v(45.73, -143.36) * mm, "end": v(45.73, -155.76) * mm});
            skLineSegment(sketch, "E1047.right", {"start": v(61.13, -143.36) * mm, "end": v(61.13, -155.76) * mm});
            skPoint(sketch, "E1048.visualSharp", {"position": v(45.73, -141.86) * mm});
            skArc(sketch, "E1048.filletArc", {"start": v(47.23, -141.86) * mm, "mid": v(46.17, -142.3) * mm, "end": v(45.73, -143.36) * mm});
            skPoint(sketch, "E1049.visualSharp", {"position": v(61.13, -141.86) * mm});
            skArc(sketch, "E1049.filletArc", {"start": v(61.13, -143.36) * mm, "mid": v(60.69, -142.3) * mm, "end": v(59.63, -141.86) * mm});
            skPoint(sketch, "E1050.visualSharp", {"position": v(45.73, -157.26) * mm});
            skArc(sketch, "E1050.filletArc", {"start": v(45.73, -155.76) * mm, "mid": v(46.17, -156.82) * mm, "end": v(47.23, -157.26) * mm});
            skPoint(sketch, "E1051.visualSharp", {"position": v(61.13, -157.26) * mm});
            skArc(sketch, "E1051.filletArc", {"start": v(59.63, -157.26) * mm, "mid": v(60.69, -156.82) * mm, "end": v(61.13, -155.76) * mm});
            skLineSegment(sketch, "E1052.bottom", {"start": v(47.23, -122.86) * mm, "end": v(59.63, -122.86) * mm});
            skLineSegment(sketch, "E1052.top", {"start": v(47.23, -138.26) * mm, "end": v(59.63, -138.26) * mm});
            skLineSegment(sketch, "E1052.left", {"start": v(45.73, -124.36) * mm, "end": v(45.73, -136.76) * mm});
            skLineSegment(sketch, "E1052.right", {"start": v(61.13, -124.36) * mm, "end": v(61.13, -136.76) * mm});
            skPoint(sketch, "E1053.visualSharp", {"position": v(45.73, -122.86) * mm});
            skArc(sketch, "E1053.filletArc", {"start": v(47.23, -122.86) * mm, "mid": v(46.17, -123.3) * mm, "end": v(45.73, -124.36) * mm});
            skPoint(sketch, "E1054.visualSharp", {"position": v(61.13, -122.86) * mm});
            skArc(sketch, "E1054.filletArc", {"start": v(61.13, -124.36) * mm, "mid": v(60.69, -123.3) * mm, "end": v(59.63, -122.86) * mm});
            skPoint(sketch, "E1055.visualSharp", {"position": v(45.73, -138.26) * mm});
            skArc(sketch, "E1055.filletArc", {"start": v(45.73, -136.76) * mm, "mid": v(46.17, -137.82) * mm, "end": v(47.23, -138.26) * mm});
            skPoint(sketch, "E1056.visualSharp", {"position": v(61.13, -138.26) * mm});
            skArc(sketch, "E1056.filletArc", {"start": v(59.63, -138.26) * mm, "mid": v(60.69, -137.82) * mm, "end": v(61.13, -136.76) * mm});
            skLineSegment(sketch, "E1057.bottom", {"start": v(47.23, -179.86) * mm, "end": v(59.63, -179.86) * mm});
            skLineSegment(sketch, "E1057.top", {"start": v(47.23, -195.26) * mm, "end": v(59.63, -195.26) * mm});
            skLineSegment(sketch, "E1057.left", {"start": v(45.73, -181.36) * mm, "end": v(45.73, -193.76) * mm});
            skLineSegment(sketch, "E1057.right", {"start": v(61.13, -181.36) * mm, "end": v(61.13, -193.76) * mm});
            skPoint(sketch, "E1058.visualSharp", {"position": v(45.73, -179.86) * mm});
            skArc(sketch, "E1058.filletArc", {"start": v(47.23, -179.86) * mm, "mid": v(46.17, -180.3) * mm, "end": v(45.73, -181.36) * mm});
            skPoint(sketch, "E1059.visualSharp", {"position": v(61.13, -179.86) * mm});
            skArc(sketch, "E1059.filletArc", {"start": v(61.13, -181.36) * mm, "mid": v(60.69, -180.3) * mm, "end": v(59.63, -179.86) * mm});
            skPoint(sketch, "E1060.visualSharp", {"position": v(45.73, -195.26) * mm});
            skArc(sketch, "E1060.filletArc", {"start": v(45.73, -193.76) * mm, "mid": v(46.17, -194.82) * mm, "end": v(47.23, -195.26) * mm});
            skPoint(sketch, "E1061.visualSharp", {"position": v(61.13, -195.26) * mm});
            skArc(sketch, "E1061.filletArc", {"start": v(59.63, -195.26) * mm, "mid": v(60.69, -194.82) * mm, "end": v(61.13, -193.76) * mm});
            skLineSegment(sketch, "E1062.bottom", {"start": v(47.23, -160.86) * mm, "end": v(59.63, -160.86) * mm});
            skLineSegment(sketch, "E1062.top", {"start": v(47.23, -176.26) * mm, "end": v(59.63, -176.26) * mm});
            skLineSegment(sketch, "E1062.left", {"start": v(45.73, -162.36) * mm, "end": v(45.73, -174.76) * mm});
            skLineSegment(sketch, "E1062.right", {"start": v(61.13, -162.36) * mm, "end": v(61.13, -174.76) * mm});
            skPoint(sketch, "E1063.visualSharp", {"position": v(45.73, -160.86) * mm});
            skArc(sketch, "E1063.filletArc", {"start": v(47.23, -160.86) * mm, "mid": v(46.17, -161.3) * mm, "end": v(45.73, -162.36) * mm});
            skPoint(sketch, "E1064.visualSharp", {"position": v(61.13, -160.86) * mm});
            skArc(sketch, "E1064.filletArc", {"start": v(61.13, -162.36) * mm, "mid": v(60.69, -161.3) * mm, "end": v(59.63, -160.86) * mm});
            skPoint(sketch, "E1065.visualSharp", {"position": v(45.73, -176.26) * mm});
            skArc(sketch, "E1065.filletArc", {"start": v(45.73, -174.76) * mm, "mid": v(46.17, -175.82) * mm, "end": v(47.23, -176.26) * mm});
            skPoint(sketch, "E1066.visualSharp", {"position": v(61.13, -176.26) * mm});
            skArc(sketch, "E1066.filletArc", {"start": v(59.63, -176.26) * mm, "mid": v(60.69, -175.82) * mm, "end": v(61.13, -174.76) * mm});
            skLineSegment(sketch, "E1067.bottom", {"start": v(47.23, -217.86) * mm, "end": v(59.63, -217.86) * mm});
            skLineSegment(sketch, "E1067.top", {"start": v(47.23, -233.26) * mm, "end": v(59.63, -233.26) * mm});
            skLineSegment(sketch, "E1067.left", {"start": v(45.73, -219.36) * mm, "end": v(45.73, -231.76) * mm});
            skLineSegment(sketch, "E1067.right", {"start": v(61.13, -219.36) * mm, "end": v(61.13, -231.76) * mm});
            skPoint(sketch, "E1068.visualSharp", {"position": v(45.73, -217.86) * mm});
            skArc(sketch, "E1068.filletArc", {"start": v(47.23, -217.86) * mm, "mid": v(46.17, -218.3) * mm, "end": v(45.73, -219.36) * mm});
            skPoint(sketch, "E1069.visualSharp", {"position": v(61.13, -217.86) * mm});
            skArc(sketch, "E1069.filletArc", {"start": v(61.13, -219.36) * mm, "mid": v(60.69, -218.3) * mm, "end": v(59.63, -217.86) * mm});
            skPoint(sketch, "E1070.visualSharp", {"position": v(45.73, -233.26) * mm});
            skArc(sketch, "E1070.filletArc", {"start": v(45.73, -231.76) * mm, "mid": v(46.17, -232.82) * mm, "end": v(47.23, -233.26) * mm});
            skPoint(sketch, "E1071.visualSharp", {"position": v(61.13, -233.26) * mm});
            skArc(sketch, "E1071.filletArc", {"start": v(59.63, -233.26) * mm, "mid": v(60.69, -232.82) * mm, "end": v(61.13, -231.76) * mm});
            skLineSegment(sketch, "E1072.bottom", {"start": v(47.23, -198.86) * mm, "end": v(59.63, -198.86) * mm});
            skLineSegment(sketch, "E1072.top", {"start": v(47.23, -214.26) * mm, "end": v(59.63, -214.26) * mm});
            skLineSegment(sketch, "E1072.left", {"start": v(45.73, -200.36) * mm, "end": v(45.73, -212.76) * mm});
            skLineSegment(sketch, "E1072.right", {"start": v(61.13, -200.36) * mm, "end": v(61.13, -212.76) * mm});
            skPoint(sketch, "E1073.visualSharp", {"position": v(45.73, -198.86) * mm});
            skArc(sketch, "E1073.filletArc", {"start": v(47.23, -198.86) * mm, "mid": v(46.17, -199.3) * mm, "end": v(45.73, -200.36) * mm});
            skPoint(sketch, "E1074.visualSharp", {"position": v(61.13, -198.86) * mm});
            skArc(sketch, "E1074.filletArc", {"start": v(61.13, -200.36) * mm, "mid": v(60.69, -199.3) * mm, "end": v(59.63, -198.86) * mm});
            skPoint(sketch, "E1075.visualSharp", {"position": v(45.73, -214.26) * mm});
            skArc(sketch, "E1075.filletArc", {"start": v(45.73, -212.76) * mm, "mid": v(46.17, -213.82) * mm, "end": v(47.23, -214.26) * mm});
            skPoint(sketch, "E1076.visualSharp", {"position": v(61.13, -214.26) * mm});
            skArc(sketch, "E1076.filletArc", {"start": v(59.63, -214.26) * mm, "mid": v(60.69, -213.82) * mm, "end": v(61.13, -212.76) * mm});
            skLineSegment(sketch, "E1077.bottom", {"start": v(30.73, -141.86) * mm, "end": v(43.13, -141.86) * mm});
            skLineSegment(sketch, "E1077.top", {"start": v(30.73, -157.26) * mm, "end": v(43.13, -157.26) * mm});
            skLineSegment(sketch, "E1077.left", {"start": v(29.23, -143.36) * mm, "end": v(29.23, -155.76) * mm});
            skLineSegment(sketch, "E1077.right", {"start": v(44.63, -143.36) * mm, "end": v(44.63, -155.76) * mm});
            skPoint(sketch, "E1078.visualSharp", {"position": v(29.23, -141.86) * mm});
            skArc(sketch, "E1078.filletArc", {"start": v(30.73, -141.86) * mm, "mid": v(29.67, -142.3) * mm, "end": v(29.23, -143.36) * mm});
            skPoint(sketch, "E1079.visualSharp", {"position": v(44.63, -141.86) * mm});
            skArc(sketch, "E1079.filletArc", {"start": v(44.63, -143.36) * mm, "mid": v(44.19, -142.3) * mm, "end": v(43.13, -141.86) * mm});
            skPoint(sketch, "E1080.visualSharp", {"position": v(29.23, -157.26) * mm});
            skArc(sketch, "E1080.filletArc", {"start": v(29.23, -155.76) * mm, "mid": v(29.67, -156.82) * mm, "end": v(30.73, -157.26) * mm});
            skPoint(sketch, "E1081.visualSharp", {"position": v(44.63, -157.26) * mm});
            skArc(sketch, "E1081.filletArc", {"start": v(43.13, -157.26) * mm, "mid": v(44.19, -156.82) * mm, "end": v(44.63, -155.76) * mm});
            skLineSegment(sketch, "E1082.bottom", {"start": v(30.73, -122.86) * mm, "end": v(43.13, -122.86) * mm});
            skLineSegment(sketch, "E1082.top", {"start": v(30.73, -138.26) * mm, "end": v(43.13, -138.26) * mm});
            skLineSegment(sketch, "E1082.left", {"start": v(29.23, -124.36) * mm, "end": v(29.23, -136.76) * mm});
            skLineSegment(sketch, "E1082.right", {"start": v(44.63, -124.36) * mm, "end": v(44.63, -136.76) * mm});
            skPoint(sketch, "E1083.visualSharp", {"position": v(29.23, -122.86) * mm});
            skArc(sketch, "E1083.filletArc", {"start": v(30.73, -122.86) * mm, "mid": v(29.67, -123.3) * mm, "end": v(29.23, -124.36) * mm});
            skPoint(sketch, "E1084.visualSharp", {"position": v(44.63, -122.86) * mm});
            skArc(sketch, "E1084.filletArc", {"start": v(44.63, -124.36) * mm, "mid": v(44.19, -123.3) * mm, "end": v(43.13, -122.86) * mm});
            skPoint(sketch, "E1085.visualSharp", {"position": v(29.23, -138.26) * mm});
            skArc(sketch, "E1085.filletArc", {"start": v(29.23, -136.76) * mm, "mid": v(29.67, -137.82) * mm, "end": v(30.73, -138.26) * mm});
            skPoint(sketch, "E1086.visualSharp", {"position": v(44.63, -138.26) * mm});
            skArc(sketch, "E1086.filletArc", {"start": v(43.13, -138.26) * mm, "mid": v(44.19, -137.82) * mm, "end": v(44.63, -136.76) * mm});
            skLineSegment(sketch, "E1087.bottom", {"start": v(30.73, -179.86) * mm, "end": v(43.13, -179.86) * mm});
            skLineSegment(sketch, "E1087.top", {"start": v(30.73, -195.26) * mm, "end": v(43.13, -195.26) * mm});
            skLineSegment(sketch, "E1087.left", {"start": v(29.23, -181.36) * mm, "end": v(29.23, -193.76) * mm});
            skLineSegment(sketch, "E1087.right", {"start": v(44.63, -181.36) * mm, "end": v(44.63, -193.76) * mm});
            skPoint(sketch, "E1088.visualSharp", {"position": v(29.23, -179.86) * mm});
            skArc(sketch, "E1088.filletArc", {"start": v(30.73, -179.86) * mm, "mid": v(29.67, -180.3) * mm, "end": v(29.23, -181.36) * mm});
            skPoint(sketch, "E1089.visualSharp", {"position": v(44.63, -179.86) * mm});
            skArc(sketch, "E1089.filletArc", {"start": v(44.63, -181.36) * mm, "mid": v(44.19, -180.3) * mm, "end": v(43.13, -179.86) * mm});
            skPoint(sketch, "E1090.visualSharp", {"position": v(29.23, -195.26) * mm});
            skArc(sketch, "E1090.filletArc", {"start": v(29.23, -193.76) * mm, "mid": v(29.67, -194.82) * mm, "end": v(30.73, -195.26) * mm});
            skPoint(sketch, "E1091.visualSharp", {"position": v(44.63, -195.26) * mm});
            skArc(sketch, "E1091.filletArc", {"start": v(43.13, -195.26) * mm, "mid": v(44.19, -194.82) * mm, "end": v(44.63, -193.76) * mm});
            skLineSegment(sketch, "E1092.bottom", {"start": v(30.73, -160.86) * mm, "end": v(43.13, -160.86) * mm});
            skLineSegment(sketch, "E1092.top", {"start": v(30.73, -176.26) * mm, "end": v(43.13, -176.26) * mm});
            skLineSegment(sketch, "E1092.left", {"start": v(29.23, -162.36) * mm, "end": v(29.23, -174.76) * mm});
            skLineSegment(sketch, "E1092.right", {"start": v(44.63, -162.36) * mm, "end": v(44.63, -174.76) * mm});
            skPoint(sketch, "E1093.visualSharp", {"position": v(29.23, -160.86) * mm});
            skArc(sketch, "E1093.filletArc", {"start": v(30.73, -160.86) * mm, "mid": v(29.67, -161.3) * mm, "end": v(29.23, -162.36) * mm});
            skPoint(sketch, "E1094.visualSharp", {"position": v(44.63, -160.86) * mm});
            skArc(sketch, "E1094.filletArc", {"start": v(44.63, -162.36) * mm, "mid": v(44.19, -161.3) * mm, "end": v(43.13, -160.86) * mm});
            skPoint(sketch, "E1095.visualSharp", {"position": v(29.23, -176.26) * mm});
            skArc(sketch, "E1095.filletArc", {"start": v(29.23, -174.76) * mm, "mid": v(29.67, -175.82) * mm, "end": v(30.73, -176.26) * mm});
            skPoint(sketch, "E1096.visualSharp", {"position": v(44.63, -176.26) * mm});
            skArc(sketch, "E1096.filletArc", {"start": v(43.13, -176.26) * mm, "mid": v(44.19, -175.82) * mm, "end": v(44.63, -174.76) * mm});
            skLineSegment(sketch, "E1097.bottom", {"start": v(30.73, -217.86) * mm, "end": v(43.13, -217.86) * mm});
            skLineSegment(sketch, "E1097.top", {"start": v(30.73, -233.26) * mm, "end": v(43.13, -233.26) * mm});
            skLineSegment(sketch, "E1097.left", {"start": v(29.23, -219.36) * mm, "end": v(29.23, -231.76) * mm});
            skLineSegment(sketch, "E1097.right", {"start": v(44.63, -219.36) * mm, "end": v(44.63, -231.76) * mm});
            skPoint(sketch, "E1098.visualSharp", {"position": v(29.23, -217.86) * mm});
            skArc(sketch, "E1098.filletArc", {"start": v(30.73, -217.86) * mm, "mid": v(29.67, -218.3) * mm, "end": v(29.23, -219.36) * mm});
            skPoint(sketch, "E1099.visualSharp", {"position": v(44.63, -217.86) * mm});
            skArc(sketch, "E1099.filletArc", {"start": v(44.63, -219.36) * mm, "mid": v(44.19, -218.3) * mm, "end": v(43.13, -217.86) * mm});
            skPoint(sketch, "E1100.visualSharp", {"position": v(29.23, -233.26) * mm});
            skArc(sketch, "E1100.filletArc", {"start": v(29.23, -231.76) * mm, "mid": v(29.67, -232.82) * mm, "end": v(30.73, -233.26) * mm});
            skPoint(sketch, "E1101.visualSharp", {"position": v(44.63, -233.26) * mm});
            skArc(sketch, "E1101.filletArc", {"start": v(43.13, -233.26) * mm, "mid": v(44.19, -232.82) * mm, "end": v(44.63, -231.76) * mm});
            skLineSegment(sketch, "E1102.bottom", {"start": v(30.73, -198.86) * mm, "end": v(43.13, -198.86) * mm});
            skLineSegment(sketch, "E1102.top", {"start": v(30.73, -214.26) * mm, "end": v(43.13, -214.26) * mm});
            skLineSegment(sketch, "E1102.left", {"start": v(29.23, -200.36) * mm, "end": v(29.23, -212.76) * mm});
            skLineSegment(sketch, "E1102.right", {"start": v(44.63, -200.36) * mm, "end": v(44.63, -212.76) * mm});
            skPoint(sketch, "E1103.visualSharp", {"position": v(29.23, -198.86) * mm});
            skArc(sketch, "E1103.filletArc", {"start": v(30.73, -198.86) * mm, "mid": v(29.67, -199.3) * mm, "end": v(29.23, -200.36) * mm});
            skPoint(sketch, "E1104.visualSharp", {"position": v(44.63, -198.86) * mm});
            skArc(sketch, "E1104.filletArc", {"start": v(44.63, -200.36) * mm, "mid": v(44.19, -199.3) * mm, "end": v(43.13, -198.86) * mm});
            skPoint(sketch, "E1105.visualSharp", {"position": v(29.23, -214.26) * mm});
            skArc(sketch, "E1105.filletArc", {"start": v(29.23, -212.76) * mm, "mid": v(29.67, -213.82) * mm, "end": v(30.73, -214.26) * mm});
            skPoint(sketch, "E1106.visualSharp", {"position": v(44.63, -214.26) * mm});
            skArc(sketch, "E1106.filletArc", {"start": v(43.13, -214.26) * mm, "mid": v(44.19, -213.82) * mm, "end": v(44.63, -212.76) * mm});
            skLineSegment(sketch, "E1107.bottom", {"start": v(14.23, -141.86) * mm, "end": v(26.63, -141.86) * mm});
            skLineSegment(sketch, "E1107.top", {"start": v(14.23, -157.26) * mm, "end": v(26.63, -157.26) * mm});
            skLineSegment(sketch, "E1107.left", {"start": v(12.73, -143.36) * mm, "end": v(12.73, -155.76) * mm});
            skLineSegment(sketch, "E1107.right", {"start": v(28.13, -143.36) * mm, "end": v(28.13, -155.76) * mm});
            skPoint(sketch, "E1108.visualSharp", {"position": v(12.73, -141.86) * mm});
            skArc(sketch, "E1108.filletArc", {"start": v(14.23, -141.86) * mm, "mid": v(13.17, -142.3) * mm, "end": v(12.73, -143.36) * mm});
            skPoint(sketch, "E1109.visualSharp", {"position": v(28.13, -141.86) * mm});
            skArc(sketch, "E1109.filletArc", {"start": v(28.13, -143.36) * mm, "mid": v(27.69, -142.3) * mm, "end": v(26.63, -141.86) * mm});
            skPoint(sketch, "E1110.visualSharp", {"position": v(12.73, -157.26) * mm});
            skArc(sketch, "E1110.filletArc", {"start": v(12.73, -155.76) * mm, "mid": v(13.17, -156.82) * mm, "end": v(14.23, -157.26) * mm});
            skPoint(sketch, "E1111.visualSharp", {"position": v(28.13, -157.26) * mm});
            skArc(sketch, "E1111.filletArc", {"start": v(26.63, -157.26) * mm, "mid": v(27.69, -156.82) * mm, "end": v(28.13, -155.76) * mm});
            skLineSegment(sketch, "E1112.bottom", {"start": v(14.23, -122.86) * mm, "end": v(26.63, -122.86) * mm});
            skLineSegment(sketch, "E1112.top", {"start": v(14.23, -138.26) * mm, "end": v(26.63, -138.26) * mm});
            skLineSegment(sketch, "E1112.left", {"start": v(12.73, -124.36) * mm, "end": v(12.73, -136.76) * mm});
            skLineSegment(sketch, "E1112.right", {"start": v(28.13, -124.36) * mm, "end": v(28.13, -136.76) * mm});
            skPoint(sketch, "E1113.visualSharp", {"position": v(12.73, -122.86) * mm});
            skArc(sketch, "E1113.filletArc", {"start": v(14.23, -122.86) * mm, "mid": v(13.17, -123.3) * mm, "end": v(12.73, -124.36) * mm});
            skPoint(sketch, "E1114.visualSharp", {"position": v(28.13, -122.86) * mm});
            skArc(sketch, "E1114.filletArc", {"start": v(28.13, -124.36) * mm, "mid": v(27.69, -123.3) * mm, "end": v(26.63, -122.86) * mm});
            skPoint(sketch, "E1115.visualSharp", {"position": v(12.73, -138.26) * mm});
            skArc(sketch, "E1115.filletArc", {"start": v(12.73, -136.76) * mm, "mid": v(13.17, -137.82) * mm, "end": v(14.23, -138.26) * mm});
            skPoint(sketch, "E1116.visualSharp", {"position": v(28.13, -138.26) * mm});
            skArc(sketch, "E1116.filletArc", {"start": v(26.63, -138.26) * mm, "mid": v(27.69, -137.82) * mm, "end": v(28.13, -136.76) * mm});
            skLineSegment(sketch, "E1117.bottom", {"start": v(14.23, -179.86) * mm, "end": v(26.63, -179.86) * mm});
            skLineSegment(sketch, "E1117.top", {"start": v(14.23, -195.26) * mm, "end": v(26.63, -195.26) * mm});
            skLineSegment(sketch, "E1117.left", {"start": v(12.73, -181.36) * mm, "end": v(12.73, -193.76) * mm});
            skLineSegment(sketch, "E1117.right", {"start": v(28.13, -181.36) * mm, "end": v(28.13, -193.76) * mm});
            skPoint(sketch, "E1118.visualSharp", {"position": v(12.73, -179.86) * mm});
            skArc(sketch, "E1118.filletArc", {"start": v(14.23, -179.86) * mm, "mid": v(13.17, -180.3) * mm, "end": v(12.73, -181.36) * mm});
            skPoint(sketch, "E1119.visualSharp", {"position": v(28.13, -179.86) * mm});
            skArc(sketch, "E1119.filletArc", {"start": v(28.13, -181.36) * mm, "mid": v(27.69, -180.3) * mm, "end": v(26.63, -179.86) * mm});
            skPoint(sketch, "E1120.visualSharp", {"position": v(12.73, -195.26) * mm});
            skArc(sketch, "E1120.filletArc", {"start": v(12.73, -193.76) * mm, "mid": v(13.17, -194.82) * mm, "end": v(14.23, -195.26) * mm});
            skPoint(sketch, "E1121.visualSharp", {"position": v(28.13, -195.26) * mm});
            skArc(sketch, "E1121.filletArc", {"start": v(26.63, -195.26) * mm, "mid": v(27.69, -194.82) * mm, "end": v(28.13, -193.76) * mm});
            skLineSegment(sketch, "E1122.bottom", {"start": v(14.23, -160.86) * mm, "end": v(26.63, -160.86) * mm});
            skLineSegment(sketch, "E1122.top", {"start": v(14.23, -176.26) * mm, "end": v(26.63, -176.26) * mm});
            skLineSegment(sketch, "E1122.left", {"start": v(12.73, -162.36) * mm, "end": v(12.73, -174.76) * mm});
            skLineSegment(sketch, "E1122.right", {"start": v(28.13, -162.36) * mm, "end": v(28.13, -174.76) * mm});
            skPoint(sketch, "E1123.visualSharp", {"position": v(12.73, -160.86) * mm});
            skArc(sketch, "E1123.filletArc", {"start": v(14.23, -160.86) * mm, "mid": v(13.17, -161.3) * mm, "end": v(12.73, -162.36) * mm});
            skPoint(sketch, "E1124.visualSharp", {"position": v(28.13, -160.86) * mm});
            skArc(sketch, "E1124.filletArc", {"start": v(28.13, -162.36) * mm, "mid": v(27.69, -161.3) * mm, "end": v(26.63, -160.86) * mm});
            skPoint(sketch, "E1125.visualSharp", {"position": v(12.73, -176.26) * mm});
            skArc(sketch, "E1125.filletArc", {"start": v(12.73, -174.76) * mm, "mid": v(13.17, -175.82) * mm, "end": v(14.23, -176.26) * mm});
            skPoint(sketch, "E1126.visualSharp", {"position": v(28.13, -176.26) * mm});
            skArc(sketch, "E1126.filletArc", {"start": v(26.63, -176.26) * mm, "mid": v(27.69, -175.82) * mm, "end": v(28.13, -174.76) * mm});
            skLineSegment(sketch, "E1127.bottom", {"start": v(14.23, -217.86) * mm, "end": v(26.63, -217.86) * mm});
            skLineSegment(sketch, "E1127.top", {"start": v(14.23, -233.26) * mm, "end": v(26.63, -233.26) * mm});
            skLineSegment(sketch, "E1127.left", {"start": v(12.73, -219.36) * mm, "end": v(12.73, -231.76) * mm});
            skLineSegment(sketch, "E1127.right", {"start": v(28.13, -219.36) * mm, "end": v(28.13, -231.76) * mm});
            skPoint(sketch, "E1128.visualSharp", {"position": v(12.73, -217.86) * mm});
            skArc(sketch, "E1128.filletArc", {"start": v(14.23, -217.86) * mm, "mid": v(13.17, -218.3) * mm, "end": v(12.73, -219.36) * mm});
            skPoint(sketch, "E1129.visualSharp", {"position": v(28.13, -217.86) * mm});
            skArc(sketch, "E1129.filletArc", {"start": v(28.13, -219.36) * mm, "mid": v(27.69, -218.3) * mm, "end": v(26.63, -217.86) * mm});
            skPoint(sketch, "E1130.visualSharp", {"position": v(12.73, -233.26) * mm});
            skArc(sketch, "E1130.filletArc", {"start": v(12.73, -231.76) * mm, "mid": v(13.17, -232.82) * mm, "end": v(14.23, -233.26) * mm});
            skPoint(sketch, "E1131.visualSharp", {"position": v(28.13, -233.26) * mm});
            skArc(sketch, "E1131.filletArc", {"start": v(26.63, -233.26) * mm, "mid": v(27.69, -232.82) * mm, "end": v(28.13, -231.76) * mm});
            skLineSegment(sketch, "E1132.bottom", {"start": v(14.23, -198.86) * mm, "end": v(26.63, -198.86) * mm});
            skLineSegment(sketch, "E1132.top", {"start": v(14.23, -214.26) * mm, "end": v(26.63, -214.26) * mm});
            skLineSegment(sketch, "E1132.left", {"start": v(12.73, -200.36) * mm, "end": v(12.73, -212.76) * mm});
            skLineSegment(sketch, "E1132.right", {"start": v(28.13, -200.36) * mm, "end": v(28.13, -212.76) * mm});
            skPoint(sketch, "E1133.visualSharp", {"position": v(12.73, -198.86) * mm});
            skArc(sketch, "E1133.filletArc", {"start": v(14.23, -198.86) * mm, "mid": v(13.17, -199.3) * mm, "end": v(12.73, -200.36) * mm});
            skPoint(sketch, "E1134.visualSharp", {"position": v(28.13, -198.86) * mm});
            skArc(sketch, "E1134.filletArc", {"start": v(28.13, -200.36) * mm, "mid": v(27.69, -199.3) * mm, "end": v(26.63, -198.86) * mm});
            skPoint(sketch, "E1135.visualSharp", {"position": v(12.73, -214.26) * mm});
            skArc(sketch, "E1135.filletArc", {"start": v(12.73, -212.76) * mm, "mid": v(13.17, -213.82) * mm, "end": v(14.23, -214.26) * mm});
            skPoint(sketch, "E1136.visualSharp", {"position": v(28.13, -214.26) * mm});
            skArc(sketch, "E1136.filletArc", {"start": v(26.63, -214.26) * mm, "mid": v(27.69, -213.82) * mm, "end": v(28.13, -212.76) * mm});
            skLineSegment(sketch, "E1137.bottom", {"start": v(-2.27, -141.86) * mm, "end": v(10.13, -141.86) * mm});
            skLineSegment(sketch, "E1137.top", {"start": v(-2.27, -157.26) * mm, "end": v(10.13, -157.26) * mm});
            skLineSegment(sketch, "E1137.left", {"start": v(-3.77, -143.36) * mm, "end": v(-3.77, -155.76) * mm});
            skLineSegment(sketch, "E1137.right", {"start": v(11.63, -143.36) * mm, "end": v(11.63, -155.76) * mm});
            skPoint(sketch, "E1138.visualSharp", {"position": v(-3.77, -141.86) * mm});
            skArc(sketch, "E1138.filletArc", {"start": v(-2.27, -141.86) * mm, "mid": v(-3.33, -142.3) * mm, "end": v(-3.77, -143.36) * mm});
            skPoint(sketch, "E1139.visualSharp", {"position": v(11.63, -141.86) * mm});
            skArc(sketch, "E1139.filletArc", {"start": v(11.63, -143.36) * mm, "mid": v(11.19, -142.3) * mm, "end": v(10.13, -141.86) * mm});
            skPoint(sketch, "E1140.visualSharp", {"position": v(-3.77, -157.26) * mm});
            skArc(sketch, "E1140.filletArc", {"start": v(-3.77, -155.76) * mm, "mid": v(-3.33, -156.82) * mm, "end": v(-2.27, -157.26) * mm});
            skPoint(sketch, "E1141.visualSharp", {"position": v(11.63, -157.26) * mm});
            skArc(sketch, "E1141.filletArc", {"start": v(10.13, -157.26) * mm, "mid": v(11.19, -156.82) * mm, "end": v(11.63, -155.76) * mm});
            skLineSegment(sketch, "E1142.bottom", {"start": v(-2.27, -122.86) * mm, "end": v(10.13, -122.86) * mm});
            skLineSegment(sketch, "E1142.top", {"start": v(-2.27, -138.26) * mm, "end": v(10.13, -138.26) * mm});
            skLineSegment(sketch, "E1142.left", {"start": v(-3.77, -124.36) * mm, "end": v(-3.77, -136.76) * mm});
            skLineSegment(sketch, "E1142.right", {"start": v(11.63, -124.36) * mm, "end": v(11.63, -136.76) * mm});
            skPoint(sketch, "E1143.visualSharp", {"position": v(-3.77, -122.86) * mm});
            skArc(sketch, "E1143.filletArc", {"start": v(-2.27, -122.86) * mm, "mid": v(-3.33, -123.3) * mm, "end": v(-3.77, -124.36) * mm});
            skPoint(sketch, "E1144.visualSharp", {"position": v(11.63, -122.86) * mm});
            skArc(sketch, "E1144.filletArc", {"start": v(11.63, -124.36) * mm, "mid": v(11.19, -123.3) * mm, "end": v(10.13, -122.86) * mm});
            skPoint(sketch, "E1145.visualSharp", {"position": v(-3.77, -138.26) * mm});
            skArc(sketch, "E1145.filletArc", {"start": v(-3.77, -136.76) * mm, "mid": v(-3.33, -137.82) * mm, "end": v(-2.27, -138.26) * mm});
            skPoint(sketch, "E1146.visualSharp", {"position": v(11.63, -138.26) * mm});
            skArc(sketch, "E1146.filletArc", {"start": v(10.13, -138.26) * mm, "mid": v(11.19, -137.82) * mm, "end": v(11.63, -136.76) * mm});
            skLineSegment(sketch, "E1147.bottom", {"start": v(-2.27, -179.86) * mm, "end": v(10.13, -179.86) * mm});
            skLineSegment(sketch, "E1147.top", {"start": v(-2.27, -195.26) * mm, "end": v(10.13, -195.26) * mm});
            skLineSegment(sketch, "E1147.left", {"start": v(-3.77, -181.36) * mm, "end": v(-3.77, -193.76) * mm});
            skLineSegment(sketch, "E1147.right", {"start": v(11.63, -181.36) * mm, "end": v(11.63, -193.76) * mm});
            skPoint(sketch, "E1148.visualSharp", {"position": v(-3.77, -179.86) * mm});
            skArc(sketch, "E1148.filletArc", {"start": v(-2.27, -179.86) * mm, "mid": v(-3.33, -180.3) * mm, "end": v(-3.77, -181.36) * mm});
            skPoint(sketch, "E1149.visualSharp", {"position": v(11.63, -179.86) * mm});
            skArc(sketch, "E1149.filletArc", {"start": v(11.63, -181.36) * mm, "mid": v(11.19, -180.3) * mm, "end": v(10.13, -179.86) * mm});
            skPoint(sketch, "E1150.visualSharp", {"position": v(-3.77, -195.26) * mm});
            skArc(sketch, "E1150.filletArc", {"start": v(-3.77, -193.76) * mm, "mid": v(-3.33, -194.82) * mm, "end": v(-2.27, -195.26) * mm});
            skPoint(sketch, "E1151.visualSharp", {"position": v(11.63, -195.26) * mm});
            skArc(sketch, "E1151.filletArc", {"start": v(10.13, -195.26) * mm, "mid": v(11.19, -194.82) * mm, "end": v(11.63, -193.76) * mm});
            skLineSegment(sketch, "E1152.bottom", {"start": v(-2.27, -160.86) * mm, "end": v(10.13, -160.86) * mm});
            skLineSegment(sketch, "E1152.top", {"start": v(-2.27, -176.26) * mm, "end": v(10.13, -176.26) * mm});
            skLineSegment(sketch, "E1152.left", {"start": v(-3.77, -162.36) * mm, "end": v(-3.77, -174.76) * mm});
            skLineSegment(sketch, "E1152.right", {"start": v(11.63, -162.36) * mm, "end": v(11.63, -174.76) * mm});
            skPoint(sketch, "E1153.visualSharp", {"position": v(-3.77, -160.86) * mm});
            skArc(sketch, "E1153.filletArc", {"start": v(-2.27, -160.86) * mm, "mid": v(-3.33, -161.3) * mm, "end": v(-3.77, -162.36) * mm});
            skPoint(sketch, "E1154.visualSharp", {"position": v(11.63, -160.86) * mm});
            skArc(sketch, "E1154.filletArc", {"start": v(11.63, -162.36) * mm, "mid": v(11.19, -161.3) * mm, "end": v(10.13, -160.86) * mm});
            skPoint(sketch, "E1155.visualSharp", {"position": v(-3.77, -176.26) * mm});
            skArc(sketch, "E1155.filletArc", {"start": v(-3.77, -174.76) * mm, "mid": v(-3.33, -175.82) * mm, "end": v(-2.27, -176.26) * mm});
            skPoint(sketch, "E1156.visualSharp", {"position": v(11.63, -176.26) * mm});
            skArc(sketch, "E1156.filletArc", {"start": v(10.13, -176.26) * mm, "mid": v(11.19, -175.82) * mm, "end": v(11.63, -174.76) * mm});
            skLineSegment(sketch, "E1157.bottom", {"start": v(-2.27, -217.86) * mm, "end": v(10.13, -217.86) * mm});
            skLineSegment(sketch, "E1157.top", {"start": v(-2.27, -233.26) * mm, "end": v(10.13, -233.26) * mm});
            skLineSegment(sketch, "E1157.left", {"start": v(-3.77, -219.36) * mm, "end": v(-3.77, -231.76) * mm});
            skLineSegment(sketch, "E1157.right", {"start": v(11.63, -219.36) * mm, "end": v(11.63, -231.76) * mm});
            skPoint(sketch, "E1158.visualSharp", {"position": v(-3.77, -217.86) * mm});
            skArc(sketch, "E1158.filletArc", {"start": v(-2.27, -217.86) * mm, "mid": v(-3.33, -218.3) * mm, "end": v(-3.77, -219.36) * mm});
            skPoint(sketch, "E1159.visualSharp", {"position": v(11.63, -217.86) * mm});
            skArc(sketch, "E1159.filletArc", {"start": v(11.63, -219.36) * mm, "mid": v(11.19, -218.3) * mm, "end": v(10.13, -217.86) * mm});
            skPoint(sketch, "E1160.visualSharp", {"position": v(-3.77, -233.26) * mm});
            skArc(sketch, "E1160.filletArc", {"start": v(-3.77, -231.76) * mm, "mid": v(-3.33, -232.82) * mm, "end": v(-2.27, -233.26) * mm});
            skPoint(sketch, "E1161.visualSharp", {"position": v(11.63, -233.26) * mm});
            skArc(sketch, "E1161.filletArc", {"start": v(10.13, -233.26) * mm, "mid": v(11.19, -232.82) * mm, "end": v(11.63, -231.76) * mm});
            skLineSegment(sketch, "E1162.bottom", {"start": v(-2.27, -198.86) * mm, "end": v(10.13, -198.86) * mm});
            skLineSegment(sketch, "E1162.top", {"start": v(-2.27, -214.26) * mm, "end": v(10.13, -214.26) * mm});
            skLineSegment(sketch, "E1162.left", {"start": v(-3.77, -200.36) * mm, "end": v(-3.77, -212.76) * mm});
            skLineSegment(sketch, "E1162.right", {"start": v(11.63, -200.36) * mm, "end": v(11.63, -212.76) * mm});
            skPoint(sketch, "E1163.visualSharp", {"position": v(-3.77, -198.86) * mm});
            skArc(sketch, "E1163.filletArc", {"start": v(-2.27, -198.86) * mm, "mid": v(-3.33, -199.3) * mm, "end": v(-3.77, -200.36) * mm});
            skPoint(sketch, "E1164.visualSharp", {"position": v(11.63, -198.86) * mm});
            skArc(sketch, "E1164.filletArc", {"start": v(11.63, -200.36) * mm, "mid": v(11.19, -199.3) * mm, "end": v(10.13, -198.86) * mm});
            skPoint(sketch, "E1165.visualSharp", {"position": v(-3.77, -214.26) * mm});
            skArc(sketch, "E1165.filletArc", {"start": v(-3.77, -212.76) * mm, "mid": v(-3.33, -213.82) * mm, "end": v(-2.27, -214.26) * mm});
            skPoint(sketch, "E1166.visualSharp", {"position": v(11.63, -214.26) * mm});
            skArc(sketch, "E1166.filletArc", {"start": v(10.13, -214.26) * mm, "mid": v(11.19, -213.82) * mm, "end": v(11.63, -212.76) * mm});
            skLineSegment(sketch, "E1167.bottom", {"start": v(-18.77, -141.86) * mm, "end": v(-6.37, -141.86) * mm});
            skLineSegment(sketch, "E1167.top", {"start": v(-18.77, -157.26) * mm, "end": v(-6.37, -157.26) * mm});
            skLineSegment(sketch, "E1167.left", {"start": v(-20.27, -143.36) * mm, "end": v(-20.27, -155.76) * mm});
            skLineSegment(sketch, "E1167.right", {"start": v(-4.87, -143.36) * mm, "end": v(-4.87, -155.76) * mm});
            skPoint(sketch, "E1168.visualSharp", {"position": v(-20.27, -141.86) * mm});
            skArc(sketch, "E1168.filletArc", {"start": v(-18.77, -141.86) * mm, "mid": v(-19.83, -142.3) * mm, "end": v(-20.27, -143.36) * mm});
            skPoint(sketch, "E1169.visualSharp", {"position": v(-4.87, -141.86) * mm});
            skArc(sketch, "E1169.filletArc", {"start": v(-4.87, -143.36) * mm, "mid": v(-5.31, -142.3) * mm, "end": v(-6.37, -141.86) * mm});
            skPoint(sketch, "E1170.visualSharp", {"position": v(-20.27, -157.26) * mm});
            skArc(sketch, "E1170.filletArc", {"start": v(-20.27, -155.76) * mm, "mid": v(-19.83, -156.82) * mm, "end": v(-18.77, -157.26) * mm});
            skPoint(sketch, "E1171.visualSharp", {"position": v(-4.87, -157.26) * mm});
            skArc(sketch, "E1171.filletArc", {"start": v(-6.37, -157.26) * mm, "mid": v(-5.31, -156.82) * mm, "end": v(-4.87, -155.76) * mm});
            skLineSegment(sketch, "E1172.bottom", {"start": v(-18.77, -122.86) * mm, "end": v(-6.37, -122.86) * mm});
            skLineSegment(sketch, "E1172.top", {"start": v(-18.77, -138.26) * mm, "end": v(-6.37, -138.26) * mm});
            skLineSegment(sketch, "E1172.left", {"start": v(-20.27, -124.36) * mm, "end": v(-20.27, -136.76) * mm});
            skLineSegment(sketch, "E1172.right", {"start": v(-4.87, -124.36) * mm, "end": v(-4.87, -136.76) * mm});
            skPoint(sketch, "E1173.visualSharp", {"position": v(-20.27, -122.86) * mm});
            skArc(sketch, "E1173.filletArc", {"start": v(-18.77, -122.86) * mm, "mid": v(-19.83, -123.3) * mm, "end": v(-20.27, -124.36) * mm});
            skPoint(sketch, "E1174.visualSharp", {"position": v(-4.87, -122.86) * mm});
            skArc(sketch, "E1174.filletArc", {"start": v(-4.87, -124.36) * mm, "mid": v(-5.31, -123.3) * mm, "end": v(-6.37, -122.86) * mm});
            skPoint(sketch, "E1175.visualSharp", {"position": v(-20.27, -138.26) * mm});
            skArc(sketch, "E1175.filletArc", {"start": v(-20.27, -136.76) * mm, "mid": v(-19.83, -137.82) * mm, "end": v(-18.77, -138.26) * mm});
            skPoint(sketch, "E1176.visualSharp", {"position": v(-4.87, -138.26) * mm});
            skArc(sketch, "E1176.filletArc", {"start": v(-6.37, -138.26) * mm, "mid": v(-5.31, -137.82) * mm, "end": v(-4.87, -136.76) * mm});
            skLineSegment(sketch, "E1177.bottom", {"start": v(-18.77, -179.86) * mm, "end": v(-6.37, -179.86) * mm});
            skLineSegment(sketch, "E1177.top", {"start": v(-18.77, -195.26) * mm, "end": v(-6.37, -195.26) * mm});
            skLineSegment(sketch, "E1177.left", {"start": v(-20.27, -181.36) * mm, "end": v(-20.27, -193.76) * mm});
            skLineSegment(sketch, "E1177.right", {"start": v(-4.87, -181.36) * mm, "end": v(-4.87, -193.76) * mm});
            skPoint(sketch, "E1178.visualSharp", {"position": v(-20.27, -179.86) * mm});
            skArc(sketch, "E1178.filletArc", {"start": v(-18.77, -179.86) * mm, "mid": v(-19.83, -180.3) * mm, "end": v(-20.27, -181.36) * mm});
            skPoint(sketch, "E1179.visualSharp", {"position": v(-4.87, -179.86) * mm});
            skArc(sketch, "E1179.filletArc", {"start": v(-4.87, -181.36) * mm, "mid": v(-5.31, -180.3) * mm, "end": v(-6.37, -179.86) * mm});
            skPoint(sketch, "E1180.visualSharp", {"position": v(-20.27, -195.26) * mm});
            skArc(sketch, "E1180.filletArc", {"start": v(-20.27, -193.76) * mm, "mid": v(-19.83, -194.82) * mm, "end": v(-18.77, -195.26) * mm});
            skPoint(sketch, "E1181.visualSharp", {"position": v(-4.87, -195.26) * mm});
            skArc(sketch, "E1181.filletArc", {"start": v(-6.37, -195.26) * mm, "mid": v(-5.31, -194.82) * mm, "end": v(-4.87, -193.76) * mm});
            skLineSegment(sketch, "E1182.bottom", {"start": v(-18.77, -160.86) * mm, "end": v(-6.37, -160.86) * mm});
            skLineSegment(sketch, "E1182.top", {"start": v(-18.77, -176.26) * mm, "end": v(-6.37, -176.26) * mm});
            skLineSegment(sketch, "E1182.left", {"start": v(-20.27, -162.36) * mm, "end": v(-20.27, -174.76) * mm});
            skLineSegment(sketch, "E1182.right", {"start": v(-4.87, -162.36) * mm, "end": v(-4.87, -174.76) * mm});
            skPoint(sketch, "E1183.visualSharp", {"position": v(-20.27, -160.86) * mm});
            skArc(sketch, "E1183.filletArc", {"start": v(-18.77, -160.86) * mm, "mid": v(-19.83, -161.3) * mm, "end": v(-20.27, -162.36) * mm});
            skPoint(sketch, "E1184.visualSharp", {"position": v(-4.87, -160.86) * mm});
            skArc(sketch, "E1184.filletArc", {"start": v(-4.87, -162.36) * mm, "mid": v(-5.31, -161.3) * mm, "end": v(-6.37, -160.86) * mm});
            skPoint(sketch, "E1185.visualSharp", {"position": v(-20.27, -176.26) * mm});
            skArc(sketch, "E1185.filletArc", {"start": v(-20.27, -174.76) * mm, "mid": v(-19.83, -175.82) * mm, "end": v(-18.77, -176.26) * mm});
            skPoint(sketch, "E1186.visualSharp", {"position": v(-4.87, -176.26) * mm});
            skArc(sketch, "E1186.filletArc", {"start": v(-6.37, -176.26) * mm, "mid": v(-5.31, -175.82) * mm, "end": v(-4.87, -174.76) * mm});
            skLineSegment(sketch, "E1187.bottom", {"start": v(-18.77, -217.86) * mm, "end": v(-6.37, -217.86) * mm});
            skLineSegment(sketch, "E1187.top", {"start": v(-18.77, -233.26) * mm, "end": v(-6.37, -233.26) * mm});
            skLineSegment(sketch, "E1187.left", {"start": v(-20.27, -219.36) * mm, "end": v(-20.27, -231.76) * mm});
            skLineSegment(sketch, "E1187.right", {"start": v(-4.87, -219.36) * mm, "end": v(-4.87, -231.76) * mm});
            skPoint(sketch, "E1188.visualSharp", {"position": v(-20.27, -217.86) * mm});
            skArc(sketch, "E1188.filletArc", {"start": v(-18.77, -217.86) * mm, "mid": v(-19.83, -218.3) * mm, "end": v(-20.27, -219.36) * mm});
            skPoint(sketch, "E1189.visualSharp", {"position": v(-4.87, -217.86) * mm});
            skArc(sketch, "E1189.filletArc", {"start": v(-4.87, -219.36) * mm, "mid": v(-5.31, -218.3) * mm, "end": v(-6.37, -217.86) * mm});
            skPoint(sketch, "E1190.visualSharp", {"position": v(-20.27, -233.26) * mm});
            skArc(sketch, "E1190.filletArc", {"start": v(-20.27, -231.76) * mm, "mid": v(-19.83, -232.82) * mm, "end": v(-18.77, -233.26) * mm});
            skPoint(sketch, "E1191.visualSharp", {"position": v(-4.87, -233.26) * mm});
            skArc(sketch, "E1191.filletArc", {"start": v(-6.37, -233.26) * mm, "mid": v(-5.31, -232.82) * mm, "end": v(-4.87, -231.76) * mm});
            skLineSegment(sketch, "E1192.bottom", {"start": v(-18.77, -198.86) * mm, "end": v(-6.37, -198.86) * mm});
            skLineSegment(sketch, "E1192.top", {"start": v(-18.77, -214.26) * mm, "end": v(-6.37, -214.26) * mm});
            skLineSegment(sketch, "E1192.left", {"start": v(-20.27, -200.36) * mm, "end": v(-20.27, -212.76) * mm});
            skLineSegment(sketch, "E1192.right", {"start": v(-4.87, -200.36) * mm, "end": v(-4.87, -212.76) * mm});
            skPoint(sketch, "E1193.visualSharp", {"position": v(-20.27, -198.86) * mm});
            skArc(sketch, "E1193.filletArc", {"start": v(-18.77, -198.86) * mm, "mid": v(-19.83, -199.3) * mm, "end": v(-20.27, -200.36) * mm});
            skPoint(sketch, "E1194.visualSharp", {"position": v(-4.87, -198.86) * mm});
            skArc(sketch, "E1194.filletArc", {"start": v(-4.87, -200.36) * mm, "mid": v(-5.31, -199.3) * mm, "end": v(-6.37, -198.86) * mm});
            skPoint(sketch, "E1195.visualSharp", {"position": v(-20.27, -214.26) * mm});
            skArc(sketch, "E1195.filletArc", {"start": v(-20.27, -212.76) * mm, "mid": v(-19.83, -213.82) * mm, "end": v(-18.77, -214.26) * mm});
            skPoint(sketch, "E1196.visualSharp", {"position": v(-4.87, -214.26) * mm});
            skArc(sketch, "E1196.filletArc", {"start": v(-6.37, -214.26) * mm, "mid": v(-5.31, -213.82) * mm, "end": v(-4.87, -212.76) * mm});
            skLineSegment(sketch, "E1197.bottom", {"start": v(-35.27, -141.86) * mm, "end": v(-22.87, -141.86) * mm});
            skLineSegment(sketch, "E1197.top", {"start": v(-35.27, -157.26) * mm, "end": v(-22.87, -157.26) * mm});
            skLineSegment(sketch, "E1197.left", {"start": v(-36.77, -143.36) * mm, "end": v(-36.77, -155.76) * mm});
            skLineSegment(sketch, "E1197.right", {"start": v(-21.37, -143.36) * mm, "end": v(-21.37, -155.76) * mm});
            skPoint(sketch, "E1198.visualSharp", {"position": v(-36.77, -141.86) * mm});
            skArc(sketch, "E1198.filletArc", {"start": v(-35.27, -141.86) * mm, "mid": v(-36.33, -142.3) * mm, "end": v(-36.77, -143.36) * mm});
            skPoint(sketch, "E1199.visualSharp", {"position": v(-21.37, -141.86) * mm});
            skArc(sketch, "E1199.filletArc", {"start": v(-21.37, -143.36) * mm, "mid": v(-21.81, -142.3) * mm, "end": v(-22.87, -141.86) * mm});
            skPoint(sketch, "E1200.visualSharp", {"position": v(-36.77, -157.26) * mm});
            skArc(sketch, "E1200.filletArc", {"start": v(-36.77, -155.76) * mm, "mid": v(-36.33, -156.82) * mm, "end": v(-35.27, -157.26) * mm});
            skPoint(sketch, "E1201.visualSharp", {"position": v(-21.37, -157.26) * mm});
            skArc(sketch, "E1201.filletArc", {"start": v(-22.87, -157.26) * mm, "mid": v(-21.81, -156.82) * mm, "end": v(-21.37, -155.76) * mm});
            skLineSegment(sketch, "E1202.bottom", {"start": v(-35.27, -122.86) * mm, "end": v(-22.87, -122.86) * mm});
            skLineSegment(sketch, "E1202.top", {"start": v(-35.27, -138.26) * mm, "end": v(-22.87, -138.26) * mm});
            skLineSegment(sketch, "E1202.left", {"start": v(-36.77, -124.36) * mm, "end": v(-36.77, -136.76) * mm});
            skLineSegment(sketch, "E1202.right", {"start": v(-21.37, -124.36) * mm, "end": v(-21.37, -136.76) * mm});
            skPoint(sketch, "E1203.visualSharp", {"position": v(-36.77, -122.86) * mm});
            skArc(sketch, "E1203.filletArc", {"start": v(-35.27, -122.86) * mm, "mid": v(-36.33, -123.3) * mm, "end": v(-36.77, -124.36) * mm});
            skPoint(sketch, "E1204.visualSharp", {"position": v(-21.37, -122.86) * mm});
            skArc(sketch, "E1204.filletArc", {"start": v(-21.37, -124.36) * mm, "mid": v(-21.81, -123.3) * mm, "end": v(-22.87, -122.86) * mm});
            skPoint(sketch, "E1205.visualSharp", {"position": v(-36.77, -138.26) * mm});
            skArc(sketch, "E1205.filletArc", {"start": v(-36.77, -136.76) * mm, "mid": v(-36.33, -137.82) * mm, "end": v(-35.27, -138.26) * mm});
            skPoint(sketch, "E1206.visualSharp", {"position": v(-21.37, -138.26) * mm});
            skArc(sketch, "E1206.filletArc", {"start": v(-22.87, -138.26) * mm, "mid": v(-21.81, -137.82) * mm, "end": v(-21.37, -136.76) * mm});
            skLineSegment(sketch, "E1207.bottom", {"start": v(-35.27, -179.86) * mm, "end": v(-22.87, -179.86) * mm});
            skLineSegment(sketch, "E1207.top", {"start": v(-35.27, -195.26) * mm, "end": v(-22.87, -195.26) * mm});
            skLineSegment(sketch, "E1207.left", {"start": v(-36.77, -181.36) * mm, "end": v(-36.77, -193.76) * mm});
            skLineSegment(sketch, "E1207.right", {"start": v(-21.37, -181.36) * mm, "end": v(-21.37, -193.76) * mm});
            skPoint(sketch, "E1208.visualSharp", {"position": v(-36.77, -179.86) * mm});
            skArc(sketch, "E1208.filletArc", {"start": v(-35.27, -179.86) * mm, "mid": v(-36.33, -180.3) * mm, "end": v(-36.77, -181.36) * mm});
            skPoint(sketch, "E1209.visualSharp", {"position": v(-21.37, -179.86) * mm});
            skArc(sketch, "E1209.filletArc", {"start": v(-21.37, -181.36) * mm, "mid": v(-21.81, -180.3) * mm, "end": v(-22.87, -179.86) * mm});
            skPoint(sketch, "E1210.visualSharp", {"position": v(-36.77, -195.26) * mm});
            skArc(sketch, "E1210.filletArc", {"start": v(-36.77, -193.76) * mm, "mid": v(-36.33, -194.82) * mm, "end": v(-35.27, -195.26) * mm});
            skPoint(sketch, "E1211.visualSharp", {"position": v(-21.37, -195.26) * mm});
            skArc(sketch, "E1211.filletArc", {"start": v(-22.87, -195.26) * mm, "mid": v(-21.81, -194.82) * mm, "end": v(-21.37, -193.76) * mm});
            skLineSegment(sketch, "E1212.bottom", {"start": v(-35.27, -160.86) * mm, "end": v(-22.87, -160.86) * mm});
            skLineSegment(sketch, "E1212.top", {"start": v(-35.27, -176.26) * mm, "end": v(-22.87, -176.26) * mm});
            skLineSegment(sketch, "E1212.left", {"start": v(-36.77, -162.36) * mm, "end": v(-36.77, -174.76) * mm});
            skLineSegment(sketch, "E1212.right", {"start": v(-21.37, -162.36) * mm, "end": v(-21.37, -174.76) * mm});
            skPoint(sketch, "E1213.visualSharp", {"position": v(-36.77, -160.86) * mm});
            skArc(sketch, "E1213.filletArc", {"start": v(-35.27, -160.86) * mm, "mid": v(-36.33, -161.3) * mm, "end": v(-36.77, -162.36) * mm});
            skPoint(sketch, "E1214.visualSharp", {"position": v(-21.37, -160.86) * mm});
            skArc(sketch, "E1214.filletArc", {"start": v(-21.37, -162.36) * mm, "mid": v(-21.81, -161.3) * mm, "end": v(-22.87, -160.86) * mm});
            skPoint(sketch, "E1215.visualSharp", {"position": v(-36.77, -176.26) * mm});
            skArc(sketch, "E1215.filletArc", {"start": v(-36.77, -174.76) * mm, "mid": v(-36.33, -175.82) * mm, "end": v(-35.27, -176.26) * mm});
            skPoint(sketch, "E1216.visualSharp", {"position": v(-21.37, -176.26) * mm});
            skArc(sketch, "E1216.filletArc", {"start": v(-22.87, -176.26) * mm, "mid": v(-21.81, -175.82) * mm, "end": v(-21.37, -174.76) * mm});
            skLineSegment(sketch, "E1217.bottom", {"start": v(-35.27, -217.86) * mm, "end": v(-22.87, -217.86) * mm});
            skLineSegment(sketch, "E1217.top", {"start": v(-35.27, -233.26) * mm, "end": v(-22.87, -233.26) * mm});
            skLineSegment(sketch, "E1217.left", {"start": v(-36.77, -219.36) * mm, "end": v(-36.77, -231.76) * mm});
            skLineSegment(sketch, "E1217.right", {"start": v(-21.37, -219.36) * mm, "end": v(-21.37, -231.76) * mm});
            skPoint(sketch, "E1218.visualSharp", {"position": v(-36.77, -217.86) * mm});
            skArc(sketch, "E1218.filletArc", {"start": v(-35.27, -217.86) * mm, "mid": v(-36.33, -218.3) * mm, "end": v(-36.77, -219.36) * mm});
            skPoint(sketch, "E1219.visualSharp", {"position": v(-21.37, -217.86) * mm});
            skArc(sketch, "E1219.filletArc", {"start": v(-21.37, -219.36) * mm, "mid": v(-21.81, -218.3) * mm, "end": v(-22.87, -217.86) * mm});
            skPoint(sketch, "E1220.visualSharp", {"position": v(-36.77, -233.26) * mm});
            skArc(sketch, "E1220.filletArc", {"start": v(-36.77, -231.76) * mm, "mid": v(-36.33, -232.82) * mm, "end": v(-35.27, -233.26) * mm});
            skPoint(sketch, "E1221.visualSharp", {"position": v(-21.37, -233.26) * mm});
            skArc(sketch, "E1221.filletArc", {"start": v(-22.87, -233.26) * mm, "mid": v(-21.81, -232.82) * mm, "end": v(-21.37, -231.76) * mm});
            skLineSegment(sketch, "E1222.bottom", {"start": v(-35.27, -198.86) * mm, "end": v(-22.87, -198.86) * mm});
            skLineSegment(sketch, "E1222.top", {"start": v(-35.27, -214.26) * mm, "end": v(-22.87, -214.26) * mm});
            skLineSegment(sketch, "E1222.left", {"start": v(-36.77, -200.36) * mm, "end": v(-36.77, -212.76) * mm});
            skLineSegment(sketch, "E1222.right", {"start": v(-21.37, -200.36) * mm, "end": v(-21.37, -212.76) * mm});
            skPoint(sketch, "E1223.visualSharp", {"position": v(-36.77, -198.86) * mm});
            skArc(sketch, "E1223.filletArc", {"start": v(-35.27, -198.86) * mm, "mid": v(-36.33, -199.3) * mm, "end": v(-36.77, -200.36) * mm});
            skPoint(sketch, "E1224.visualSharp", {"position": v(-21.37, -198.86) * mm});
            skArc(sketch, "E1224.filletArc", {"start": v(-21.37, -200.36) * mm, "mid": v(-21.81, -199.3) * mm, "end": v(-22.87, -198.86) * mm});
            skPoint(sketch, "E1225.visualSharp", {"position": v(-36.77, -214.26) * mm});
            skArc(sketch, "E1225.filletArc", {"start": v(-36.77, -212.76) * mm, "mid": v(-36.33, -213.82) * mm, "end": v(-35.27, -214.26) * mm});
            skPoint(sketch, "E1226.visualSharp", {"position": v(-21.37, -214.26) * mm});
            skArc(sketch, "E1226.filletArc", {"start": v(-22.87, -214.26) * mm, "mid": v(-21.81, -213.82) * mm, "end": v(-21.37, -212.76) * mm});
            skLineSegment(sketch, "E1227.bottom", {"start": v(-51.77, -141.86) * mm, "end": v(-39.37, -141.86) * mm});
            skLineSegment(sketch, "E1227.top", {"start": v(-51.77, -157.26) * mm, "end": v(-39.37, -157.26) * mm});
            skLineSegment(sketch, "E1227.left", {"start": v(-53.27, -143.36) * mm, "end": v(-53.27, -155.76) * mm});
            skLineSegment(sketch, "E1227.right", {"start": v(-37.87, -143.36) * mm, "end": v(-37.87, -155.76) * mm});
            skPoint(sketch, "E1228.visualSharp", {"position": v(-53.27, -141.86) * mm});
            skArc(sketch, "E1228.filletArc", {"start": v(-51.77, -141.86) * mm, "mid": v(-52.83, -142.3) * mm, "end": v(-53.27, -143.36) * mm});
            skPoint(sketch, "E1229.visualSharp", {"position": v(-37.87, -141.86) * mm});
            skArc(sketch, "E1229.filletArc", {"start": v(-37.87, -143.36) * mm, "mid": v(-38.31, -142.3) * mm, "end": v(-39.37, -141.86) * mm});
            skPoint(sketch, "E1230.visualSharp", {"position": v(-53.27, -157.26) * mm});
            skArc(sketch, "E1230.filletArc", {"start": v(-53.27, -155.76) * mm, "mid": v(-52.83, -156.82) * mm, "end": v(-51.77, -157.26) * mm});
            skPoint(sketch, "E1231.visualSharp", {"position": v(-37.87, -157.26) * mm});
            skArc(sketch, "E1231.filletArc", {"start": v(-39.37, -157.26) * mm, "mid": v(-38.31, -156.82) * mm, "end": v(-37.87, -155.76) * mm});
            skLineSegment(sketch, "E1232.bottom", {"start": v(-51.77, -122.86) * mm, "end": v(-39.37, -122.86) * mm});
            skLineSegment(sketch, "E1232.top", {"start": v(-51.77, -138.26) * mm, "end": v(-39.37, -138.26) * mm});
            skLineSegment(sketch, "E1232.left", {"start": v(-53.27, -124.36) * mm, "end": v(-53.27, -136.76) * mm});
            skLineSegment(sketch, "E1232.right", {"start": v(-37.87, -124.36) * mm, "end": v(-37.87, -136.76) * mm});
            skPoint(sketch, "E1233.visualSharp", {"position": v(-53.27, -122.86) * mm});
            skArc(sketch, "E1233.filletArc", {"start": v(-51.77, -122.86) * mm, "mid": v(-52.83, -123.3) * mm, "end": v(-53.27, -124.36) * mm});
            skPoint(sketch, "E1234.visualSharp", {"position": v(-37.87, -122.86) * mm});
            skArc(sketch, "E1234.filletArc", {"start": v(-37.87, -124.36) * mm, "mid": v(-38.31, -123.3) * mm, "end": v(-39.37, -122.86) * mm});
            skPoint(sketch, "E1235.visualSharp", {"position": v(-53.27, -138.26) * mm});
            skArc(sketch, "E1235.filletArc", {"start": v(-53.27, -136.76) * mm, "mid": v(-52.83, -137.82) * mm, "end": v(-51.77, -138.26) * mm});
            skPoint(sketch, "E1236.visualSharp", {"position": v(-37.87, -138.26) * mm});
            skArc(sketch, "E1236.filletArc", {"start": v(-39.37, -138.26) * mm, "mid": v(-38.31, -137.82) * mm, "end": v(-37.87, -136.76) * mm});
            skLineSegment(sketch, "E1237.bottom", {"start": v(-51.77, -179.86) * mm, "end": v(-39.37, -179.86) * mm});
            skLineSegment(sketch, "E1237.top", {"start": v(-51.77, -195.26) * mm, "end": v(-39.37, -195.26) * mm});
            skLineSegment(sketch, "E1237.left", {"start": v(-53.27, -181.36) * mm, "end": v(-53.27, -193.76) * mm});
            skLineSegment(sketch, "E1237.right", {"start": v(-37.87, -181.36) * mm, "end": v(-37.87, -193.76) * mm});
            skPoint(sketch, "E1238.visualSharp", {"position": v(-53.27, -179.86) * mm});
            skArc(sketch, "E1238.filletArc", {"start": v(-51.77, -179.86) * mm, "mid": v(-52.83, -180.3) * mm, "end": v(-53.27, -181.36) * mm});
            skPoint(sketch, "E1239.visualSharp", {"position": v(-37.87, -179.86) * mm});
            skArc(sketch, "E1239.filletArc", {"start": v(-37.87, -181.36) * mm, "mid": v(-38.31, -180.3) * mm, "end": v(-39.37, -179.86) * mm});
            skPoint(sketch, "E1240.visualSharp", {"position": v(-53.27, -195.26) * mm});
            skArc(sketch, "E1240.filletArc", {"start": v(-53.27, -193.76) * mm, "mid": v(-52.83, -194.82) * mm, "end": v(-51.77, -195.26) * mm});
            skPoint(sketch, "E1241.visualSharp", {"position": v(-37.87, -195.26) * mm});
            skArc(sketch, "E1241.filletArc", {"start": v(-39.37, -195.26) * mm, "mid": v(-38.31, -194.82) * mm, "end": v(-37.87, -193.76) * mm});
            skLineSegment(sketch, "E1242.bottom", {"start": v(-51.77, -160.86) * mm, "end": v(-39.37, -160.86) * mm});
            skLineSegment(sketch, "E1242.top", {"start": v(-51.77, -176.26) * mm, "end": v(-39.37, -176.26) * mm});
            skLineSegment(sketch, "E1242.left", {"start": v(-53.27, -162.36) * mm, "end": v(-53.27, -174.76) * mm});
            skLineSegment(sketch, "E1242.right", {"start": v(-37.87, -162.36) * mm, "end": v(-37.87, -174.76) * mm});
            skPoint(sketch, "E1243.visualSharp", {"position": v(-53.27, -160.86) * mm});
            skArc(sketch, "E1243.filletArc", {"start": v(-51.77, -160.86) * mm, "mid": v(-52.83, -161.3) * mm, "end": v(-53.27, -162.36) * mm});
            skPoint(sketch, "E1244.visualSharp", {"position": v(-37.87, -160.86) * mm});
            skArc(sketch, "E1244.filletArc", {"start": v(-37.87, -162.36) * mm, "mid": v(-38.31, -161.3) * mm, "end": v(-39.37, -160.86) * mm});
            skPoint(sketch, "E1245.visualSharp", {"position": v(-53.27, -176.26) * mm});
            skArc(sketch, "E1245.filletArc", {"start": v(-53.27, -174.76) * mm, "mid": v(-52.83, -175.82) * mm, "end": v(-51.77, -176.26) * mm});
            skPoint(sketch, "E1246.visualSharp", {"position": v(-37.87, -176.26) * mm});
            skArc(sketch, "E1246.filletArc", {"start": v(-39.37, -176.26) * mm, "mid": v(-38.31, -175.82) * mm, "end": v(-37.87, -174.76) * mm});
            skLineSegment(sketch, "E1247.bottom", {"start": v(-51.77, -217.86) * mm, "end": v(-39.37, -217.86) * mm});
            skLineSegment(sketch, "E1247.top", {"start": v(-51.77, -233.26) * mm, "end": v(-39.37, -233.26) * mm});
            skLineSegment(sketch, "E1247.left", {"start": v(-53.27, -219.36) * mm, "end": v(-53.27, -231.76) * mm});
            skLineSegment(sketch, "E1247.right", {"start": v(-37.87, -219.36) * mm, "end": v(-37.87, -231.76) * mm});
            skPoint(sketch, "E1248.visualSharp", {"position": v(-53.27, -217.86) * mm});
            skArc(sketch, "E1248.filletArc", {"start": v(-51.77, -217.86) * mm, "mid": v(-52.83, -218.3) * mm, "end": v(-53.27, -219.36) * mm});
            skPoint(sketch, "E1249.visualSharp", {"position": v(-37.87, -217.86) * mm});
            skArc(sketch, "E1249.filletArc", {"start": v(-37.87, -219.36) * mm, "mid": v(-38.31, -218.3) * mm, "end": v(-39.37, -217.86) * mm});
            skPoint(sketch, "E1250.visualSharp", {"position": v(-53.27, -233.26) * mm});
            skArc(sketch, "E1250.filletArc", {"start": v(-53.27, -231.76) * mm, "mid": v(-52.83, -232.82) * mm, "end": v(-51.77, -233.26) * mm});
            skPoint(sketch, "E1251.visualSharp", {"position": v(-37.87, -233.26) * mm});
            skArc(sketch, "E1251.filletArc", {"start": v(-39.37, -233.26) * mm, "mid": v(-38.31, -232.82) * mm, "end": v(-37.87, -231.76) * mm});
            skLineSegment(sketch, "E1252.bottom", {"start": v(-51.77, -198.86) * mm, "end": v(-39.37, -198.86) * mm});
            skLineSegment(sketch, "E1252.top", {"start": v(-51.77, -214.26) * mm, "end": v(-39.37, -214.26) * mm});
            skLineSegment(sketch, "E1252.left", {"start": v(-53.27, -200.36) * mm, "end": v(-53.27, -212.76) * mm});
            skLineSegment(sketch, "E1252.right", {"start": v(-37.87, -200.36) * mm, "end": v(-37.87, -212.76) * mm});
            skPoint(sketch, "E1253.visualSharp", {"position": v(-53.27, -198.86) * mm});
            skArc(sketch, "E1253.filletArc", {"start": v(-51.77, -198.86) * mm, "mid": v(-52.83, -199.3) * mm, "end": v(-53.27, -200.36) * mm});
            skPoint(sketch, "E1254.visualSharp", {"position": v(-37.87, -198.86) * mm});
            skArc(sketch, "E1254.filletArc", {"start": v(-37.87, -200.36) * mm, "mid": v(-38.31, -199.3) * mm, "end": v(-39.37, -198.86) * mm});
            skPoint(sketch, "E1255.visualSharp", {"position": v(-53.27, -214.26) * mm});
            skArc(sketch, "E1255.filletArc", {"start": v(-53.27, -212.76) * mm, "mid": v(-52.83, -213.82) * mm, "end": v(-51.77, -214.26) * mm});
            skPoint(sketch, "E1256.visualSharp", {"position": v(-37.87, -214.26) * mm});
            skArc(sketch, "E1256.filletArc", {"start": v(-39.37, -214.26) * mm, "mid": v(-38.31, -213.82) * mm, "end": v(-37.87, -212.76) * mm});
            skLineSegment(sketch, "E1257.bottom", {"start": v(-68.27, -141.86) * mm, "end": v(-55.87, -141.86) * mm});
            skLineSegment(sketch, "E1257.top", {"start": v(-68.27, -157.26) * mm, "end": v(-55.87, -157.26) * mm});
            skLineSegment(sketch, "E1257.left", {"start": v(-69.77, -143.36) * mm, "end": v(-69.77, -155.76) * mm});
            skLineSegment(sketch, "E1257.right", {"start": v(-54.37, -143.36) * mm, "end": v(-54.37, -155.76) * mm});
            skPoint(sketch, "E1258.visualSharp", {"position": v(-69.77, -141.86) * mm});
            skArc(sketch, "E1258.filletArc", {"start": v(-68.27, -141.86) * mm, "mid": v(-69.33, -142.3) * mm, "end": v(-69.77, -143.36) * mm});
            skPoint(sketch, "E1259.visualSharp", {"position": v(-54.37, -141.86) * mm});
            skArc(sketch, "E1259.filletArc", {"start": v(-54.37, -143.36) * mm, "mid": v(-54.81, -142.3) * mm, "end": v(-55.87, -141.86) * mm});
            skPoint(sketch, "E1260.visualSharp", {"position": v(-69.77, -157.26) * mm});
            skArc(sketch, "E1260.filletArc", {"start": v(-69.77, -155.76) * mm, "mid": v(-69.33, -156.82) * mm, "end": v(-68.27, -157.26) * mm});
            skPoint(sketch, "E1261.visualSharp", {"position": v(-54.37, -157.26) * mm});
            skArc(sketch, "E1261.filletArc", {"start": v(-55.87, -157.26) * mm, "mid": v(-54.81, -156.82) * mm, "end": v(-54.37, -155.76) * mm});
            skLineSegment(sketch, "E1262.bottom", {"start": v(-68.27, -122.86) * mm, "end": v(-55.87, -122.86) * mm});
            skLineSegment(sketch, "E1262.top", {"start": v(-68.27, -138.26) * mm, "end": v(-55.87, -138.26) * mm});
            skLineSegment(sketch, "E1262.left", {"start": v(-69.77, -124.36) * mm, "end": v(-69.77, -136.76) * mm});
            skLineSegment(sketch, "E1262.right", {"start": v(-54.37, -124.36) * mm, "end": v(-54.37, -136.76) * mm});
            skPoint(sketch, "E1263.visualSharp", {"position": v(-69.77, -122.86) * mm});
            skArc(sketch, "E1263.filletArc", {"start": v(-68.27, -122.86) * mm, "mid": v(-69.33, -123.3) * mm, "end": v(-69.77, -124.36) * mm});
            skPoint(sketch, "E1264.visualSharp", {"position": v(-54.37, -122.86) * mm});
            skArc(sketch, "E1264.filletArc", {"start": v(-54.37, -124.36) * mm, "mid": v(-54.81, -123.3) * mm, "end": v(-55.87, -122.86) * mm});
            skPoint(sketch, "E1265.visualSharp", {"position": v(-69.77, -138.26) * mm});
            skArc(sketch, "E1265.filletArc", {"start": v(-69.77, -136.76) * mm, "mid": v(-69.33, -137.82) * mm, "end": v(-68.27, -138.26) * mm});
            skPoint(sketch, "E1266.visualSharp", {"position": v(-54.37, -138.26) * mm});
            skArc(sketch, "E1266.filletArc", {"start": v(-55.87, -138.26) * mm, "mid": v(-54.81, -137.82) * mm, "end": v(-54.37, -136.76) * mm});
            skLineSegment(sketch, "E1267.bottom", {"start": v(-68.27, -179.86) * mm, "end": v(-55.87, -179.86) * mm});
            skLineSegment(sketch, "E1267.top", {"start": v(-68.27, -195.26) * mm, "end": v(-55.87, -195.26) * mm});
            skLineSegment(sketch, "E1267.left", {"start": v(-69.77, -181.36) * mm, "end": v(-69.77, -193.76) * mm});
            skLineSegment(sketch, "E1267.right", {"start": v(-54.37, -181.36) * mm, "end": v(-54.37, -193.76) * mm});
            skPoint(sketch, "E1268.visualSharp", {"position": v(-69.77, -179.86) * mm});
            skArc(sketch, "E1268.filletArc", {"start": v(-68.27, -179.86) * mm, "mid": v(-69.33, -180.3) * mm, "end": v(-69.77, -181.36) * mm});
            skPoint(sketch, "E1269.visualSharp", {"position": v(-54.37, -179.86) * mm});
            skArc(sketch, "E1269.filletArc", {"start": v(-54.37, -181.36) * mm, "mid": v(-54.81, -180.3) * mm, "end": v(-55.87, -179.86) * mm});
            skPoint(sketch, "E1270.visualSharp", {"position": v(-69.77, -195.26) * mm});
            skArc(sketch, "E1270.filletArc", {"start": v(-69.77, -193.76) * mm, "mid": v(-69.33, -194.82) * mm, "end": v(-68.27, -195.26) * mm});
            skPoint(sketch, "E1271.visualSharp", {"position": v(-54.37, -195.26) * mm});
            skArc(sketch, "E1271.filletArc", {"start": v(-55.87, -195.26) * mm, "mid": v(-54.81, -194.82) * mm, "end": v(-54.37, -193.76) * mm});
            skLineSegment(sketch, "E1272.bottom", {"start": v(-68.27, -160.86) * mm, "end": v(-55.87, -160.86) * mm});
            skLineSegment(sketch, "E1272.top", {"start": v(-68.27, -176.26) * mm, "end": v(-55.87, -176.26) * mm});
            skLineSegment(sketch, "E1272.left", {"start": v(-69.77, -162.36) * mm, "end": v(-69.77, -174.76) * mm});
            skLineSegment(sketch, "E1272.right", {"start": v(-54.37, -162.36) * mm, "end": v(-54.37, -174.76) * mm});
            skPoint(sketch, "E1273.visualSharp", {"position": v(-69.77, -160.86) * mm});
            skArc(sketch, "E1273.filletArc", {"start": v(-68.27, -160.86) * mm, "mid": v(-69.33, -161.3) * mm, "end": v(-69.77, -162.36) * mm});
            skPoint(sketch, "E1274.visualSharp", {"position": v(-54.37, -160.86) * mm});
            skArc(sketch, "E1274.filletArc", {"start": v(-54.37, -162.36) * mm, "mid": v(-54.81, -161.3) * mm, "end": v(-55.87, -160.86) * mm});
            skPoint(sketch, "E1275.visualSharp", {"position": v(-69.77, -176.26) * mm});
            skArc(sketch, "E1275.filletArc", {"start": v(-69.77, -174.76) * mm, "mid": v(-69.33, -175.82) * mm, "end": v(-68.27, -176.26) * mm});
            skPoint(sketch, "E1276.visualSharp", {"position": v(-54.37, -176.26) * mm});
            skArc(sketch, "E1276.filletArc", {"start": v(-55.87, -176.26) * mm, "mid": v(-54.81, -175.82) * mm, "end": v(-54.37, -174.76) * mm});
            skLineSegment(sketch, "E1277.bottom", {"start": v(-68.27, -217.86) * mm, "end": v(-55.87, -217.86) * mm});
            skLineSegment(sketch, "E1277.top", {"start": v(-68.27, -233.26) * mm, "end": v(-55.87, -233.26) * mm});
            skLineSegment(sketch, "E1277.left", {"start": v(-69.77, -219.36) * mm, "end": v(-69.77, -231.76) * mm});
            skLineSegment(sketch, "E1277.right", {"start": v(-54.37, -219.36) * mm, "end": v(-54.37, -231.76) * mm});
            skPoint(sketch, "E1278.visualSharp", {"position": v(-69.77, -217.86) * mm});
            skArc(sketch, "E1278.filletArc", {"start": v(-68.27, -217.86) * mm, "mid": v(-69.33, -218.3) * mm, "end": v(-69.77, -219.36) * mm});
            skPoint(sketch, "E1279.visualSharp", {"position": v(-54.37, -217.86) * mm});
            skArc(sketch, "E1279.filletArc", {"start": v(-54.37, -219.36) * mm, "mid": v(-54.81, -218.3) * mm, "end": v(-55.87, -217.86) * mm});
            skPoint(sketch, "E1280.visualSharp", {"position": v(-69.77, -233.26) * mm});
            skArc(sketch, "E1280.filletArc", {"start": v(-69.77, -231.76) * mm, "mid": v(-69.33, -232.82) * mm, "end": v(-68.27, -233.26) * mm});
            skPoint(sketch, "E1281.visualSharp", {"position": v(-54.37, -233.26) * mm});
            skArc(sketch, "E1281.filletArc", {"start": v(-55.87, -233.26) * mm, "mid": v(-54.81, -232.82) * mm, "end": v(-54.37, -231.76) * mm});
            skLineSegment(sketch, "E1282.bottom", {"start": v(-68.27, -198.86) * mm, "end": v(-55.87, -198.86) * mm});
            skLineSegment(sketch, "E1282.top", {"start": v(-68.27, -214.26) * mm, "end": v(-55.87, -214.26) * mm});
            skLineSegment(sketch, "E1282.left", {"start": v(-69.77, -200.36) * mm, "end": v(-69.77, -212.76) * mm});
            skLineSegment(sketch, "E1282.right", {"start": v(-54.37, -200.36) * mm, "end": v(-54.37, -212.76) * mm});
            skPoint(sketch, "E1283.visualSharp", {"position": v(-69.77, -198.86) * mm});
            skArc(sketch, "E1283.filletArc", {"start": v(-68.27, -198.86) * mm, "mid": v(-69.33, -199.3) * mm, "end": v(-69.77, -200.36) * mm});
            skPoint(sketch, "E1284.visualSharp", {"position": v(-54.37, -198.86) * mm});
            skArc(sketch, "E1284.filletArc", {"start": v(-54.37, -200.36) * mm, "mid": v(-54.81, -199.3) * mm, "end": v(-55.87, -198.86) * mm});
            skPoint(sketch, "E1285.visualSharp", {"position": v(-69.77, -214.26) * mm});
            skArc(sketch, "E1285.filletArc", {"start": v(-69.77, -212.76) * mm, "mid": v(-69.33, -213.82) * mm, "end": v(-68.27, -214.26) * mm});
            skPoint(sketch, "E1286.visualSharp", {"position": v(-54.37, -214.26) * mm});
            skArc(sketch, "E1286.filletArc", {"start": v(-55.87, -214.26) * mm, "mid": v(-54.81, -213.82) * mm, "end": v(-54.37, -212.76) * mm});
            skLineSegment(sketch, "E1287.bottom", {"start": v(-84.77, -141.86) * mm, "end": v(-72.37, -141.86) * mm});
            skLineSegment(sketch, "E1287.top", {"start": v(-84.77, -157.26) * mm, "end": v(-72.37, -157.26) * mm});
            skLineSegment(sketch, "E1287.left", {"start": v(-86.27, -143.36) * mm, "end": v(-86.27, -155.76) * mm});
            skLineSegment(sketch, "E1287.right", {"start": v(-70.87, -143.36) * mm, "end": v(-70.87, -155.76) * mm});
            skPoint(sketch, "E1288.visualSharp", {"position": v(-86.27, -141.86) * mm});
            skArc(sketch, "E1288.filletArc", {"start": v(-84.77, -141.86) * mm, "mid": v(-85.83, -142.3) * mm, "end": v(-86.27, -143.36) * mm});
            skPoint(sketch, "E1289.visualSharp", {"position": v(-70.87, -141.86) * mm});
            skArc(sketch, "E1289.filletArc", {"start": v(-70.87, -143.36) * mm, "mid": v(-71.31, -142.3) * mm, "end": v(-72.37, -141.86) * mm});
            skPoint(sketch, "E1290.visualSharp", {"position": v(-86.27, -157.26) * mm});
            skArc(sketch, "E1290.filletArc", {"start": v(-86.27, -155.76) * mm, "mid": v(-85.83, -156.82) * mm, "end": v(-84.77, -157.26) * mm});
            skPoint(sketch, "E1291.visualSharp", {"position": v(-70.87, -157.26) * mm});
            skArc(sketch, "E1291.filletArc", {"start": v(-72.37, -157.26) * mm, "mid": v(-71.31, -156.82) * mm, "end": v(-70.87, -155.76) * mm});
            skLineSegment(sketch, "E1292.bottom", {"start": v(-84.77, -122.86) * mm, "end": v(-72.37, -122.86) * mm});
            skLineSegment(sketch, "E1292.top", {"start": v(-84.77, -138.26) * mm, "end": v(-72.37, -138.26) * mm});
            skLineSegment(sketch, "E1292.left", {"start": v(-86.27, -124.36) * mm, "end": v(-86.27, -136.76) * mm});
            skLineSegment(sketch, "E1292.right", {"start": v(-70.87, -124.36) * mm, "end": v(-70.87, -136.76) * mm});
            skPoint(sketch, "E1293.visualSharp", {"position": v(-86.27, -122.86) * mm});
            skArc(sketch, "E1293.filletArc", {"start": v(-84.77, -122.86) * mm, "mid": v(-85.83, -123.3) * mm, "end": v(-86.27, -124.36) * mm});
            skPoint(sketch, "E1294.visualSharp", {"position": v(-70.87, -122.86) * mm});
            skArc(sketch, "E1294.filletArc", {"start": v(-70.87, -124.36) * mm, "mid": v(-71.31, -123.3) * mm, "end": v(-72.37, -122.86) * mm});
            skPoint(sketch, "E1295.visualSharp", {"position": v(-86.27, -138.26) * mm});
            skArc(sketch, "E1295.filletArc", {"start": v(-86.27, -136.76) * mm, "mid": v(-85.83, -137.82) * mm, "end": v(-84.77, -138.26) * mm});
            skPoint(sketch, "E1296.visualSharp", {"position": v(-70.87, -138.26) * mm});
            skArc(sketch, "E1296.filletArc", {"start": v(-72.37, -138.26) * mm, "mid": v(-71.31, -137.82) * mm, "end": v(-70.87, -136.76) * mm});
            skLineSegment(sketch, "E1297.bottom", {"start": v(-84.77, -179.86) * mm, "end": v(-72.37, -179.86) * mm});
            skLineSegment(sketch, "E1297.top", {"start": v(-84.77, -195.26) * mm, "end": v(-72.37, -195.26) * mm});
            skLineSegment(sketch, "E1297.left", {"start": v(-86.27, -181.36) * mm, "end": v(-86.27, -193.76) * mm});
            skLineSegment(sketch, "E1297.right", {"start": v(-70.87, -181.36) * mm, "end": v(-70.87, -193.76) * mm});
            skPoint(sketch, "E1298.visualSharp", {"position": v(-86.27, -179.86) * mm});
            skArc(sketch, "E1298.filletArc", {"start": v(-84.77, -179.86) * mm, "mid": v(-85.83, -180.3) * mm, "end": v(-86.27, -181.36) * mm});
            skPoint(sketch, "E1299.visualSharp", {"position": v(-70.87, -179.86) * mm});
            skArc(sketch, "E1299.filletArc", {"start": v(-70.87, -181.36) * mm, "mid": v(-71.31, -180.3) * mm, "end": v(-72.37, -179.86) * mm});
            skPoint(sketch, "E1300.visualSharp", {"position": v(-86.27, -195.26) * mm});
            skArc(sketch, "E1300.filletArc", {"start": v(-86.27, -193.76) * mm, "mid": v(-85.83, -194.82) * mm, "end": v(-84.77, -195.26) * mm});
            skPoint(sketch, "E1301.visualSharp", {"position": v(-70.87, -195.26) * mm});
            skArc(sketch, "E1301.filletArc", {"start": v(-72.37, -195.26) * mm, "mid": v(-71.31, -194.82) * mm, "end": v(-70.87, -193.76) * mm});
            skLineSegment(sketch, "E1302.bottom", {"start": v(-84.77, -160.86) * mm, "end": v(-72.37, -160.86) * mm});
            skLineSegment(sketch, "E1302.top", {"start": v(-84.77, -176.26) * mm, "end": v(-72.37, -176.26) * mm});
            skLineSegment(sketch, "E1302.left", {"start": v(-86.27, -162.36) * mm, "end": v(-86.27, -174.76) * mm});
            skLineSegment(sketch, "E1302.right", {"start": v(-70.87, -162.36) * mm, "end": v(-70.87, -174.76) * mm});
            skPoint(sketch, "E1303.visualSharp", {"position": v(-86.27, -160.86) * mm});
            skArc(sketch, "E1303.filletArc", {"start": v(-84.77, -160.86) * mm, "mid": v(-85.83, -161.3) * mm, "end": v(-86.27, -162.36) * mm});
            skPoint(sketch, "E1304.visualSharp", {"position": v(-70.87, -160.86) * mm});
            skArc(sketch, "E1304.filletArc", {"start": v(-70.87, -162.36) * mm, "mid": v(-71.31, -161.3) * mm, "end": v(-72.37, -160.86) * mm});
            skPoint(sketch, "E1305.visualSharp", {"position": v(-86.27, -176.26) * mm});
            skArc(sketch, "E1305.filletArc", {"start": v(-86.27, -174.76) * mm, "mid": v(-85.83, -175.82) * mm, "end": v(-84.77, -176.26) * mm});
            skPoint(sketch, "E1306.visualSharp", {"position": v(-70.87, -176.26) * mm});
            skArc(sketch, "E1306.filletArc", {"start": v(-72.37, -176.26) * mm, "mid": v(-71.31, -175.82) * mm, "end": v(-70.87, -174.76) * mm});
            skLineSegment(sketch, "E1307.bottom", {"start": v(-84.77, -217.86) * mm, "end": v(-72.37, -217.86) * mm});
            skLineSegment(sketch, "E1307.top", {"start": v(-84.77, -233.26) * mm, "end": v(-72.37, -233.26) * mm});
            skLineSegment(sketch, "E1307.left", {"start": v(-86.27, -219.36) * mm, "end": v(-86.27, -231.76) * mm});
            skLineSegment(sketch, "E1307.right", {"start": v(-70.87, -219.36) * mm, "end": v(-70.87, -231.76) * mm});
            skPoint(sketch, "E1308.visualSharp", {"position": v(-86.27, -217.86) * mm});
            skArc(sketch, "E1308.filletArc", {"start": v(-84.77, -217.86) * mm, "mid": v(-85.83, -218.3) * mm, "end": v(-86.27, -219.36) * mm});
            skPoint(sketch, "E1309.visualSharp", {"position": v(-70.87, -217.86) * mm});
            skArc(sketch, "E1309.filletArc", {"start": v(-70.87, -219.36) * mm, "mid": v(-71.31, -218.3) * mm, "end": v(-72.37, -217.86) * mm});
            skPoint(sketch, "E1310.visualSharp", {"position": v(-86.27, -233.26) * mm});
            skArc(sketch, "E1310.filletArc", {"start": v(-86.27, -231.76) * mm, "mid": v(-85.83, -232.82) * mm, "end": v(-84.77, -233.26) * mm});
            skPoint(sketch, "E1311.visualSharp", {"position": v(-70.87, -233.26) * mm});
            skArc(sketch, "E1311.filletArc", {"start": v(-72.37, -233.26) * mm, "mid": v(-71.31, -232.82) * mm, "end": v(-70.87, -231.76) * mm});
            skLineSegment(sketch, "E1312.bottom", {"start": v(-84.77, -198.86) * mm, "end": v(-72.37, -198.86) * mm});
            skLineSegment(sketch, "E1312.top", {"start": v(-84.77, -214.26) * mm, "end": v(-72.37, -214.26) * mm});
            skLineSegment(sketch, "E1312.left", {"start": v(-86.27, -200.36) * mm, "end": v(-86.27, -212.76) * mm});
            skLineSegment(sketch, "E1312.right", {"start": v(-70.87, -200.36) * mm, "end": v(-70.87, -212.76) * mm});
            skPoint(sketch, "E1313.visualSharp", {"position": v(-86.27, -198.86) * mm});
            skArc(sketch, "E1313.filletArc", {"start": v(-84.77, -198.86) * mm, "mid": v(-85.83, -199.3) * mm, "end": v(-86.27, -200.36) * mm});
            skPoint(sketch, "E1314.visualSharp", {"position": v(-70.87, -198.86) * mm});
            skArc(sketch, "E1314.filletArc", {"start": v(-70.87, -200.36) * mm, "mid": v(-71.31, -199.3) * mm, "end": v(-72.37, -198.86) * mm});
            skPoint(sketch, "E1315.visualSharp", {"position": v(-86.27, -214.26) * mm});
            skArc(sketch, "E1315.filletArc", {"start": v(-86.27, -212.76) * mm, "mid": v(-85.83, -213.82) * mm, "end": v(-84.77, -214.26) * mm});
            skPoint(sketch, "E1316.visualSharp", {"position": v(-70.87, -214.26) * mm});
            skArc(sketch, "E1316.filletArc", {"start": v(-72.37, -214.26) * mm, "mid": v(-71.31, -213.82) * mm, "end": v(-70.87, -212.76) * mm});
            skSolve(sketch);
        }
        {
            var Q0;
            Q0 = qSketchRegion(id + "F37", true);
            extrude(context, id + "F38", {"entities" : qUnion([Q0]), "operationType" : NewBodyOperationType.REMOVE, "oppositeDirection" : true, "depth" : 50 * mm, "offsetDistance" : 25 * mm});
        }
        {
            var Q0;
            Q0=makeQuery(id+"F36.opExtrude","CAP_FACE",FACE,{"disambiguationData":[OSD([sQuery(id+"F35.wireOp",EDGE,"E686.bottom"),sQuery(id+"F35.wireOp",EDGE,"E686.top"),sQuery(id+"F35.wireOp",EDGE,"E686.left"),sQuery(id+"F35.wireOp",EDGE,"E686.right")])],"isStart":false});
            extrude(context, id + "F39", {"entities" : qUnion([Q0]), "operationType" : NewBodyOperationType.REMOVE, "oppositeDirection" : true, "depth" : 10 * mm, "offsetDistance" : 25 * mm});
        }
        {
            var Q0;
            Q0=makeQuery(id+"F39.boolean.opBoolean","COPY",FACE,{"derivedFrom":makeQuery(id+"F39.opExtrude","CAP_FACE",FACE,{"disambiguationData":[OSD([sQuery(id+"F35.wireOp",EDGE,"E686.bottom"),sQuery(id+"F35.wireOp",EDGE,"E686.top"),sQuery(id+"F35.wireOp",EDGE,"E686.left"),sQuery(id+"F35.wireOp",EDGE,"E686.right")])],"isStart":false})});
            var sketch = newSketch(context, id + "F40", { "sketchPlane" : qUnion([Q0])});
            skLineSegment(sketch, "E1317.bottom", {"start": v(-181.07, 252.06) * mm, "end": v(188.93, 252.06) * mm});
            skLineSegment(sketch, "E1317.top", {"start": v(-181.07, 94.06) * mm, "end": v(188.93, 94.06) * mm});
            skLineSegment(sketch, "E1317.left", {"start": v(-181.07, 252.06) * mm, "end": v(-181.07, 94.06) * mm});
            skLineSegment(sketch, "E1317.right", {"start": v(188.93, 252.06) * mm, "end": v(188.93, 94.06) * mm});
            skSolve(sketch);
        }
        {
            var Q0;
            Q0=makeQuery(id+"F4.opExtrude","CAP_FACE",FACE,{"disambiguationData":[OSD([sQuery(id+"F2.wireOp",EDGE,"E632.bottom"),sQuery(id+"F2.wireOp",EDGE,"E632.top"),sQuery(id+"F2.wireOp",EDGE,"E632.left"),sQuery(id+"F2.wireOp",EDGE,"E632.right")])],"isStart":false});
            var sketch = newSketch(context, id + "F41", { "sketchPlane" : qUnion([Q0])});
            skCircle(sketch, "E1318", {"center": v(-161.07, -130.56) * mm, "radius": 3.5 * mm});
            skCircle(sketch, "E1319", {"center": v(-144.57, -130.56) * mm, "radius": 3.5 * mm});
            skCircle(sketch, "E1320", {"center": v(-128.07, -130.56) * mm, "radius": 3.5 * mm});
            skCircle(sketch, "E1321", {"center": v(-111.57, -130.56) * mm, "radius": 3.5 * mm});
            skCircle(sketch, "E1322", {"center": v(-95.07, -130.56) * mm, "radius": 3.5 * mm});
            skCircle(sketch, "E1323", {"center": v(-78.57, -130.56) * mm, "radius": 3.5 * mm});
            skCircle(sketch, "E1324", {"center": v(-62.07, -130.56) * mm, "radius": 3.5 * mm});
            skCircle(sketch, "E1325", {"center": v(-45.57, -130.56) * mm, "radius": 3.5 * mm});
            skCircle(sketch, "E1326", {"center": v(-29.07, -130.56) * mm, "radius": 3.5 * mm});
            skCircle(sketch, "E1327", {"center": v(-12.57, -130.56) * mm, "radius": 3.5 * mm});
            skCircle(sketch, "E1328", {"center": v(3.93, -130.56) * mm, "radius": 3.5 * mm});
            skCircle(sketch, "E1329", {"center": v(20.43, -130.56) * mm, "radius": 3.5 * mm});
            skCircle(sketch, "E1330", {"center": v(36.93, -130.56) * mm, "radius": 3.5 * mm});
            skCircle(sketch, "E1331", {"center": v(53.43, -130.56) * mm, "radius": 3.5 * mm});
            skCircle(sketch, "E1332", {"center": v(69.93, -130.56) * mm, "radius": 3.5 * mm});
            skCircle(sketch, "E1333", {"center": v(86.43, -130.56) * mm, "radius": 3.5 * mm});
            skCircle(sketch, "E1334", {"center": v(102.93, -130.56) * mm, "radius": 3.5 * mm});
            skCircle(sketch, "E1335", {"center": v(119.43, -130.56) * mm, "radius": 3.5 * mm});
            skCircle(sketch, "E1336", {"center": v(135.93, -130.56) * mm, "radius": 3.5 * mm});
            skCircle(sketch, "E1337", {"center": v(152.43, -130.56) * mm, "radius": 3.5 * mm});
            skCircle(sketch, "E1338", {"center": v(168.93, -130.56) * mm, "radius": 3.5 * mm});
            skCircle(sketch, "E1339", {"center": v(-161.07, -149.56) * mm, "radius": 3.5 * mm});
            skCircle(sketch, "E1340", {"center": v(-144.57, -149.56) * mm, "radius": 3.5 * mm});
            skCircle(sketch, "E1341", {"center": v(-128.07, -149.56) * mm, "radius": 3.5 * mm});
            skCircle(sketch, "E1342", {"center": v(-111.57, -149.56) * mm, "radius": 3.5 * mm});
            skCircle(sketch, "E1343", {"center": v(-95.07, -149.56) * mm, "radius": 3.5 * mm});
            skCircle(sketch, "E1344", {"center": v(-78.57, -149.56) * mm, "radius": 3.5 * mm});
            skCircle(sketch, "E1345", {"center": v(-62.07, -149.56) * mm, "radius": 3.5 * mm});
            skCircle(sketch, "E1346", {"center": v(-45.57, -149.56) * mm, "radius": 3.5 * mm});
            skCircle(sketch, "E1347", {"center": v(-29.07, -149.56) * mm, "radius": 3.5 * mm});
            skCircle(sketch, "E1348", {"center": v(-12.57, -149.56) * mm, "radius": 3.5 * mm});
            skCircle(sketch, "E1349", {"center": v(3.93, -149.56) * mm, "radius": 3.5 * mm});
            skCircle(sketch, "E1350", {"center": v(20.43, -149.56) * mm, "radius": 3.5 * mm});
            skCircle(sketch, "E1351", {"center": v(36.93, -149.56) * mm, "radius": 3.5 * mm});
            skCircle(sketch, "E1352", {"center": v(53.43, -149.56) * mm, "radius": 3.5 * mm});
            skCircle(sketch, "E1353", {"center": v(69.93, -149.56) * mm, "radius": 3.5 * mm});
            skCircle(sketch, "E1354", {"center": v(86.43, -149.56) * mm, "radius": 3.5 * mm});
            skCircle(sketch, "E1355", {"center": v(102.93, -149.56) * mm, "radius": 3.5 * mm});
            skCircle(sketch, "E1356", {"center": v(119.43, -149.56) * mm, "radius": 3.5 * mm});
            skCircle(sketch, "E1357", {"center": v(135.93, -149.56) * mm, "radius": 3.5 * mm});
            skCircle(sketch, "E1358", {"center": v(152.43, -149.56) * mm, "radius": 3.5 * mm});
            skCircle(sketch, "E1359", {"center": v(168.93, -149.56) * mm, "radius": 3.5 * mm});
            skCircle(sketch, "E1360", {"center": v(-161.07, -168.56) * mm, "radius": 3.5 * mm});
            skCircle(sketch, "E1361", {"center": v(-144.57, -168.56) * mm, "radius": 3.5 * mm});
            skCircle(sketch, "E1362", {"center": v(-128.07, -168.56) * mm, "radius": 3.5 * mm});
            skCircle(sketch, "E1363", {"center": v(-111.57, -168.56) * mm, "radius": 3.5 * mm});
            skCircle(sketch, "E1364", {"center": v(-95.07, -168.56) * mm, "radius": 3.5 * mm});
            skCircle(sketch, "E1365", {"center": v(-78.57, -168.56) * mm, "radius": 3.5 * mm});
            skCircle(sketch, "E1366", {"center": v(-62.07, -168.56) * mm, "radius": 3.5 * mm});
            skCircle(sketch, "E1367", {"center": v(-45.57, -168.56) * mm, "radius": 3.5 * mm});
            skCircle(sketch, "E1368", {"center": v(-29.07, -168.56) * mm, "radius": 3.5 * mm});
            skCircle(sketch, "E1369", {"center": v(-12.57, -168.56) * mm, "radius": 3.5 * mm});
            skCircle(sketch, "E1370", {"center": v(3.93, -168.56) * mm, "radius": 3.5 * mm});
            skCircle(sketch, "E1371", {"center": v(20.43, -168.56) * mm, "radius": 3.5 * mm});
            skCircle(sketch, "E1372", {"center": v(36.93, -168.56) * mm, "radius": 3.5 * mm});
            skCircle(sketch, "E1373", {"center": v(53.43, -168.56) * mm, "radius": 3.5 * mm});
            skCircle(sketch, "E1374", {"center": v(69.93, -168.56) * mm, "radius": 3.5 * mm});
            skCircle(sketch, "E1375", {"center": v(86.43, -168.56) * mm, "radius": 3.5 * mm});
            skCircle(sketch, "E1376", {"center": v(102.93, -168.56) * mm, "radius": 3.5 * mm});
            skCircle(sketch, "E1377", {"center": v(119.43, -168.56) * mm, "radius": 3.5 * mm});
            skCircle(sketch, "E1378", {"center": v(135.93, -168.56) * mm, "radius": 3.5 * mm});
            skCircle(sketch, "E1379", {"center": v(152.43, -168.56) * mm, "radius": 3.5 * mm});
            skCircle(sketch, "E1380", {"center": v(168.93, -168.56) * mm, "radius": 3.5 * mm});
            skCircle(sketch, "E1381", {"center": v(-161.07, -187.56) * mm, "radius": 3.5 * mm});
            skCircle(sketch, "E1382", {"center": v(-144.57, -187.56) * mm, "radius": 3.5 * mm});
            skCircle(sketch, "E1383", {"center": v(-128.07, -187.56) * mm, "radius": 3.5 * mm});
            skCircle(sketch, "E1384", {"center": v(-111.57, -187.56) * mm, "radius": 3.5 * mm});
            skCircle(sketch, "E1385", {"center": v(-95.07, -187.56) * mm, "radius": 3.5 * mm});
            skCircle(sketch, "E1386", {"center": v(-78.57, -187.56) * mm, "radius": 3.5 * mm});
            skCircle(sketch, "E1387", {"center": v(-62.07, -187.56) * mm, "radius": 3.5 * mm});
            skCircle(sketch, "E1388", {"center": v(-45.57, -187.56) * mm, "radius": 3.5 * mm});
            skCircle(sketch, "E1389", {"center": v(-29.07, -187.56) * mm, "radius": 3.5 * mm});
            skCircle(sketch, "E1390", {"center": v(-12.57, -187.56) * mm, "radius": 3.5 * mm});
            skCircle(sketch, "E1391", {"center": v(3.93, -187.56) * mm, "radius": 3.5 * mm});
            skCircle(sketch, "E1392", {"center": v(20.43, -187.56) * mm, "radius": 3.5 * mm});
            skCircle(sketch, "E1393", {"center": v(36.93, -187.56) * mm, "radius": 3.5 * mm});
            skCircle(sketch, "E1394", {"center": v(53.43, -187.56) * mm, "radius": 3.5 * mm});
            skCircle(sketch, "E1395", {"center": v(69.93, -187.56) * mm, "radius": 3.5 * mm});
            skCircle(sketch, "E1396", {"center": v(86.43, -187.56) * mm, "radius": 3.5 * mm});
            skCircle(sketch, "E1397", {"center": v(102.93, -187.56) * mm, "radius": 3.5 * mm});
            skCircle(sketch, "E1398", {"center": v(119.43, -187.56) * mm, "radius": 3.5 * mm});
            skCircle(sketch, "E1399", {"center": v(135.93, -187.56) * mm, "radius": 3.5 * mm});
            skCircle(sketch, "E1400", {"center": v(152.43, -187.56) * mm, "radius": 3.5 * mm});
            skCircle(sketch, "E1401", {"center": v(168.93, -187.56) * mm, "radius": 3.5 * mm});
            skCircle(sketch, "E1402", {"center": v(-161.07, -206.56) * mm, "radius": 3.5 * mm});
            skCircle(sketch, "E1403", {"center": v(-144.57, -206.56) * mm, "radius": 3.5 * mm});
            skCircle(sketch, "E1404", {"center": v(-128.07, -206.56) * mm, "radius": 3.5 * mm});
            skCircle(sketch, "E1405", {"center": v(-111.57, -206.56) * mm, "radius": 3.5 * mm});
            skCircle(sketch, "E1406", {"center": v(-95.07, -206.56) * mm, "radius": 3.5 * mm});
            skCircle(sketch, "E1407", {"center": v(-78.57, -206.56) * mm, "radius": 3.5 * mm});
            skCircle(sketch, "E1408", {"center": v(-62.07, -206.56) * mm, "radius": 3.5 * mm});
            skCircle(sketch, "E1409", {"center": v(-45.57, -206.56) * mm, "radius": 3.5 * mm});
            skCircle(sketch, "E1410", {"center": v(-29.07, -206.56) * mm, "radius": 3.5 * mm});
            skCircle(sketch, "E1411", {"center": v(-12.57, -206.56) * mm, "radius": 3.5 * mm});
            skCircle(sketch, "E1412", {"center": v(3.93, -206.56) * mm, "radius": 3.5 * mm});
            skCircle(sketch, "E1413", {"center": v(20.43, -206.56) * mm, "radius": 3.5 * mm});
            skCircle(sketch, "E1414", {"center": v(36.93, -206.56) * mm, "radius": 3.5 * mm});
            skCircle(sketch, "E1415", {"center": v(53.43, -206.56) * mm, "radius": 3.5 * mm});
            skCircle(sketch, "E1416", {"center": v(69.93, -206.56) * mm, "radius": 3.5 * mm});
            skCircle(sketch, "E1417", {"center": v(86.43, -206.56) * mm, "radius": 3.5 * mm});
            skCircle(sketch, "E1418", {"center": v(102.93, -206.56) * mm, "radius": 3.5 * mm});
            skCircle(sketch, "E1419", {"center": v(119.43, -206.56) * mm, "radius": 3.5 * mm});
            skCircle(sketch, "E1420", {"center": v(135.93, -206.56) * mm, "radius": 3.5 * mm});
            skCircle(sketch, "E1421", {"center": v(152.43, -206.56) * mm, "radius": 3.5 * mm});
            skCircle(sketch, "E1422", {"center": v(168.93, -206.56) * mm, "radius": 3.5 * mm});
            skCircle(sketch, "E1423", {"center": v(-161.07, -225.56) * mm, "radius": 3.5 * mm});
            skCircle(sketch, "E1424", {"center": v(-144.57, -225.56) * mm, "radius": 3.5 * mm});
            skCircle(sketch, "E1425", {"center": v(-128.07, -225.56) * mm, "radius": 3.5 * mm});
            skCircle(sketch, "E1426", {"center": v(-111.57, -225.56) * mm, "radius": 3.5 * mm});
            skCircle(sketch, "E1427", {"center": v(-95.07, -225.56) * mm, "radius": 3.5 * mm});
            skCircle(sketch, "E1428", {"center": v(-78.57, -225.56) * mm, "radius": 3.5 * mm});
            skCircle(sketch, "E1429", {"center": v(-62.07, -225.56) * mm, "radius": 3.5 * mm});
            skCircle(sketch, "E1430", {"center": v(-45.57, -225.56) * mm, "radius": 3.5 * mm});
            skCircle(sketch, "E1431", {"center": v(-29.07, -225.56) * mm, "radius": 3.5 * mm});
            skCircle(sketch, "E1432", {"center": v(-12.57, -225.56) * mm, "radius": 3.5 * mm});
            skCircle(sketch, "E1433", {"center": v(3.93, -225.56) * mm, "radius": 3.5 * mm});
            skCircle(sketch, "E1434", {"center": v(20.43, -225.56) * mm, "radius": 3.5 * mm});
            skCircle(sketch, "E1435", {"center": v(36.93, -225.56) * mm, "radius": 3.5 * mm});
            skCircle(sketch, "E1436", {"center": v(53.43, -225.56) * mm, "radius": 3.5 * mm});
            skCircle(sketch, "E1437", {"center": v(69.93, -225.56) * mm, "radius": 3.5 * mm});
            skCircle(sketch, "E1438", {"center": v(86.43, -225.56) * mm, "radius": 3.5 * mm});
            skCircle(sketch, "E1439", {"center": v(102.93, -225.56) * mm, "radius": 3.5 * mm});
            skCircle(sketch, "E1440", {"center": v(119.43, -225.56) * mm, "radius": 3.5 * mm});
            skCircle(sketch, "E1441", {"center": v(135.93, -225.56) * mm, "radius": 3.5 * mm});
            skCircle(sketch, "E1442", {"center": v(152.43, -225.56) * mm, "radius": 3.5 * mm});
            skCircle(sketch, "E1443", {"center": v(168.93, -225.56) * mm, "radius": 3.5 * mm});
            skSolve(sketch);
        }
        {
            var Q0;
            Q0 = qSketchRegion(id + "F40", true);
            extrude(context, id + "F42", {"entities" : qUnion([Q0]), "depth" : 4 * mm, "offsetDistance" : 25 * mm});
        }
        {
            var Q0;
            Q0 = qSketchRegion(id + "F41", true);
            extrude(context, id + "F43", {"entities" : qUnion([Q0]), "operationType" : NewBodyOperationType.REMOVE, "oppositeDirection" : true, "depth" : 50 * mm, "offsetDistance" : 25 * mm});
        }
        {
            var Q0;
            Q0=makeQuery(id+"F4.opExtrude","CAP_EDGE",EDGE,{"disambiguationData":[OSD([sQuery(id+"F2.wireOp",EDGE,"E632.top")])],"isStart":false});
            var Q1;
            Q1=makeQuery(id+"F4.opExtrude","CAP_EDGE",EDGE,{"disambiguationData":[OSD([sQuery(id+"F2.wireOp",EDGE,"E632.left")])],"isStart":false});
            var Q2;
            Q2=makeQuery(id+"F4.opExtrude","CAP_EDGE",EDGE,{"disambiguationData":[OSD([sQuery(id+"F2.wireOp",EDGE,"E632.right")])],"isStart":false});
            var Q3;
            Q3=makeQuery(id+"F4.opExtrude","CAP_EDGE",EDGE,{"disambiguationData":[OSD([sQuery(id+"F2.wireOp",EDGE,"E632.bottom")])],"isStart":false});
            fillet(context, id + "F44", {"entities" : qUnion([Q0, Q1, Q2, Q3]), "radius" : 1 * mm, "tangentPropagation" : true, "allowEdgeOverflow" : false});
        }
        {
            var Q0;
            Q0=makeQuery(id+"F4.opExtrude","CAP_FACE",FACE,{"disambiguationData":[OSD([sQuery(id+"F2.wireOp",EDGE,"E632.bottom"),sQuery(id+"F2.wireOp",EDGE,"E632.top"),sQuery(id+"F2.wireOp",EDGE,"E632.left"),sQuery(id+"F2.wireOp",EDGE,"E632.right")])],"isStart":false});
            var sketch = newSketch(context, id + "F45", { "sketchPlane" : qUnion([Q0])});
            skCircle(sketch, "E1444", {"center": v(-146.07, -243.06) * mm, "radius": 2.5 * mm});
            skCircle(sketch, "E1445", {"center": v(153.93, -243.06) * mm, "radius": 2.5 * mm});
            skCircle(sketch, "E1446", {"center": v(-46.07, -243.06) * mm, "radius": 2.5 * mm});
            skCircle(sketch, "E1447", {"center": v(53.93, -243.06) * mm, "radius": 2.5 * mm});
            skCircle(sketch, "E1448", {"center": v(-146.07, -113.06) * mm, "radius": 2.5 * mm});
            skCircle(sketch, "E1449", {"center": v(-46.07, -113.06) * mm, "radius": 2.5 * mm});
            skCircle(sketch, "E1450", {"center": v(53.93, -113.06) * mm, "radius": 2.5 * mm});
            skCircle(sketch, "E1451", {"center": v(153.93, -113.06) * mm, "radius": 2.5 * mm});
            skSolve(sketch);
        }
        {
            var Q0;
            Q0 = qSketchRegion(id + "F45", true);
            extrude(context, id + "F46", {"entities" : qUnion([Q0]), "operationType" : NewBodyOperationType.REMOVE, "oppositeDirection" : true, "depth" : 50 * mm, "offsetDistance" : 25 * mm});
        }
        {
            var Q0;
            Q0=makeQuery(id+"F4.opExtrude","CAP_FACE",FACE,{"disambiguationData":[OSD([sQuery(id+"F2.wireOp",EDGE,"E632.bottom"),sQuery(id+"F2.wireOp",EDGE,"E632.top"),sQuery(id+"F2.wireOp",EDGE,"E632.left"),sQuery(id+"F2.wireOp",EDGE,"E632.right")])],"isStart":false});
            var sketch = newSketch(context, id + "F47", { "sketchPlane" : qUnion([Q0])});
            skCircle(sketch, "E1452", {"center": v(-146.07, -243.06) * mm, "radius": 2.05 * mm});
            skCircle(sketch, "E1453", {"center": v(-46.07, -243.06) * mm, "radius": 2.05 * mm});
            skCircle(sketch, "E1454", {"center": v(53.93, -243.06) * mm, "radius": 2.05 * mm});
            skCircle(sketch, "E1455", {"center": v(153.93, -243.06) * mm, "radius": 2.05 * mm});
            skCircle(sketch, "E1456", {"center": v(-146.07, -113.06) * mm, "radius": 2.05 * mm});
            skCircle(sketch, "E1457", {"center": v(-46.07, -113.06) * mm, "radius": 2.05 * mm});
            skCircle(sketch, "E1458", {"center": v(53.93, -113.06) * mm, "radius": 2.05 * mm});
            skCircle(sketch, "E1459", {"center": v(153.93, -113.06) * mm, "radius": 2.05 * mm});
            skSolve(sketch);
        }
        {
            var Q0;
            Q0 = qSketchRegion(id + "F47", true);
            extrude(context, id + "F48", {"entities" : qUnion([Q0]), "operationType" : NewBodyOperationType.REMOVE, "oppositeDirection" : true, "depth" : 40 * mm, "offsetDistance" : 25 * mm});
        }
        {
            var Q0;
            Q0=makeQuery(id+"F36.opExtrude","SWEPT_FACE",FACE,{"disambiguationData":[OSD([sQuery(id+"F35.wireOp",EDGE,"E686.left")])]});
            var sketch = newSketch(context, id + "F49", { "sketchPlane" : qUnion([Q0])});
            skCircle(sketch, "E1460", {"center": v(124.06, -23) * mm, "radius": 2.05 * mm});
            skCircle(sketch, "E1461", {"center": v(222.06, -23) * mm, "radius": 2.05 * mm});
            skCircle(sketch, "E1462", {"center": v(169.06, -23) * mm, "radius": 2.05 * mm});
            skSolve(sketch);
        }
        {
            var Q0;
            Q0=makeQuery(id+"F36.opExtrude","SWEPT_FACE",FACE,{"disambiguationData":[OSD([sQuery(id+"F35.wireOp",EDGE,"E686.right")])]});
            var sketch = newSketch(context, id + "F50", { "sketchPlane" : qUnion([Q0])});
            skCircle(sketch, "E1463", {"center": v(-222.06, -23) * mm, "radius": 2.05 * mm});
            skCircle(sketch, "E1464", {"center": v(-124.06, -23) * mm, "radius": 2.05 * mm});
            skCircle(sketch, "E1465", {"center": v(-169.06, -23) * mm, "radius": 2.05 * mm});
            skSolve(sketch);
        }
        {
            var Q0;
            Q0 = qSketchRegion(id + "F49", true);
            extrude(context, id + "F51", {"entities" : qUnion([Q0]), "operationType" : NewBodyOperationType.REMOVE, "oppositeDirection" : true, "depth" : 10 * mm, "offsetDistance" : 25 * mm});
        }
        {
            var Q0;
            Q0 = qSketchRegion(id + "F50", true);
            extrude(context, id + "F52", {"entities" : qUnion([Q0]), "operationType" : NewBodyOperationType.REMOVE, "oppositeDirection" : true, "depth" : 10 * mm, "offsetDistance" : 25 * mm});
        }
        {
            var Q0;
            Q0=makeQuery(id+"F34.imprint","IMPRINT",FACE,{"disambiguationData":[TD([[makeQuery(id+"F34.imprint","IMPRINT",EDGE,{"derivedFrom":makeQuery(id+"F33.opExtrude","CAP_EDGE",EDGE,{"disambiguationData":[OSD([sQuery(id+"F32.wireOp",EDGE,"E676.bottom")])],"isStart":false})}),-1.0]])]});
            var sketch = newSketch(context, id + "F53", { "sketchPlane" : qUnion([Q0])});
            skLineSegment(sketch, "E1466.bottom", {"start": v(-100.77, 156.76) * mm, "end": v(-89.37, 156.76) * mm});
            skLineSegment(sketch, "E1466.top", {"start": v(-100.77, 142.36) * mm, "end": v(-89.37, 142.36) * mm});
            skLineSegment(sketch, "E1466.left", {"start": v(-102.27, 155.26) * mm, "end": v(-102.27, 143.86) * mm});
            skLineSegment(sketch, "E1466.right", {"start": v(-87.87, 155.26) * mm, "end": v(-87.87, 143.86) * mm});
            skPoint(sketch, "E1467.visualSharp", {"position": v(-102.27, 156.76) * mm});
            skArc(sketch, "E1467.filletArc", {"start": v(-100.77, 156.76) * mm, "mid": v(-101.83, 156.32) * mm, "end": v(-102.27, 155.26) * mm});
            skPoint(sketch, "E1468.visualSharp", {"position": v(-87.87, 156.76) * mm});
            skArc(sketch, "E1468.filletArc", {"start": v(-87.87, 155.26) * mm, "mid": v(-88.31, 156.32) * mm, "end": v(-89.37, 156.76) * mm});
            skPoint(sketch, "E1469.visualSharp", {"position": v(-102.27, 142.36) * mm});
            skArc(sketch, "E1469.filletArc", {"start": v(-102.27, 143.86) * mm, "mid": v(-101.83, 142.8) * mm, "end": v(-100.77, 142.36) * mm});
            skPoint(sketch, "E1470.visualSharp", {"position": v(-87.87, 142.36) * mm});
            skArc(sketch, "E1470.filletArc", {"start": v(-89.37, 142.36) * mm, "mid": v(-88.31, 142.8) * mm, "end": v(-87.87, 143.86) * mm});
            skSolve(sketch);
        }
        {
            var Q0;
            Q0 = qSketchRegion(id + "F53", true);
            extrude(context, id + "F54", {"entities" : qUnion([Q0]), "operationType" : NewBodyOperationType.ADD, "depth" : 2 * mm, "offsetDistance" : 25 * mm});
        }
        {
            var Q0;
            Q0=makeQuery(id+"F54.opExtrude","CAP_FACE",FACE,{"disambiguationData":[OSD([sQuery(id+"F53.wireOp",EDGE,"E1466.bottom"),sQuery(id+"F53.wireOp",EDGE,"E1466.top"),sQuery(id+"F53.wireOp",EDGE,"E1466.left"),sQuery(id+"F53.wireOp",EDGE,"E1466.right"),sQuery(id+"F53.wireOp",EDGE,"E1467.filletArc"),sQuery(id+"F53.wireOp",EDGE,"E1468.filletArc"),sQuery(id+"F53.wireOp",EDGE,"E1469.filletArc"),sQuery(id+"F53.wireOp",EDGE,"E1470.filletArc")])],"isStart":false});
            var sketch = newSketch(context, id + "F55", { "sketchPlane" : qUnion([Q0])});
            skCircle(sketch, "E1471", {"center": v(-95.07, 152.26) * mm, "radius": 1 * mm});
            skSolve(sketch);
        }
        {
            var Q0;
            Q0 = qSketchRegion(id + "F55", true);
            extrude(context, id + "F56", {"entities" : qUnion([Q0]), "operationType" : NewBodyOperationType.REMOVE, "oppositeDirection" : true, "depth" : 25 * mm, "offsetDistance" : 25 * mm});
        }
        {
            var Q0;
            Q0=makeQuery(id+"F42.opExtrude","CAP_FACE",FACE,{"disambiguationData":[OSD([sQuery(id+"F40.wireOp",EDGE,"E1317.bottom"),sQuery(id+"F40.wireOp",EDGE,"E1317.top"),sQuery(id+"F40.wireOp",EDGE,"E1317.left"),sQuery(id+"F40.wireOp",EDGE,"E1317.right")])],"isStart":false});
            var sketch = newSketch(context, id + "F57", { "sketchPlane" : qUnion([Q0])});
            skCircle(sketch, "E1472", {"center": v(-101.2, 155.98) * mm, "radius": 1 * mm});
            skCircle(sketch, "E1473", {"center": v(-101.25, 137.13) * mm, "radius": 1 * mm});
            skCircle(sketch, "E1474", {"center": v(-101.44, 175.11) * mm, "radius": 1 * mm});
            skCircle(sketch, "E1475", {"center": v(-101.1, 194.13) * mm, "radius": 1 * mm});
            skCircle(sketch, "E1476", {"center": v(-100.44, 231.3) * mm, "radius": 1 * mm});
            skCircle(sketch, "E1477", {"center": v(-101.46, 212.8) * mm, "radius": 1 * mm});
            skCircle(sketch, "E1478", {"center": v(-117.57, 155.62) * mm, "radius": 1 * mm});
            skCircle(sketch, "E1479", {"center": v(-117.62, 136.76) * mm, "radius": 1 * mm});
            skCircle(sketch, "E1480", {"center": v(-117.8, 174.75) * mm, "radius": 1 * mm});
            skCircle(sketch, "E1481", {"center": v(-117.47, 193.76) * mm, "radius": 1 * mm});
            skCircle(sketch, "E1482", {"center": v(-117.43, 231.63) * mm, "radius": 1 * mm});
            skCircle(sketch, "E1483", {"center": v(-117.83, 212.44) * mm, "radius": 1 * mm});
            skCircle(sketch, "E1484", {"center": v(-133.45, 155.65) * mm, "radius": 1 * mm});
            skCircle(sketch, "E1485", {"center": v(-133.5, 136.8) * mm, "radius": 1 * mm});
            skCircle(sketch, "E1486", {"center": v(-133.68, 174.78) * mm, "radius": 1 * mm});
            skCircle(sketch, "E1487", {"center": v(-133.35, 193.8) * mm, "radius": 1 * mm});
            skCircle(sketch, "E1488", {"center": v(-133.3, 231.67) * mm, "radius": 1 * mm});
            skCircle(sketch, "E1489", {"center": v(-133.7, 212.48) * mm, "radius": 1 * mm});
            skCircle(sketch, "E1490", {"center": v(-149.82, 155.29) * mm, "radius": 1 * mm});
            skCircle(sketch, "E1491", {"center": v(-149.86, 136.43) * mm, "radius": 1 * mm});
            skCircle(sketch, "E1492", {"center": v(-150.05, 174.42) * mm, "radius": 1 * mm});
            skCircle(sketch, "E1493", {"center": v(-149.72, 193.43) * mm, "radius": 1 * mm});
            skCircle(sketch, "E1494", {"center": v(-149.67, 231.3) * mm, "radius": 1 * mm});
            skCircle(sketch, "E1495", {"center": v(-150.07, 212.1) * mm, "radius": 1 * mm});
            skCircle(sketch, "E1496", {"center": v(-166.9, 155.09) * mm, "radius": 1 * mm});
            skCircle(sketch, "E1497", {"center": v(-166.18, 136.06) * mm, "radius": 1 * mm});
            skCircle(sketch, "E1498", {"center": v(-166.36, 174.07) * mm, "radius": 1 * mm});
            skCircle(sketch, "E1499", {"center": v(-166.38, 193.07) * mm, "radius": 1 * mm});
            skCircle(sketch, "E1500", {"center": v(-166.76, 231.03) * mm, "radius": 1 * mm});
            skCircle(sketch, "E1501", {"center": v(-166.7, 212.08) * mm, "radius": 1 * mm});
            skCircle(sketch, "E1502", {"center": v(163.1, 155.98) * mm, "radius": 1 * mm});
            skCircle(sketch, "E1503", {"center": v(163.06, 137.12) * mm, "radius": 1 * mm});
            skCircle(sketch, "E1504", {"center": v(162.87, 175.11) * mm, "radius": 1 * mm});
            skCircle(sketch, "E1505", {"center": v(163.2, 194.12) * mm, "radius": 1 * mm});
            skCircle(sketch, "E1506", {"center": v(163.25, 232) * mm, "radius": 1 * mm});
            skCircle(sketch, "E1507", {"center": v(162.85, 212.8) * mm, "radius": 1 * mm});
            skCircle(sketch, "E1508", {"center": v(146.74, 155.61) * mm, "radius": 1 * mm});
            skCircle(sketch, "E1509", {"center": v(146.7, 136.76) * mm, "radius": 1 * mm});
            skCircle(sketch, "E1510", {"center": v(146.5, 174.74) * mm, "radius": 1 * mm});
            skCircle(sketch, "E1511", {"center": v(146.84, 193.76) * mm, "radius": 1 * mm});
            skCircle(sketch, "E1512", {"center": v(146.89, 231.63) * mm, "radius": 1 * mm});
            skCircle(sketch, "E1513", {"center": v(146.48, 212.44) * mm, "radius": 1 * mm});
            skCircle(sketch, "E1514", {"center": v(130.86, 155.65) * mm, "radius": 1 * mm});
            skCircle(sketch, "E1515", {"center": v(130.81, 136.8) * mm, "radius": 1 * mm});
            skCircle(sketch, "E1516", {"center": v(130.63, 174.78) * mm, "radius": 1 * mm});
            skCircle(sketch, "E1517", {"center": v(130.96, 193.8) * mm, "radius": 1 * mm});
            skCircle(sketch, "E1518", {"center": v(131, 231.67) * mm, "radius": 1 * mm});
            skCircle(sketch, "E1519", {"center": v(130.6, 212.47) * mm, "radius": 1 * mm});
            skCircle(sketch, "E1520", {"center": v(114.5, 155.28) * mm, "radius": 1 * mm});
            skCircle(sketch, "E1521", {"center": v(114.45, 136.43) * mm, "radius": 1 * mm});
            skCircle(sketch, "E1522", {"center": v(114.26, 174.41) * mm, "radius": 1 * mm});
            skCircle(sketch, "E1523", {"center": v(114.6, 193.43) * mm, "radius": 1 * mm});
            skCircle(sketch, "E1524", {"center": v(114.64, 231.3) * mm, "radius": 1 * mm});
            skCircle(sketch, "E1525", {"center": v(114.24, 212.1) * mm, "radius": 1 * mm});
            skCircle(sketch, "E1526", {"center": v(97.6, 155.39) * mm, "radius": 1 * mm});
            skCircle(sketch, "E1527", {"center": v(97.56, 136.53) * mm, "radius": 1 * mm});
            skCircle(sketch, "E1528", {"center": v(97.38, 174.52) * mm, "radius": 1 * mm});
            skCircle(sketch, "E1529", {"center": v(97.7, 193.53) * mm, "radius": 1 * mm});
            skCircle(sketch, "E1530", {"center": v(97.76, 231.4) * mm, "radius": 1 * mm});
            skCircle(sketch, "E1531", {"center": v(97.35, 212.21) * mm, "radius": 1 * mm});
            skCircle(sketch, "E1532", {"center": v(80.27, 156) * mm, "radius": 1 * mm});
            skCircle(sketch, "E1533", {"center": v(80.23, 137.14) * mm, "radius": 1 * mm});
            skCircle(sketch, "E1534", {"center": v(80.04, 175.12) * mm, "radius": 1 * mm});
            skCircle(sketch, "E1535", {"center": v(80.37, 194.14) * mm, "radius": 1 * mm});
            skCircle(sketch, "E1536", {"center": v(80.42, 232.01) * mm, "radius": 1 * mm});
            skCircle(sketch, "E1537", {"center": v(80.02, 212.82) * mm, "radius": 1 * mm});
            skCircle(sketch, "E1538", {"center": v(63.9, 155.63) * mm, "radius": 1 * mm});
            skCircle(sketch, "E1539", {"center": v(63.86, 136.77) * mm, "radius": 1 * mm});
            skCircle(sketch, "E1540", {"center": v(63.67, 174.76) * mm, "radius": 1 * mm});
            skCircle(sketch, "E1541", {"center": v(64, 193.77) * mm, "radius": 1 * mm});
            skCircle(sketch, "E1542", {"center": v(64.05, 231.65) * mm, "radius": 1 * mm});
            skCircle(sketch, "E1543", {"center": v(63.65, 212.45) * mm, "radius": 1 * mm});
            skCircle(sketch, "E1544", {"center": v(48.03, 155.66) * mm, "radius": 1 * mm});
            skCircle(sketch, "E1545", {"center": v(47.98, 136.8) * mm, "radius": 1 * mm});
            skCircle(sketch, "E1546", {"center": v(47.8, 174.8) * mm, "radius": 1 * mm});
            skCircle(sketch, "E1547", {"center": v(48.13, 193.8) * mm, "radius": 1 * mm});
            skCircle(sketch, "E1548", {"center": v(48.18, 231.68) * mm, "radius": 1 * mm});
            skCircle(sketch, "E1549", {"center": v(47.77, 212.49) * mm, "radius": 1 * mm});
            skCircle(sketch, "E1550", {"center": v(31.66, 155.3) * mm, "radius": 1 * mm});
            skCircle(sketch, "E1551", {"center": v(31.62, 136.44) * mm, "radius": 1 * mm});
            skCircle(sketch, "E1552", {"center": v(31.43, 174.43) * mm, "radius": 1 * mm});
            skCircle(sketch, "E1553", {"center": v(31.76, 193.44) * mm, "radius": 1 * mm});
            skCircle(sketch, "E1554", {"center": v(31.8, 231.32) * mm, "radius": 1 * mm});
            skCircle(sketch, "E1555", {"center": v(31.4, 212.12) * mm, "radius": 1 * mm});
            skCircle(sketch, "E1556", {"center": v(14.77, 155.4) * mm, "radius": 1 * mm});
            skCircle(sketch, "E1557", {"center": v(14.73, 136.54) * mm, "radius": 1 * mm});
            skCircle(sketch, "E1558", {"center": v(14.54, 174.53) * mm, "radius": 1 * mm});
            skCircle(sketch, "E1559", {"center": v(14.87, 193.54) * mm, "radius": 1 * mm});
            skCircle(sketch, "E1560", {"center": v(14.92, 231.42) * mm, "radius": 1 * mm});
            skCircle(sketch, "E1561", {"center": v(14.52, 212.22) * mm, "radius": 1 * mm});
            skCircle(sketch, "E1562", {"center": v(-1.42, 155.78) * mm, "radius": 1 * mm});
            skCircle(sketch, "E1563", {"center": v(-1.47, 136.92) * mm, "radius": 1 * mm});
            skCircle(sketch, "E1564", {"center": v(-1.65, 174.91) * mm, "radius": 1 * mm});
            skCircle(sketch, "E1565", {"center": v(-1.32, 193.93) * mm, "radius": 1 * mm});
            skCircle(sketch, "E1566", {"center": v(-1.28, 231.8) * mm, "radius": 1 * mm});
            skCircle(sketch, "E1567", {"center": v(-1.68, 212.6) * mm, "radius": 1 * mm});
            skCircle(sketch, "E1568", {"center": v(-17.79, 155.42) * mm, "radius": 1 * mm});
            skCircle(sketch, "E1569", {"center": v(-17.84, 136.56) * mm, "radius": 1 * mm});
            skCircle(sketch, "E1570", {"center": v(-18.02, 174.55) * mm, "radius": 1 * mm});
            skCircle(sketch, "E1571", {"center": v(-17.69, 193.56) * mm, "radius": 1 * mm});
            skCircle(sketch, "E1572", {"center": v(-17.64, 231.43) * mm, "radius": 1 * mm});
            skCircle(sketch, "E1573", {"center": v(-18.04, 212.24) * mm, "radius": 1 * mm});
            skCircle(sketch, "E1574", {"center": v(-34.68, 155.52) * mm, "radius": 1 * mm});
            skCircle(sketch, "E1575", {"center": v(-34.72, 136.66) * mm, "radius": 1 * mm});
            skCircle(sketch, "E1576", {"center": v(-34.9, 174.65) * mm, "radius": 1 * mm});
            skCircle(sketch, "E1577", {"center": v(-34.58, 193.66) * mm, "radius": 1 * mm});
            skCircle(sketch, "E1578", {"center": v(-34.53, 231.54) * mm, "radius": 1 * mm});
            skCircle(sketch, "E1579", {"center": v(-34.93, 212.34) * mm, "radius": 1 * mm});
            skCircle(sketch, "E1580", {"center": v(-51.24, 155.77) * mm, "radius": 1 * mm});
            skCircle(sketch, "E1581", {"center": v(-51.29, 136.91) * mm, "radius": 1 * mm});
            skCircle(sketch, "E1582", {"center": v(-51.47, 174.9) * mm, "radius": 1 * mm});
            skCircle(sketch, "E1583", {"center": v(-51.14, 193.92) * mm, "radius": 1 * mm});
            skCircle(sketch, "E1584", {"center": v(-51.1, 231.8) * mm, "radius": 1 * mm});
            skCircle(sketch, "E1585", {"center": v(-51.5, 212.6) * mm, "radius": 1 * mm});
            skCircle(sketch, "E1586", {"center": v(-67.6, 155.4) * mm, "radius": 1 * mm});
            skCircle(sketch, "E1587", {"center": v(-67.65, 136.55) * mm, "radius": 1 * mm});
            skCircle(sketch, "E1588", {"center": v(-67.84, 174.54) * mm, "radius": 1 * mm});
            skCircle(sketch, "E1589", {"center": v(-67.5, 193.55) * mm, "radius": 1 * mm});
            skCircle(sketch, "E1590", {"center": v(-67.46, 231.42) * mm, "radius": 1 * mm});
            skCircle(sketch, "E1591", {"center": v(-67.86, 212.23) * mm, "radius": 1 * mm});
            skCircle(sketch, "E1592", {"center": v(-84.5, 155.5) * mm, "radius": 1 * mm});
            skCircle(sketch, "E1593", {"center": v(-84.54, 136.65) * mm, "radius": 1 * mm});
            skCircle(sketch, "E1594", {"center": v(-84.72, 174.64) * mm, "radius": 1 * mm});
            skCircle(sketch, "E1595", {"center": v(-84.4, 193.65) * mm, "radius": 1 * mm});
            skCircle(sketch, "E1596", {"center": v(-84.34, 231.53) * mm, "radius": 1 * mm});
            skCircle(sketch, "E1597", {"center": v(-84.75, 212.33) * mm, "radius": 1 * mm});
            skSolve(sketch);
        }
        {
            var Q0;
            Q0 = qSketchRegion(id + "F57", true);
            extrude(context, id + "F58", {"entities" : qUnion([Q0]), "operationType" : NewBodyOperationType.REMOVE, "oppositeDirection" : true, "depth" : 25 * mm, "offsetDistance" : 25 * mm});
        }
    });
